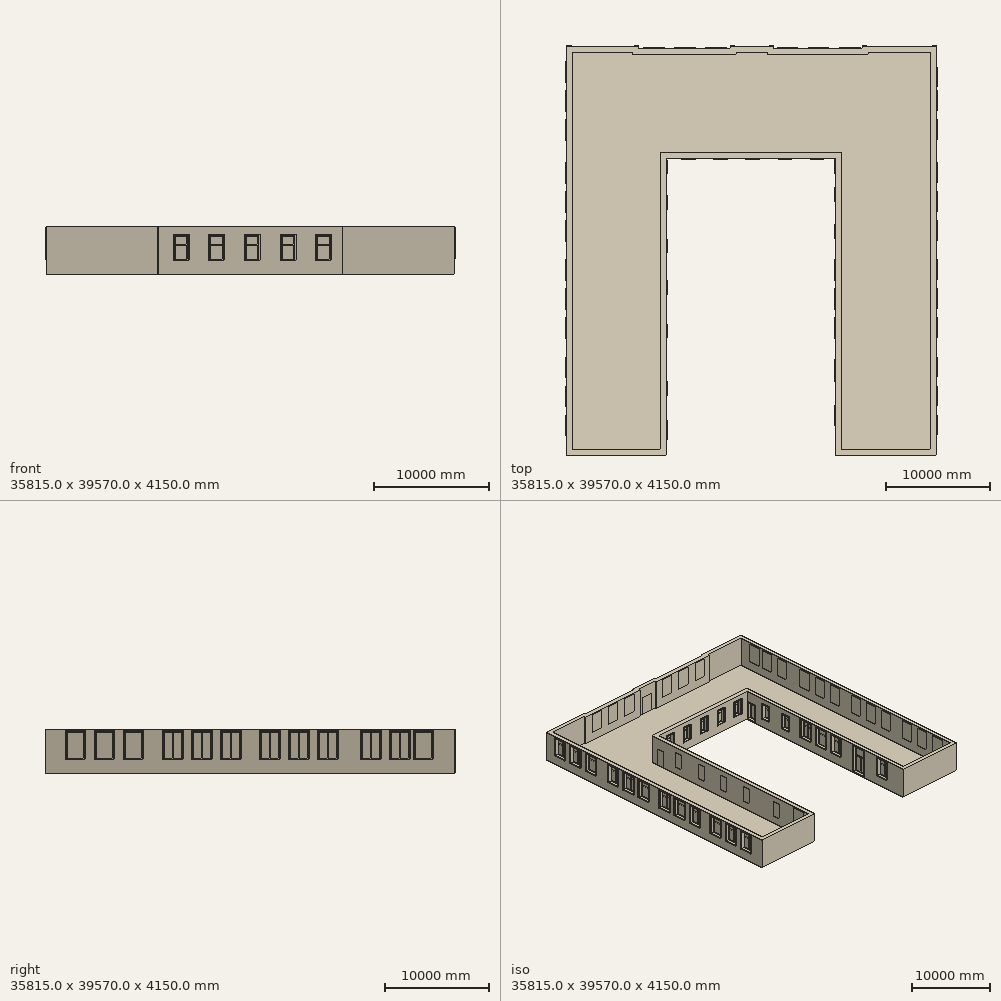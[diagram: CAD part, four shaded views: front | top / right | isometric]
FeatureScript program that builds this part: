
annotation { "Feature Type Name" : "Feature", "Feature Type Description" : "" }
export const myFeature = defineFeature(function(context is Context, id is Id, definition is map)
    precondition{}
    {
        {
            var Q0;
            Q0=qCreatedBy(makeId("Top.planeOp"),FACE);
            var sketch = newSketch(context, id + "F0", { "sketchPlane" : qUnion([Q0])});
            skLineSegment(sketch, "E0", {"start": v(0, 0) * mm, "end": v(0, 39360) * mm});
            skLineSegment(sketch, "E1", {"start": v(0, 39360) * mm, "end": v(-7000, 39360) * mm});
            skLineSegment(sketch, "E2", {"start": v(-7000, 39360) * mm, "end": v(-7000, 39160) * mm});
            skLineSegment(sketch, "E3", {"start": v(-7000, 39160) * mm, "end": v(-15730, 39160) * mm});
            skLineSegment(sketch, "E4", {"start": v(-15730, 39160) * mm, "end": v(-15730, 39360) * mm});
            skLineSegment(sketch, "E5", {"start": v(-15730, 39360) * mm, "end": v(-19730, 39360) * mm});
            skLineSegment(sketch, "E6", {"start": v(-19730, 39360) * mm, "end": v(-19730, 39160) * mm});
            skLineSegment(sketch, "E7", {"start": v(-19730, 39160) * mm, "end": v(-28730, 39160) * mm});
            skLineSegment(sketch, "E8", {"start": v(-28730, 39160) * mm, "end": v(-28730, 39360) * mm});
            skLineSegment(sketch, "E9", {"start": v(-28730, 39360) * mm, "end": v(-35480, 39360) * mm});
            skLineSegment(sketch, "E10", {"start": v(-35480, 39360) * mm, "end": v(-35480, 0) * mm});
            skLineSegment(sketch, "E11", {"start": v(-35480, 0) * mm, "end": v(-26000, 0) * mm});
            skLineSegment(sketch, "E12", {"start": v(-26000, 0) * mm, "end": v(-26000, 28660) * mm});
            skLineSegment(sketch, "E13", {"start": v(-26000, 28660) * mm, "end": v(-9600, 28660) * mm});
            skLineSegment(sketch, "E14", {"start": v(-9600, 28660) * mm, "end": v(-9600, 0) * mm});
            skLineSegment(sketch, "E15", {"start": v(-9600, 0) * mm, "end": v(0, 0) * mm});
            skLineSegment(sketch, "E16.0", {"start": v(-500, 500) * mm, "end": v(-500, 38860) * mm});
            skLineSegment(sketch, "E16.1", {"start": v(-9100, 500) * mm, "end": v(-500, 500) * mm});
            skLineSegment(sketch, "E16.2", {"start": v(-9100, 29160) * mm, "end": v(-9100, 500) * mm});
            skLineSegment(sketch, "E16.3", {"start": v(-26500, 29160) * mm, "end": v(-9100, 29160) * mm});
            skLineSegment(sketch, "E16.4", {"start": v(-26500, 500) * mm, "end": v(-26500, 29160) * mm});
            skLineSegment(sketch, "E16.5", {"start": v(-16230, 38860) * mm, "end": v(-19230, 38860) * mm});
            skLineSegment(sketch, "E16.6", {"start": v(-16230, 38660) * mm, "end": v(-16230, 38860) * mm});
            skLineSegment(sketch, "E16.7", {"start": v(-6500, 38660) * mm, "end": v(-16230, 38660) * mm});
            skLineSegment(sketch, "E16.8", {"start": v(-6500, 38860) * mm, "end": v(-6500, 38660) * mm});
            skLineSegment(sketch, "E16.9", {"start": v(-19230, 38860) * mm, "end": v(-19230, 38660) * mm});
            skLineSegment(sketch, "E16.10", {"start": v(-19230, 38660) * mm, "end": v(-29230, 38660) * mm});
            skLineSegment(sketch, "E16.11", {"start": v(-29230, 38660) * mm, "end": v(-29230, 38860) * mm});
            skLineSegment(sketch, "E16.12", {"start": v(-29230, 38860) * mm, "end": v(-34980, 38860) * mm});
            skLineSegment(sketch, "E16.13", {"start": v(-34980, 38860) * mm, "end": v(-34980, 500) * mm});
            skLineSegment(sketch, "E16.14", {"start": v(-500, 38860) * mm, "end": v(-6500, 38860) * mm});
            skLineSegment(sketch, "E16.15", {"start": v(-34980, 500) * mm, "end": v(-26500, 500) * mm});
            skLineSegment(sketch, "E17.0", {"start": v(-28640, 39250) * mm, "end": v(-28640, 39450) * mm});
            skLineSegment(sketch, "E17.1", {"start": v(-19820, 39250) * mm, "end": v(-28640, 39250) * mm});
            skLineSegment(sketch, "E17.2", {"start": v(-19820, 39450) * mm, "end": v(-19820, 39250) * mm});
            skLineSegment(sketch, "E17.3", {"start": v(-15640, 39450) * mm, "end": v(-19820, 39450) * mm});
            skLineSegment(sketch, "E17.4", {"start": v(-15640, 39250) * mm, "end": v(-15640, 39450) * mm});
            skLineSegment(sketch, "E17.5", {"start": v(-25910, 28570) * mm, "end": v(-9690, 28570) * mm});
            skLineSegment(sketch, "E17.6", {"start": v(-25910, -90) * mm, "end": v(-25910, 28570) * mm});
            skLineSegment(sketch, "E17.7", {"start": v(-35570, -90) * mm, "end": v(-25910, -90) * mm});
            skLineSegment(sketch, "E17.8", {"start": v(-35570, 39450) * mm, "end": v(-35570, -90) * mm});
            skLineSegment(sketch, "E17.9", {"start": v(-9690, 28570) * mm, "end": v(-9690, -90) * mm});
            skLineSegment(sketch, "E17.10", {"start": v(-9690, -90) * mm, "end": v(90, -90) * mm});
            skLineSegment(sketch, "E17.11", {"start": v(90, -90) * mm, "end": v(90, 39450) * mm});
            skLineSegment(sketch, "E17.12", {"start": v(90, 39450) * mm, "end": v(-7090, 39450) * mm});
            skLineSegment(sketch, "E17.13", {"start": v(-7090, 39450) * mm, "end": v(-7090, 39250) * mm});
            skLineSegment(sketch, "E17.14", {"start": v(-28640, 39450) * mm, "end": v(-35570, 39450) * mm});
            skLineSegment(sketch, "E17.15", {"start": v(-7090, 39250) * mm, "end": v(-15640, 39250) * mm});
            skSolve(sketch);
        }
        {
            var Q0;
            Q0=qSketchRegion(id+"F0",true);
            var Q1;
            Q1=makeQuery(id+"F0.imprint","IMPRINT",FACE,{"disambiguationData":[TD([[makeQuery(id+"F0.imprint","IMPRINT",EDGE,{"derivedFrom":sQuery(id+"F0.wireOp",EDGE,"E0")}),1.0]])]});
            extrude(context, id + "F1", {"entities" : qUnion([Q0, Q1]), "depth" : 4000 * mm, "offsetDistance" : 25 * mm});
        }
        {
            var Q0;
            Q0=makeQuery(id+"F1.opExtrude","CAP_FACE",FACE,{"disambiguationData":[OSD([sQuery(id+"F0.wireOp",EDGE,"E16.0"),sQuery(id+"F0.wireOp",EDGE,"E16.1"),sQuery(id+"F0.wireOp",EDGE,"E16.2"),sQuery(id+"F0.wireOp",EDGE,"E16.3"),sQuery(id+"F0.wireOp",EDGE,"E16.4"),sQuery(id+"F0.wireOp",EDGE,"E16.5"),sQuery(id+"F0.wireOp",EDGE,"E16.6"),sQuery(id+"F0.wireOp",EDGE,"E16.7"),sQuery(id+"F0.wireOp",EDGE,"E16.8"),sQuery(id+"F0.wireOp",EDGE,"E16.9"),sQuery(id+"F0.wireOp",EDGE,"E16.10"),sQuery(id+"F0.wireOp",EDGE,"E16.11"),sQuery(id+"F0.wireOp",EDGE,"E16.12"),sQuery(id+"F0.wireOp",EDGE,"E16.13"),sQuery(id+"F0.wireOp",EDGE,"E16.14"),sQuery(id+"F0.wireOp",EDGE,"E16.15"),sQuery(id+"F0.wireOp",EDGE,"E17.0"),sQuery(id+"F0.wireOp",EDGE,"E17.1"),sQuery(id+"F0.wireOp",EDGE,"E17.2"),sQuery(id+"F0.wireOp",EDGE,"E17.3"),sQuery(id+"F0.wireOp",EDGE,"E17.4"),sQuery(id+"F0.wireOp",EDGE,"E17.5"),sQuery(id+"F0.wireOp",EDGE,"E17.6"),sQuery(id+"F0.wireOp",EDGE,"E17.7"),sQuery(id+"F0.wireOp",EDGE,"E17.8"),sQuery(id+"F0.wireOp",EDGE,"E17.9"),sQuery(id+"F0.wireOp",EDGE,"E17.10"),sQuery(id+"F0.wireOp",EDGE,"E17.11"),sQuery(id+"F0.wireOp",EDGE,"E17.12"),sQuery(id+"F0.wireOp",EDGE,"E17.13"),sQuery(id+"F0.wireOp",EDGE,"E17.14"),sQuery(id+"F0.wireOp",EDGE,"E17.15")])],"isStart":false});
            var sketch = newSketch(context, id + "F2", { "sketchPlane" : qUnion([Q0])});
            skLineSegment(sketch, "E18.0.0", {"start": v(-9690, 28570) * mm, "end": v(-9690, -90) * mm});
            skLineSegment(sketch, "E18.0.1", {"start": v(-9690, -90) * mm, "end": v(90, -90) * mm});
            skLineSegment(sketch, "E18.0.2", {"start": v(90, -90) * mm, "end": v(90, 39450) * mm});
            skLineSegment(sketch, "E18.0.3", {"start": v(90, 39450) * mm, "end": v(-7090, 39450) * mm});
            skLineSegment(sketch, "E18.0.4", {"start": v(-7090, 39450) * mm, "end": v(-7090, 39250) * mm});
            skLineSegment(sketch, "E18.0.5", {"start": v(-7090, 39250) * mm, "end": v(-15640, 39250) * mm});
            skLineSegment(sketch, "E18.0.6", {"start": v(-15640, 39250) * mm, "end": v(-15640, 39450) * mm});
            skLineSegment(sketch, "E18.0.7", {"start": v(-15640, 39450) * mm, "end": v(-19820, 39450) * mm});
            skLineSegment(sketch, "E18.0.8", {"start": v(-19820, 39450) * mm, "end": v(-19820, 39250) * mm});
            skLineSegment(sketch, "E18.0.9", {"start": v(-19820, 39250) * mm, "end": v(-28640, 39250) * mm});
            skLineSegment(sketch, "E18.0.10", {"start": v(-28640, 39250) * mm, "end": v(-28640, 39450) * mm});
            skLineSegment(sketch, "E18.0.11", {"start": v(-28640, 39450) * mm, "end": v(-35570, 39450) * mm});
            skLineSegment(sketch, "E18.0.12", {"start": v(-35570, 39450) * mm, "end": v(-35570, -90) * mm});
            skLineSegment(sketch, "E18.0.13", {"start": v(-35570, -90) * mm, "end": v(-25910, -90) * mm});
            skLineSegment(sketch, "E18.0.14", {"start": v(-25910, -90) * mm, "end": v(-25910, 28570) * mm});
            skLineSegment(sketch, "E18.0.15", {"start": v(-25910, 28570) * mm, "end": v(-9690, 28570) * mm});
            skLineSegment(sketch, "E19.0", {"start": v(-19810, 39440) * mm, "end": v(-19810, 39240) * mm});
            skLineSegment(sketch, "E19.1", {"start": v(-15650, 39440) * mm, "end": v(-19810, 39440) * mm});
            skLineSegment(sketch, "E19.2", {"start": v(-15650, 39240) * mm, "end": v(-15650, 39440) * mm});
            skLineSegment(sketch, "E19.3", {"start": v(-7080, 39240) * mm, "end": v(-15650, 39240) * mm});
            skLineSegment(sketch, "E19.4", {"start": v(-7080, 39440) * mm, "end": v(-7080, 39240) * mm});
            skLineSegment(sketch, "E19.5", {"start": v(-35560, -80) * mm, "end": v(-25920, -80) * mm});
            skLineSegment(sketch, "E19.6", {"start": v(-35560, 39440) * mm, "end": v(-35560, -80) * mm});
            skLineSegment(sketch, "E19.7", {"start": v(-28650, 39440) * mm, "end": v(-35560, 39440) * mm});
            skLineSegment(sketch, "E19.8", {"start": v(-28650, 39240) * mm, "end": v(-28650, 39440) * mm});
            skLineSegment(sketch, "E19.9", {"start": v(-25920, -80) * mm, "end": v(-25920, 28580) * mm});
            skLineSegment(sketch, "E19.10", {"start": v(-25920, 28580) * mm, "end": v(-9680, 28580) * mm});
            skLineSegment(sketch, "E19.11", {"start": v(-9680, 28580) * mm, "end": v(-9680, -80) * mm});
            skLineSegment(sketch, "E19.12", {"start": v(-9680, -80) * mm, "end": v(80, -80) * mm});
            skLineSegment(sketch, "E19.13", {"start": v(80, -80) * mm, "end": v(80, 39440) * mm});
            skLineSegment(sketch, "E19.14", {"start": v(-19810, 39240) * mm, "end": v(-28650, 39240) * mm});
            skLineSegment(sketch, "E19.15", {"start": v(80, 39440) * mm, "end": v(-7080, 39440) * mm});
            skSolve(sketch);
        }
        {
            var Q0;
            Q0 = qSketchRegion(id + "F2", true);
            var Q1;
            Q1=makeQuery(id+"F1.opExtrude","CAP_VERTEX",VERTEX,{"disambiguationData":[OSD([sQuery(id+"F0.wireOp",EDGE,"E17.8"),sQuery(id+"F0.wireOp",EDGE,"E17.14")])],"isStart":true});
            extrude(context, id + "F3", {"entities" : qUnion([Q0]), "operationType" : NewBodyOperationType.REMOVE, "endBound" : BoundingType.UP_TO_VERTEX, "oppositeDirection" : true, "depth" : 25 * mm, "endBoundEntityVertex" : qUnion([Q1]), "offsetDistance" : 25 * mm});
        }
        {
            var Q0;
            Q0=makeQuery(id+"F1.opExtrude","CAP_FACE",FACE,{"disambiguationData":[OSD([sQuery(id+"F0.wireOp",EDGE,"E0"),sQuery(id+"F0.wireOp",EDGE,"E1"),sQuery(id+"F0.wireOp",EDGE,"E2"),sQuery(id+"F0.wireOp",EDGE,"E3"),sQuery(id+"F0.wireOp",EDGE,"E4"),sQuery(id+"F0.wireOp",EDGE,"E5"),sQuery(id+"F0.wireOp",EDGE,"E6"),sQuery(id+"F0.wireOp",EDGE,"E7"),sQuery(id+"F0.wireOp",EDGE,"E8"),sQuery(id+"F0.wireOp",EDGE,"E9"),sQuery(id+"F0.wireOp",EDGE,"E10"),sQuery(id+"F0.wireOp",EDGE,"E11"),sQuery(id+"F0.wireOp",EDGE,"E12"),sQuery(id+"F0.wireOp",EDGE,"E13"),sQuery(id+"F0.wireOp",EDGE,"E14"),sQuery(id+"F0.wireOp",EDGE,"E15"),sQuery(id+"F0.wireOp",EDGE,"E16.0"),sQuery(id+"F0.wireOp",EDGE,"E16.1"),sQuery(id+"F0.wireOp",EDGE,"E16.2"),sQuery(id+"F0.wireOp",EDGE,"E16.3"),sQuery(id+"F0.wireOp",EDGE,"E16.4"),sQuery(id+"F0.wireOp",EDGE,"E16.5"),sQuery(id+"F0.wireOp",EDGE,"E16.6"),sQuery(id+"F0.wireOp",EDGE,"E16.7"),sQuery(id+"F0.wireOp",EDGE,"E16.8"),sQuery(id+"F0.wireOp",EDGE,"E16.9"),sQuery(id+"F0.wireOp",EDGE,"E16.10"),sQuery(id+"F0.wireOp",EDGE,"E16.11"),sQuery(id+"F0.wireOp",EDGE,"E16.12"),sQuery(id+"F0.wireOp",EDGE,"E16.13"),sQuery(id+"F0.wireOp",EDGE,"E16.14"),sQuery(id+"F0.wireOp",EDGE,"E16.15")])],"isStart":true});
            var sketch = newSketch(context, id + "F4", { "sketchPlane" : qUnion([Q0])});
            skLineSegment(sketch, "E20", {"start": v(-35560, -39440) * mm, "end": v(-35560, 80) * mm});
            skLineSegment(sketch, "E21", {"start": v(-15650, -39440) * mm, "end": v(-19810, -39440) * mm});
            skLineSegment(sketch, "E22", {"start": v(-19810, -39440) * mm, "end": v(-19810, -39240) * mm});
            skLineSegment(sketch, "E23", {"start": v(-19810, -39240) * mm, "end": v(-28650, -39240) * mm});
            skLineSegment(sketch, "E24", {"start": v(-28650, -39240) * mm, "end": v(-28650, -39440) * mm});
            skLineSegment(sketch, "E25", {"start": v(-28650, -39440) * mm, "end": v(-35560, -39440) * mm});
            skLineSegment(sketch, "E26.0", {"start": v(-15650, -39240) * mm, "end": v(-15650, -39440) * mm});
            skLineSegment(sketch, "E27.0", {"start": v(-7080, -39240) * mm, "end": v(-15650, -39240) * mm});
            skLineSegment(sketch, "E28.0", {"start": v(-7080, -39440) * mm, "end": v(-7080, -39240) * mm});
            skLineSegment(sketch, "E29.0", {"start": v(80, -39440) * mm, "end": v(-7080, -39440) * mm});
            skLineSegment(sketch, "E30.0", {"start": v(80, 80) * mm, "end": v(80, -39440) * mm});
            skLineSegment(sketch, "E31.0", {"start": v(-9680, 80) * mm, "end": v(80, 80) * mm});
            skLineSegment(sketch, "E32.0", {"start": v(-9680, -28580) * mm, "end": v(-9680, 80) * mm});
            skLineSegment(sketch, "E33.0", {"start": v(-25920, -28580) * mm, "end": v(-9680, -28580) * mm});
            skLineSegment(sketch, "E34.0", {"start": v(-25920, 80) * mm, "end": v(-25920, -28580) * mm});
            skLineSegment(sketch, "E35.0", {"start": v(-35560, 80) * mm, "end": v(-25920, 80) * mm});
            skSolve(sketch);
        }
        {
            var Q0;
            {var subQ0=makeQuery(id+"F1.opExtrude","CAP_EDGE",EDGE,{"disambiguationData":[OSD([sQuery(id+"F0.wireOp",EDGE,"E16.10")])],"isStart":true});Q0=makeQuery(id+"F4.imprint","IMPRINT",FACE,{"disambiguationData":[TD([[makeQuery(id+"F4.imprint","IMPRINT",EDGE,{"derivedFrom":subQ0}),-1.0]])]});}
            var Q1;
            {var subQ8=sQuery(id+"F4.wireOp",EDGE,"E20");Q1=makeQuery(id+"F4.imprint","IMPRINT",FACE,{"disambiguationData":[TD([[makeQuery(id+"F4.imprint","IMPRINT",EDGE,{"derivedFrom":subQ8}),-1.0]])]});}
            var Q2;
            {var subQ5=sQuery(id+"F4.wireOp",EDGE,"WrZoUcTY-9wdJ-lOnS-oAZQ-S74aqCpjquS9");var subQ6=makeQuery(id+"F4.imprint","INTERSECT",VERTEX,{"derivedFrom":[makeQuery(id+"F1.opExtrude","CAP_EDGE",EDGE,{"disambiguationData":[OSD([sQuery(id+"F0.wireOp",EDGE,"E12")])],"isStart":true}),subQ5]});Q2=makeQuery(id+"F4.imprint","IMPRINT",FACE,{"disambiguationData":[TD([[makeQuery(id+"F4.imprint","IMPRINT",EDGE,{"disambiguationData":[TD([[subQ6,1.0]])],"derivedFrom":subQ5}),-1.0]])]});}
            extrude(context, id + "F5", {"entities" : qUnion([Q0, Q1, Q2]), "operationType" : NewBodyOperationType.ADD, "depth" : 150 * mm, "offsetDistance" : 25 * mm});
        }
        {
            var Q0;
            Q0=makeQuery(id+"F5.boolean.opBoolean","MERGE",FACE,{"derivedFrom":[makeQuery(id+"F1.opExtrude","SWEPT_FACE",FACE,{"disambiguationData":[OSD([sQuery(id+"F0.wireOp",EDGE,"E7")])]}),makeQuery(id+"F5.opExtrude","SWEPT_FACE",FACE,{"disambiguationData":[OSD([sQuery(id+"F4.wireOp",EDGE,"E23")])]})]});
            var sketch = newSketch(context, id + "F6", { "sketchPlane" : qUnion([Q0])});
            skLineSegment(sketch, "E36.bottom", {"start": v(20330, 3800) * mm, "end": v(22030, 3800) * mm});
            skLineSegment(sketch, "E36.top", {"start": v(20330, 1200) * mm, "end": v(22030, 1200) * mm});
            skLineSegment(sketch, "E36.left", {"start": v(20330, 3800) * mm, "end": v(20330, 1200) * mm});
            skLineSegment(sketch, "E36.right", {"start": v(22030, 3800) * mm, "end": v(22030, 1200) * mm});
            skLineSegment(sketch, "E37.bottom", {"start": v(23330, 3800) * mm, "end": v(25030, 3800) * mm});
            skLineSegment(sketch, "E37.top", {"start": v(23330, 1200) * mm, "end": v(25030, 1200) * mm});
            skLineSegment(sketch, "E37.left", {"start": v(23330, 3800) * mm, "end": v(23330, 1200) * mm});
            skLineSegment(sketch, "E37.right", {"start": v(25030, 3800) * mm, "end": v(25030, 1200) * mm});
            skLineSegment(sketch, "E38.bottom", {"start": v(26330, 3800) * mm, "end": v(28030, 3800) * mm});
            skLineSegment(sketch, "E38.top", {"start": v(26330, 1200) * mm, "end": v(28030, 1200) * mm});
            skLineSegment(sketch, "E38.left", {"start": v(26330, 3800) * mm, "end": v(26330, 1200) * mm});
            skLineSegment(sketch, "E38.right", {"start": v(28030, 3800) * mm, "end": v(28030, 1200) * mm});
            skLineSegment(sketch, "E39", {"start": v(17730, -150) * mm, "end": v(17730, 3306.36) * mm, "construction": true});
            skLineSegment(sketch, "E40.MirrorCS", {"start": v(15130, 3800) * mm, "end": v(15130, 1200) * mm});
            skLineSegment(sketch, "E41.MirrorCS", {"start": v(7430, 3800) * mm, "end": v(7430, 1200) * mm});
            skLineSegment(sketch, "E42.MirrorCS", {"start": v(10430, 3800) * mm, "end": v(10430, 1200) * mm});
            skLineSegment(sketch, "E43.MirrorCS", {"start": v(9130, 3800) * mm, "end": v(9130, 1200) * mm});
            skLineSegment(sketch, "E44.MirrorCS", {"start": v(9130, 3800) * mm, "end": v(7430, 3800) * mm});
            skLineSegment(sketch, "E45.MirrorCS", {"start": v(12130, 3800) * mm, "end": v(12130, 1200) * mm});
            skLineSegment(sketch, "E46.MirrorCS", {"start": v(12130, 1200) * mm, "end": v(10430, 1200) * mm});
            skLineSegment(sketch, "E47.MirrorCS", {"start": v(15130, 3800) * mm, "end": v(13430, 3800) * mm});
            skLineSegment(sketch, "E48.MirrorCS", {"start": v(15130, 1200) * mm, "end": v(13430, 1200) * mm});
            skLineSegment(sketch, "E49.MirrorCS", {"start": v(9130, 1200) * mm, "end": v(7430, 1200) * mm});
            skLineSegment(sketch, "E50.MirrorCS", {"start": v(13430, 3800) * mm, "end": v(13430, 1200) * mm});
            skLineSegment(sketch, "E51.MirrorCS", {"start": v(12130, 3800) * mm, "end": v(10430, 3800) * mm});
            skSolve(sketch);
        }
        {
            var Q0;
            Q0=qSketchRegion(id+"F6",true);
            extrude(context, id + "F7", {"entities" : qUnion([Q0]), "operationType" : NewBodyOperationType.REMOVE, "oppositeDirection" : true, "depth" : 590 * mm, "offsetDistance" : 25 * mm});
        }
        {
            var Q0;
            Q0=makeQuery(id+"F1.opExtrude","SWEPT_FACE",FACE,{"disambiguationData":[OSD([sQuery(id+"F0.wireOp",EDGE,"E16.10")])]});
            var sketch = newSketch(context, id + "F8", { "sketchPlane" : qUnion([Q0])});
            skLineSegment(sketch, "E52.0", {"start": v(-20330, 3800) * mm, "end": v(-22030, 3800) * mm});
            skLineSegment(sketch, "E53.0", {"start": v(-20330, 3800) * mm, "end": v(-20330, 1200) * mm});
            skLineSegment(sketch, "E54.0", {"start": v(-20330, 1200) * mm, "end": v(-22030, 1200) * mm});
            skLineSegment(sketch, "E55.0", {"start": v(-22030, 3800) * mm, "end": v(-22030, 1200) * mm});
            skLineSegment(sketch, "E56.0", {"start": v(-23330, 3800) * mm, "end": v(-23330, 1200) * mm});
            skLineSegment(sketch, "E57.0", {"start": v(-23330, 3800) * mm, "end": v(-25030, 3800) * mm});
            skLineSegment(sketch, "E58.0", {"start": v(-25030, 3800) * mm, "end": v(-25030, 1200) * mm});
            skLineSegment(sketch, "E59.0", {"start": v(-23330, 1200) * mm, "end": v(-25030, 1200) * mm});
            skLineSegment(sketch, "E60.0", {"start": v(-26330, 3800) * mm, "end": v(-28030, 3800) * mm});
            skLineSegment(sketch, "E61.0", {"start": v(-28030, 3800) * mm, "end": v(-28030, 1200) * mm});
            skLineSegment(sketch, "E62.0", {"start": v(-26330, 1200) * mm, "end": v(-28030, 1200) * mm});
            skLineSegment(sketch, "E63.0", {"start": v(-26330, 3800) * mm, "end": v(-26330, 1200) * mm});
            skLineSegment(sketch, "E64.0", {"start": v(-9130, 1200) * mm, "end": v(-7430, 1200) * mm});
            skLineSegment(sketch, "E65.0", {"start": v(-7430, 3800) * mm, "end": v(-7430, 1200) * mm});
            skLineSegment(sketch, "E66.0", {"start": v(-9130, 3800) * mm, "end": v(-7430, 3800) * mm});
            skLineSegment(sketch, "E67.0", {"start": v(-9130, 3800) * mm, "end": v(-9130, 1200) * mm});
            skLineSegment(sketch, "E68.0", {"start": v(-12130, 1200) * mm, "end": v(-10430, 1200) * mm});
            skLineSegment(sketch, "E69.0", {"start": v(-10430, 3800) * mm, "end": v(-10430, 1200) * mm});
            skLineSegment(sketch, "E70.0", {"start": v(-12130, 3800) * mm, "end": v(-10430, 3800) * mm});
            skLineSegment(sketch, "E71.0", {"start": v(-12130, 3800) * mm, "end": v(-12130, 1200) * mm});
            skLineSegment(sketch, "E72.0", {"start": v(-15130, 1200) * mm, "end": v(-13430, 1200) * mm});
            skLineSegment(sketch, "E73.0", {"start": v(-13430, 3800) * mm, "end": v(-13430, 1200) * mm});
            skLineSegment(sketch, "E74.0", {"start": v(-15130, 3800) * mm, "end": v(-13430, 3800) * mm});
            skLineSegment(sketch, "E75.0", {"start": v(-15130, 3800) * mm, "end": v(-15130, 1200) * mm});
            skSolve(sketch);
        }
        {
            var Q0;
            Q0=qSketchRegion(id+"F8",true);
            extrude(context, id + "F9", {"entities" : qUnion([Q0]), "oppositeDirection" : true, "depth" : 5 * mm, "offsetDistance" : 25 * mm});
        }
        {
            var Q0;
            Q0=makeQuery(id+"F9.opExtrude","CAP_FACE",FACE,{"disambiguationData":[OSD([sQuery(id+"F8.wireOp",EDGE,"E60.0"),sQuery(id+"F8.wireOp",EDGE,"E61.0"),sQuery(id+"F8.wireOp",EDGE,"E62.0"),sQuery(id+"F8.wireOp",EDGE,"E63.0")])],"isStart":false});
            var sketch = newSketch(context, id + "F10", { "sketchPlane" : qUnion([Q0])});
            skLineSegment(sketch, "E76.0.0", {"start": v(9130, 3800) * mm, "end": v(7430, 3800) * mm});
            skLineSegment(sketch, "E76.0.1", {"start": v(7430, 3800) * mm, "end": v(7430, 1200) * mm});
            skLineSegment(sketch, "E76.0.2", {"start": v(7430, 1200) * mm, "end": v(9130, 1200) * mm});
            skLineSegment(sketch, "E76.0.3", {"start": v(9130, 1200) * mm, "end": v(9130, 3800) * mm});
            skLineSegment(sketch, "E77", {"start": v(8280, 3800) * mm, "end": v(8280, 1200) * mm, "construction": true});
            skLineSegment(sketch, "E78.bottom", {"start": v(7480, 2850) * mm, "end": v(8242.5, 2850) * mm});
            skLineSegment(sketch, "E78.top", {"start": v(7480, 1250) * mm, "end": v(8242.5, 1250) * mm});
            skLineSegment(sketch, "E78.left", {"start": v(7480, 2850) * mm, "end": v(7480, 1250) * mm});
            skLineSegment(sketch, "E78.right", {"start": v(8242.5, 2850) * mm, "end": v(8242.5, 1250) * mm});
            skLineSegment(sketch, "E79.bottom", {"start": v(7480, 2900) * mm, "end": v(8242.5, 2900) * mm});
            skLineSegment(sketch, "E79.top", {"start": v(7480, 3750) * mm, "end": v(8242.5, 3750) * mm});
            skLineSegment(sketch, "E79.left", {"start": v(7480, 2900) * mm, "end": v(7480, 3750) * mm});
            skLineSegment(sketch, "E79.right", {"start": v(8242.5, 2900) * mm, "end": v(8242.5, 3750) * mm});
            skLineSegment(sketch, "E80.MirrorCS", {"start": v(9080, 3750) * mm, "end": v(8317.5, 3750) * mm});
            skLineSegment(sketch, "E81.MirrorCS", {"start": v(9080, 2900) * mm, "end": v(9080, 3750) * mm});
            skLineSegment(sketch, "E82.MirrorCS", {"start": v(8317.5, 2900) * mm, "end": v(8317.5, 3750) * mm});
            skLineSegment(sketch, "E83.MirrorCS", {"start": v(9080, 2900) * mm, "end": v(8317.5, 2900) * mm});
            skLineSegment(sketch, "E84.MirrorCS", {"start": v(9080, 2850) * mm, "end": v(8317.5, 2850) * mm});
            skLineSegment(sketch, "E85.MirrorCS", {"start": v(8317.5, 2850) * mm, "end": v(8317.5, 1250) * mm});
            skLineSegment(sketch, "E86.MirrorCS", {"start": v(9080, 2850) * mm, "end": v(9080, 1250) * mm});
            skLineSegment(sketch, "E87.MirrorCS", {"start": v(9080, 1250) * mm, "end": v(8317.5, 1250) * mm});
            skLineSegment(sketch, "E88.0.0", {"start": v(12129.64, 3800) * mm, "end": v(10429.64, 3800) * mm});
            skLineSegment(sketch, "E88.0.1", {"start": v(10429.64, 3800) * mm, "end": v(10429.64, 1200) * mm});
            skLineSegment(sketch, "E88.0.2", {"start": v(10429.64, 1200) * mm, "end": v(12129.64, 1200) * mm});
            skLineSegment(sketch, "E88.0.3", {"start": v(12129.64, 1200) * mm, "end": v(12129.64, 3800) * mm});
            skLineSegment(sketch, "E89", {"start": v(11279.64, 3800) * mm, "end": v(11279.64, 1200) * mm, "construction": true});
            skLineSegment(sketch, "E90.bottom", {"start": v(10479.64, 2850) * mm, "end": v(11242.14, 2850) * mm});
            skLineSegment(sketch, "E90.top", {"start": v(10479.64, 1250) * mm, "end": v(11242.14, 1250) * mm});
            skLineSegment(sketch, "E90.left", {"start": v(10479.64, 2850) * mm, "end": v(10479.64, 1250) * mm});
            skLineSegment(sketch, "E90.right", {"start": v(11242.14, 2850) * mm, "end": v(11242.14, 1250) * mm});
            skLineSegment(sketch, "E91.bottom", {"start": v(10479.64, 2900) * mm, "end": v(11242.14, 2900) * mm});
            skLineSegment(sketch, "E91.top", {"start": v(10479.64, 3750) * mm, "end": v(11242.14, 3750) * mm});
            skLineSegment(sketch, "E91.left", {"start": v(10479.64, 2900) * mm, "end": v(10479.64, 3750) * mm});
            skLineSegment(sketch, "E91.right", {"start": v(11242.14, 2900) * mm, "end": v(11242.14, 3750) * mm});
            skLineSegment(sketch, "E92.MirrorCS", {"start": v(12079.64, 3750) * mm, "end": v(11317.14, 3750) * mm});
            skLineSegment(sketch, "E93.MirrorCS", {"start": v(12079.64, 2900) * mm, "end": v(12079.64, 3750) * mm});
            skLineSegment(sketch, "E94.MirrorCS", {"start": v(11317.14, 2900) * mm, "end": v(11317.14, 3750) * mm});
            skLineSegment(sketch, "E95.MirrorCS", {"start": v(12079.64, 2900) * mm, "end": v(11317.14, 2900) * mm});
            skLineSegment(sketch, "E96.MirrorCS", {"start": v(12079.64, 2850) * mm, "end": v(11317.14, 2850) * mm});
            skLineSegment(sketch, "E97.MirrorCS", {"start": v(11317.14, 2850) * mm, "end": v(11317.14, 1250) * mm});
            skLineSegment(sketch, "E98.MirrorCS", {"start": v(12079.64, 2850) * mm, "end": v(12079.64, 1250) * mm});
            skLineSegment(sketch, "E99.MirrorCS", {"start": v(12079.64, 1250) * mm, "end": v(11317.14, 1250) * mm});
            skLineSegment(sketch, "E100.0.0", {"start": v(15130, 3800) * mm, "end": v(13430, 3800) * mm});
            skLineSegment(sketch, "E100.0.1", {"start": v(13430, 3800) * mm, "end": v(13430, 1200) * mm});
            skLineSegment(sketch, "E100.0.2", {"start": v(13430, 1200) * mm, "end": v(15130, 1200) * mm});
            skLineSegment(sketch, "E100.0.3", {"start": v(15130, 1200) * mm, "end": v(15130, 3800) * mm});
            skLineSegment(sketch, "E101", {"start": v(14280, 3800) * mm, "end": v(14280, 1200) * mm, "construction": true});
            skLineSegment(sketch, "E102.bottom", {"start": v(13480, 2850) * mm, "end": v(14242.5, 2850) * mm});
            skLineSegment(sketch, "E102.top", {"start": v(13480, 1250) * mm, "end": v(14242.5, 1250) * mm});
            skLineSegment(sketch, "E102.left", {"start": v(13480, 2850) * mm, "end": v(13480, 1250) * mm});
            skLineSegment(sketch, "E102.right", {"start": v(14242.5, 2850) * mm, "end": v(14242.5, 1250) * mm});
            skLineSegment(sketch, "E103.bottom", {"start": v(13480, 2900) * mm, "end": v(14242.5, 2900) * mm});
            skLineSegment(sketch, "E103.top", {"start": v(13480, 3750) * mm, "end": v(14242.5, 3750) * mm});
            skLineSegment(sketch, "E103.left", {"start": v(13480, 2900) * mm, "end": v(13480, 3750) * mm});
            skLineSegment(sketch, "E103.right", {"start": v(14242.5, 2900) * mm, "end": v(14242.5, 3750) * mm});
            skLineSegment(sketch, "E104.MirrorCS", {"start": v(15080, 3750) * mm, "end": v(14317.5, 3750) * mm});
            skLineSegment(sketch, "E105.MirrorCS", {"start": v(15080, 2900) * mm, "end": v(15080, 3750) * mm});
            skLineSegment(sketch, "E106.MirrorCS", {"start": v(14317.5, 2900) * mm, "end": v(14317.5, 3750) * mm});
            skLineSegment(sketch, "E107.MirrorCS", {"start": v(15080, 2900) * mm, "end": v(14317.5, 2900) * mm});
            skLineSegment(sketch, "E108.MirrorCS", {"start": v(15080, 2850) * mm, "end": v(14317.5, 2850) * mm});
            skLineSegment(sketch, "E109.MirrorCS", {"start": v(14317.5, 2850) * mm, "end": v(14317.5, 1250) * mm});
            skLineSegment(sketch, "E110.MirrorCS", {"start": v(15080, 2850) * mm, "end": v(15080, 1250) * mm});
            skLineSegment(sketch, "E111.MirrorCS", {"start": v(15080, 1250) * mm, "end": v(14317.5, 1250) * mm});
            skLineSegment(sketch, "E112", {"start": v(17730, -150) * mm, "end": v(17730, 2939.63) * mm, "construction": true});
            skLineSegment(sketch, "E113.MirrorCS", {"start": v(21142.5, 2900) * mm, "end": v(21142.5, 3750) * mm});
            skLineSegment(sketch, "E114.MirrorCS", {"start": v(25030.36, 1200) * mm, "end": v(23330.36, 1200) * mm});
            skLineSegment(sketch, "E115.MirrorCS", {"start": v(27217.5, 2900) * mm, "end": v(27217.5, 3750) * mm});
            skLineSegment(sketch, "E116.MirrorCS", {"start": v(24217.86, 2900) * mm, "end": v(24217.86, 3750) * mm});
            skLineSegment(sketch, "E117.MirrorCS", {"start": v(21980, 2900) * mm, "end": v(21980, 3750) * mm});
            skLineSegment(sketch, "E118.MirrorCS", {"start": v(27217.5, 2850) * mm, "end": v(27217.5, 1250) * mm});
            skLineSegment(sketch, "E119.MirrorCS", {"start": v(21980, 2850) * mm, "end": v(21980, 1250) * mm});
            skLineSegment(sketch, "E120.MirrorCS", {"start": v(21142.5, 2850) * mm, "end": v(21142.5, 1250) * mm});
            skLineSegment(sketch, "E121.MirrorCS", {"start": v(22030, 1200) * mm, "end": v(20330, 1200) * mm});
            skLineSegment(sketch, "E122.MirrorCS", {"start": v(28030, 1200) * mm, "end": v(26330, 1200) * mm});
            skLineSegment(sketch, "E123.MirrorCS", {"start": v(24217.86, 2850) * mm, "end": v(24217.86, 1250) * mm});
            skLineSegment(sketch, "E124.MirrorCS", {"start": v(23380.36, 1250) * mm, "end": v(24142.86, 1250) * mm});
            skLineSegment(sketch, "E125.MirrorCS", {"start": v(27980, 2850) * mm, "end": v(27980, 1250) * mm});
            skLineSegment(sketch, "E126.MirrorCS", {"start": v(27980, 1250) * mm, "end": v(27217.5, 1250) * mm});
            skLineSegment(sketch, "E127.MirrorCS", {"start": v(23380.36, 2850) * mm, "end": v(24142.86, 2850) * mm});
            skLineSegment(sketch, "E128.MirrorCS", {"start": v(24980.36, 3750) * mm, "end": v(24217.86, 3750) * mm});
            skLineSegment(sketch, "E129.MirrorCS", {"start": v(20380, 2900) * mm, "end": v(21142.5, 2900) * mm});
            skLineSegment(sketch, "E130.MirrorCS", {"start": v(23330.36, 3800) * mm, "end": v(25030.36, 3800) * mm});
            skLineSegment(sketch, "E131.MirrorCS", {"start": v(23380.36, 2900) * mm, "end": v(24142.86, 2900) * mm});
            skLineSegment(sketch, "E132.MirrorCS", {"start": v(27980, 3750) * mm, "end": v(27217.5, 3750) * mm});
            skLineSegment(sketch, "E133.MirrorCS", {"start": v(23330.36, 1200) * mm, "end": v(23330.36, 3800) * mm});
            skLineSegment(sketch, "E134.MirrorCS", {"start": v(27980, 2850) * mm, "end": v(27217.5, 2850) * mm});
            skLineSegment(sketch, "E135.MirrorCS", {"start": v(20330, 3800) * mm, "end": v(22030, 3800) * mm});
            skLineSegment(sketch, "E136.MirrorCS", {"start": v(21980, 3750) * mm, "end": v(21217.5, 3750) * mm});
            skLineSegment(sketch, "E137.MirrorCS", {"start": v(21217.5, 2900) * mm, "end": v(21217.5, 3750) * mm});
            skLineSegment(sketch, "E138.MirrorCS", {"start": v(21180, 3800) * mm, "end": v(21180, 1200) * mm, "construction": true});
            skLineSegment(sketch, "E139.MirrorCS", {"start": v(23380.36, 2850) * mm, "end": v(23380.36, 1250) * mm});
            skLineSegment(sketch, "E140.MirrorCS", {"start": v(20330, 1200) * mm, "end": v(20330, 3800) * mm});
            skLineSegment(sketch, "E141.MirrorCS", {"start": v(24142.86, 2900) * mm, "end": v(24142.86, 3750) * mm});
            skLineSegment(sketch, "E142.MirrorCS", {"start": v(24180.36, 3800) * mm, "end": v(24180.36, 1200) * mm, "construction": true});
            skLineSegment(sketch, "E143.MirrorCS", {"start": v(27142.5, 2850) * mm, "end": v(27142.5, 1250) * mm});
            skLineSegment(sketch, "E144.MirrorCS", {"start": v(24980.36, 1250) * mm, "end": v(24217.86, 1250) * mm});
            skLineSegment(sketch, "E145.MirrorCS", {"start": v(26380, 2850) * mm, "end": v(26380, 1250) * mm});
            skLineSegment(sketch, "E146.MirrorCS", {"start": v(27142.5, 2900) * mm, "end": v(27142.5, 3750) * mm});
            skLineSegment(sketch, "E147.MirrorCS", {"start": v(28030, 3800) * mm, "end": v(28030, 1200) * mm});
            skLineSegment(sketch, "E148.MirrorCS", {"start": v(22030, 3800) * mm, "end": v(22030, 1200) * mm});
            skLineSegment(sketch, "E149.MirrorCS", {"start": v(26380, 2900) * mm, "end": v(26380, 3750) * mm});
            skLineSegment(sketch, "E150.MirrorCS", {"start": v(26330, 1200) * mm, "end": v(26330, 3800) * mm});
            skLineSegment(sketch, "E151.MirrorCS", {"start": v(23380.36, 2900) * mm, "end": v(23380.36, 3750) * mm});
            skLineSegment(sketch, "E152.MirrorCS", {"start": v(21980, 2850) * mm, "end": v(21217.5, 2850) * mm});
            skLineSegment(sketch, "E153.MirrorCS", {"start": v(26380, 2900) * mm, "end": v(27142.5, 2900) * mm});
            skLineSegment(sketch, "E154.MirrorCS", {"start": v(20380, 1250) * mm, "end": v(21142.5, 1250) * mm});
            skLineSegment(sketch, "E155.MirrorCS", {"start": v(26380, 3750) * mm, "end": v(27142.5, 3750) * mm});
            skLineSegment(sketch, "E156.MirrorCS", {"start": v(26380, 2850) * mm, "end": v(27142.5, 2850) * mm});
            skLineSegment(sketch, "E157.MirrorCS", {"start": v(24142.86, 2850) * mm, "end": v(24142.86, 1250) * mm});
            skLineSegment(sketch, "E158.MirrorCS", {"start": v(21217.5, 2850) * mm, "end": v(21217.5, 1250) * mm});
            skLineSegment(sketch, "E159.MirrorCS", {"start": v(23380.36, 3750) * mm, "end": v(24142.86, 3750) * mm});
            skLineSegment(sketch, "E160.MirrorCS", {"start": v(24980.36, 2850) * mm, "end": v(24217.86, 2850) * mm});
            skLineSegment(sketch, "E161.MirrorCS", {"start": v(20380, 2850) * mm, "end": v(20380, 1250) * mm});
            skLineSegment(sketch, "E162.MirrorCS", {"start": v(21980, 2900) * mm, "end": v(21217.5, 2900) * mm});
            skLineSegment(sketch, "E163.MirrorCS", {"start": v(24980.36, 2850) * mm, "end": v(24980.36, 1250) * mm});
            skLineSegment(sketch, "E164.MirrorCS", {"start": v(27980, 2900) * mm, "end": v(27217.5, 2900) * mm});
            skLineSegment(sketch, "E165.MirrorCS", {"start": v(26380, 1250) * mm, "end": v(27142.5, 1250) * mm});
            skLineSegment(sketch, "E166.MirrorCS", {"start": v(26330, 3800) * mm, "end": v(28030, 3800) * mm});
            skLineSegment(sketch, "E167.MirrorCS", {"start": v(24980.36, 2900) * mm, "end": v(24217.86, 2900) * mm});
            skLineSegment(sketch, "E168.MirrorCS", {"start": v(27180, 3800) * mm, "end": v(27180, 1200) * mm, "construction": true});
            skLineSegment(sketch, "E169.MirrorCS", {"start": v(27980, 2900) * mm, "end": v(27980, 3750) * mm});
            skLineSegment(sketch, "E170.MirrorCS", {"start": v(24980.36, 2900) * mm, "end": v(24980.36, 3750) * mm});
            skLineSegment(sketch, "E171.MirrorCS", {"start": v(20380, 3750) * mm, "end": v(21142.5, 3750) * mm});
            skLineSegment(sketch, "E172.MirrorCS", {"start": v(25030.36, 3800) * mm, "end": v(25030.36, 1200) * mm});
            skLineSegment(sketch, "E173.MirrorCS", {"start": v(21980, 1250) * mm, "end": v(21217.5, 1250) * mm});
            skLineSegment(sketch, "E174.MirrorCS", {"start": v(20380, 2850) * mm, "end": v(21142.5, 2850) * mm});
            skLineSegment(sketch, "E175.MirrorCS", {"start": v(20380, 2900) * mm, "end": v(20380, 3750) * mm});
            skSolve(sketch);
        }
        {
            var Q0;
            Q0=qSketchRegion(id+"F10",true);
            extrude(context, id + "F11", {"entities" : qUnion([Q0]), "depth" : 50 * mm, "offsetDistance" : 25 * mm});
        }
        {
            var Q0;
            Q0=makeQuery(id+"F5.boolean.opBoolean","MERGE",FACE,{"derivedFrom":[makeQuery(id+"F1.opExtrude","SWEPT_FACE",FACE,{"disambiguationData":[OSD([sQuery(id+"F0.wireOp",EDGE,"E17.8")])]}),makeQuery(id+"F5.opExtrude","SWEPT_FACE",FACE,{"disambiguationData":[OSD([sQuery(id+"F4.wireOp",EDGE,"E20")])]})]});
            var sketch = newSketch(context, id + "F12", { "sketchPlane" : qUnion([Q0])});
            skLineSegment(sketch, "E176.bottom", {"start": v(-37810, 3800) * mm, "end": v(-36110, 3800) * mm});
            skLineSegment(sketch, "E176.top", {"start": v(-37810, 1200) * mm, "end": v(-36110, 1200) * mm});
            skLineSegment(sketch, "E176.left", {"start": v(-37810, 3800) * mm, "end": v(-37810, 1200) * mm});
            skLineSegment(sketch, "E176.right", {"start": v(-36110, 3800) * mm, "end": v(-36110, 1200) * mm});
            skLineSegment(sketch, "E177.bottom", {"start": v(-35010, 3800) * mm, "end": v(-33310, 3800) * mm});
            skLineSegment(sketch, "E177.top", {"start": v(-35010, 1200) * mm, "end": v(-33310, 1200) * mm});
            skLineSegment(sketch, "E177.left", {"start": v(-35010, 3800) * mm, "end": v(-35010, 1200) * mm});
            skLineSegment(sketch, "E177.right", {"start": v(-33310, 3800) * mm, "end": v(-33310, 1200) * mm});
            skLineSegment(sketch, "E178.bottom", {"start": v(-32160, 3800) * mm, "end": v(-30460, 3800) * mm});
            skLineSegment(sketch, "E178.top", {"start": v(-32160, 1200) * mm, "end": v(-30460, 1200) * mm});
            skLineSegment(sketch, "E178.left", {"start": v(-32160, 3800) * mm, "end": v(-32160, 1200) * mm});
            skLineSegment(sketch, "E178.right", {"start": v(-30460, 3800) * mm, "end": v(-30460, 1200) * mm});
            skLineSegment(sketch, "E179.bottom", {"start": v(-28060, 3800) * mm, "end": v(-26360, 3800) * mm});
            skLineSegment(sketch, "E179.top", {"start": v(-28060, 1200) * mm, "end": v(-26360, 1200) * mm});
            skLineSegment(sketch, "E179.left", {"start": v(-28060, 3800) * mm, "end": v(-28060, 1200) * mm});
            skLineSegment(sketch, "E179.right", {"start": v(-26360, 3800) * mm, "end": v(-26360, 1200) * mm});
            skLineSegment(sketch, "E180.bottom", {"start": v(-25260, 3800) * mm, "end": v(-23560, 3800) * mm});
            skLineSegment(sketch, "E180.top", {"start": v(-25260, 1200) * mm, "end": v(-23560, 1200) * mm});
            skLineSegment(sketch, "E180.left", {"start": v(-25260, 3800) * mm, "end": v(-25260, 1200) * mm});
            skLineSegment(sketch, "E180.right", {"start": v(-23560, 3800) * mm, "end": v(-23560, 1200) * mm});
            skLineSegment(sketch, "E181.bottom", {"start": v(-22460, 3800) * mm, "end": v(-20760, 3800) * mm});
            skLineSegment(sketch, "E181.top", {"start": v(-22460, 1200) * mm, "end": v(-20760, 1200) * mm});
            skLineSegment(sketch, "E181.left", {"start": v(-22460, 3800) * mm, "end": v(-22460, 1200) * mm});
            skLineSegment(sketch, "E181.right", {"start": v(-20760, 3800) * mm, "end": v(-20760, 1200) * mm});
            skLineSegment(sketch, "E182.1.0.0", {"start": v(-13060, 3800) * mm, "end": v(-11360, 3800) * mm});
            skLineSegment(sketch, "E182.1.0.1", {"start": v(-11360, 3800) * mm, "end": v(-11360, 1200) * mm});
            skLineSegment(sketch, "E182.1.0.2", {"start": v(-15860, 3800) * mm, "end": v(-15860, 1200) * mm});
            skLineSegment(sketch, "E182.1.0.3", {"start": v(-15860, 3800) * mm, "end": v(-14160, 3800) * mm});
            skLineSegment(sketch, "E182.1.0.4", {"start": v(-18660, 3800) * mm, "end": v(-16960, 3800) * mm});
            skLineSegment(sketch, "E182.1.0.5", {"start": v(-18660, 3800) * mm, "end": v(-18660, 1200) * mm});
            skLineSegment(sketch, "E182.1.0.6", {"start": v(-13060, 3800) * mm, "end": v(-13060, 1200) * mm});
            skLineSegment(sketch, "E182.1.0.7", {"start": v(-18660, 1200) * mm, "end": v(-16960, 1200) * mm});
            skLineSegment(sketch, "E182.1.0.8", {"start": v(-15860, 1200) * mm, "end": v(-14160, 1200) * mm});
            skLineSegment(sketch, "E182.1.0.9", {"start": v(-14160, 3800) * mm, "end": v(-14160, 1200) * mm});
            skLineSegment(sketch, "E182.1.0.10", {"start": v(-13060, 1200) * mm, "end": v(-11360, 1200) * mm});
            skLineSegment(sketch, "E182.1.0.11", {"start": v(-16960, 3800) * mm, "end": v(-16960, 1200) * mm});
            skLineSegment(sketch, "E182.2.0.0", {"start": v(-3660, 3800) * mm, "end": v(-1960, 3800) * mm});
            skLineSegment(sketch, "E182.2.0.1", {"start": v(-1960, 3800) * mm, "end": v(-1960, 1200) * mm});
            skLineSegment(sketch, "E182.2.0.2", {"start": v(-6460, 3800) * mm, "end": v(-6460, 1200) * mm});
            skLineSegment(sketch, "E182.2.0.3", {"start": v(-6460, 3800) * mm, "end": v(-4760, 3800) * mm});
            skLineSegment(sketch, "E182.2.0.4", {"start": v(-9260, 3800) * mm, "end": v(-7560, 3800) * mm});
            skLineSegment(sketch, "E182.2.0.5", {"start": v(-9260, 3800) * mm, "end": v(-9260, 1200) * mm});
            skLineSegment(sketch, "E182.2.0.6", {"start": v(-3660, 3800) * mm, "end": v(-3660, 1200) * mm});
            skLineSegment(sketch, "E182.2.0.7", {"start": v(-9260, 1200) * mm, "end": v(-7560, 1200) * mm});
            skLineSegment(sketch, "E182.2.0.8", {"start": v(-6460, 1200) * mm, "end": v(-4760, 1200) * mm});
            skLineSegment(sketch, "E182.2.0.9", {"start": v(-4760, 3800) * mm, "end": v(-4760, 1200) * mm});
            skLineSegment(sketch, "E182.2.0.10", {"start": v(-3660, 1200) * mm, "end": v(-1960, 1200) * mm});
            skLineSegment(sketch, "E182.2.0.11", {"start": v(-7560, 3800) * mm, "end": v(-7560, 1200) * mm});
            skLineSegment(sketch, "E182.direction1", {"start": v(-28060, 1200) * mm, "end": v(-18660, 1200) * mm, "construction": true});
            skSolve(sketch);
        }
        {
            var Q0;
            Q0=qSketchRegion(id+"F12",true);
            extrude(context, id + "F13", {"entities" : qUnion([Q0]), "operationType" : NewBodyOperationType.REMOVE, "oppositeDirection" : true, "depth" : 650 * mm, "offsetDistance" : 25 * mm});
        }
        {
            var Q0;
            Q0=makeQuery(id+"F5.boolean.opBoolean","MERGE",FACE,{"derivedFrom":[makeQuery(id+"F3.boolean.opBoolean","COPY",FACE,{"derivedFrom":makeQuery(id+"F3.opExtrude","SWEPT_FACE",FACE,{"disambiguationData":[OSD([sQuery(id+"F2.wireOp",EDGE,"E19.13")])]})}),makeQuery(id+"F5.opExtrude","SWEPT_FACE",FACE,{"disambiguationData":[OSD([sQuery(id+"F4.wireOp",EDGE,"E30.0")])]})]});
            var sketch = newSketch(context, id + "F14", { "sketchPlane" : qUnion([Q0])});
            skLineSegment(sketch, "E183.12", {"start": v(28060, 3800) * mm, "end": v(26360, 3800) * mm});
            skLineSegment(sketch, "E183.13", {"start": v(28060, 1200) * mm, "end": v(26360, 1200) * mm});
            skLineSegment(sketch, "E183.14", {"start": v(28060, 3800) * mm, "end": v(28060, 1200) * mm});
            skLineSegment(sketch, "E183.15", {"start": v(26360, 3800) * mm, "end": v(26360, 1200) * mm});
            skLineSegment(sketch, "E183.16", {"start": v(25260, 3800) * mm, "end": v(23560, 3800) * mm});
            skLineSegment(sketch, "E183.17", {"start": v(25260, 1200) * mm, "end": v(23560, 1200) * mm});
            skLineSegment(sketch, "E183.18", {"start": v(25260, 3800) * mm, "end": v(25260, 1200) * mm});
            skLineSegment(sketch, "E183.19", {"start": v(23560, 3800) * mm, "end": v(23560, 1200) * mm});
            skLineSegment(sketch, "E183.20", {"start": v(22460, 3800) * mm, "end": v(20760, 3800) * mm});
            skLineSegment(sketch, "E183.21", {"start": v(22460, 1200) * mm, "end": v(20760, 1200) * mm});
            skLineSegment(sketch, "E183.22", {"start": v(22460, 3800) * mm, "end": v(22460, 1200) * mm});
            skLineSegment(sketch, "E183.23", {"start": v(20760, 3800) * mm, "end": v(20760, 1200) * mm});
            skLineSegment(sketch, "E183.24", {"start": v(13060, 3800) * mm, "end": v(11360, 3800) * mm});
            skLineSegment(sketch, "E183.25", {"start": v(11360, 3800) * mm, "end": v(11360, 1200) * mm});
            skLineSegment(sketch, "E183.26", {"start": v(15860, 3800) * mm, "end": v(15860, 1200) * mm});
            skLineSegment(sketch, "E183.27", {"start": v(15860, 3800) * mm, "end": v(14160, 3800) * mm});
            skLineSegment(sketch, "E183.28", {"start": v(18660, 3800) * mm, "end": v(16960, 3800) * mm});
            skLineSegment(sketch, "E183.29", {"start": v(18660, 3800) * mm, "end": v(18660, 1200) * mm});
            skLineSegment(sketch, "E183.30", {"start": v(13060, 3800) * mm, "end": v(13060, 1200) * mm});
            skLineSegment(sketch, "E183.31", {"start": v(18660, 1200) * mm, "end": v(16960, 1200) * mm});
            skLineSegment(sketch, "E183.32", {"start": v(15860, 1200) * mm, "end": v(14160, 1200) * mm});
            skLineSegment(sketch, "E183.33", {"start": v(14160, 3800) * mm, "end": v(14160, 1200) * mm});
            skLineSegment(sketch, "E183.34", {"start": v(13060, 1200) * mm, "end": v(11360, 1200) * mm});
            skLineSegment(sketch, "E183.35", {"start": v(16960, 3800) * mm, "end": v(16960, 1200) * mm});
            skLineSegment(sketch, "E183.36", {"start": v(3660, 3800) * mm, "end": v(1960, 3800) * mm});
            skLineSegment(sketch, "E183.37", {"start": v(1960, 3800) * mm, "end": v(1960, 1200) * mm});
            skLineSegment(sketch, "E183.38", {"start": v(6460, 3800) * mm, "end": v(6460, 1200) * mm});
            skLineSegment(sketch, "E183.39", {"start": v(6460, 3800) * mm, "end": v(4760, 3800) * mm});
            skLineSegment(sketch, "E183.40", {"start": v(9260, 3800) * mm, "end": v(7560, 3800) * mm});
            skLineSegment(sketch, "E183.41", {"start": v(9260, 3800) * mm, "end": v(9260, 1200) * mm});
            skLineSegment(sketch, "E183.42", {"start": v(3660, 3800) * mm, "end": v(3660, 1200) * mm});
            skLineSegment(sketch, "E183.43", {"start": v(9260, 1200) * mm, "end": v(7560, 1200) * mm});
            skLineSegment(sketch, "E183.44", {"start": v(6460, 1200) * mm, "end": v(4760, 1200) * mm});
            skLineSegment(sketch, "E183.45", {"start": v(4760, 3800) * mm, "end": v(4760, 1200) * mm});
            skLineSegment(sketch, "E183.46", {"start": v(3660, 1200) * mm, "end": v(1960, 1200) * mm});
            skLineSegment(sketch, "E183.47", {"start": v(7560, 3800) * mm, "end": v(7560, 1200) * mm});
            skLineSegment(sketch, "E183.48", {"start": v(28060, 1200) * mm, "end": v(18660, 1200) * mm});
            skLineSegment(sketch, "E184.bottom", {"start": v(30460, 3800) * mm, "end": v(32160, 3800) * mm});
            skLineSegment(sketch, "E184.top", {"start": v(30460, 1200) * mm, "end": v(32160, 1200) * mm});
            skLineSegment(sketch, "E184.left", {"start": v(30460, 3800) * mm, "end": v(30460, 1200) * mm});
            skLineSegment(sketch, "E184.right", {"start": v(32160, 3800) * mm, "end": v(32160, 1200) * mm});
            skLineSegment(sketch, "E185.bottom", {"start": v(33310, 3800) * mm, "end": v(35010, 3800) * mm});
            skLineSegment(sketch, "E185.top", {"start": v(33310, 1200) * mm, "end": v(35010, 1200) * mm});
            skLineSegment(sketch, "E185.left", {"start": v(33310, 3800) * mm, "end": v(33310, 1200) * mm});
            skLineSegment(sketch, "E185.right", {"start": v(35010, 3800) * mm, "end": v(35010, 1200) * mm});
            skLineSegment(sketch, "E186.bottom", {"start": v(35560, 3800) * mm, "end": v(37260, 3800) * mm});
            skLineSegment(sketch, "E186.top", {"start": v(35560, 1200) * mm, "end": v(37260, 1200) * mm});
            skLineSegment(sketch, "E186.left", {"start": v(35560, 3800) * mm, "end": v(35560, 1200) * mm});
            skLineSegment(sketch, "E186.right", {"start": v(37260, 3800) * mm, "end": v(37260, 1200) * mm});
            skSolve(sketch);
        }
        {
            var Q0;
            Q0 = qSketchRegion(id + "F14", true);
            extrude(context, id + "F15", {"entities" : qUnion([Q0]), "operationType" : NewBodyOperationType.REMOVE, "oppositeDirection" : true, "depth" : 600 * mm, "offsetDistance" : 25 * mm});
        }
        {
            var Q0;
            {var subQ18=sQuery(id+"F0.wireOp",EDGE,"E16.13");var subQ28=sQuery(id+"F0.wireOp",EDGE,"E16.3");Q0=makeQuery(id+"FMK1u3Q9oKXTw7Y_1.boolean.opBoolean","SPLIT",FACE,{"disambiguationData":[TD([makeQuery(id+"F1.opExtrude","SWEPT_FACE",FACE,{"disambiguationData":[OSD([subQ28])]})])],"derivedFrom":makeQuery(id+"F1.opExtrude","SWEPT_FACE",FACE,{"disambiguationData":[OSD([subQ18])]})});}
            var sketch = newSketch(context, id + "F16", { "sketchPlane" : qUnion([Q0])});
            skLineSegment(sketch, "E187.0", {"start": v(37810, 3800) * mm, "end": v(36110, 3800) * mm});
            skLineSegment(sketch, "E187.1", {"start": v(37810, 1200) * mm, "end": v(36110, 1200) * mm});
            skLineSegment(sketch, "E187.2", {"start": v(37810, 3800) * mm, "end": v(37810, 1200) * mm});
            skLineSegment(sketch, "E187.3", {"start": v(36110, 3800) * mm, "end": v(36110, 1200) * mm});
            skLineSegment(sketch, "E187.4", {"start": v(35010, 3800) * mm, "end": v(33310, 3800) * mm});
            skLineSegment(sketch, "E187.5", {"start": v(35010, 1200) * mm, "end": v(33310, 1200) * mm});
            skLineSegment(sketch, "E187.6", {"start": v(35010, 3800) * mm, "end": v(35010, 1200) * mm});
            skLineSegment(sketch, "E187.7", {"start": v(33310, 3800) * mm, "end": v(33310, 1200) * mm});
            skLineSegment(sketch, "E187.8", {"start": v(32160, 3800) * mm, "end": v(30460, 3800) * mm});
            skLineSegment(sketch, "E187.9", {"start": v(32160, 1200) * mm, "end": v(30460, 1200) * mm});
            skLineSegment(sketch, "E187.10", {"start": v(32160, 3800) * mm, "end": v(32160, 1200) * mm});
            skLineSegment(sketch, "E187.11", {"start": v(30460, 3800) * mm, "end": v(30460, 1200) * mm});
            skLineSegment(sketch, "E187.12", {"start": v(28060, 3800) * mm, "end": v(26360, 3800) * mm});
            skLineSegment(sketch, "E187.13", {"start": v(28060, 1200) * mm, "end": v(26360, 1200) * mm});
            skLineSegment(sketch, "E187.14", {"start": v(28060, 3800) * mm, "end": v(28060, 1200) * mm});
            skLineSegment(sketch, "E187.15", {"start": v(26360, 3800) * mm, "end": v(26360, 1200) * mm});
            skLineSegment(sketch, "E187.16", {"start": v(25260, 3800) * mm, "end": v(23560, 3800) * mm});
            skLineSegment(sketch, "E187.17", {"start": v(25260, 1200) * mm, "end": v(23560, 1200) * mm});
            skLineSegment(sketch, "E187.18", {"start": v(25260, 3800) * mm, "end": v(25260, 1200) * mm});
            skLineSegment(sketch, "E187.19", {"start": v(23560, 3800) * mm, "end": v(23560, 1200) * mm});
            skLineSegment(sketch, "E187.20", {"start": v(22460, 3800) * mm, "end": v(20760, 3800) * mm});
            skLineSegment(sketch, "E187.21", {"start": v(22460, 1200) * mm, "end": v(20760, 1200) * mm});
            skLineSegment(sketch, "E187.22", {"start": v(22460, 3800) * mm, "end": v(22460, 1200) * mm});
            skLineSegment(sketch, "E187.23", {"start": v(20760, 3800) * mm, "end": v(20760, 1200) * mm});
            skLineSegment(sketch, "E187.24", {"start": v(13060, 3800) * mm, "end": v(11360, 3800) * mm});
            skLineSegment(sketch, "E187.25", {"start": v(11360, 3800) * mm, "end": v(11360, 1200) * mm});
            skLineSegment(sketch, "E187.26", {"start": v(15860, 3800) * mm, "end": v(15860, 1200) * mm});
            skLineSegment(sketch, "E187.27", {"start": v(15860, 3800) * mm, "end": v(14160, 3800) * mm});
            skLineSegment(sketch, "E187.28", {"start": v(18660, 3800) * mm, "end": v(16960, 3800) * mm});
            skLineSegment(sketch, "E187.29", {"start": v(18660, 3800) * mm, "end": v(18660, 1200) * mm});
            skLineSegment(sketch, "E187.30", {"start": v(13060, 3800) * mm, "end": v(13060, 1200) * mm});
            skLineSegment(sketch, "E187.31", {"start": v(18660, 1200) * mm, "end": v(16960, 1200) * mm});
            skLineSegment(sketch, "E187.32", {"start": v(15860, 1200) * mm, "end": v(14160, 1200) * mm});
            skLineSegment(sketch, "E187.33", {"start": v(14160, 3800) * mm, "end": v(14160, 1200) * mm});
            skLineSegment(sketch, "E187.34", {"start": v(13060, 1200) * mm, "end": v(11360, 1200) * mm});
            skLineSegment(sketch, "E187.35", {"start": v(16960, 3800) * mm, "end": v(16960, 1200) * mm});
            skLineSegment(sketch, "E187.36", {"start": v(3660, 3800) * mm, "end": v(1960, 3800) * mm});
            skLineSegment(sketch, "E187.37", {"start": v(1960, 3800) * mm, "end": v(1960, 1200) * mm});
            skLineSegment(sketch, "E187.38", {"start": v(6460, 3800) * mm, "end": v(6460, 1200) * mm});
            skLineSegment(sketch, "E187.39", {"start": v(6460, 3800) * mm, "end": v(4760, 3800) * mm});
            skLineSegment(sketch, "E187.40", {"start": v(9260, 3800) * mm, "end": v(7560, 3800) * mm});
            skLineSegment(sketch, "E187.41", {"start": v(9260, 3800) * mm, "end": v(9260, 1200) * mm});
            skLineSegment(sketch, "E187.42", {"start": v(3660, 3800) * mm, "end": v(3660, 1200) * mm});
            skLineSegment(sketch, "E187.43", {"start": v(9260, 1200) * mm, "end": v(7560, 1200) * mm});
            skLineSegment(sketch, "E187.44", {"start": v(6460, 1200) * mm, "end": v(4760, 1200) * mm});
            skLineSegment(sketch, "E187.45", {"start": v(4760, 3800) * mm, "end": v(4760, 1200) * mm});
            skLineSegment(sketch, "E187.46", {"start": v(3660, 1200) * mm, "end": v(1960, 1200) * mm});
            skLineSegment(sketch, "E187.47", {"start": v(7560, 3800) * mm, "end": v(7560, 1200) * mm});
            skLineSegment(sketch, "E187.48", {"start": v(28060, 1200) * mm, "end": v(18660, 1200) * mm});
            skSolve(sketch);
        }
        {
            var Q0;
            Q0=qSketchRegion(id+"F16",true);
            extrude(context, id + "F17", {"entities" : qUnion([Q0]), "oppositeDirection" : true, "depth" : 100 * mm, "offsetDistance" : 25 * mm});
        }
        {
            var Q0;
            Q0=makeQuery(id+"F1.opExtrude","SWEPT_FACE",FACE,{"disambiguationData":[OSD([sQuery(id+"F0.wireOp",EDGE,"E16.0")])]});
            var sketch = newSketch(context, id + "F18", { "sketchPlane" : qUnion([Q0])});
            skLineSegment(sketch, "E188.0", {"start": v(-28060, 3800) * mm, "end": v(-26360, 3800) * mm});
            skLineSegment(sketch, "E188.1", {"start": v(-28060, 1200) * mm, "end": v(-26360, 1200) * mm});
            skLineSegment(sketch, "E188.2", {"start": v(-28060, 3800) * mm, "end": v(-28060, 1200) * mm});
            skLineSegment(sketch, "E188.3", {"start": v(-26360, 3800) * mm, "end": v(-26360, 1200) * mm});
            skLineSegment(sketch, "E188.4", {"start": v(-25260, 3800) * mm, "end": v(-23560, 3800) * mm});
            skLineSegment(sketch, "E188.5", {"start": v(-25260, 1200) * mm, "end": v(-23560, 1200) * mm});
            skLineSegment(sketch, "E188.6", {"start": v(-25260, 3800) * mm, "end": v(-25260, 1200) * mm});
            skLineSegment(sketch, "E188.7", {"start": v(-23560, 3800) * mm, "end": v(-23560, 1200) * mm});
            skLineSegment(sketch, "E188.8", {"start": v(-22460, 3800) * mm, "end": v(-20760, 3800) * mm});
            skLineSegment(sketch, "E188.9", {"start": v(-22460, 1200) * mm, "end": v(-20760, 1200) * mm});
            skLineSegment(sketch, "E188.10", {"start": v(-22460, 3800) * mm, "end": v(-22460, 1200) * mm});
            skLineSegment(sketch, "E188.11", {"start": v(-20760, 3800) * mm, "end": v(-20760, 1200) * mm});
            skLineSegment(sketch, "E188.12", {"start": v(-13060, 3800) * mm, "end": v(-11360, 3800) * mm});
            skLineSegment(sketch, "E188.13", {"start": v(-11360, 3800) * mm, "end": v(-11360, 1200) * mm});
            skLineSegment(sketch, "E188.14", {"start": v(-15860, 3800) * mm, "end": v(-15860, 1200) * mm});
            skLineSegment(sketch, "E188.15", {"start": v(-15860, 3800) * mm, "end": v(-14160, 3800) * mm});
            skLineSegment(sketch, "E188.16", {"start": v(-18660, 3800) * mm, "end": v(-16960, 3800) * mm});
            skLineSegment(sketch, "E188.17", {"start": v(-18660, 3800) * mm, "end": v(-18660, 1200) * mm});
            skLineSegment(sketch, "E188.18", {"start": v(-13060, 3800) * mm, "end": v(-13060, 1200) * mm});
            skLineSegment(sketch, "E188.19", {"start": v(-18660, 1200) * mm, "end": v(-16960, 1200) * mm});
            skLineSegment(sketch, "E188.20", {"start": v(-15860, 1200) * mm, "end": v(-14160, 1200) * mm});
            skLineSegment(sketch, "E188.21", {"start": v(-14160, 3800) * mm, "end": v(-14160, 1200) * mm});
            skLineSegment(sketch, "E188.22", {"start": v(-13060, 1200) * mm, "end": v(-11360, 1200) * mm});
            skLineSegment(sketch, "E188.23", {"start": v(-16960, 3800) * mm, "end": v(-16960, 1200) * mm});
            skLineSegment(sketch, "E188.24", {"start": v(-3660, 3800) * mm, "end": v(-1960, 3800) * mm});
            skLineSegment(sketch, "E188.25", {"start": v(-1960, 3800) * mm, "end": v(-1960, 1200) * mm});
            skLineSegment(sketch, "E188.26", {"start": v(-6460, 3800) * mm, "end": v(-6460, 1200) * mm});
            skLineSegment(sketch, "E188.27", {"start": v(-6460, 3800) * mm, "end": v(-4760, 3800) * mm});
            skLineSegment(sketch, "E188.28", {"start": v(-9260, 3800) * mm, "end": v(-7560, 3800) * mm});
            skLineSegment(sketch, "E188.29", {"start": v(-9260, 3800) * mm, "end": v(-9260, 1200) * mm});
            skLineSegment(sketch, "E188.30", {"start": v(-3660, 3800) * mm, "end": v(-3660, 1200) * mm});
            skLineSegment(sketch, "E188.31", {"start": v(-9260, 1200) * mm, "end": v(-7560, 1200) * mm});
            skLineSegment(sketch, "E188.32", {"start": v(-6460, 1200) * mm, "end": v(-4760, 1200) * mm});
            skLineSegment(sketch, "E188.33", {"start": v(-4760, 3800) * mm, "end": v(-4760, 1200) * mm});
            skLineSegment(sketch, "E188.34", {"start": v(-3660, 1200) * mm, "end": v(-1960, 1200) * mm});
            skLineSegment(sketch, "E188.35", {"start": v(-7560, 3800) * mm, "end": v(-7560, 1200) * mm});
            skLineSegment(sketch, "E188.36", {"start": v(-28060, 1200) * mm, "end": v(-18660, 1200) * mm});
            skLineSegment(sketch, "E188.37", {"start": v(-30460, 3800) * mm, "end": v(-32160, 3800) * mm});
            skLineSegment(sketch, "E188.38", {"start": v(-30460, 1200) * mm, "end": v(-32160, 1200) * mm});
            skLineSegment(sketch, "E188.39", {"start": v(-30460, 3800) * mm, "end": v(-30460, 1200) * mm});
            skLineSegment(sketch, "E188.40", {"start": v(-32160, 3800) * mm, "end": v(-32160, 1200) * mm});
            skLineSegment(sketch, "E188.41", {"start": v(-33310, 3800) * mm, "end": v(-35010, 3800) * mm});
            skLineSegment(sketch, "E188.42", {"start": v(-33310, 1200) * mm, "end": v(-35010, 1200) * mm});
            skLineSegment(sketch, "E188.43", {"start": v(-33310, 3800) * mm, "end": v(-33310, 1200) * mm});
            skLineSegment(sketch, "E188.44", {"start": v(-35010, 3800) * mm, "end": v(-35010, 1200) * mm});
            skLineSegment(sketch, "E188.45", {"start": v(-35560, 3800) * mm, "end": v(-37260, 3800) * mm});
            skLineSegment(sketch, "E188.46", {"start": v(-35560, 1200) * mm, "end": v(-37260, 1200) * mm});
            skLineSegment(sketch, "E188.47", {"start": v(-35560, 3800) * mm, "end": v(-35560, 1200) * mm});
            skLineSegment(sketch, "E188.48", {"start": v(-37260, 3800) * mm, "end": v(-37260, 1200) * mm});
            skSolve(sketch);
        }
        {
            var Q0;
            Q0 = qSketchRegion(id + "F18", true);
            extrude(context, id + "F19", {"entities" : qUnion([Q0]), "oppositeDirection" : true, "depth" : 100 * mm, "offsetDistance" : 25 * mm});
        }
        {
            var Q0;
            Q0=makeQuery(id+"F17.opExtrude","CAP_FACE",FACE,{"disambiguationData":[OSD([sQuery(id+"F16.wireOp",EDGE,"E187.0"),sQuery(id+"F16.wireOp",EDGE,"E187.1"),sQuery(id+"F16.wireOp",EDGE,"E187.2"),sQuery(id+"F16.wireOp",EDGE,"E187.3")])],"isStart":false});
            var sketch = newSketch(context, id + "F20", { "sketchPlane" : qUnion([Q0])});
            skLineSegment(sketch, "E189.0.0", {"start": v(-37810, 1200) * mm, "end": v(-36110, 1200) * mm});
            skLineSegment(sketch, "E189.0.1", {"start": v(-36110, 1200) * mm, "end": v(-36110, 3800) * mm});
            skLineSegment(sketch, "E189.0.2", {"start": v(-36110, 3800) * mm, "end": v(-37810, 3800) * mm});
            skLineSegment(sketch, "E189.0.3", {"start": v(-37810, 3800) * mm, "end": v(-37810, 1200) * mm});
            skLineSegment(sketch, "E190", {"start": v(-36960, 1200) * mm, "end": v(-36960, 3800) * mm, "construction": true});
            skLineSegment(sketch, "E191.bottom", {"start": v(-37760, 2850) * mm, "end": v(-36997.5, 2850) * mm});
            skLineSegment(sketch, "E191.top", {"start": v(-37760, 1250) * mm, "end": v(-36997.5, 1250) * mm});
            skLineSegment(sketch, "E191.left", {"start": v(-37760, 2850) * mm, "end": v(-37760, 1250) * mm});
            skLineSegment(sketch, "E191.right", {"start": v(-36997.5, 2850) * mm, "end": v(-36997.5, 1250) * mm});
            skLineSegment(sketch, "E192.bottom", {"start": v(-37760, 2900) * mm, "end": v(-36997.5, 2900) * mm});
            skLineSegment(sketch, "E192.top", {"start": v(-37760, 3750) * mm, "end": v(-36997.5, 3750) * mm});
            skLineSegment(sketch, "E192.left", {"start": v(-37760, 2900) * mm, "end": v(-37760, 3750) * mm});
            skLineSegment(sketch, "E192.right", {"start": v(-36997.5, 2900) * mm, "end": v(-36997.5, 3750) * mm});
            skLineSegment(sketch, "E193.MirrorCS", {"start": v(-36160, 3750) * mm, "end": v(-36922.5, 3750) * mm});
            skLineSegment(sketch, "E194.MirrorCS", {"start": v(-36922.5, 2900) * mm, "end": v(-36922.5, 3750) * mm});
            skLineSegment(sketch, "E195.MirrorCS", {"start": v(-36160, 2900) * mm, "end": v(-36922.5, 2900) * mm});
            skLineSegment(sketch, "E196.MirrorCS", {"start": v(-36160, 2900) * mm, "end": v(-36160, 3750) * mm});
            skLineSegment(sketch, "E197.MirrorCS", {"start": v(-36160, 2850) * mm, "end": v(-36922.5, 2850) * mm});
            skLineSegment(sketch, "E198.MirrorCS", {"start": v(-36922.5, 2850) * mm, "end": v(-36922.5, 1250) * mm});
            skLineSegment(sketch, "E199.MirrorCS", {"start": v(-36160, 1250) * mm, "end": v(-36922.5, 1250) * mm});
            skLineSegment(sketch, "E200.MirrorCS", {"start": v(-36160, 2850) * mm, "end": v(-36160, 1250) * mm});
            skPoint(sketch, "E201", {"position": v(-35010, 1200) * mm});
            skPoint(sketch, "E202", {"position": v(-32160, 1200) * mm});
            skLineSegment(sketch, "E203.0.0", {"start": v(-35010, 1200) * mm, "end": v(-33310, 1200) * mm});
            skLineSegment(sketch, "E203.0.1", {"start": v(-33310, 1200) * mm, "end": v(-33310, 3800) * mm});
            skLineSegment(sketch, "E203.0.2", {"start": v(-33310, 3800) * mm, "end": v(-35010, 3800) * mm});
            skLineSegment(sketch, "E203.0.3", {"start": v(-35010, 3800) * mm, "end": v(-35010, 1200) * mm});
            skLineSegment(sketch, "E204", {"start": v(-34160, 1200) * mm, "end": v(-34160, 3800) * mm, "construction": true});
            skLineSegment(sketch, "E205.bottom", {"start": v(-34960, 2850) * mm, "end": v(-34197.5, 2850) * mm});
            skLineSegment(sketch, "E205.top", {"start": v(-34960, 1250) * mm, "end": v(-34197.5, 1250) * mm});
            skLineSegment(sketch, "E205.left", {"start": v(-34960, 2850) * mm, "end": v(-34960, 1250) * mm});
            skLineSegment(sketch, "E205.right", {"start": v(-34197.5, 2850) * mm, "end": v(-34197.5, 1250) * mm});
            skLineSegment(sketch, "E206.bottom", {"start": v(-34960, 2900) * mm, "end": v(-34197.5, 2900) * mm});
            skLineSegment(sketch, "E206.top", {"start": v(-34960, 3750) * mm, "end": v(-34197.5, 3750) * mm});
            skLineSegment(sketch, "E206.left", {"start": v(-34960, 2900) * mm, "end": v(-34960, 3750) * mm});
            skLineSegment(sketch, "E206.right", {"start": v(-34197.5, 2900) * mm, "end": v(-34197.5, 3750) * mm});
            skLineSegment(sketch, "E207.MirrorCS", {"start": v(-33360, 3750) * mm, "end": v(-34122.5, 3750) * mm});
            skLineSegment(sketch, "E208.MirrorCS", {"start": v(-34122.5, 2900) * mm, "end": v(-34122.5, 3750) * mm});
            skLineSegment(sketch, "E209.MirrorCS", {"start": v(-33360, 2900) * mm, "end": v(-34122.5, 2900) * mm});
            skLineSegment(sketch, "E210.MirrorCS", {"start": v(-33360, 2900) * mm, "end": v(-33360, 3750) * mm});
            skLineSegment(sketch, "E211.MirrorCS", {"start": v(-33360, 2850) * mm, "end": v(-34122.5, 2850) * mm});
            skLineSegment(sketch, "E212.MirrorCS", {"start": v(-34122.5, 2850) * mm, "end": v(-34122.5, 1250) * mm});
            skLineSegment(sketch, "E213.MirrorCS", {"start": v(-33360, 1250) * mm, "end": v(-34122.5, 1250) * mm});
            skLineSegment(sketch, "E214.MirrorCS", {"start": v(-33360, 2850) * mm, "end": v(-33360, 1250) * mm});
            skLineSegment(sketch, "E215.0.0", {"start": v(-32160, 1199) * mm, "end": v(-30460, 1199) * mm});
            skLineSegment(sketch, "E215.0.1", {"start": v(-30460, 1199) * mm, "end": v(-30460, 3799) * mm});
            skLineSegment(sketch, "E215.0.2", {"start": v(-30460, 3799) * mm, "end": v(-32160, 3799) * mm});
            skLineSegment(sketch, "E215.0.3", {"start": v(-32160, 3799) * mm, "end": v(-32160, 1199) * mm});
            skLineSegment(sketch, "E216", {"start": v(-31310, 1199) * mm, "end": v(-31310, 3799) * mm, "construction": true});
            skLineSegment(sketch, "E217.bottom", {"start": v(-32110, 2849) * mm, "end": v(-31347.5, 2849) * mm});
            skLineSegment(sketch, "E217.top", {"start": v(-32110, 1249) * mm, "end": v(-31347.5, 1249) * mm});
            skLineSegment(sketch, "E217.left", {"start": v(-32110, 2849) * mm, "end": v(-32110, 1249) * mm});
            skLineSegment(sketch, "E217.right", {"start": v(-31347.5, 2849) * mm, "end": v(-31347.5, 1249) * mm});
            skLineSegment(sketch, "E218.bottom", {"start": v(-32110, 2899) * mm, "end": v(-31347.5, 2899) * mm});
            skLineSegment(sketch, "E218.top", {"start": v(-32110, 3749) * mm, "end": v(-31347.5, 3749) * mm});
            skLineSegment(sketch, "E218.left", {"start": v(-32110, 2899) * mm, "end": v(-32110, 3749) * mm});
            skLineSegment(sketch, "E218.right", {"start": v(-31347.5, 2899) * mm, "end": v(-31347.5, 3749) * mm});
            skLineSegment(sketch, "E219.MirrorCS", {"start": v(-30510, 3749) * mm, "end": v(-31272.5, 3749) * mm});
            skLineSegment(sketch, "E220.MirrorCS", {"start": v(-31272.5, 2899) * mm, "end": v(-31272.5, 3749) * mm});
            skLineSegment(sketch, "E221.MirrorCS", {"start": v(-30510, 2899) * mm, "end": v(-31272.5, 2899) * mm});
            skLineSegment(sketch, "E222.MirrorCS", {"start": v(-30510, 2899) * mm, "end": v(-30510, 3749) * mm});
            skLineSegment(sketch, "E223.MirrorCS", {"start": v(-30510, 2849) * mm, "end": v(-31272.5, 2849) * mm});
            skLineSegment(sketch, "E224.MirrorCS", {"start": v(-31272.5, 2849) * mm, "end": v(-31272.5, 1249) * mm});
            skLineSegment(sketch, "E225.MirrorCS", {"start": v(-30510, 1249) * mm, "end": v(-31272.5, 1249) * mm});
            skLineSegment(sketch, "E226.MirrorCS", {"start": v(-30510, 2849) * mm, "end": v(-30510, 1249) * mm});
            skPoint(sketch, "E227", {"position": v(-28060, 1200) * mm});
            skPoint(sketch, "E228", {"position": v(-25260, 1200) * mm});
            skPoint(sketch, "E229", {"position": v(-22460, 1200) * mm});
            skLineSegment(sketch, "E230.0.0", {"start": v(-28060, 1200) * mm, "end": v(-26360, 1200) * mm});
            skLineSegment(sketch, "E230.0.1", {"start": v(-26360, 1200) * mm, "end": v(-26360, 3800) * mm});
            skLineSegment(sketch, "E230.0.2", {"start": v(-26360, 3800) * mm, "end": v(-28060, 3800) * mm});
            skLineSegment(sketch, "E230.0.3", {"start": v(-28060, 3800) * mm, "end": v(-28060, 1200) * mm});
            skLineSegment(sketch, "E231", {"start": v(-27210, 1200) * mm, "end": v(-27210, 3800) * mm, "construction": true});
            skLineSegment(sketch, "E232.bottom", {"start": v(-28010, 2850) * mm, "end": v(-27247.5, 2850) * mm});
            skLineSegment(sketch, "E232.top", {"start": v(-28010, 1250) * mm, "end": v(-27247.5, 1250) * mm});
            skLineSegment(sketch, "E232.left", {"start": v(-28010, 2850) * mm, "end": v(-28010, 1250) * mm});
            skLineSegment(sketch, "E232.right", {"start": v(-27247.5, 2850) * mm, "end": v(-27247.5, 1250) * mm});
            skLineSegment(sketch, "E233.bottom", {"start": v(-28010, 2900) * mm, "end": v(-27247.5, 2900) * mm});
            skLineSegment(sketch, "E233.top", {"start": v(-28010, 3750) * mm, "end": v(-27247.5, 3750) * mm});
            skLineSegment(sketch, "E233.left", {"start": v(-28010, 2900) * mm, "end": v(-28010, 3750) * mm});
            skLineSegment(sketch, "E233.right", {"start": v(-27247.5, 2900) * mm, "end": v(-27247.5, 3750) * mm});
            skLineSegment(sketch, "E234.MirrorCS", {"start": v(-26410, 3750) * mm, "end": v(-27172.5, 3750) * mm});
            skLineSegment(sketch, "E235.MirrorCS", {"start": v(-27172.5, 2900) * mm, "end": v(-27172.5, 3750) * mm});
            skLineSegment(sketch, "E236.MirrorCS", {"start": v(-26410, 2900) * mm, "end": v(-27172.5, 2900) * mm});
            skLineSegment(sketch, "E237.MirrorCS", {"start": v(-26410, 2900) * mm, "end": v(-26410, 3750) * mm});
            skLineSegment(sketch, "E238.MirrorCS", {"start": v(-26410, 2850) * mm, "end": v(-27172.5, 2850) * mm});
            skLineSegment(sketch, "E239.MirrorCS", {"start": v(-27172.5, 2850) * mm, "end": v(-27172.5, 1250) * mm});
            skLineSegment(sketch, "E240.MirrorCS", {"start": v(-26410, 1250) * mm, "end": v(-27172.5, 1250) * mm});
            skLineSegment(sketch, "E241.MirrorCS", {"start": v(-26410, 2850) * mm, "end": v(-26410, 1250) * mm});
            skLineSegment(sketch, "E242.0.0", {"start": v(-25260, 1200) * mm, "end": v(-23560, 1200) * mm});
            skLineSegment(sketch, "E242.0.1", {"start": v(-23560, 1200) * mm, "end": v(-23560, 3800) * mm});
            skLineSegment(sketch, "E242.0.2", {"start": v(-23560, 3800) * mm, "end": v(-25260, 3800) * mm});
            skLineSegment(sketch, "E242.0.3", {"start": v(-25260, 3800) * mm, "end": v(-25260, 1200) * mm});
            skLineSegment(sketch, "E243", {"start": v(-24410, 1200) * mm, "end": v(-24410, 3800) * mm, "construction": true});
            skLineSegment(sketch, "E244.bottom", {"start": v(-25210, 2850) * mm, "end": v(-24447.5, 2850) * mm});
            skLineSegment(sketch, "E244.top", {"start": v(-25210, 1250) * mm, "end": v(-24447.5, 1250) * mm});
            skLineSegment(sketch, "E244.left", {"start": v(-25210, 2850) * mm, "end": v(-25210, 1250) * mm});
            skLineSegment(sketch, "E244.right", {"start": v(-24447.5, 2850) * mm, "end": v(-24447.5, 1250) * mm});
            skLineSegment(sketch, "E245.bottom", {"start": v(-25210, 2900) * mm, "end": v(-24447.5, 2900) * mm});
            skLineSegment(sketch, "E245.top", {"start": v(-25210, 3750) * mm, "end": v(-24447.5, 3750) * mm});
            skLineSegment(sketch, "E245.left", {"start": v(-25210, 2900) * mm, "end": v(-25210, 3750) * mm});
            skLineSegment(sketch, "E245.right", {"start": v(-24447.5, 2900) * mm, "end": v(-24447.5, 3750) * mm});
            skLineSegment(sketch, "E246.MirrorCS", {"start": v(-23610, 3750) * mm, "end": v(-24372.5, 3750) * mm});
            skLineSegment(sketch, "E247.MirrorCS", {"start": v(-24372.5, 2900) * mm, "end": v(-24372.5, 3750) * mm});
            skLineSegment(sketch, "E248.MirrorCS", {"start": v(-23610, 2900) * mm, "end": v(-24372.5, 2900) * mm});
            skLineSegment(sketch, "E249.MirrorCS", {"start": v(-23610, 2900) * mm, "end": v(-23610, 3750) * mm});
            skLineSegment(sketch, "E250.MirrorCS", {"start": v(-23610, 2850) * mm, "end": v(-24372.5, 2850) * mm});
            skLineSegment(sketch, "E251.MirrorCS", {"start": v(-24372.5, 2850) * mm, "end": v(-24372.5, 1250) * mm});
            skLineSegment(sketch, "E252.MirrorCS", {"start": v(-23610, 1250) * mm, "end": v(-24372.5, 1250) * mm});
            skLineSegment(sketch, "E253.MirrorCS", {"start": v(-23610, 2850) * mm, "end": v(-23610, 1250) * mm});
            skLineSegment(sketch, "E254.0.0", {"start": v(-22460, 1200) * mm, "end": v(-20760, 1200) * mm});
            skLineSegment(sketch, "E254.0.1", {"start": v(-20760, 1200) * mm, "end": v(-20760, 3800) * mm});
            skLineSegment(sketch, "E254.0.2", {"start": v(-20760, 3800) * mm, "end": v(-22460, 3800) * mm});
            skLineSegment(sketch, "E254.0.3", {"start": v(-22460, 3800) * mm, "end": v(-22460, 1200) * mm});
            skLineSegment(sketch, "E255", {"start": v(-21610, 1200) * mm, "end": v(-21610, 3800) * mm, "construction": true});
            skLineSegment(sketch, "E256.bottom", {"start": v(-22410, 2850) * mm, "end": v(-21647.5, 2850) * mm});
            skLineSegment(sketch, "E256.top", {"start": v(-22410, 1250) * mm, "end": v(-21647.5, 1250) * mm});
            skLineSegment(sketch, "E256.left", {"start": v(-22410, 2850) * mm, "end": v(-22410, 1250) * mm});
            skLineSegment(sketch, "E256.right", {"start": v(-21647.5, 2850) * mm, "end": v(-21647.5, 1250) * mm});
            skLineSegment(sketch, "E257.bottom", {"start": v(-22410, 2900) * mm, "end": v(-21647.5, 2900) * mm});
            skLineSegment(sketch, "E257.top", {"start": v(-22410, 3750) * mm, "end": v(-21647.5, 3750) * mm});
            skLineSegment(sketch, "E257.left", {"start": v(-22410, 2900) * mm, "end": v(-22410, 3750) * mm});
            skLineSegment(sketch, "E257.right", {"start": v(-21647.5, 2900) * mm, "end": v(-21647.5, 3750) * mm});
            skLineSegment(sketch, "E258.MirrorCS", {"start": v(-20810, 3750) * mm, "end": v(-21572.5, 3750) * mm});
            skLineSegment(sketch, "E259.MirrorCS", {"start": v(-21572.5, 2900) * mm, "end": v(-21572.5, 3750) * mm});
            skLineSegment(sketch, "E260.MirrorCS", {"start": v(-20810, 2900) * mm, "end": v(-21572.5, 2900) * mm});
            skLineSegment(sketch, "E261.MirrorCS", {"start": v(-20810, 2900) * mm, "end": v(-20810, 3750) * mm});
            skLineSegment(sketch, "E262.MirrorCS", {"start": v(-20810, 2850) * mm, "end": v(-21572.5, 2850) * mm});
            skLineSegment(sketch, "E263.MirrorCS", {"start": v(-21572.5, 2850) * mm, "end": v(-21572.5, 1250) * mm});
            skLineSegment(sketch, "E264.MirrorCS", {"start": v(-20810, 1250) * mm, "end": v(-21572.5, 1250) * mm});
            skLineSegment(sketch, "E265.MirrorCS", {"start": v(-20810, 2850) * mm, "end": v(-20810, 1250) * mm});
            skLineSegment(sketch, "E266.1.0.0", {"start": v(-15810, 2900) * mm, "end": v(-15047.5, 2900) * mm});
            skLineSegment(sketch, "E266.1.0.1", {"start": v(-18610, 2900) * mm, "end": v(-18610, 3750) * mm});
            skLineSegment(sketch, "E266.1.0.2", {"start": v(-11410, 2900) * mm, "end": v(-11410, 3750) * mm});
            skLineSegment(sketch, "E266.1.0.3", {"start": v(-15810, 2850) * mm, "end": v(-15047.5, 2850) * mm});
            skLineSegment(sketch, "E266.1.0.4", {"start": v(-18610, 3750) * mm, "end": v(-17847.5, 3750) * mm});
            skLineSegment(sketch, "E266.1.0.5", {"start": v(-17010, 2850) * mm, "end": v(-17010, 1250) * mm});
            skLineSegment(sketch, "E266.1.0.6", {"start": v(-14210, 2900) * mm, "end": v(-14972.5, 2900) * mm});
            skLineSegment(sketch, "E266.1.0.7", {"start": v(-18610, 2900) * mm, "end": v(-17847.5, 2900) * mm});
            skLineSegment(sketch, "E266.1.0.8", {"start": v(-13060, 1200) * mm, "end": v(-11360, 1200) * mm});
            skPoint(sketch, "E266.1.0.9", {"position": v(-18660, 1200) * mm});
            skLineSegment(sketch, "E266.1.0.10", {"start": v(-13010, 2900) * mm, "end": v(-12247.5, 2900) * mm});
            skLineSegment(sketch, "E266.1.0.11", {"start": v(-13010, 1250) * mm, "end": v(-12247.5, 1250) * mm});
            skLineSegment(sketch, "E266.1.0.12", {"start": v(-18660, 1200) * mm, "end": v(-16960, 1200) * mm});
            skLineSegment(sketch, "E266.1.0.13", {"start": v(-17010, 2850) * mm, "end": v(-17772.5, 2850) * mm});
            skLineSegment(sketch, "E266.1.0.14", {"start": v(-13010, 2850) * mm, "end": v(-13010, 1250) * mm});
            skLineSegment(sketch, "E266.1.0.15", {"start": v(-18610, 1250) * mm, "end": v(-17847.5, 1250) * mm});
            skLineSegment(sketch, "E266.1.0.16", {"start": v(-15047.5, 2850) * mm, "end": v(-15047.5, 1250) * mm});
            skLineSegment(sketch, "E266.1.0.17", {"start": v(-16960, 1200) * mm, "end": v(-16960, 3800) * mm});
            skLineSegment(sketch, "E266.1.0.18", {"start": v(-13010, 2850) * mm, "end": v(-12247.5, 2850) * mm});
            skLineSegment(sketch, "E266.1.0.19", {"start": v(-17010, 2900) * mm, "end": v(-17772.5, 2900) * mm});
            skLineSegment(sketch, "E266.1.0.20", {"start": v(-15047.5, 2900) * mm, "end": v(-15047.5, 3750) * mm});
            skPoint(sketch, "E266.1.0.21", {"position": v(-15860, 1200) * mm});
            skLineSegment(sketch, "E266.1.0.22", {"start": v(-15810, 2900) * mm, "end": v(-15810, 3750) * mm});
            skLineSegment(sketch, "E266.1.0.23", {"start": v(-11410, 2850) * mm, "end": v(-11410, 1250) * mm});
            skLineSegment(sketch, "E266.1.0.24", {"start": v(-15810, 2850) * mm, "end": v(-15810, 1250) * mm});
            skLineSegment(sketch, "E266.1.0.25", {"start": v(-11360, 3800) * mm, "end": v(-13060, 3800) * mm});
            skLineSegment(sketch, "E266.1.0.26", {"start": v(-17010, 1250) * mm, "end": v(-17772.5, 1250) * mm});
            skLineSegment(sketch, "E266.1.0.27", {"start": v(-18610, 2850) * mm, "end": v(-17847.5, 2850) * mm});
            skLineSegment(sketch, "E266.1.0.28", {"start": v(-17010, 3750) * mm, "end": v(-17772.5, 3750) * mm});
            skLineSegment(sketch, "E266.1.0.29", {"start": v(-17810, 1200) * mm, "end": v(-17810, 3800) * mm, "construction": true});
            skLineSegment(sketch, "E266.1.0.30", {"start": v(-14160, 1200) * mm, "end": v(-14160, 3800) * mm});
            skLineSegment(sketch, "E266.1.0.31", {"start": v(-11410, 1250) * mm, "end": v(-12172.5, 1250) * mm});
            skLineSegment(sketch, "E266.1.0.32", {"start": v(-17010, 2900) * mm, "end": v(-17010, 3750) * mm});
            skPoint(sketch, "E266.1.0.33", {"position": v(-13060, 1200) * mm});
            skLineSegment(sketch, "E266.1.0.34", {"start": v(-13010, 2900) * mm, "end": v(-13010, 3750) * mm});
            skLineSegment(sketch, "E266.1.0.35", {"start": v(-18660, 3800) * mm, "end": v(-18660, 1200) * mm});
            skLineSegment(sketch, "E266.1.0.36", {"start": v(-12210, 1200) * mm, "end": v(-12210, 3800) * mm, "construction": true});
            skLineSegment(sketch, "E266.1.0.37", {"start": v(-11410, 2850) * mm, "end": v(-12172.5, 2850) * mm});
            skLineSegment(sketch, "E266.1.0.38", {"start": v(-15810, 3750) * mm, "end": v(-15047.5, 3750) * mm});
            skLineSegment(sketch, "E266.1.0.39", {"start": v(-15860, 1200) * mm, "end": v(-14160, 1200) * mm});
            skLineSegment(sketch, "E266.1.0.40", {"start": v(-13060, 3800) * mm, "end": v(-13060, 1200) * mm});
            skLineSegment(sketch, "E266.1.0.41", {"start": v(-11410, 2900) * mm, "end": v(-12172.5, 2900) * mm});
            skLineSegment(sketch, "E266.1.0.42", {"start": v(-14210, 1250) * mm, "end": v(-14972.5, 1250) * mm});
            skLineSegment(sketch, "E266.1.0.43", {"start": v(-14160, 3800) * mm, "end": v(-15860, 3800) * mm});
            skLineSegment(sketch, "E266.1.0.44", {"start": v(-14210, 2850) * mm, "end": v(-14210, 1250) * mm});
            skLineSegment(sketch, "E266.1.0.45", {"start": v(-14210, 2850) * mm, "end": v(-14972.5, 2850) * mm});
            skLineSegment(sketch, "E266.1.0.46", {"start": v(-11360, 1200) * mm, "end": v(-11360, 3800) * mm});
            skLineSegment(sketch, "E266.1.0.47", {"start": v(-18610, 2850) * mm, "end": v(-18610, 1250) * mm});
            skLineSegment(sketch, "E266.1.0.48", {"start": v(-15010, 1200) * mm, "end": v(-15010, 3800) * mm, "construction": true});
            skLineSegment(sketch, "E266.1.0.49", {"start": v(-13010, 3750) * mm, "end": v(-12247.5, 3750) * mm});
            skLineSegment(sketch, "E266.1.0.50", {"start": v(-11410, 3750) * mm, "end": v(-12172.5, 3750) * mm});
            skLineSegment(sketch, "E266.1.0.51", {"start": v(-14210, 3750) * mm, "end": v(-14972.5, 3750) * mm});
            skLineSegment(sketch, "E266.1.0.52", {"start": v(-16960, 3800) * mm, "end": v(-18660, 3800) * mm});
            skLineSegment(sketch, "E266.1.0.53", {"start": v(-14972.5, 2900) * mm, "end": v(-14972.5, 3750) * mm});
            skLineSegment(sketch, "E266.1.0.54", {"start": v(-15810, 1250) * mm, "end": v(-15047.5, 1250) * mm});
            skLineSegment(sketch, "E266.1.0.55", {"start": v(-12172.5, 2850) * mm, "end": v(-12172.5, 1250) * mm});
            skLineSegment(sketch, "E266.1.0.56", {"start": v(-14210, 2900) * mm, "end": v(-14210, 3750) * mm});
            skLineSegment(sketch, "E266.1.0.57", {"start": v(-15860, 3800) * mm, "end": v(-15860, 1200) * mm});
            skLineSegment(sketch, "E266.1.0.58", {"start": v(-17847.5, 2850) * mm, "end": v(-17847.5, 1250) * mm});
            skLineSegment(sketch, "E266.1.0.59", {"start": v(-12172.5, 2900) * mm, "end": v(-12172.5, 3750) * mm});
            skLineSegment(sketch, "E266.1.0.60", {"start": v(-14972.5, 2850) * mm, "end": v(-14972.5, 1250) * mm});
            skLineSegment(sketch, "E266.1.0.61", {"start": v(-17847.5, 2900) * mm, "end": v(-17847.5, 3750) * mm});
            skLineSegment(sketch, "E266.1.0.62", {"start": v(-17772.5, 2900) * mm, "end": v(-17772.5, 3750) * mm});
            skLineSegment(sketch, "E266.1.0.63", {"start": v(-12247.5, 2900) * mm, "end": v(-12247.5, 3750) * mm});
            skLineSegment(sketch, "E266.1.0.64", {"start": v(-17772.5, 2850) * mm, "end": v(-17772.5, 1250) * mm});
            skLineSegment(sketch, "E266.1.0.65", {"start": v(-12247.5, 2850) * mm, "end": v(-12247.5, 1250) * mm});
            skLineSegment(sketch, "E266.2.0.0", {"start": v(-6410, 2900) * mm, "end": v(-5647.5, 2900) * mm});
            skLineSegment(sketch, "E266.2.0.1", {"start": v(-9210, 2900) * mm, "end": v(-9210, 3750) * mm});
            skLineSegment(sketch, "E266.2.0.2", {"start": v(-2010, 2900) * mm, "end": v(-2010, 3750) * mm});
            skLineSegment(sketch, "E266.2.0.3", {"start": v(-6410, 2850) * mm, "end": v(-5647.5, 2850) * mm});
            skLineSegment(sketch, "E266.2.0.4", {"start": v(-9210, 3750) * mm, "end": v(-8447.5, 3750) * mm});
            skLineSegment(sketch, "E266.2.0.5", {"start": v(-7610, 2850) * mm, "end": v(-7610, 1250) * mm});
            skLineSegment(sketch, "E266.2.0.6", {"start": v(-4810, 2900) * mm, "end": v(-5572.5, 2900) * mm});
            skLineSegment(sketch, "E266.2.0.7", {"start": v(-9210, 2900) * mm, "end": v(-8447.5, 2900) * mm});
            skLineSegment(sketch, "E266.2.0.8", {"start": v(-3660, 1200) * mm, "end": v(-1960, 1200) * mm});
            skPoint(sketch, "E266.2.0.9", {"position": v(-9260, 1200) * mm});
            skLineSegment(sketch, "E266.2.0.10", {"start": v(-3610, 2900) * mm, "end": v(-2847.5, 2900) * mm});
            skLineSegment(sketch, "E266.2.0.11", {"start": v(-3610, 1250) * mm, "end": v(-2847.5, 1250) * mm});
            skLineSegment(sketch, "E266.2.0.12", {"start": v(-9260, 1200) * mm, "end": v(-7560, 1200) * mm});
            skLineSegment(sketch, "E266.2.0.13", {"start": v(-7610, 2850) * mm, "end": v(-8372.5, 2850) * mm});
            skLineSegment(sketch, "E266.2.0.14", {"start": v(-3610, 2850) * mm, "end": v(-3610, 1250) * mm});
            skLineSegment(sketch, "E266.2.0.15", {"start": v(-9210, 1250) * mm, "end": v(-8447.5, 1250) * mm});
            skLineSegment(sketch, "E266.2.0.16", {"start": v(-5647.5, 2850) * mm, "end": v(-5647.5, 1250) * mm});
            skLineSegment(sketch, "E266.2.0.17", {"start": v(-7560, 1200) * mm, "end": v(-7560, 3800) * mm});
            skLineSegment(sketch, "E266.2.0.18", {"start": v(-3610, 2850) * mm, "end": v(-2847.5, 2850) * mm});
            skLineSegment(sketch, "E266.2.0.19", {"start": v(-7610, 2900) * mm, "end": v(-8372.5, 2900) * mm});
            skLineSegment(sketch, "E266.2.0.20", {"start": v(-5647.5, 2900) * mm, "end": v(-5647.5, 3750) * mm});
            skPoint(sketch, "E266.2.0.21", {"position": v(-6460, 1200) * mm});
            skLineSegment(sketch, "E266.2.0.22", {"start": v(-6410, 2900) * mm, "end": v(-6410, 3750) * mm});
            skLineSegment(sketch, "E266.2.0.23", {"start": v(-2010, 2850) * mm, "end": v(-2010, 1250) * mm});
            skLineSegment(sketch, "E266.2.0.24", {"start": v(-6410, 2850) * mm, "end": v(-6410, 1250) * mm});
            skLineSegment(sketch, "E266.2.0.25", {"start": v(-1960, 3800) * mm, "end": v(-3660, 3800) * mm});
            skLineSegment(sketch, "E266.2.0.26", {"start": v(-7610, 1250) * mm, "end": v(-8372.5, 1250) * mm});
            skLineSegment(sketch, "E266.2.0.27", {"start": v(-9210, 2850) * mm, "end": v(-8447.5, 2850) * mm});
            skLineSegment(sketch, "E266.2.0.28", {"start": v(-7610, 3750) * mm, "end": v(-8372.5, 3750) * mm});
            skLineSegment(sketch, "E266.2.0.29", {"start": v(-8410, 1200) * mm, "end": v(-8410, 3800) * mm, "construction": true});
            skLineSegment(sketch, "E266.2.0.30", {"start": v(-4760, 1200) * mm, "end": v(-4760, 3800) * mm});
            skLineSegment(sketch, "E266.2.0.31", {"start": v(-2010, 1250) * mm, "end": v(-2772.5, 1250) * mm});
            skLineSegment(sketch, "E266.2.0.32", {"start": v(-7610, 2900) * mm, "end": v(-7610, 3750) * mm});
            skPoint(sketch, "E266.2.0.33", {"position": v(-3660, 1200) * mm});
            skLineSegment(sketch, "E266.2.0.34", {"start": v(-3610, 2900) * mm, "end": v(-3610, 3750) * mm});
            skLineSegment(sketch, "E266.2.0.35", {"start": v(-9260, 3800) * mm, "end": v(-9260, 1200) * mm});
            skLineSegment(sketch, "E266.2.0.36", {"start": v(-2810, 1200) * mm, "end": v(-2810, 3800) * mm, "construction": true});
            skLineSegment(sketch, "E266.2.0.37", {"start": v(-2010, 2850) * mm, "end": v(-2772.5, 2850) * mm});
            skLineSegment(sketch, "E266.2.0.38", {"start": v(-6410, 3750) * mm, "end": v(-5647.5, 3750) * mm});
            skLineSegment(sketch, "E266.2.0.39", {"start": v(-6460, 1200) * mm, "end": v(-4760, 1200) * mm});
            skLineSegment(sketch, "E266.2.0.40", {"start": v(-3660, 3800) * mm, "end": v(-3660, 1200) * mm});
            skLineSegment(sketch, "E266.2.0.41", {"start": v(-2010, 2900) * mm, "end": v(-2772.5, 2900) * mm});
            skLineSegment(sketch, "E266.2.0.42", {"start": v(-4810, 1250) * mm, "end": v(-5572.5, 1250) * mm});
            skLineSegment(sketch, "E266.2.0.43", {"start": v(-4760, 3800) * mm, "end": v(-6460, 3800) * mm});
            skLineSegment(sketch, "E266.2.0.44", {"start": v(-4810, 2850) * mm, "end": v(-4810, 1250) * mm});
            skLineSegment(sketch, "E266.2.0.45", {"start": v(-4810, 2850) * mm, "end": v(-5572.5, 2850) * mm});
            skLineSegment(sketch, "E266.2.0.46", {"start": v(-1960, 1200) * mm, "end": v(-1960, 3800) * mm});
            skLineSegment(sketch, "E266.2.0.47", {"start": v(-9210, 2850) * mm, "end": v(-9210, 1250) * mm});
            skLineSegment(sketch, "E266.2.0.48", {"start": v(-5610, 1200) * mm, "end": v(-5610, 3800) * mm, "construction": true});
            skLineSegment(sketch, "E266.2.0.49", {"start": v(-3610, 3750) * mm, "end": v(-2847.5, 3750) * mm});
            skLineSegment(sketch, "E266.2.0.50", {"start": v(-2010, 3750) * mm, "end": v(-2772.5, 3750) * mm});
            skLineSegment(sketch, "E266.2.0.51", {"start": v(-4810, 3750) * mm, "end": v(-5572.5, 3750) * mm});
            skLineSegment(sketch, "E266.2.0.52", {"start": v(-7560, 3800) * mm, "end": v(-9260, 3800) * mm});
            skLineSegment(sketch, "E266.2.0.53", {"start": v(-5572.5, 2900) * mm, "end": v(-5572.5, 3750) * mm});
            skLineSegment(sketch, "E266.2.0.54", {"start": v(-6410, 1250) * mm, "end": v(-5647.5, 1250) * mm});
            skLineSegment(sketch, "E266.2.0.55", {"start": v(-2772.5, 2850) * mm, "end": v(-2772.5, 1250) * mm});
            skLineSegment(sketch, "E266.2.0.56", {"start": v(-4810, 2900) * mm, "end": v(-4810, 3750) * mm});
            skLineSegment(sketch, "E266.2.0.57", {"start": v(-6460, 3800) * mm, "end": v(-6460, 1200) * mm});
            skLineSegment(sketch, "E266.2.0.58", {"start": v(-8447.5, 2850) * mm, "end": v(-8447.5, 1250) * mm});
            skLineSegment(sketch, "E266.2.0.59", {"start": v(-2772.5, 2900) * mm, "end": v(-2772.5, 3750) * mm});
            skLineSegment(sketch, "E266.2.0.60", {"start": v(-5572.5, 2850) * mm, "end": v(-5572.5, 1250) * mm});
            skLineSegment(sketch, "E266.2.0.61", {"start": v(-8447.5, 2900) * mm, "end": v(-8447.5, 3750) * mm});
            skLineSegment(sketch, "E266.2.0.62", {"start": v(-8372.5, 2900) * mm, "end": v(-8372.5, 3750) * mm});
            skLineSegment(sketch, "E266.2.0.63", {"start": v(-2847.5, 2900) * mm, "end": v(-2847.5, 3750) * mm});
            skLineSegment(sketch, "E266.2.0.64", {"start": v(-8372.5, 2850) * mm, "end": v(-8372.5, 1250) * mm});
            skLineSegment(sketch, "E266.2.0.65", {"start": v(-2847.5, 2850) * mm, "end": v(-2847.5, 1250) * mm});
            skLineSegment(sketch, "E266.direction1", {"start": v(-28060, 1200) * mm, "end": v(-18660, 1200) * mm, "construction": true});
            skSolve(sketch);
        }
        {
            var Q0;
            Q0=qSketchRegion(id+"F20",true);
            extrude(context, id + "F21", {"entities" : qUnion([Q0]), "depth" : 50 * mm, "offsetDistance" : 25 * mm});
        }
        {
            var Q0;
            Q0=makeQuery(id+"F19.opExtrude","CAP_FACE",FACE,{"disambiguationData":[OSD([sQuery(id+"F18.wireOp",EDGE,"E188.24"),sQuery(id+"F18.wireOp",EDGE,"E188.25"),sQuery(id+"F18.wireOp",EDGE,"E188.30"),sQuery(id+"F18.wireOp",EDGE,"E188.34")])],"isStart":false});
            var sketch = newSketch(context, id + "F22", { "sketchPlane" : qUnion([Q0])});
            skLineSegment(sketch, "E267.0", {"start": v(37260, 1200) * mm, "end": v(35560, 1200) * mm});
            skLineSegment(sketch, "E267.1", {"start": v(35560, 1200) * mm, "end": v(35560, 3800) * mm});
            skLineSegment(sketch, "E267.2", {"start": v(35560, 3800) * mm, "end": v(37260, 3800) * mm});
            skLineSegment(sketch, "E267.3", {"start": v(37260, 3800) * mm, "end": v(37260, 1200) * mm});
            skLineSegment(sketch, "E267.4", {"start": v(36410, 1200) * mm, "end": v(36410, 3800) * mm});
            skLineSegment(sketch, "E267.5", {"start": v(37210, 2850) * mm, "end": v(36447.5, 2850) * mm});
            skLineSegment(sketch, "E267.6", {"start": v(37210, 1250) * mm, "end": v(36447.5, 1250) * mm});
            skLineSegment(sketch, "E267.7", {"start": v(37210, 2850) * mm, "end": v(37210, 1250) * mm});
            skLineSegment(sketch, "E267.8", {"start": v(36447.5, 2850) * mm, "end": v(36447.5, 1250) * mm});
            skLineSegment(sketch, "E267.9", {"start": v(37210, 2900) * mm, "end": v(36447.5, 2900) * mm});
            skLineSegment(sketch, "E267.10", {"start": v(37210, 3750) * mm, "end": v(36447.5, 3750) * mm});
            skLineSegment(sketch, "E267.11", {"start": v(37210, 2900) * mm, "end": v(37210, 3750) * mm});
            skLineSegment(sketch, "E267.12", {"start": v(36447.5, 2900) * mm, "end": v(36447.5, 3750) * mm});
            skLineSegment(sketch, "E267.13", {"start": v(35610, 3750) * mm, "end": v(36372.5, 3750) * mm});
            skLineSegment(sketch, "E267.14", {"start": v(36372.5, 2900) * mm, "end": v(36372.5, 3750) * mm});
            skLineSegment(sketch, "E267.15", {"start": v(35610, 2900) * mm, "end": v(36372.5, 2900) * mm});
            skLineSegment(sketch, "E267.16", {"start": v(35610, 2900) * mm, "end": v(35610, 3750) * mm});
            skLineSegment(sketch, "E267.17", {"start": v(35610, 2850) * mm, "end": v(36372.5, 2850) * mm});
            skLineSegment(sketch, "E267.18", {"start": v(36372.5, 2850) * mm, "end": v(36372.5, 1250) * mm});
            skLineSegment(sketch, "E267.19", {"start": v(35610, 1250) * mm, "end": v(36372.5, 1250) * mm});
            skLineSegment(sketch, "E267.20", {"start": v(35610, 2850) * mm, "end": v(35610, 1250) * mm});
            skPoint(sketch, "E267.21", {"position": v(35010, 1200) * mm});
            skPoint(sketch, "E267.22", {"position": v(32160, 1200) * mm});
            skLineSegment(sketch, "E267.23", {"start": v(35010, 1200) * mm, "end": v(33310, 1200) * mm});
            skLineSegment(sketch, "E267.24", {"start": v(33310, 1200) * mm, "end": v(33310, 3800) * mm});
            skLineSegment(sketch, "E267.25", {"start": v(33310, 3800) * mm, "end": v(35010, 3800) * mm});
            skLineSegment(sketch, "E267.26", {"start": v(35010, 3800) * mm, "end": v(35010, 1200) * mm});
            skLineSegment(sketch, "E267.27", {"start": v(34160, 1200) * mm, "end": v(34160, 3800) * mm});
            skLineSegment(sketch, "E267.28", {"start": v(34960, 2850) * mm, "end": v(34197.5, 2850) * mm});
            skLineSegment(sketch, "E267.29", {"start": v(34960, 1250) * mm, "end": v(34197.5, 1250) * mm});
            skLineSegment(sketch, "E267.30", {"start": v(34960, 2850) * mm, "end": v(34960, 1250) * mm});
            skLineSegment(sketch, "E267.31", {"start": v(34197.5, 2850) * mm, "end": v(34197.5, 1250) * mm});
            skLineSegment(sketch, "E267.32", {"start": v(34960, 2900) * mm, "end": v(34197.5, 2900) * mm});
            skLineSegment(sketch, "E267.33", {"start": v(34960, 3750) * mm, "end": v(34197.5, 3750) * mm});
            skLineSegment(sketch, "E267.34", {"start": v(34960, 2900) * mm, "end": v(34960, 3750) * mm});
            skLineSegment(sketch, "E267.35", {"start": v(34197.5, 2900) * mm, "end": v(34197.5, 3750) * mm});
            skLineSegment(sketch, "E267.36", {"start": v(33360, 3750) * mm, "end": v(34122.5, 3750) * mm});
            skLineSegment(sketch, "E267.37", {"start": v(34122.5, 2900) * mm, "end": v(34122.5, 3750) * mm});
            skLineSegment(sketch, "E267.38", {"start": v(33360, 2900) * mm, "end": v(34122.5, 2900) * mm});
            skLineSegment(sketch, "E267.39", {"start": v(33360, 2900) * mm, "end": v(33360, 3750) * mm});
            skLineSegment(sketch, "E267.40", {"start": v(33360, 2850) * mm, "end": v(34122.5, 2850) * mm});
            skLineSegment(sketch, "E267.41", {"start": v(34122.5, 2850) * mm, "end": v(34122.5, 1250) * mm});
            skLineSegment(sketch, "E267.42", {"start": v(33360, 1250) * mm, "end": v(34122.5, 1250) * mm});
            skLineSegment(sketch, "E267.43", {"start": v(33360, 2850) * mm, "end": v(33360, 1250) * mm});
            skLineSegment(sketch, "E267.44", {"start": v(32160, 1199) * mm, "end": v(30460, 1199) * mm});
            skLineSegment(sketch, "E267.45", {"start": v(30460, 1199) * mm, "end": v(30460, 3799) * mm});
            skLineSegment(sketch, "E267.46", {"start": v(30460, 3799) * mm, "end": v(32160, 3799) * mm});
            skLineSegment(sketch, "E267.47", {"start": v(32160, 3799) * mm, "end": v(32160, 1199) * mm});
            skLineSegment(sketch, "E267.48", {"start": v(31310, 1199) * mm, "end": v(31310, 3799) * mm});
            skLineSegment(sketch, "E267.49", {"start": v(32110, 2849) * mm, "end": v(31347.5, 2849) * mm});
            skLineSegment(sketch, "E267.50", {"start": v(32110, 1249) * mm, "end": v(31347.5, 1249) * mm});
            skLineSegment(sketch, "E267.51", {"start": v(32110, 2849) * mm, "end": v(32110, 1249) * mm});
            skLineSegment(sketch, "E267.52", {"start": v(31347.5, 2849) * mm, "end": v(31347.5, 1249) * mm});
            skLineSegment(sketch, "E267.53", {"start": v(32110, 2899) * mm, "end": v(31347.5, 2899) * mm});
            skLineSegment(sketch, "E267.54", {"start": v(32110, 3749) * mm, "end": v(31347.5, 3749) * mm});
            skLineSegment(sketch, "E267.55", {"start": v(32110, 2899) * mm, "end": v(32110, 3749) * mm});
            skLineSegment(sketch, "E267.56", {"start": v(31347.5, 2899) * mm, "end": v(31347.5, 3749) * mm});
            skLineSegment(sketch, "E267.57", {"start": v(30510, 3749) * mm, "end": v(31272.5, 3749) * mm});
            skLineSegment(sketch, "E267.58", {"start": v(31272.5, 2899) * mm, "end": v(31272.5, 3749) * mm});
            skLineSegment(sketch, "E267.59", {"start": v(30510, 2899) * mm, "end": v(31272.5, 2899) * mm});
            skLineSegment(sketch, "E267.60", {"start": v(30510, 2899) * mm, "end": v(30510, 3749) * mm});
            skLineSegment(sketch, "E267.61", {"start": v(30510, 2849) * mm, "end": v(31272.5, 2849) * mm});
            skLineSegment(sketch, "E267.62", {"start": v(31272.5, 2849) * mm, "end": v(31272.5, 1249) * mm});
            skLineSegment(sketch, "E267.63", {"start": v(30510, 1249) * mm, "end": v(31272.5, 1249) * mm});
            skLineSegment(sketch, "E267.64", {"start": v(30510, 2849) * mm, "end": v(30510, 1249) * mm});
            skPoint(sketch, "E267.65", {"position": v(28060, 1200) * mm});
            skPoint(sketch, "E267.66", {"position": v(25260, 1200) * mm});
            skPoint(sketch, "E267.67", {"position": v(22460, 1200) * mm});
            skLineSegment(sketch, "E267.68", {"start": v(28060, 1200) * mm, "end": v(26360, 1200) * mm});
            skLineSegment(sketch, "E267.69", {"start": v(26360, 1200) * mm, "end": v(26360, 3800) * mm});
            skLineSegment(sketch, "E267.70", {"start": v(26360, 3800) * mm, "end": v(28060, 3800) * mm});
            skLineSegment(sketch, "E267.71", {"start": v(28060, 3800) * mm, "end": v(28060, 1200) * mm});
            skLineSegment(sketch, "E267.72", {"start": v(27210, 1200) * mm, "end": v(27210, 3800) * mm});
            skLineSegment(sketch, "E267.73", {"start": v(28010, 2850) * mm, "end": v(27247.5, 2850) * mm});
            skLineSegment(sketch, "E267.74", {"start": v(28010, 1250) * mm, "end": v(27247.5, 1250) * mm});
            skLineSegment(sketch, "E267.75", {"start": v(28010, 2850) * mm, "end": v(28010, 1250) * mm});
            skLineSegment(sketch, "E267.76", {"start": v(27247.5, 2850) * mm, "end": v(27247.5, 1250) * mm});
            skLineSegment(sketch, "E267.77", {"start": v(28010, 2900) * mm, "end": v(27247.5, 2900) * mm});
            skLineSegment(sketch, "E267.78", {"start": v(28010, 3750) * mm, "end": v(27247.5, 3750) * mm});
            skLineSegment(sketch, "E267.79", {"start": v(28010, 2900) * mm, "end": v(28010, 3750) * mm});
            skLineSegment(sketch, "E267.80", {"start": v(27247.5, 2900) * mm, "end": v(27247.5, 3750) * mm});
            skLineSegment(sketch, "E267.81", {"start": v(26410, 3750) * mm, "end": v(27172.5, 3750) * mm});
            skLineSegment(sketch, "E267.82", {"start": v(27172.5, 2900) * mm, "end": v(27172.5, 3750) * mm});
            skLineSegment(sketch, "E267.83", {"start": v(26410, 2900) * mm, "end": v(27172.5, 2900) * mm});
            skLineSegment(sketch, "E267.84", {"start": v(26410, 2900) * mm, "end": v(26410, 3750) * mm});
            skLineSegment(sketch, "E267.85", {"start": v(26410, 2850) * mm, "end": v(27172.5, 2850) * mm});
            skLineSegment(sketch, "E267.86", {"start": v(27172.5, 2850) * mm, "end": v(27172.5, 1250) * mm});
            skLineSegment(sketch, "E267.87", {"start": v(26410, 1250) * mm, "end": v(27172.5, 1250) * mm});
            skLineSegment(sketch, "E267.88", {"start": v(26410, 2850) * mm, "end": v(26410, 1250) * mm});
            skLineSegment(sketch, "E267.89", {"start": v(25260, 1200) * mm, "end": v(23560, 1200) * mm});
            skLineSegment(sketch, "E267.90", {"start": v(23560, 1200) * mm, "end": v(23560, 3800) * mm});
            skLineSegment(sketch, "E267.91", {"start": v(23560, 3800) * mm, "end": v(25260, 3800) * mm});
            skLineSegment(sketch, "E267.92", {"start": v(25260, 3800) * mm, "end": v(25260, 1200) * mm});
            skLineSegment(sketch, "E267.93", {"start": v(24410, 1200) * mm, "end": v(24410, 3800) * mm});
            skLineSegment(sketch, "E267.94", {"start": v(25210, 2850) * mm, "end": v(24447.5, 2850) * mm});
            skLineSegment(sketch, "E267.95", {"start": v(25210, 1250) * mm, "end": v(24447.5, 1250) * mm});
            skLineSegment(sketch, "E267.96", {"start": v(25210, 2850) * mm, "end": v(25210, 1250) * mm});
            skLineSegment(sketch, "E267.97", {"start": v(24447.5, 2850) * mm, "end": v(24447.5, 1250) * mm});
            skLineSegment(sketch, "E267.98", {"start": v(25210, 2900) * mm, "end": v(24447.5, 2900) * mm});
            skLineSegment(sketch, "E267.99", {"start": v(25210, 3750) * mm, "end": v(24447.5, 3750) * mm});
            skLineSegment(sketch, "E267.100", {"start": v(25210, 2900) * mm, "end": v(25210, 3750) * mm});
            skLineSegment(sketch, "E267.101", {"start": v(24447.5, 2900) * mm, "end": v(24447.5, 3750) * mm});
            skLineSegment(sketch, "E267.102", {"start": v(23610, 3750) * mm, "end": v(24372.5, 3750) * mm});
            skLineSegment(sketch, "E267.103", {"start": v(24372.5, 2900) * mm, "end": v(24372.5, 3750) * mm});
            skLineSegment(sketch, "E267.104", {"start": v(23610, 2900) * mm, "end": v(24372.5, 2900) * mm});
            skLineSegment(sketch, "E267.105", {"start": v(23610, 2900) * mm, "end": v(23610, 3750) * mm});
            skLineSegment(sketch, "E267.106", {"start": v(23610, 2850) * mm, "end": v(24372.5, 2850) * mm});
            skLineSegment(sketch, "E267.107", {"start": v(24372.5, 2850) * mm, "end": v(24372.5, 1250) * mm});
            skLineSegment(sketch, "E267.108", {"start": v(23610, 1250) * mm, "end": v(24372.5, 1250) * mm});
            skLineSegment(sketch, "E267.109", {"start": v(23610, 2850) * mm, "end": v(23610, 1250) * mm});
            skLineSegment(sketch, "E267.110", {"start": v(22460, 1200) * mm, "end": v(20760, 1200) * mm});
            skLineSegment(sketch, "E267.111", {"start": v(20760, 1200) * mm, "end": v(20760, 3800) * mm});
            skLineSegment(sketch, "E267.112", {"start": v(20760, 3800) * mm, "end": v(22460, 3800) * mm});
            skLineSegment(sketch, "E267.113", {"start": v(22460, 3800) * mm, "end": v(22460, 1200) * mm});
            skLineSegment(sketch, "E267.114", {"start": v(21610, 1200) * mm, "end": v(21610, 3800) * mm});
            skLineSegment(sketch, "E267.115", {"start": v(22410, 2850) * mm, "end": v(21647.5, 2850) * mm});
            skLineSegment(sketch, "E267.116", {"start": v(22410, 1250) * mm, "end": v(21647.5, 1250) * mm});
            skLineSegment(sketch, "E267.117", {"start": v(22410, 2850) * mm, "end": v(22410, 1250) * mm});
            skLineSegment(sketch, "E267.118", {"start": v(21647.5, 2850) * mm, "end": v(21647.5, 1250) * mm});
            skLineSegment(sketch, "E267.119", {"start": v(22410, 2900) * mm, "end": v(21647.5, 2900) * mm});
            skLineSegment(sketch, "E267.120", {"start": v(22410, 3750) * mm, "end": v(21647.5, 3750) * mm});
            skLineSegment(sketch, "E267.121", {"start": v(22410, 2900) * mm, "end": v(22410, 3750) * mm});
            skLineSegment(sketch, "E267.122", {"start": v(21647.5, 2900) * mm, "end": v(21647.5, 3750) * mm});
            skLineSegment(sketch, "E267.123", {"start": v(20810, 3750) * mm, "end": v(21572.5, 3750) * mm});
            skLineSegment(sketch, "E267.124", {"start": v(21572.5, 2900) * mm, "end": v(21572.5, 3750) * mm});
            skLineSegment(sketch, "E267.125", {"start": v(20810, 2900) * mm, "end": v(21572.5, 2900) * mm});
            skLineSegment(sketch, "E267.126", {"start": v(20810, 2900) * mm, "end": v(20810, 3750) * mm});
            skLineSegment(sketch, "E267.127", {"start": v(20810, 2850) * mm, "end": v(21572.5, 2850) * mm});
            skLineSegment(sketch, "E267.128", {"start": v(21572.5, 2850) * mm, "end": v(21572.5, 1250) * mm});
            skLineSegment(sketch, "E267.129", {"start": v(20810, 1250) * mm, "end": v(21572.5, 1250) * mm});
            skLineSegment(sketch, "E267.130", {"start": v(20810, 2850) * mm, "end": v(20810, 1250) * mm});
            skLineSegment(sketch, "E267.131", {"start": v(15810, 2900) * mm, "end": v(15047.5, 2900) * mm});
            skLineSegment(sketch, "E267.132", {"start": v(18610, 2900) * mm, "end": v(18610, 3750) * mm});
            skLineSegment(sketch, "E267.133", {"start": v(11410, 2900) * mm, "end": v(11410, 3750) * mm});
            skLineSegment(sketch, "E267.134", {"start": v(15810, 2850) * mm, "end": v(15047.5, 2850) * mm});
            skLineSegment(sketch, "E267.135", {"start": v(18610, 3750) * mm, "end": v(17847.5, 3750) * mm});
            skLineSegment(sketch, "E267.136", {"start": v(17010, 2850) * mm, "end": v(17010, 1250) * mm});
            skLineSegment(sketch, "E267.137", {"start": v(14210, 2900) * mm, "end": v(14972.5, 2900) * mm});
            skLineSegment(sketch, "E267.138", {"start": v(18610, 2900) * mm, "end": v(17847.5, 2900) * mm});
            skLineSegment(sketch, "E267.139", {"start": v(13060, 1200) * mm, "end": v(11360, 1200) * mm});
            skPoint(sketch, "E267.140", {"position": v(18660, 1200) * mm});
            skLineSegment(sketch, "E267.141", {"start": v(13010, 2900) * mm, "end": v(12247.5, 2900) * mm});
            skLineSegment(sketch, "E267.142", {"start": v(13010, 1250) * mm, "end": v(12247.5, 1250) * mm});
            skLineSegment(sketch, "E267.143", {"start": v(18660, 1200) * mm, "end": v(16960, 1200) * mm});
            skLineSegment(sketch, "E267.144", {"start": v(17010, 2850) * mm, "end": v(17772.5, 2850) * mm});
            skLineSegment(sketch, "E267.145", {"start": v(13010, 2850) * mm, "end": v(13010, 1250) * mm});
            skLineSegment(sketch, "E267.146", {"start": v(18610, 1250) * mm, "end": v(17847.5, 1250) * mm});
            skLineSegment(sketch, "E267.147", {"start": v(15047.5, 2850) * mm, "end": v(15047.5, 1250) * mm});
            skLineSegment(sketch, "E267.148", {"start": v(16960, 1200) * mm, "end": v(16960, 3800) * mm});
            skLineSegment(sketch, "E267.149", {"start": v(13010, 2850) * mm, "end": v(12247.5, 2850) * mm});
            skLineSegment(sketch, "E267.150", {"start": v(17010, 2900) * mm, "end": v(17772.5, 2900) * mm});
            skLineSegment(sketch, "E267.151", {"start": v(15047.5, 2900) * mm, "end": v(15047.5, 3750) * mm});
            skPoint(sketch, "E267.152", {"position": v(15860, 1200) * mm});
            skLineSegment(sketch, "E267.153", {"start": v(15810, 2900) * mm, "end": v(15810, 3750) * mm});
            skLineSegment(sketch, "E267.154", {"start": v(11410, 2850) * mm, "end": v(11410, 1250) * mm});
            skLineSegment(sketch, "E267.155", {"start": v(15810, 2850) * mm, "end": v(15810, 1250) * mm});
            skLineSegment(sketch, "E267.156", {"start": v(11360, 3800) * mm, "end": v(13060, 3800) * mm});
            skLineSegment(sketch, "E267.157", {"start": v(17010, 1250) * mm, "end": v(17772.5, 1250) * mm});
            skLineSegment(sketch, "E267.158", {"start": v(18610, 2850) * mm, "end": v(17847.5, 2850) * mm});
            skLineSegment(sketch, "E267.159", {"start": v(17010, 3750) * mm, "end": v(17772.5, 3750) * mm});
            skLineSegment(sketch, "E267.160", {"start": v(17810, 1200) * mm, "end": v(17810, 3800) * mm});
            skLineSegment(sketch, "E267.161", {"start": v(14160, 1200) * mm, "end": v(14160, 3800) * mm});
            skLineSegment(sketch, "E267.162", {"start": v(11410, 1250) * mm, "end": v(12172.5, 1250) * mm});
            skLineSegment(sketch, "E267.163", {"start": v(17010, 2900) * mm, "end": v(17010, 3750) * mm});
            skPoint(sketch, "E267.164", {"position": v(13060, 1200) * mm});
            skLineSegment(sketch, "E267.165", {"start": v(13010, 2900) * mm, "end": v(13010, 3750) * mm});
            skLineSegment(sketch, "E267.166", {"start": v(18660, 3800) * mm, "end": v(18660, 1200) * mm});
            skLineSegment(sketch, "E267.167", {"start": v(12210, 1200) * mm, "end": v(12210, 3800) * mm});
            skLineSegment(sketch, "E267.168", {"start": v(11410, 2850) * mm, "end": v(12172.5, 2850) * mm});
            skLineSegment(sketch, "E267.169", {"start": v(15810, 3750) * mm, "end": v(15047.5, 3750) * mm});
            skLineSegment(sketch, "E267.170", {"start": v(15860, 1200) * mm, "end": v(14160, 1200) * mm});
            skLineSegment(sketch, "E267.171", {"start": v(13060, 3800) * mm, "end": v(13060, 1200) * mm});
            skLineSegment(sketch, "E267.172", {"start": v(11410, 2900) * mm, "end": v(12172.5, 2900) * mm});
            skLineSegment(sketch, "E267.173", {"start": v(14210, 1250) * mm, "end": v(14972.5, 1250) * mm});
            skLineSegment(sketch, "E267.174", {"start": v(14160, 3800) * mm, "end": v(15860, 3800) * mm});
            skLineSegment(sketch, "E267.175", {"start": v(14210, 2850) * mm, "end": v(14210, 1250) * mm});
            skLineSegment(sketch, "E267.176", {"start": v(14210, 2850) * mm, "end": v(14972.5, 2850) * mm});
            skLineSegment(sketch, "E267.177", {"start": v(11360, 1200) * mm, "end": v(11360, 3800) * mm});
            skLineSegment(sketch, "E267.178", {"start": v(18610, 2850) * mm, "end": v(18610, 1250) * mm});
            skLineSegment(sketch, "E267.179", {"start": v(15010, 1200) * mm, "end": v(15010, 3800) * mm});
            skLineSegment(sketch, "E267.180", {"start": v(13010, 3750) * mm, "end": v(12247.5, 3750) * mm});
            skLineSegment(sketch, "E267.181", {"start": v(11410, 3750) * mm, "end": v(12172.5, 3750) * mm});
            skLineSegment(sketch, "E267.182", {"start": v(14210, 3750) * mm, "end": v(14972.5, 3750) * mm});
            skLineSegment(sketch, "E267.183", {"start": v(16960, 3800) * mm, "end": v(18660, 3800) * mm});
            skLineSegment(sketch, "E267.184", {"start": v(14972.5, 2900) * mm, "end": v(14972.5, 3750) * mm});
            skLineSegment(sketch, "E267.185", {"start": v(15810, 1250) * mm, "end": v(15047.5, 1250) * mm});
            skLineSegment(sketch, "E267.186", {"start": v(12172.5, 2850) * mm, "end": v(12172.5, 1250) * mm});
            skLineSegment(sketch, "E267.187", {"start": v(14210, 2900) * mm, "end": v(14210, 3750) * mm});
            skLineSegment(sketch, "E267.188", {"start": v(15860, 3800) * mm, "end": v(15860, 1200) * mm});
            skLineSegment(sketch, "E267.189", {"start": v(17847.5, 2850) * mm, "end": v(17847.5, 1250) * mm});
            skLineSegment(sketch, "E267.190", {"start": v(12172.5, 2900) * mm, "end": v(12172.5, 3750) * mm});
            skLineSegment(sketch, "E267.191", {"start": v(14972.5, 2850) * mm, "end": v(14972.5, 1250) * mm});
            skLineSegment(sketch, "E267.192", {"start": v(17847.5, 2900) * mm, "end": v(17847.5, 3750) * mm});
            skLineSegment(sketch, "E267.193", {"start": v(17772.5, 2900) * mm, "end": v(17772.5, 3750) * mm});
            skLineSegment(sketch, "E267.194", {"start": v(12247.5, 2900) * mm, "end": v(12247.5, 3750) * mm});
            skLineSegment(sketch, "E267.195", {"start": v(17772.5, 2850) * mm, "end": v(17772.5, 1250) * mm});
            skLineSegment(sketch, "E267.196", {"start": v(12247.5, 2850) * mm, "end": v(12247.5, 1250) * mm});
            skLineSegment(sketch, "E267.197", {"start": v(6410, 2900) * mm, "end": v(5647.5, 2900) * mm});
            skLineSegment(sketch, "E267.198", {"start": v(9210, 2900) * mm, "end": v(9210, 3750) * mm});
            skLineSegment(sketch, "E267.199", {"start": v(2010, 2900) * mm, "end": v(2010, 3750) * mm});
            skLineSegment(sketch, "E267.200", {"start": v(6410, 2850) * mm, "end": v(5647.5, 2850) * mm});
            skLineSegment(sketch, "E267.201", {"start": v(9210, 3750) * mm, "end": v(8447.5, 3750) * mm});
            skLineSegment(sketch, "E267.202", {"start": v(7610, 2850) * mm, "end": v(7610, 1250) * mm});
            skLineSegment(sketch, "E267.203", {"start": v(4810, 2900) * mm, "end": v(5572.5, 2900) * mm});
            skLineSegment(sketch, "E267.204", {"start": v(9210, 2900) * mm, "end": v(8447.5, 2900) * mm});
            skLineSegment(sketch, "E267.205", {"start": v(3660, 1200) * mm, "end": v(1960, 1200) * mm});
            skPoint(sketch, "E267.206", {"position": v(9260, 1200) * mm});
            skLineSegment(sketch, "E267.207", {"start": v(3610, 2900) * mm, "end": v(2847.5, 2900) * mm});
            skLineSegment(sketch, "E267.208", {"start": v(3610, 1250) * mm, "end": v(2847.5, 1250) * mm});
            skLineSegment(sketch, "E267.209", {"start": v(9260, 1200) * mm, "end": v(7560, 1200) * mm});
            skLineSegment(sketch, "E267.210", {"start": v(7610, 2850) * mm, "end": v(8372.5, 2850) * mm});
            skLineSegment(sketch, "E267.211", {"start": v(3610, 2850) * mm, "end": v(3610, 1250) * mm});
            skLineSegment(sketch, "E267.212", {"start": v(9210, 1250) * mm, "end": v(8447.5, 1250) * mm});
            skLineSegment(sketch, "E267.213", {"start": v(5647.5, 2850) * mm, "end": v(5647.5, 1250) * mm});
            skLineSegment(sketch, "E267.214", {"start": v(7560, 1200) * mm, "end": v(7560, 3800) * mm});
            skLineSegment(sketch, "E267.215", {"start": v(3610, 2850) * mm, "end": v(2847.5, 2850) * mm});
            skLineSegment(sketch, "E267.216", {"start": v(7610, 2900) * mm, "end": v(8372.5, 2900) * mm});
            skLineSegment(sketch, "E267.217", {"start": v(5647.5, 2900) * mm, "end": v(5647.5, 3750) * mm});
            skPoint(sketch, "E267.218", {"position": v(6460, 1200) * mm});
            skLineSegment(sketch, "E267.219", {"start": v(6410, 2900) * mm, "end": v(6410, 3750) * mm});
            skLineSegment(sketch, "E267.220", {"start": v(2010, 2850) * mm, "end": v(2010, 1250) * mm});
            skLineSegment(sketch, "E267.221", {"start": v(6410, 2850) * mm, "end": v(6410, 1250) * mm});
            skLineSegment(sketch, "E267.222", {"start": v(1960, 3800) * mm, "end": v(3660, 3800) * mm});
            skLineSegment(sketch, "E267.223", {"start": v(7610, 1250) * mm, "end": v(8372.5, 1250) * mm});
            skLineSegment(sketch, "E267.224", {"start": v(9210, 2850) * mm, "end": v(8447.5, 2850) * mm});
            skLineSegment(sketch, "E267.225", {"start": v(7610, 3750) * mm, "end": v(8372.5, 3750) * mm});
            skLineSegment(sketch, "E267.226", {"start": v(8410, 1200) * mm, "end": v(8410, 3800) * mm});
            skLineSegment(sketch, "E267.227", {"start": v(4760, 1200) * mm, "end": v(4760, 3800) * mm});
            skLineSegment(sketch, "E267.228", {"start": v(2010, 1250) * mm, "end": v(2772.5, 1250) * mm});
            skLineSegment(sketch, "E267.229", {"start": v(7610, 2900) * mm, "end": v(7610, 3750) * mm});
            skPoint(sketch, "E267.230", {"position": v(3660, 1200) * mm});
            skLineSegment(sketch, "E267.231", {"start": v(3610, 2900) * mm, "end": v(3610, 3750) * mm});
            skLineSegment(sketch, "E267.232", {"start": v(9260, 3800) * mm, "end": v(9260, 1200) * mm});
            skLineSegment(sketch, "E267.233", {"start": v(2810, 1200) * mm, "end": v(2810, 3800) * mm});
            skLineSegment(sketch, "E267.234", {"start": v(2010, 2850) * mm, "end": v(2772.5, 2850) * mm});
            skLineSegment(sketch, "E267.235", {"start": v(6410, 3750) * mm, "end": v(5647.5, 3750) * mm});
            skLineSegment(sketch, "E267.236", {"start": v(6460, 1200) * mm, "end": v(4760, 1200) * mm});
            skLineSegment(sketch, "E267.237", {"start": v(3660, 3800) * mm, "end": v(3660, 1200) * mm});
            skLineSegment(sketch, "E267.238", {"start": v(2010, 2900) * mm, "end": v(2772.5, 2900) * mm});
            skLineSegment(sketch, "E267.239", {"start": v(4810, 1250) * mm, "end": v(5572.5, 1250) * mm});
            skLineSegment(sketch, "E267.240", {"start": v(4760, 3800) * mm, "end": v(6460, 3800) * mm});
            skLineSegment(sketch, "E267.241", {"start": v(4810, 2850) * mm, "end": v(4810, 1250) * mm});
            skLineSegment(sketch, "E267.242", {"start": v(4810, 2850) * mm, "end": v(5572.5, 2850) * mm});
            skLineSegment(sketch, "E267.243", {"start": v(1960, 1200) * mm, "end": v(1960, 3800) * mm});
            skLineSegment(sketch, "E267.244", {"start": v(9210, 2850) * mm, "end": v(9210, 1250) * mm});
            skLineSegment(sketch, "E267.245", {"start": v(5610, 1200) * mm, "end": v(5610, 3800) * mm});
            skLineSegment(sketch, "E267.246", {"start": v(3610, 3750) * mm, "end": v(2847.5, 3750) * mm});
            skLineSegment(sketch, "E267.247", {"start": v(2010, 3750) * mm, "end": v(2772.5, 3750) * mm});
            skLineSegment(sketch, "E267.248", {"start": v(4810, 3750) * mm, "end": v(5572.5, 3750) * mm});
            skLineSegment(sketch, "E267.249", {"start": v(7560, 3800) * mm, "end": v(9260, 3800) * mm});
            skLineSegment(sketch, "E267.250", {"start": v(5572.5, 2900) * mm, "end": v(5572.5, 3750) * mm});
            skLineSegment(sketch, "E267.251", {"start": v(6410, 1250) * mm, "end": v(5647.5, 1250) * mm});
            skLineSegment(sketch, "E267.252", {"start": v(2772.5, 2850) * mm, "end": v(2772.5, 1250) * mm});
            skLineSegment(sketch, "E267.253", {"start": v(4810, 2900) * mm, "end": v(4810, 3750) * mm});
            skLineSegment(sketch, "E267.254", {"start": v(6460, 3800) * mm, "end": v(6460, 1200) * mm});
            skLineSegment(sketch, "E267.255", {"start": v(8447.5, 2850) * mm, "end": v(8447.5, 1250) * mm});
            skLineSegment(sketch, "E267.256", {"start": v(2772.5, 2900) * mm, "end": v(2772.5, 3750) * mm});
            skLineSegment(sketch, "E267.257", {"start": v(5572.5, 2850) * mm, "end": v(5572.5, 1250) * mm});
            skLineSegment(sketch, "E267.258", {"start": v(8447.5, 2900) * mm, "end": v(8447.5, 3750) * mm});
            skLineSegment(sketch, "E267.259", {"start": v(8372.5, 2900) * mm, "end": v(8372.5, 3750) * mm});
            skLineSegment(sketch, "E267.260", {"start": v(2847.5, 2900) * mm, "end": v(2847.5, 3750) * mm});
            skLineSegment(sketch, "E267.261", {"start": v(8372.5, 2850) * mm, "end": v(8372.5, 1250) * mm});
            skLineSegment(sketch, "E267.262", {"start": v(2847.5, 2850) * mm, "end": v(2847.5, 1250) * mm});
            skLineSegment(sketch, "E267.263", {"start": v(28060, 1200) * mm, "end": v(18660, 1200) * mm});
            skPoint(sketch, "E268", {"position": v(35560, 1200) * mm});
            skSolve(sketch);
        }
        {
            var Q0;
            Q0 = qSketchRegion(id + "F22", true);
            extrude(context, id + "F23", {"entities" : qUnion([Q0]), "depth" : 50 * mm, "offsetDistance" : 25 * mm});
        }
        {
            var Q0;
            Q0=makeQuery(id+"F5.boolean.opBoolean","MERGE",FACE,{"derivedFrom":[makeQuery(id+"F3.boolean.opBoolean","COPY",FACE,{"derivedFrom":makeQuery(id+"F3.opExtrude","SWEPT_FACE",FACE,{"disambiguationData":[OSD([sQuery(id+"F2.wireOp",EDGE,"E19.9")])]})}),makeQuery(id+"F5.opExtrude","SWEPT_FACE",FACE,{"disambiguationData":[OSD([sQuery(id+"F4.wireOp",EDGE,"E34.0")])]})]});
            var sketch = newSketch(context, id + "F24", { "sketchPlane" : qUnion([Q0])});
            skLineSegment(sketch, "E269.bottom", {"start": v(27160, 2400) * mm, "end": v(28260, 2400) * mm});
            skLineSegment(sketch, "E269.top", {"start": v(27160, 0) * mm, "end": v(28260, 0) * mm});
            skLineSegment(sketch, "E269.left", {"start": v(27160, 2400) * mm, "end": v(27160, 0) * mm});
            skLineSegment(sketch, "E269.right", {"start": v(28260, 2400) * mm, "end": v(28260, 0) * mm});
            skLineSegment(sketch, "E270.bottom", {"start": v(23730, 3200) * mm, "end": v(24830, 3200) * mm});
            skLineSegment(sketch, "E270.top", {"start": v(23730, 1100) * mm, "end": v(24830, 1100) * mm});
            skLineSegment(sketch, "E270.left", {"start": v(23730, 3200) * mm, "end": v(23730, 1100) * mm});
            skLineSegment(sketch, "E270.right", {"start": v(24830, 3200) * mm, "end": v(24830, 1100) * mm});
            skLineSegment(sketch, "E271.bottom", {"start": v(20660, 3200) * mm, "end": v(19560, 3200) * mm});
            skLineSegment(sketch, "E271.top", {"start": v(20660, 1100) * mm, "end": v(19560, 1100) * mm});
            skLineSegment(sketch, "E271.left", {"start": v(20660, 3200) * mm, "end": v(20660, 1100) * mm});
            skLineSegment(sketch, "E271.right", {"start": v(19560, 3200) * mm, "end": v(19560, 1100) * mm});
            skLineSegment(sketch, "E272.bottom", {"start": v(16660, 3200) * mm, "end": v(15560, 3200) * mm});
            skLineSegment(sketch, "E272.top", {"start": v(16660, 1100) * mm, "end": v(15560, 1100) * mm});
            skLineSegment(sketch, "E272.left", {"start": v(16660, 3200) * mm, "end": v(16660, 1100) * mm});
            skLineSegment(sketch, "E272.right", {"start": v(15560, 3200) * mm, "end": v(15560, 1100) * mm});
            skLineSegment(sketch, "E273.bottom", {"start": v(12430, 3200) * mm, "end": v(11330, 3200) * mm});
            skLineSegment(sketch, "E273.top", {"start": v(12430, 1100) * mm, "end": v(11330, 1100) * mm});
            skLineSegment(sketch, "E273.left", {"start": v(12430, 3200) * mm, "end": v(12430, 1100) * mm});
            skLineSegment(sketch, "E273.right", {"start": v(11330, 3200) * mm, "end": v(11330, 1100) * mm});
            skLineSegment(sketch, "E274.bottom", {"start": v(6900, 3200) * mm, "end": v(5800, 3200) * mm});
            skLineSegment(sketch, "E274.top", {"start": v(6900, 1100) * mm, "end": v(5800, 1100) * mm});
            skLineSegment(sketch, "E274.left", {"start": v(6900, 3200) * mm, "end": v(6900, 1100) * mm});
            skLineSegment(sketch, "E274.right", {"start": v(5800, 3200) * mm, "end": v(5800, 1100) * mm});
            skLineSegment(sketch, "E275.bottom", {"start": v(1480, 3800) * mm, "end": v(3180, 3800) * mm});
            skLineSegment(sketch, "E275.top", {"start": v(1480, 1200) * mm, "end": v(3180, 1200) * mm});
            skLineSegment(sketch, "E275.left", {"start": v(1480, 3800) * mm, "end": v(1480, 1200) * mm});
            skLineSegment(sketch, "E275.right", {"start": v(3180, 3800) * mm, "end": v(3180, 1200) * mm});
            skSolve(sketch);
        }
        {
            var Q0;
            Q0 = qSketchRegion(id + "F24", true);
            extrude(context, id + "F25", {"entities" : qUnion([Q0]), "operationType" : NewBodyOperationType.REMOVE, "oppositeDirection" : true, "depth" : 600 * mm, "offsetDistance" : 25 * mm});
        }
        {
            var Q0;
            Q0=makeQuery(id+"F1.opExtrude","SWEPT_FACE",FACE,{"disambiguationData":[OSD([sQuery(id+"F0.wireOp",EDGE,"E16.4")])]});
            var sketch = newSketch(context, id + "F26", { "sketchPlane" : qUnion([Q0])});
            skLineSegment(sketch, "E276.0", {"start": v(-27160, 2400) * mm, "end": v(-28260, 2400) * mm});
            skLineSegment(sketch, "E276.1", {"start": v(-27160, 0) * mm, "end": v(-28260, 0) * mm});
            skLineSegment(sketch, "E276.2", {"start": v(-27160, 2400) * mm, "end": v(-27160, 0) * mm});
            skLineSegment(sketch, "E276.3", {"start": v(-28260, 2400) * mm, "end": v(-28260, 0) * mm});
            skLineSegment(sketch, "E276.4", {"start": v(-23730, 3200) * mm, "end": v(-24830, 3200) * mm});
            skLineSegment(sketch, "E276.5", {"start": v(-23730, 1100) * mm, "end": v(-24830, 1100) * mm});
            skLineSegment(sketch, "E276.6", {"start": v(-23730, 3200) * mm, "end": v(-23730, 1100) * mm});
            skLineSegment(sketch, "E276.7", {"start": v(-24830, 3200) * mm, "end": v(-24830, 1100) * mm});
            skLineSegment(sketch, "E276.8", {"start": v(-20660, 3200) * mm, "end": v(-19560, 3200) * mm});
            skLineSegment(sketch, "E276.9", {"start": v(-20660, 1100) * mm, "end": v(-19560, 1100) * mm});
            skLineSegment(sketch, "E276.10", {"start": v(-20660, 3200) * mm, "end": v(-20660, 1100) * mm});
            skLineSegment(sketch, "E276.11", {"start": v(-19560, 3200) * mm, "end": v(-19560, 1100) * mm});
            skLineSegment(sketch, "E276.12", {"start": v(-16660, 3200) * mm, "end": v(-15560, 3200) * mm});
            skLineSegment(sketch, "E276.13", {"start": v(-16660, 1100) * mm, "end": v(-15560, 1100) * mm});
            skLineSegment(sketch, "E276.14", {"start": v(-16660, 3200) * mm, "end": v(-16660, 1100) * mm});
            skLineSegment(sketch, "E276.15", {"start": v(-15560, 3200) * mm, "end": v(-15560, 1100) * mm});
            skLineSegment(sketch, "E276.16", {"start": v(-12430, 3200) * mm, "end": v(-11330, 3200) * mm});
            skLineSegment(sketch, "E276.17", {"start": v(-12430, 1100) * mm, "end": v(-11330, 1100) * mm});
            skLineSegment(sketch, "E276.18", {"start": v(-12430, 3200) * mm, "end": v(-12430, 1100) * mm});
            skLineSegment(sketch, "E276.19", {"start": v(-11330, 3200) * mm, "end": v(-11330, 1100) * mm});
            skLineSegment(sketch, "E276.20", {"start": v(-6900, 3200) * mm, "end": v(-5800, 3200) * mm});
            skLineSegment(sketch, "E276.21", {"start": v(-6900, 1100) * mm, "end": v(-5800, 1100) * mm});
            skLineSegment(sketch, "E276.22", {"start": v(-6900, 3200) * mm, "end": v(-6900, 1100) * mm});
            skLineSegment(sketch, "E276.23", {"start": v(-5800, 3200) * mm, "end": v(-5800, 1100) * mm});
            skLineSegment(sketch, "E276.24", {"start": v(-1480, 3800) * mm, "end": v(-3180, 3800) * mm});
            skLineSegment(sketch, "E276.25", {"start": v(-1480, 1200) * mm, "end": v(-3180, 1200) * mm});
            skLineSegment(sketch, "E276.26", {"start": v(-1480, 3800) * mm, "end": v(-1480, 1200) * mm});
            skLineSegment(sketch, "E276.27", {"start": v(-3180, 3800) * mm, "end": v(-3180, 1200) * mm});
            skSolve(sketch);
        }
        {
            var Q0;
            Q0 = qSketchRegion(id + "F26", true);
            extrude(context, id + "F27", {"entities" : qUnion([Q0]), "oppositeDirection" : true, "depth" : 100 * mm, "offsetDistance" : 25 * mm});
        }
        {
            var Q0;
            Q0=makeQuery(id+"F27.opExtrude","CAP_FACE",FACE,{"disambiguationData":[OSD([sQuery(id+"F26.wireOp",EDGE,"E276.0"),sQuery(id+"F26.wireOp",EDGE,"E276.1"),sQuery(id+"F26.wireOp",EDGE,"E276.2"),sQuery(id+"F26.wireOp",EDGE,"E276.3")])],"isStart":false});
            var sketch = newSketch(context, id + "F28", { "sketchPlane" : qUnion([Q0])});
            skLineSegment(sketch, "E277.0.0", {"start": v(27160, 0) * mm, "end": v(28260, 0) * mm});
            skLineSegment(sketch, "E277.0.1", {"start": v(28260, 0) * mm, "end": v(28260, 2400) * mm});
            skLineSegment(sketch, "E277.0.2", {"start": v(28260, 2400) * mm, "end": v(27160, 2400) * mm});
            skLineSegment(sketch, "E277.0.3", {"start": v(27160, 2400) * mm, "end": v(27160, 0) * mm});
            skLineSegment(sketch, "E278.0.0", {"start": v(1480, 1200) * mm, "end": v(3180, 1200) * mm});
            skLineSegment(sketch, "E278.0.1", {"start": v(3180, 1200) * mm, "end": v(3180, 3800) * mm});
            skLineSegment(sketch, "E278.0.2", {"start": v(3180, 3800) * mm, "end": v(1480, 3800) * mm});
            skLineSegment(sketch, "E278.0.3", {"start": v(1480, 3800) * mm, "end": v(1480, 1200) * mm});
            skLineSegment(sketch, "E279.0.0", {"start": v(5800, 1100) * mm, "end": v(6900, 1100) * mm});
            skLineSegment(sketch, "E279.0.1", {"start": v(6900, 1100) * mm, "end": v(6900, 3200) * mm});
            skLineSegment(sketch, "E279.0.2", {"start": v(6900, 3200) * mm, "end": v(5800, 3200) * mm});
            skLineSegment(sketch, "E279.0.3", {"start": v(5800, 3200) * mm, "end": v(5800, 1100) * mm});
            skLineSegment(sketch, "E280", {"start": v(2330, 3800) * mm, "end": v(2330, 1200) * mm, "construction": true});
            skLineSegment(sketch, "E281.bottom", {"start": v(1530, 2850) * mm, "end": v(2292.5, 2850) * mm});
            skLineSegment(sketch, "E281.top", {"start": v(1530, 1250) * mm, "end": v(2292.5, 1250) * mm});
            skLineSegment(sketch, "E281.left", {"start": v(1530, 2850) * mm, "end": v(1530, 1250) * mm});
            skLineSegment(sketch, "E281.right", {"start": v(2292.5, 2850) * mm, "end": v(2292.5, 1250) * mm});
            skLineSegment(sketch, "E282.bottom", {"start": v(1530, 2900) * mm, "end": v(2292.5, 2900) * mm});
            skLineSegment(sketch, "E282.top", {"start": v(1530, 3750) * mm, "end": v(2292.5, 3750) * mm});
            skLineSegment(sketch, "E282.left", {"start": v(1530, 2900) * mm, "end": v(1530, 3750) * mm});
            skLineSegment(sketch, "E282.right", {"start": v(2292.5, 2900) * mm, "end": v(2292.5, 3750) * mm});
            skLineSegment(sketch, "E283.MirrorCS", {"start": v(3130, 2850) * mm, "end": v(2367.5, 2850) * mm});
            skLineSegment(sketch, "E284.MirrorCS", {"start": v(2367.5, 2850) * mm, "end": v(2367.5, 1250) * mm});
            skLineSegment(sketch, "E285.MirrorCS", {"start": v(3130, 2850) * mm, "end": v(3130, 1250) * mm});
            skLineSegment(sketch, "E286.MirrorCS", {"start": v(3130, 1250) * mm, "end": v(2367.5, 1250) * mm});
            skLineSegment(sketch, "E287.MirrorCS", {"start": v(3130, 2900) * mm, "end": v(2367.5, 2900) * mm});
            skLineSegment(sketch, "E288.MirrorCS", {"start": v(2367.5, 2900) * mm, "end": v(2367.5, 3750) * mm});
            skLineSegment(sketch, "E289.MirrorCS", {"start": v(3130, 2900) * mm, "end": v(3130, 3750) * mm});
            skLineSegment(sketch, "E290.MirrorCS", {"start": v(3130, 3750) * mm, "end": v(2367.5, 3750) * mm});
            skLineSegment(sketch, "E291.0", {"start": v(27210, 2350) * mm, "end": v(27210, 50) * mm});
            skLineSegment(sketch, "E291.1", {"start": v(28210, 2350) * mm, "end": v(27210, 2350) * mm});
            skLineSegment(sketch, "E291.2", {"start": v(28210, 50) * mm, "end": v(28210, 2350) * mm});
            skLineSegment(sketch, "E291.3", {"start": v(27210, 50) * mm, "end": v(28210, 50) * mm});
            skLineSegment(sketch, "E292.bottom", {"start": v(5850, 2400) * mm, "end": v(6850, 2400) * mm});
            skLineSegment(sketch, "E292.top", {"start": v(5850, 1150) * mm, "end": v(6850, 1150) * mm});
            skLineSegment(sketch, "E292.left", {"start": v(5850, 2400) * mm, "end": v(5850, 1150) * mm});
            skLineSegment(sketch, "E292.right", {"start": v(6850, 2400) * mm, "end": v(6850, 1150) * mm});
            skLineSegment(sketch, "E293.bottom", {"start": v(5850, 2450) * mm, "end": v(6850, 2450) * mm});
            skLineSegment(sketch, "E293.top", {"start": v(5850, 3150) * mm, "end": v(6850, 3150) * mm});
            skLineSegment(sketch, "E293.left", {"start": v(5850, 2450) * mm, "end": v(5850, 3150) * mm});
            skLineSegment(sketch, "E293.right", {"start": v(6850, 2450) * mm, "end": v(6850, 3150) * mm});
            skPoint(sketch, "E294", {"position": v(11330, 1100) * mm});
            skPoint(sketch, "E295", {"position": v(15560, 1100) * mm});
            skPoint(sketch, "E296", {"position": v(19560, 1100) * mm});
            skPoint(sketch, "E297", {"position": v(23730, 1100) * mm});
            skLineSegment(sketch, "E298.0.0", {"start": v(11330, 1100) * mm, "end": v(12430, 1100) * mm});
            skLineSegment(sketch, "E298.0.1", {"start": v(12430, 1100) * mm, "end": v(12430, 3200) * mm});
            skLineSegment(sketch, "E298.0.2", {"start": v(12430, 3200) * mm, "end": v(11330, 3200) * mm});
            skLineSegment(sketch, "E298.0.3", {"start": v(11330, 3200) * mm, "end": v(11330, 1100) * mm});
            skLineSegment(sketch, "E299.bottom", {"start": v(11380, 2400) * mm, "end": v(12380, 2400) * mm});
            skLineSegment(sketch, "E299.top", {"start": v(11380, 1150) * mm, "end": v(12380, 1150) * mm});
            skLineSegment(sketch, "E299.left", {"start": v(11380, 2400) * mm, "end": v(11380, 1150) * mm});
            skLineSegment(sketch, "E299.right", {"start": v(12380, 2400) * mm, "end": v(12380, 1150) * mm});
            skLineSegment(sketch, "E300.bottom", {"start": v(11380, 2450) * mm, "end": v(12380, 2450) * mm});
            skLineSegment(sketch, "E300.top", {"start": v(11380, 3150) * mm, "end": v(12380, 3150) * mm});
            skLineSegment(sketch, "E300.left", {"start": v(11380, 2450) * mm, "end": v(11380, 3150) * mm});
            skLineSegment(sketch, "E300.right", {"start": v(12380, 2450) * mm, "end": v(12380, 3150) * mm});
            skLineSegment(sketch, "E301.0.0", {"start": v(15560, 1100) * mm, "end": v(16660, 1100) * mm});
            skLineSegment(sketch, "E301.0.1", {"start": v(16660, 1100) * mm, "end": v(16660, 3200) * mm});
            skLineSegment(sketch, "E301.0.2", {"start": v(16660, 3200) * mm, "end": v(15560, 3200) * mm});
            skLineSegment(sketch, "E301.0.3", {"start": v(15560, 3200) * mm, "end": v(15560, 1100) * mm});
            skLineSegment(sketch, "E302.bottom", {"start": v(15610, 2400) * mm, "end": v(16610, 2400) * mm});
            skLineSegment(sketch, "E302.top", {"start": v(15610, 1150) * mm, "end": v(16610, 1150) * mm});
            skLineSegment(sketch, "E302.left", {"start": v(15610, 2400) * mm, "end": v(15610, 1150) * mm});
            skLineSegment(sketch, "E302.right", {"start": v(16610, 2400) * mm, "end": v(16610, 1150) * mm});
            skLineSegment(sketch, "E303.bottom", {"start": v(15610, 2450) * mm, "end": v(16610, 2450) * mm});
            skLineSegment(sketch, "E303.top", {"start": v(15610, 3150) * mm, "end": v(16610, 3150) * mm});
            skLineSegment(sketch, "E303.left", {"start": v(15610, 2450) * mm, "end": v(15610, 3150) * mm});
            skLineSegment(sketch, "E303.right", {"start": v(16610, 2450) * mm, "end": v(16610, 3150) * mm});
            skLineSegment(sketch, "E304.0.0", {"start": v(19560, 1100) * mm, "end": v(20660, 1100) * mm});
            skLineSegment(sketch, "E304.0.1", {"start": v(20660, 1100) * mm, "end": v(20660, 3200) * mm});
            skLineSegment(sketch, "E304.0.2", {"start": v(20660, 3200) * mm, "end": v(19560, 3200) * mm});
            skLineSegment(sketch, "E304.0.3", {"start": v(19560, 3200) * mm, "end": v(19560, 1100) * mm});
            skLineSegment(sketch, "E305.bottom", {"start": v(19610, 2400) * mm, "end": v(20610, 2400) * mm});
            skLineSegment(sketch, "E305.top", {"start": v(19610, 1150) * mm, "end": v(20610, 1150) * mm});
            skLineSegment(sketch, "E305.left", {"start": v(19610, 2400) * mm, "end": v(19610, 1150) * mm});
            skLineSegment(sketch, "E305.right", {"start": v(20610, 2400) * mm, "end": v(20610, 1150) * mm});
            skLineSegment(sketch, "E306.bottom", {"start": v(19610, 2450) * mm, "end": v(20610, 2450) * mm});
            skLineSegment(sketch, "E306.top", {"start": v(19610, 3150) * mm, "end": v(20610, 3150) * mm});
            skLineSegment(sketch, "E306.left", {"start": v(19610, 2450) * mm, "end": v(19610, 3150) * mm});
            skLineSegment(sketch, "E306.right", {"start": v(20610, 2450) * mm, "end": v(20610, 3150) * mm});
            skLineSegment(sketch, "E307.0.0", {"start": v(23730, 1100) * mm, "end": v(24830, 1100) * mm});
            skLineSegment(sketch, "E307.0.1", {"start": v(24830, 1100) * mm, "end": v(24830, 3200) * mm});
            skLineSegment(sketch, "E307.0.2", {"start": v(24830, 3200) * mm, "end": v(23730, 3200) * mm});
            skLineSegment(sketch, "E307.0.3", {"start": v(23730, 3200) * mm, "end": v(23730, 1100) * mm});
            skLineSegment(sketch, "E308.bottom", {"start": v(23780, 2400) * mm, "end": v(24780, 2400) * mm});
            skLineSegment(sketch, "E308.top", {"start": v(23780, 1150) * mm, "end": v(24780, 1150) * mm});
            skLineSegment(sketch, "E308.left", {"start": v(23780, 2400) * mm, "end": v(23780, 1150) * mm});
            skLineSegment(sketch, "E308.right", {"start": v(24780, 2400) * mm, "end": v(24780, 1150) * mm});
            skLineSegment(sketch, "E309.bottom", {"start": v(23780, 2450) * mm, "end": v(24780, 2450) * mm});
            skLineSegment(sketch, "E309.top", {"start": v(23780, 3150) * mm, "end": v(24780, 3150) * mm});
            skLineSegment(sketch, "E309.left", {"start": v(23780, 2450) * mm, "end": v(23780, 3150) * mm});
            skLineSegment(sketch, "E309.right", {"start": v(24780, 2450) * mm, "end": v(24780, 3150) * mm});
            skSolve(sketch);
        }
        {
            var Q0;
            Q0 = qSketchRegion(id + "F28", true);
            extrude(context, id + "F29", {"entities" : qUnion([Q0]), "depth" : 50 * mm, "offsetDistance" : 25 * mm});
        }
        {
            var Q0;
            Q0=makeQuery(id+"F5.boolean.opBoolean","MERGE",FACE,{"derivedFrom":[makeQuery(id+"F3.boolean.opBoolean","COPY",FACE,{"derivedFrom":makeQuery(id+"F3.opExtrude","SWEPT_FACE",FACE,{"disambiguationData":[OSD([sQuery(id+"F2.wireOp",EDGE,"E19.10")])]})}),makeQuery(id+"F5.opExtrude","SWEPT_FACE",FACE,{"disambiguationData":[OSD([sQuery(id+"F4.wireOp",EDGE,"E33.0")])]})]});
            var sketch = newSketch(context, id + "F30", { "sketchPlane" : qUnion([Q0])});
            skLineSegment(sketch, "E310.bottom", {"start": v(-24350, 3200) * mm, "end": v(-23250, 3200) * mm});
            skLineSegment(sketch, "E310.top", {"start": v(-24350, 1100) * mm, "end": v(-23250, 1100) * mm});
            skLineSegment(sketch, "E310.left", {"start": v(-24350, 3200) * mm, "end": v(-24350, 1100) * mm});
            skLineSegment(sketch, "E310.right", {"start": v(-23250, 3200) * mm, "end": v(-23250, 1100) * mm});
            skLineSegment(sketch, "E311.bottom", {"start": v(-21270, 3200) * mm, "end": v(-20170, 3200) * mm});
            skLineSegment(sketch, "E311.top", {"start": v(-21270, 1100) * mm, "end": v(-20170, 1100) * mm});
            skLineSegment(sketch, "E311.left", {"start": v(-21270, 3200) * mm, "end": v(-21270, 1100) * mm});
            skLineSegment(sketch, "E311.right", {"start": v(-20170, 3200) * mm, "end": v(-20170, 1100) * mm});
            skLineSegment(sketch, "E312.bottom", {"start": v(-18160, 3200) * mm, "end": v(-17060, 3200) * mm});
            skLineSegment(sketch, "E312.top", {"start": v(-18160, 1100) * mm, "end": v(-17060, 1100) * mm});
            skLineSegment(sketch, "E312.left", {"start": v(-18160, 3200) * mm, "end": v(-18160, 1100) * mm});
            skLineSegment(sketch, "E312.right", {"start": v(-17060, 3200) * mm, "end": v(-17060, 1100) * mm});
            skLineSegment(sketch, "E313.bottom", {"start": v(-15020, 3200) * mm, "end": v(-13920, 3200) * mm});
            skLineSegment(sketch, "E313.top", {"start": v(-15020, 1100) * mm, "end": v(-13920, 1100) * mm});
            skLineSegment(sketch, "E313.left", {"start": v(-15020, 3200) * mm, "end": v(-15020, 1100) * mm});
            skLineSegment(sketch, "E313.right", {"start": v(-13920, 3200) * mm, "end": v(-13920, 1100) * mm});
            skLineSegment(sketch, "E314.bottom", {"start": v(-11930, 3200) * mm, "end": v(-10830, 3200) * mm});
            skLineSegment(sketch, "E314.top", {"start": v(-11930, 1100) * mm, "end": v(-10830, 1100) * mm});
            skLineSegment(sketch, "E314.left", {"start": v(-11930, 3200) * mm, "end": v(-11930, 1100) * mm});
            skLineSegment(sketch, "E314.right", {"start": v(-10830, 3200) * mm, "end": v(-10830, 1100) * mm});
            skSolve(sketch);
        }
        {
            var Q0;
            Q0 = qSketchRegion(id + "F30", true);
            extrude(context, id + "F31", {"entities" : qUnion([Q0]), "operationType" : NewBodyOperationType.REMOVE, "oppositeDirection" : true, "depth" : 600 * mm, "offsetDistance" : 25 * mm});
        }
        {
            var Q0;
            Q0=makeQuery(id+"F1.opExtrude","SWEPT_FACE",FACE,{"disambiguationData":[OSD([sQuery(id+"F0.wireOp",EDGE,"E16.3")])]});
            var sketch = newSketch(context, id + "F32", { "sketchPlane" : qUnion([Q0])});
            skLineSegment(sketch, "E315.0", {"start": v(24350, 3200) * mm, "end": v(23250, 3200) * mm});
            skLineSegment(sketch, "E315.1", {"start": v(24350, 1100) * mm, "end": v(23250, 1100) * mm});
            skLineSegment(sketch, "E315.2", {"start": v(24350, 3200) * mm, "end": v(24350, 1100) * mm});
            skLineSegment(sketch, "E315.3", {"start": v(23250, 3200) * mm, "end": v(23250, 1100) * mm});
            skLineSegment(sketch, "E315.4", {"start": v(21270, 3200) * mm, "end": v(20170, 3200) * mm});
            skLineSegment(sketch, "E315.5", {"start": v(21270, 1100) * mm, "end": v(20170, 1100) * mm});
            skLineSegment(sketch, "E315.6", {"start": v(21270, 3200) * mm, "end": v(21270, 1100) * mm});
            skLineSegment(sketch, "E315.7", {"start": v(20170, 3200) * mm, "end": v(20170, 1100) * mm});
            skLineSegment(sketch, "E315.8", {"start": v(18160, 3200) * mm, "end": v(17060, 3200) * mm});
            skLineSegment(sketch, "E315.9", {"start": v(18160, 1100) * mm, "end": v(17060, 1100) * mm});
            skLineSegment(sketch, "E315.10", {"start": v(18160, 3200) * mm, "end": v(18160, 1100) * mm});
            skLineSegment(sketch, "E315.11", {"start": v(17060, 3200) * mm, "end": v(17060, 1100) * mm});
            skLineSegment(sketch, "E315.12", {"start": v(15020, 3200) * mm, "end": v(13920, 3200) * mm});
            skLineSegment(sketch, "E315.13", {"start": v(15020, 1100) * mm, "end": v(13920, 1100) * mm});
            skLineSegment(sketch, "E315.14", {"start": v(15020, 3200) * mm, "end": v(15020, 1100) * mm});
            skLineSegment(sketch, "E315.15", {"start": v(13920, 3200) * mm, "end": v(13920, 1100) * mm});
            skLineSegment(sketch, "E315.16", {"start": v(11930, 3200) * mm, "end": v(10830, 3200) * mm});
            skLineSegment(sketch, "E315.17", {"start": v(11930, 1100) * mm, "end": v(10830, 1100) * mm});
            skLineSegment(sketch, "E315.18", {"start": v(11930, 3200) * mm, "end": v(11930, 1100) * mm});
            skLineSegment(sketch, "E315.19", {"start": v(10830, 3200) * mm, "end": v(10830, 1100) * mm});
            skSolve(sketch);
        }
        {
            var Q0;
            Q0 = qSketchRegion(id + "F32", true);
            extrude(context, id + "F33", {"entities" : qUnion([Q0]), "oppositeDirection" : true, "depth" : 100 * mm, "offsetDistance" : 25 * mm});
        }
        {
            var Q0;
            Q0=makeQuery(id+"F33.opExtrude","CAP_FACE",FACE,{"disambiguationData":[OSD([sQuery(id+"F32.wireOp",EDGE,"E315.0"),sQuery(id+"F32.wireOp",EDGE,"E315.1"),sQuery(id+"F32.wireOp",EDGE,"E315.2"),sQuery(id+"F32.wireOp",EDGE,"E315.3")])],"isStart":false});
            var sketch = newSketch(context, id + "F34", { "sketchPlane" : qUnion([Q0])});
            skLineSegment(sketch, "E316.0.0", {"start": v(-24350, 1100) * mm, "end": v(-23250, 1100) * mm});
            skLineSegment(sketch, "E316.0.1", {"start": v(-23250, 1100) * mm, "end": v(-23250, 3200) * mm});
            skLineSegment(sketch, "E316.0.2", {"start": v(-23250, 3200) * mm, "end": v(-24350, 3200) * mm});
            skLineSegment(sketch, "E316.0.3", {"start": v(-24350, 3200) * mm, "end": v(-24350, 1100) * mm});
            skLineSegment(sketch, "E317.bottom", {"start": v(-24300, 2400) * mm, "end": v(-23300, 2400) * mm});
            skLineSegment(sketch, "E317.top", {"start": v(-24300, 1150) * mm, "end": v(-23300, 1150) * mm});
            skLineSegment(sketch, "E317.left", {"start": v(-24300, 2400) * mm, "end": v(-24300, 1150) * mm});
            skLineSegment(sketch, "E317.right", {"start": v(-23300, 2400) * mm, "end": v(-23300, 1150) * mm});
            skLineSegment(sketch, "E318.bottom", {"start": v(-24300, 2450) * mm, "end": v(-23300, 2450) * mm});
            skLineSegment(sketch, "E318.top", {"start": v(-24300, 3150) * mm, "end": v(-23300, 3150) * mm});
            skLineSegment(sketch, "E318.left", {"start": v(-24300, 2450) * mm, "end": v(-24300, 3150) * mm});
            skLineSegment(sketch, "E318.right", {"start": v(-23300, 2450) * mm, "end": v(-23300, 3150) * mm});
            skPoint(sketch, "E319", {"position": v(-24350, 1191.67) * mm});
            skPoint(sketch, "E320", {"position": v(-21270, 1100) * mm});
            skPoint(sketch, "E321", {"position": v(-18160, 1100) * mm});
            skPoint(sketch, "E322", {"position": v(-15020, 1100) * mm});
            skPoint(sketch, "E323", {"position": v(-11930, 1100) * mm});
            skLineSegment(sketch, "E324.0.0", {"start": v(-21270, 1100) * mm, "end": v(-20170, 1100) * mm});
            skLineSegment(sketch, "E324.0.1", {"start": v(-20170, 1100) * mm, "end": v(-20170, 3200) * mm});
            skLineSegment(sketch, "E324.0.2", {"start": v(-20170, 3200) * mm, "end": v(-21270, 3200) * mm});
            skLineSegment(sketch, "E324.0.3", {"start": v(-21270, 3200) * mm, "end": v(-21270, 1100) * mm});
            skLineSegment(sketch, "E325.bottom", {"start": v(-21220, 2400) * mm, "end": v(-20220, 2400) * mm});
            skLineSegment(sketch, "E325.top", {"start": v(-21220, 1150) * mm, "end": v(-20220, 1150) * mm});
            skLineSegment(sketch, "E325.left", {"start": v(-21220, 2400) * mm, "end": v(-21220, 1150) * mm});
            skLineSegment(sketch, "E325.right", {"start": v(-20220, 2400) * mm, "end": v(-20220, 1150) * mm});
            skLineSegment(sketch, "E326.bottom", {"start": v(-21220, 2450) * mm, "end": v(-20220, 2450) * mm});
            skLineSegment(sketch, "E326.top", {"start": v(-21220, 3150) * mm, "end": v(-20220, 3150) * mm});
            skLineSegment(sketch, "E326.left", {"start": v(-21220, 2450) * mm, "end": v(-21220, 3150) * mm});
            skLineSegment(sketch, "E326.right", {"start": v(-20220, 2450) * mm, "end": v(-20220, 3150) * mm});
            skLineSegment(sketch, "E327.0.0", {"start": v(-18160, 1100) * mm, "end": v(-17060, 1100) * mm});
            skLineSegment(sketch, "E327.0.1", {"start": v(-17060, 1100) * mm, "end": v(-17060, 3200) * mm});
            skLineSegment(sketch, "E327.0.2", {"start": v(-17060, 3200) * mm, "end": v(-18160, 3200) * mm});
            skLineSegment(sketch, "E327.0.3", {"start": v(-18160, 3200) * mm, "end": v(-18160, 1100) * mm});
            skLineSegment(sketch, "E328.bottom", {"start": v(-18110, 2400) * mm, "end": v(-17110, 2400) * mm});
            skLineSegment(sketch, "E328.top", {"start": v(-18110, 1150) * mm, "end": v(-17110, 1150) * mm});
            skLineSegment(sketch, "E328.left", {"start": v(-18110, 2400) * mm, "end": v(-18110, 1150) * mm});
            skLineSegment(sketch, "E328.right", {"start": v(-17110, 2400) * mm, "end": v(-17110, 1150) * mm});
            skLineSegment(sketch, "E329.bottom", {"start": v(-18110, 2450) * mm, "end": v(-17110, 2450) * mm});
            skLineSegment(sketch, "E329.top", {"start": v(-18110, 3150) * mm, "end": v(-17110, 3150) * mm});
            skLineSegment(sketch, "E329.left", {"start": v(-18110, 2450) * mm, "end": v(-18110, 3150) * mm});
            skLineSegment(sketch, "E329.right", {"start": v(-17110, 2450) * mm, "end": v(-17110, 3150) * mm});
            skLineSegment(sketch, "E330.0.0", {"start": v(-15020, 1100) * mm, "end": v(-13920, 1100) * mm});
            skLineSegment(sketch, "E330.0.1", {"start": v(-13920, 1100) * mm, "end": v(-13920, 3200) * mm});
            skLineSegment(sketch, "E330.0.2", {"start": v(-13920, 3200) * mm, "end": v(-15020, 3200) * mm});
            skLineSegment(sketch, "E330.0.3", {"start": v(-15020, 3200) * mm, "end": v(-15020, 1100) * mm});
            skLineSegment(sketch, "E331.bottom", {"start": v(-14970, 2400) * mm, "end": v(-13970, 2400) * mm});
            skLineSegment(sketch, "E331.top", {"start": v(-14970, 1150) * mm, "end": v(-13970, 1150) * mm});
            skLineSegment(sketch, "E331.left", {"start": v(-14970, 2400) * mm, "end": v(-14970, 1150) * mm});
            skLineSegment(sketch, "E331.right", {"start": v(-13970, 2400) * mm, "end": v(-13970, 1150) * mm});
            skLineSegment(sketch, "E332.bottom", {"start": v(-14970, 2450) * mm, "end": v(-13970, 2450) * mm});
            skLineSegment(sketch, "E332.top", {"start": v(-14970, 3150) * mm, "end": v(-13970, 3150) * mm});
            skLineSegment(sketch, "E332.left", {"start": v(-14970, 2450) * mm, "end": v(-14970, 3150) * mm});
            skLineSegment(sketch, "E332.right", {"start": v(-13970, 2450) * mm, "end": v(-13970, 3150) * mm});
            skLineSegment(sketch, "E333.0.0", {"start": v(-11930, 1100) * mm, "end": v(-10830, 1100) * mm});
            skLineSegment(sketch, "E333.0.1", {"start": v(-10830, 1100) * mm, "end": v(-10830, 3200) * mm});
            skLineSegment(sketch, "E333.0.2", {"start": v(-10830, 3200) * mm, "end": v(-11930, 3200) * mm});
            skLineSegment(sketch, "E333.0.3", {"start": v(-11930, 3200) * mm, "end": v(-11930, 1100) * mm});
            skLineSegment(sketch, "E334.bottom", {"start": v(-11880, 2400) * mm, "end": v(-10880, 2400) * mm});
            skLineSegment(sketch, "E334.top", {"start": v(-11880, 1150) * mm, "end": v(-10880, 1150) * mm});
            skLineSegment(sketch, "E334.left", {"start": v(-11880, 2400) * mm, "end": v(-11880, 1150) * mm});
            skLineSegment(sketch, "E334.right", {"start": v(-10880, 2400) * mm, "end": v(-10880, 1150) * mm});
            skLineSegment(sketch, "E335.bottom", {"start": v(-11880, 2450) * mm, "end": v(-10880, 2450) * mm});
            skLineSegment(sketch, "E335.top", {"start": v(-11880, 3150) * mm, "end": v(-10880, 3150) * mm});
            skLineSegment(sketch, "E335.left", {"start": v(-11880, 2450) * mm, "end": v(-11880, 3150) * mm});
            skLineSegment(sketch, "E335.right", {"start": v(-10880, 2450) * mm, "end": v(-10880, 3150) * mm});
            skSolve(sketch);
        }
        {
            var Q0;
            Q0 = qSketchRegion(id + "F34", true);
            extrude(context, id + "F35", {"entities" : qUnion([Q0]), "depth" : 50 * mm, "offsetDistance" : 25 * mm});
        }
        {
            var Q0;
            Q0=makeQuery(id+"F5.boolean.opBoolean","MERGE",FACE,{"derivedFrom":[makeQuery(id+"F3.boolean.opBoolean","COPY",FACE,{"derivedFrom":makeQuery(id+"F3.opExtrude","SWEPT_FACE",FACE,{"disambiguationData":[OSD([sQuery(id+"F2.wireOp",EDGE,"E19.11")])]})}),makeQuery(id+"F5.opExtrude","SWEPT_FACE",FACE,{"disambiguationData":[OSD([sQuery(id+"F4.wireOp",EDGE,"E32.0")])]})]});
            var sketch = newSketch(context, id + "F36", { "sketchPlane" : qUnion([Q0])});
            skLineSegment(sketch, "E336.bottom", {"start": v(-28360, 2400) * mm, "end": v(-27260, 2400) * mm});
            skLineSegment(sketch, "E336.top", {"start": v(-28360, 0) * mm, "end": v(-27260, 0) * mm});
            skLineSegment(sketch, "E336.left", {"start": v(-28360, 2400) * mm, "end": v(-28360, 0) * mm});
            skLineSegment(sketch, "E336.right", {"start": v(-27260, 2400) * mm, "end": v(-27260, 0) * mm});
            skLineSegment(sketch, "E337.bottom", {"start": v(-25660, 3200) * mm, "end": v(-24560, 3200) * mm});
            skLineSegment(sketch, "E337.top", {"start": v(-25660, 1100) * mm, "end": v(-24560, 1100) * mm});
            skLineSegment(sketch, "E337.left", {"start": v(-25660, 3200) * mm, "end": v(-25660, 1100) * mm});
            skLineSegment(sketch, "E337.right", {"start": v(-24560, 3200) * mm, "end": v(-24560, 1100) * mm});
            skLineSegment(sketch, "E338.bottom", {"start": v(-22100, 3200) * mm, "end": v(-21000, 3200) * mm});
            skLineSegment(sketch, "E338.top", {"start": v(-22100, 1100) * mm, "end": v(-21000, 1100) * mm});
            skLineSegment(sketch, "E338.left", {"start": v(-22100, 3200) * mm, "end": v(-22100, 1100) * mm});
            skLineSegment(sketch, "E338.right", {"start": v(-21000, 3200) * mm, "end": v(-21000, 1100) * mm});
            skLineSegment(sketch, "E339.0", {"start": v(-16960, 3800) * mm, "end": v(-18660, 3800) * mm});
            skLineSegment(sketch, "E340.0", {"start": v(-16960, 1200) * mm, "end": v(-16960, 3800) * mm});
            skLineSegment(sketch, "E341.0", {"start": v(-16960, 1200) * mm, "end": v(-18660, 1200) * mm});
            skLineSegment(sketch, "E342.0", {"start": v(-18660, 1200) * mm, "end": v(-18660, 3800) * mm});
            skLineSegment(sketch, "E343.0", {"start": v(-14160, 3800) * mm, "end": v(-15860, 3800) * mm});
            skLineSegment(sketch, "E344.0", {"start": v(-14160, 1200) * mm, "end": v(-14160, 3800) * mm});
            skLineSegment(sketch, "E345.0", {"start": v(-14160, 1200) * mm, "end": v(-15860, 1200) * mm});
            skLineSegment(sketch, "E346.0", {"start": v(-15860, 1200) * mm, "end": v(-15860, 3800) * mm});
            skLineSegment(sketch, "E347.0", {"start": v(-11360, 3800) * mm, "end": v(-13060, 3800) * mm});
            skLineSegment(sketch, "E348.0", {"start": v(-11360, 1200) * mm, "end": v(-11360, 3800) * mm});
            skLineSegment(sketch, "E349.0", {"start": v(-11360, 1200) * mm, "end": v(-13060, 1200) * mm});
            skLineSegment(sketch, "E350.0", {"start": v(-13060, 1200) * mm, "end": v(-13060, 3800) * mm});
            skLineSegment(sketch, "E351.bottom", {"start": v(-9030, 0) * mm, "end": v(-7230, 0) * mm});
            skLineSegment(sketch, "E351.top", {"start": v(-9030, 3800) * mm, "end": v(-7230, 3800) * mm});
            skLineSegment(sketch, "E351.left", {"start": v(-9030, 0) * mm, "end": v(-9030, 3800) * mm});
            skLineSegment(sketch, "E351.right", {"start": v(-7230, 0) * mm, "end": v(-7230, 3800) * mm});
            skLineSegment(sketch, "E352.bottom", {"start": v(-4620, 3800) * mm, "end": v(-2920, 3800) * mm});
            skLineSegment(sketch, "E352.top", {"start": v(-4620, 1200) * mm, "end": v(-2920, 1200) * mm});
            skLineSegment(sketch, "E352.left", {"start": v(-4620, 3800) * mm, "end": v(-4620, 1200) * mm});
            skLineSegment(sketch, "E352.right", {"start": v(-2920, 3800) * mm, "end": v(-2920, 1200) * mm});
            skSolve(sketch);
        }
        {
            var Q0;
            Q0 = qSketchRegion(id + "F36", true);
            extrude(context, id + "F37", {"entities" : qUnion([Q0]), "operationType" : NewBodyOperationType.REMOVE, "oppositeDirection" : true, "depth" : 600 * mm, "offsetDistance" : 25 * mm});
        }
        {
            var Q0;
            Q0=makeQuery(id+"F1.opExtrude","SWEPT_FACE",FACE,{"disambiguationData":[OSD([sQuery(id+"F0.wireOp",EDGE,"E16.2")])]});
            var sketch = newSketch(context, id + "F38", { "sketchPlane" : qUnion([Q0])});
            skLineSegment(sketch, "E353.0", {"start": v(28360, 2400) * mm, "end": v(27260, 2400) * mm});
            skLineSegment(sketch, "E353.1", {"start": v(28360, 0) * mm, "end": v(27260, 0) * mm});
            skLineSegment(sketch, "E353.2", {"start": v(28360, 2400) * mm, "end": v(28360, 0) * mm});
            skLineSegment(sketch, "E353.3", {"start": v(27260, 2400) * mm, "end": v(27260, 0) * mm});
            skLineSegment(sketch, "E353.4", {"start": v(25660, 3200) * mm, "end": v(24560, 3200) * mm});
            skLineSegment(sketch, "E353.5", {"start": v(25660, 1100) * mm, "end": v(24560, 1100) * mm});
            skLineSegment(sketch, "E353.6", {"start": v(25660, 3200) * mm, "end": v(25660, 1100) * mm});
            skLineSegment(sketch, "E353.7", {"start": v(24560, 3200) * mm, "end": v(24560, 1100) * mm});
            skLineSegment(sketch, "E353.8", {"start": v(22100, 3200) * mm, "end": v(21000, 3200) * mm});
            skLineSegment(sketch, "E353.9", {"start": v(22100, 1100) * mm, "end": v(21000, 1100) * mm});
            skLineSegment(sketch, "E353.10", {"start": v(22100, 3200) * mm, "end": v(22100, 1100) * mm});
            skLineSegment(sketch, "E353.11", {"start": v(21000, 3200) * mm, "end": v(21000, 1100) * mm});
            skLineSegment(sketch, "E353.12", {"start": v(16960, 3800) * mm, "end": v(18660, 3800) * mm});
            skLineSegment(sketch, "E353.13", {"start": v(16960, 1200) * mm, "end": v(16960, 3800) * mm});
            skLineSegment(sketch, "E353.14", {"start": v(16960, 1200) * mm, "end": v(18660, 1200) * mm});
            skLineSegment(sketch, "E353.15", {"start": v(18660, 1200) * mm, "end": v(18660, 3800) * mm});
            skLineSegment(sketch, "E353.16", {"start": v(14160, 3800) * mm, "end": v(15860, 3800) * mm});
            skLineSegment(sketch, "E353.17", {"start": v(14160, 1200) * mm, "end": v(14160, 3800) * mm});
            skLineSegment(sketch, "E353.18", {"start": v(14160, 1200) * mm, "end": v(15860, 1200) * mm});
            skLineSegment(sketch, "E353.19", {"start": v(15860, 1200) * mm, "end": v(15860, 3800) * mm});
            skLineSegment(sketch, "E353.20", {"start": v(11360, 3800) * mm, "end": v(13060, 3800) * mm});
            skLineSegment(sketch, "E353.21", {"start": v(11360, 1200) * mm, "end": v(11360, 3800) * mm});
            skLineSegment(sketch, "E353.22", {"start": v(11360, 1200) * mm, "end": v(13060, 1200) * mm});
            skLineSegment(sketch, "E353.23", {"start": v(13060, 1200) * mm, "end": v(13060, 3800) * mm});
            skLineSegment(sketch, "E353.24", {"start": v(9030, 0) * mm, "end": v(7230, 0) * mm});
            skLineSegment(sketch, "E353.25", {"start": v(9030, 3800) * mm, "end": v(7230, 3800) * mm});
            skLineSegment(sketch, "E353.26", {"start": v(9030, 0) * mm, "end": v(9030, 3800) * mm});
            skLineSegment(sketch, "E353.27", {"start": v(7230, 0) * mm, "end": v(7230, 3800) * mm});
            skLineSegment(sketch, "E353.28", {"start": v(4620, 3800) * mm, "end": v(2920, 3800) * mm});
            skLineSegment(sketch, "E353.29", {"start": v(4620, 1200) * mm, "end": v(2920, 1200) * mm});
            skLineSegment(sketch, "E353.30", {"start": v(4620, 3800) * mm, "end": v(4620, 1200) * mm});
            skLineSegment(sketch, "E353.31", {"start": v(2920, 3800) * mm, "end": v(2920, 1200) * mm});
            skSolve(sketch);
        }
        {
            var Q0;
            Q0 = qSketchRegion(id + "F38", true);
            extrude(context, id + "F39", {"entities" : qUnion([Q0]), "oppositeDirection" : true, "depth" : 100 * mm, "offsetDistance" : 25 * mm});
        }
        {
            var Q0;
            Q0=makeQuery(id+"F39.opExtrude","CAP_FACE",FACE,{"disambiguationData":[OSD([sQuery(id+"F38.wireOp",EDGE,"E353.4"),sQuery(id+"F38.wireOp",EDGE,"E353.5"),sQuery(id+"F38.wireOp",EDGE,"E353.6"),sQuery(id+"F38.wireOp",EDGE,"E353.7")])],"isStart":false});
            var sketch = newSketch(context, id + "F40", { "sketchPlane" : qUnion([Q0])});
            skLineSegment(sketch, "E354.0.0", {"start": v(-25660, 1100) * mm, "end": v(-24560, 1100) * mm});
            skLineSegment(sketch, "E354.0.1", {"start": v(-24560, 1100) * mm, "end": v(-24560, 3200) * mm});
            skLineSegment(sketch, "E354.0.2", {"start": v(-24560, 3200) * mm, "end": v(-25660, 3200) * mm});
            skLineSegment(sketch, "E354.0.3", {"start": v(-25660, 3200) * mm, "end": v(-25660, 1100) * mm});
            skLineSegment(sketch, "E355.bottom", {"start": v(-25610, 2400) * mm, "end": v(-24610, 2400) * mm});
            skLineSegment(sketch, "E355.top", {"start": v(-25610, 1150) * mm, "end": v(-24610, 1150) * mm});
            skLineSegment(sketch, "E355.left", {"start": v(-25610, 2400) * mm, "end": v(-25610, 1150) * mm});
            skLineSegment(sketch, "E355.right", {"start": v(-24610, 2400) * mm, "end": v(-24610, 1150) * mm});
            skLineSegment(sketch, "E356.bottom", {"start": v(-25610, 2450) * mm, "end": v(-24610, 2450) * mm});
            skLineSegment(sketch, "E356.top", {"start": v(-25610, 3150) * mm, "end": v(-24610, 3150) * mm});
            skLineSegment(sketch, "E356.left", {"start": v(-25610, 2450) * mm, "end": v(-25610, 3150) * mm});
            skLineSegment(sketch, "E356.right", {"start": v(-24610, 2450) * mm, "end": v(-24610, 3150) * mm});
            skLineSegment(sketch, "E357.0.0", {"start": v(-22100, 1100) * mm, "end": v(-21000, 1100) * mm});
            skLineSegment(sketch, "E357.0.1", {"start": v(-21000, 1100) * mm, "end": v(-21000, 3200) * mm});
            skLineSegment(sketch, "E357.0.2", {"start": v(-21000, 3200) * mm, "end": v(-22100, 3200) * mm});
            skLineSegment(sketch, "E357.0.3", {"start": v(-22100, 3200) * mm, "end": v(-22100, 1100) * mm});
            skLineSegment(sketch, "E358.bottom", {"start": v(-22050, 2400) * mm, "end": v(-21050, 2400) * mm});
            skLineSegment(sketch, "E358.top", {"start": v(-22050, 1150) * mm, "end": v(-21050, 1150) * mm});
            skLineSegment(sketch, "E358.left", {"start": v(-22050, 2400) * mm, "end": v(-22050, 1150) * mm});
            skLineSegment(sketch, "E358.right", {"start": v(-21050, 2400) * mm, "end": v(-21050, 1150) * mm});
            skLineSegment(sketch, "E359.bottom", {"start": v(-22050, 2450) * mm, "end": v(-21050, 2450) * mm});
            skLineSegment(sketch, "E359.top", {"start": v(-22050, 3150) * mm, "end": v(-21050, 3150) * mm});
            skLineSegment(sketch, "E359.left", {"start": v(-22050, 2450) * mm, "end": v(-22050, 3150) * mm});
            skLineSegment(sketch, "E359.right", {"start": v(-21050, 2450) * mm, "end": v(-21050, 3150) * mm});
            skPoint(sketch, "E360", {"position": v(-22100, 1100) * mm});
            skLineSegment(sketch, "E361.0.0", {"start": v(-28360, 0) * mm, "end": v(-27260, 0) * mm});
            skLineSegment(sketch, "E361.0.1", {"start": v(-27260, 0) * mm, "end": v(-27260, 2400) * mm});
            skLineSegment(sketch, "E361.0.2", {"start": v(-27260, 2400) * mm, "end": v(-28360, 2400) * mm});
            skLineSegment(sketch, "E361.0.3", {"start": v(-28360, 2400) * mm, "end": v(-28360, 0) * mm});
            skLineSegment(sketch, "E362.0", {"start": v(-28310, 50) * mm, "end": v(-27310, 50) * mm});
            skLineSegment(sketch, "E362.1", {"start": v(-28310, 2350) * mm, "end": v(-28310, 50) * mm});
            skLineSegment(sketch, "E362.2", {"start": v(-27310, 2350) * mm, "end": v(-28310, 2350) * mm});
            skLineSegment(sketch, "E362.3", {"start": v(-27310, 50) * mm, "end": v(-27310, 2350) * mm});
            skPoint(sketch, "E363", {"position": v(-18660, 1200) * mm});
            skPoint(sketch, "E364", {"position": v(-15860, 1200) * mm});
            skPoint(sketch, "E365", {"position": v(-13060, 1200) * mm});
            skLineSegment(sketch, "E366.2.0.2", {"start": v(-17010, 2900) * mm, "end": v(-17010, 3750) * mm});
            skLineSegment(sketch, "E366.2.0.8", {"start": v(-18660, 1200) * mm, "end": v(-16960, 1200) * mm});
            skLineSegment(sketch, "E366.2.0.10", {"start": v(-18610, 2900) * mm, "end": v(-17847.5, 2900) * mm});
            skLineSegment(sketch, "E366.2.0.11", {"start": v(-18610, 1250) * mm, "end": v(-17847.5, 1250) * mm});
            skLineSegment(sketch, "E366.2.0.14", {"start": v(-18610, 2850) * mm, "end": v(-18610, 1250) * mm});
            skLineSegment(sketch, "E366.2.0.18", {"start": v(-18610, 2850) * mm, "end": v(-17847.5, 2850) * mm});
            skLineSegment(sketch, "E366.2.0.23", {"start": v(-17010, 2850) * mm, "end": v(-17010, 1250) * mm});
            skLineSegment(sketch, "E366.2.0.25", {"start": v(-16960, 3800) * mm, "end": v(-18660, 3800) * mm});
            skLineSegment(sketch, "E366.2.0.31", {"start": v(-17010, 1250) * mm, "end": v(-17772.5, 1250) * mm});
            skLineSegment(sketch, "E366.2.0.34", {"start": v(-18610, 2900) * mm, "end": v(-18610, 3750) * mm});
            skLineSegment(sketch, "E366.2.0.36", {"start": v(-17810, 1200) * mm, "end": v(-17810, 3800) * mm, "construction": true});
            skLineSegment(sketch, "E366.2.0.37", {"start": v(-17010, 2850) * mm, "end": v(-17772.5, 2850) * mm});
            skLineSegment(sketch, "E366.2.0.40", {"start": v(-18660, 3800) * mm, "end": v(-18660, 1200) * mm});
            skLineSegment(sketch, "E366.2.0.41", {"start": v(-17010, 2900) * mm, "end": v(-17772.5, 2900) * mm});
            skLineSegment(sketch, "E366.2.0.46", {"start": v(-16960, 1200) * mm, "end": v(-16960, 3800) * mm});
            skLineSegment(sketch, "E366.2.0.49", {"start": v(-18610, 3750) * mm, "end": v(-17847.5, 3750) * mm});
            skLineSegment(sketch, "E366.2.0.50", {"start": v(-17010, 3750) * mm, "end": v(-17772.5, 3750) * mm});
            skLineSegment(sketch, "E366.2.0.55", {"start": v(-17772.5, 2850) * mm, "end": v(-17772.5, 1250) * mm});
            skLineSegment(sketch, "E366.2.0.59", {"start": v(-17772.5, 2900) * mm, "end": v(-17772.5, 3750) * mm});
            skLineSegment(sketch, "E366.2.0.63", {"start": v(-17847.5, 2900) * mm, "end": v(-17847.5, 3750) * mm});
            skLineSegment(sketch, "E366.2.0.65", {"start": v(-17847.5, 2850) * mm, "end": v(-17847.5, 1250) * mm});
            skLineSegment(sketch, "E367.2.0.2", {"start": v(-14210, 2850) * mm, "end": v(-14210, 3700) * mm});
            skLineSegment(sketch, "E367.2.0.8", {"start": v(-15860, 1150) * mm, "end": v(-14160, 1150) * mm});
            skLineSegment(sketch, "E367.2.0.10", {"start": v(-15810, 2850) * mm, "end": v(-15047.5, 2850) * mm});
            skLineSegment(sketch, "E367.2.0.11", {"start": v(-15810, 1200) * mm, "end": v(-15047.5, 1200) * mm});
            skLineSegment(sketch, "E367.2.0.14", {"start": v(-15810, 2800) * mm, "end": v(-15810, 1200) * mm});
            skLineSegment(sketch, "E367.2.0.18", {"start": v(-15810, 2800) * mm, "end": v(-15047.5, 2800) * mm});
            skLineSegment(sketch, "E367.2.0.23", {"start": v(-14210, 2800) * mm, "end": v(-14210, 1200) * mm});
            skLineSegment(sketch, "E367.2.0.25", {"start": v(-14160, 3750) * mm, "end": v(-15860, 3750) * mm});
            skLineSegment(sketch, "E367.2.0.31", {"start": v(-14210, 1200) * mm, "end": v(-14972.5, 1200) * mm});
            skPoint(sketch, "E367.2.0.33", {"position": v(-15860, 1150) * mm});
            skLineSegment(sketch, "E367.2.0.34", {"start": v(-15810, 2850) * mm, "end": v(-15810, 3700) * mm});
            skLineSegment(sketch, "E367.2.0.36", {"start": v(-15010, 1150) * mm, "end": v(-15010, 3750) * mm, "construction": true});
            skLineSegment(sketch, "E367.2.0.37", {"start": v(-14210, 2800) * mm, "end": v(-14972.5, 2800) * mm});
            skLineSegment(sketch, "E367.2.0.40", {"start": v(-15860, 3750) * mm, "end": v(-15860, 1150) * mm});
            skLineSegment(sketch, "E367.2.0.41", {"start": v(-14210, 2850) * mm, "end": v(-14972.5, 2850) * mm});
            skLineSegment(sketch, "E367.2.0.46", {"start": v(-14160, 1150) * mm, "end": v(-14160, 3750) * mm});
            skLineSegment(sketch, "E367.2.0.49", {"start": v(-15810, 3700) * mm, "end": v(-15047.5, 3700) * mm});
            skLineSegment(sketch, "E367.2.0.50", {"start": v(-14210, 3700) * mm, "end": v(-14972.5, 3700) * mm});
            skLineSegment(sketch, "E367.2.0.55", {"start": v(-14972.5, 2800) * mm, "end": v(-14972.5, 1200) * mm});
            skLineSegment(sketch, "E367.2.0.59", {"start": v(-14972.5, 2850) * mm, "end": v(-14972.5, 3700) * mm});
            skLineSegment(sketch, "E367.2.0.63", {"start": v(-15047.5, 2850) * mm, "end": v(-15047.5, 3700) * mm});
            skLineSegment(sketch, "E367.2.0.65", {"start": v(-15047.5, 2800) * mm, "end": v(-15047.5, 1200) * mm});
            skLineSegment(sketch, "E368.2.0.2", {"start": v(-11410, 2900) * mm, "end": v(-11410, 3750) * mm});
            skLineSegment(sketch, "E368.2.0.8", {"start": v(-13060, 1200) * mm, "end": v(-11360, 1200) * mm});
            skLineSegment(sketch, "E368.2.0.10", {"start": v(-13010, 2900) * mm, "end": v(-12247.5, 2900) * mm});
            skLineSegment(sketch, "E368.2.0.11", {"start": v(-13010, 1250) * mm, "end": v(-12247.5, 1250) * mm});
            skLineSegment(sketch, "E368.2.0.14", {"start": v(-13010, 2850) * mm, "end": v(-13010, 1250) * mm});
            skLineSegment(sketch, "E368.2.0.18", {"start": v(-13010, 2850) * mm, "end": v(-12247.5, 2850) * mm});
            skLineSegment(sketch, "E368.2.0.23", {"start": v(-11410, 2850) * mm, "end": v(-11410, 1250) * mm});
            skLineSegment(sketch, "E368.2.0.25", {"start": v(-11360, 3800) * mm, "end": v(-13060, 3800) * mm});
            skLineSegment(sketch, "E368.2.0.31", {"start": v(-11410, 1250) * mm, "end": v(-12172.5, 1250) * mm});
            skLineSegment(sketch, "E368.2.0.34", {"start": v(-13010, 2900) * mm, "end": v(-13010, 3750) * mm});
            skLineSegment(sketch, "E368.2.0.36", {"start": v(-12210, 1200) * mm, "end": v(-12210, 3800) * mm, "construction": true});
            skLineSegment(sketch, "E368.2.0.37", {"start": v(-11410, 2850) * mm, "end": v(-12172.5, 2850) * mm});
            skLineSegment(sketch, "E368.2.0.40", {"start": v(-13060, 3800) * mm, "end": v(-13060, 1200) * mm});
            skLineSegment(sketch, "E368.2.0.41", {"start": v(-11410, 2900) * mm, "end": v(-12172.5, 2900) * mm});
            skLineSegment(sketch, "E368.2.0.46", {"start": v(-11360, 1200) * mm, "end": v(-11360, 3800) * mm});
            skLineSegment(sketch, "E368.2.0.49", {"start": v(-13010, 3750) * mm, "end": v(-12247.5, 3750) * mm});
            skLineSegment(sketch, "E368.2.0.50", {"start": v(-11410, 3750) * mm, "end": v(-12172.5, 3750) * mm});
            skLineSegment(sketch, "E368.2.0.55", {"start": v(-12172.5, 2850) * mm, "end": v(-12172.5, 1250) * mm});
            skLineSegment(sketch, "E368.2.0.59", {"start": v(-12172.5, 2900) * mm, "end": v(-12172.5, 3750) * mm});
            skLineSegment(sketch, "E368.2.0.63", {"start": v(-12247.5, 2900) * mm, "end": v(-12247.5, 3750) * mm});
            skLineSegment(sketch, "E368.2.0.65", {"start": v(-12247.5, 2850) * mm, "end": v(-12247.5, 1250) * mm});
            skPoint(sketch, "E369", {"position": v(-4620, 1200) * mm});
            skLineSegment(sketch, "E370.2.0.2", {"start": v(-2970, 2900) * mm, "end": v(-2970, 3750) * mm});
            skLineSegment(sketch, "E370.2.0.8", {"start": v(-4620, 1200) * mm, "end": v(-2920, 1200) * mm});
            skLineSegment(sketch, "E370.2.0.10", {"start": v(-4570, 2900) * mm, "end": v(-3807.5, 2900) * mm});
            skLineSegment(sketch, "E370.2.0.11", {"start": v(-4570, 1250) * mm, "end": v(-3807.5, 1250) * mm});
            skLineSegment(sketch, "E370.2.0.14", {"start": v(-4570, 2850) * mm, "end": v(-4570, 1250) * mm});
            skLineSegment(sketch, "E370.2.0.18", {"start": v(-4570, 2850) * mm, "end": v(-3807.5, 2850) * mm});
            skLineSegment(sketch, "E370.2.0.23", {"start": v(-2970, 2850) * mm, "end": v(-2970, 1250) * mm});
            skLineSegment(sketch, "E370.2.0.25", {"start": v(-2920, 3800) * mm, "end": v(-4620, 3800) * mm});
            skLineSegment(sketch, "E370.2.0.31", {"start": v(-2970, 1250) * mm, "end": v(-3732.5, 1250) * mm});
            skLineSegment(sketch, "E370.2.0.34", {"start": v(-4570, 2900) * mm, "end": v(-4570, 3750) * mm});
            skLineSegment(sketch, "E370.2.0.36", {"start": v(-3770, 1200) * mm, "end": v(-3770, 3800) * mm, "construction": true});
            skLineSegment(sketch, "E370.2.0.37", {"start": v(-2970, 2850) * mm, "end": v(-3732.5, 2850) * mm});
            skLineSegment(sketch, "E370.2.0.40", {"start": v(-4620, 3800) * mm, "end": v(-4620, 1200) * mm});
            skLineSegment(sketch, "E370.2.0.41", {"start": v(-2970, 2900) * mm, "end": v(-3732.5, 2900) * mm});
            skLineSegment(sketch, "E370.2.0.46", {"start": v(-2920, 1200) * mm, "end": v(-2920, 3800) * mm});
            skLineSegment(sketch, "E370.2.0.49", {"start": v(-4570, 3750) * mm, "end": v(-3807.5, 3750) * mm});
            skLineSegment(sketch, "E370.2.0.50", {"start": v(-2970, 3750) * mm, "end": v(-3732.5, 3750) * mm});
            skLineSegment(sketch, "E370.2.0.55", {"start": v(-3732.5, 2850) * mm, "end": v(-3732.5, 1250) * mm});
            skLineSegment(sketch, "E370.2.0.59", {"start": v(-3732.5, 2900) * mm, "end": v(-3732.5, 3750) * mm});
            skLineSegment(sketch, "E370.2.0.63", {"start": v(-3807.5, 2900) * mm, "end": v(-3807.5, 3750) * mm});
            skLineSegment(sketch, "E370.2.0.65", {"start": v(-3807.5, 2850) * mm, "end": v(-3807.5, 1250) * mm});
            skLineSegment(sketch, "E371", {"start": v(-8130, 0) * mm, "end": v(-8130, 3800) * mm, "construction": true});
            skLineSegment(sketch, "E372.bottom", {"start": v(-8980, 2250) * mm, "end": v(-8167.5, 2250) * mm});
            skLineSegment(sketch, "E372.top", {"start": v(-8980, 50) * mm, "end": v(-8167.5, 50) * mm});
            skLineSegment(sketch, "E372.left", {"start": v(-8980, 2250) * mm, "end": v(-8980, 50) * mm});
            skLineSegment(sketch, "E372.right", {"start": v(-8167.5, 2250) * mm, "end": v(-8167.5, 50) * mm});
            skLineSegment(sketch, "E373.0.0", {"start": v(-9030, 0) * mm, "end": v(-7230, 0) * mm});
            skLineSegment(sketch, "E373.0.1", {"start": v(-7230, 0) * mm, "end": v(-7230, 3800) * mm});
            skLineSegment(sketch, "E373.0.2", {"start": v(-7230, 3800) * mm, "end": v(-9030, 3800) * mm});
            skLineSegment(sketch, "E373.0.3", {"start": v(-9030, 3800) * mm, "end": v(-9030, 0) * mm});
            skLineSegment(sketch, "E374.bottom", {"start": v(-8980, 2350) * mm, "end": v(-8092.5, 2350) * mm});
            skLineSegment(sketch, "E374.top", {"start": v(-8167.5, 3750) * mm, "end": v(-8092.5, 3750) * mm});
            skLineSegment(sketch, "E374.left", {"start": v(-8980, 2350) * mm, "end": v(-8980, 3750) * mm});
            skLineSegment(sketch, "E375.MirrorCS", {"start": v(-7280, 3750) * mm, "end": v(-8092.5, 3750) * mm});
            skLineSegment(sketch, "E376.MirrorCS", {"start": v(-7280, 2350) * mm, "end": v(-7280, 3750) * mm});
            skLineSegment(sketch, "E377.MirrorCS", {"start": v(-7280, 2350) * mm, "end": v(-8092.5, 2350) * mm});
            skLineSegment(sketch, "E378.MirrorCS", {"start": v(-7280, 2250) * mm, "end": v(-8092.5, 2250) * mm});
            skLineSegment(sketch, "E379.MirrorCS", {"start": v(-8092.5, 2250) * mm, "end": v(-8092.5, 50) * mm});
            skLineSegment(sketch, "E380.MirrorCS", {"start": v(-7280, 2250) * mm, "end": v(-7280, 50) * mm});
            skLineSegment(sketch, "E381.MirrorCS", {"start": v(-7280, 50) * mm, "end": v(-8092.5, 50) * mm});
            skPoint(sketch, "E382.orphan", {"position": v(-8167.5, 2350) * mm});
            skLineSegment(sketch, "E383", {"start": v(-8980, 3750) * mm, "end": v(-8167.5, 3750) * mm});
            skSolve(sketch);
        }
        {
            var Q0;
            Q0 = qSketchRegion(id + "F40", true);
            extrude(context, id + "F41", {"entities" : qUnion([Q0]), "depth" : 50 * mm, "offsetDistance" : 25 * mm});
        }
        {
            var Q0;
            Q0=makeQuery(id+"F5.boolean.opBoolean","MERGE",FACE,{"derivedFrom":[makeQuery(id+"F3.boolean.opBoolean","COPY",FACE,{"derivedFrom":makeQuery(id+"F3.opExtrude","SWEPT_FACE",FACE,{"disambiguationData":[OSD([sQuery(id+"F2.wireOp",EDGE,"E19.1")])]})}),makeQuery(id+"F5.opExtrude","SWEPT_FACE",FACE,{"disambiguationData":[OSD([sQuery(id+"F4.wireOp",EDGE,"E21")])]})]});
            var sketch = newSketch(context, id + "F42", { "sketchPlane" : qUnion([Q0])});
            skLineSegment(sketch, "E384.bottom", {"start": v(16930, -150) * mm, "end": v(18530, -150) * mm});
            skLineSegment(sketch, "E384.top", {"start": v(16930, 2440) * mm, "end": v(18530, 2440) * mm});
            skLineSegment(sketch, "E384.left", {"start": v(16930, -150) * mm, "end": v(16930, 2440) * mm});
            skLineSegment(sketch, "E384.right", {"start": v(18530, -150) * mm, "end": v(18530, 2440) * mm});
            skSolve(sketch);
        }
        {
            var Q0;
            Q0 = qSketchRegion(id + "F42", true);
            extrude(context, id + "F43", {"entities" : qUnion([Q0]), "operationType" : NewBodyOperationType.REMOVE, "oppositeDirection" : true, "depth" : 600 * mm, "offsetDistance" : 25 * mm});
        }
        {
            var Q0;
            {var subQ26=sQuery(id+"F0.wireOp",EDGE,"E16.5");Q0=makeQuery(id+"F2hi8GqezRywkeN_40.boolean.opBoolean","SPLIT",FACE,{"disambiguationData":[TD([makeQuery(id+"F2x6o0qxNZTSrfC_40.boolean.opBoolean","COPY",FACE,{"derivedFrom":makeQuery(id+"F2x6o0qxNZTSrfC_40.opExtrude","SWEPT_FACE",FACE,{"disambiguationData":[OSD([sQuery(id+"F7vcSyRpF9JMD3K_40.wireOp",EDGE,"hXnOyaqm-xlU2-VTCc-7dql-qga7E96rzK4p.right")])]})})])],"derivedFrom":makeQuery(id+"F1.opExtrude","SWEPT_FACE",FACE,{"disambiguationData":[OSD([subQ26])]})});}
            var sketch = newSketch(context, id + "F44", { "sketchPlane" : qUnion([Q0])});
            skLineSegment(sketch, "E385.0", {"start": v(-16930, -150) * mm, "end": v(-16930, 2440) * mm});
            skLineSegment(sketch, "E386.0", {"start": v(-16930, 2440) * mm, "end": v(-18530, 2440) * mm});
            skLineSegment(sketch, "E387.0", {"start": v(-18530, -150) * mm, "end": v(-18530, 2440) * mm});
            skLineSegment(sketch, "E388.0", {"start": v(-16930, -150) * mm, "end": v(-18530, -150) * mm});
            skSolve(sketch);
        }
        {
            var Q0;
            Q0=qSketchRegion(id+"F44",true);
            extrude(context, id + "F45", {"entities" : qUnion([Q0]), "oppositeDirection" : true, "depth" : 100 * mm, "offsetDistance" : 25 * mm});
        }
        {
            var Q0;
            Q0=makeQuery(id+"F45.opExtrude","CAP_FACE",FACE,{"disambiguationData":[OSD([sQuery(id+"F44.wireOp",EDGE,"E385.0"),sQuery(id+"F44.wireOp",EDGE,"E386.0"),sQuery(id+"F44.wireOp",EDGE,"E387.0"),sQuery(id+"F44.wireOp",EDGE,"E388.0")])],"isStart":false});
            var sketch = newSketch(context, id + "F46", { "sketchPlane" : qUnion([Q0])});
            skLineSegment(sketch, "E389", {"start": v(17730, 2440) * mm, "end": v(17730, -150) * mm, "construction": true});
            skLineSegment(sketch, "E390.0.0", {"start": v(18530, 2440) * mm, "end": v(18530, -150) * mm});
            skLineSegment(sketch, "E390.0.6", {"start": v(16930, -150) * mm, "end": v(16930, 2440) * mm});
            skLineSegment(sketch, "E390.0.7", {"start": v(16930, 2440) * mm, "end": v(18530, 2440) * mm});
            skLineSegment(sketch, "E391", {"start": v(16980, -150) * mm, "end": v(16980, 1050) * mm});
            skLineSegment(sketch, "E392", {"start": v(16980, 1050) * mm, "end": v(17680, 1050) * mm});
            skLineSegment(sketch, "E393", {"start": v(17680, 1050) * mm, "end": v(17680, -150) * mm});
            skLineSegment(sketch, "E394", {"start": v(17680, -150) * mm, "end": v(17730, -150) * mm});
            skLineSegment(sketch, "E395", {"start": v(16980, -150) * mm, "end": v(16930, -150) * mm});
            skLineSegment(sketch, "E396", {"start": v(17730, 2390) * mm, "end": v(16980, 2390) * mm});
            skLineSegment(sketch, "E397", {"start": v(16980, 2390) * mm, "end": v(16980, 1100) * mm});
            skLineSegment(sketch, "E398", {"start": v(16980, 1100) * mm, "end": v(17730, 1100) * mm});
            skLineSegment(sketch, "E399.MirrorCS", {"start": v(17730, 2390) * mm, "end": v(18480, 2390) * mm});
            skLineSegment(sketch, "E400.MirrorCS", {"start": v(18480, 2390) * mm, "end": v(18480, 1100) * mm});
            skLineSegment(sketch, "E401.MirrorCS", {"start": v(18480, 1100) * mm, "end": v(17730, 1100) * mm});
            skLineSegment(sketch, "E402.MirrorCS", {"start": v(18480, 1050) * mm, "end": v(17780, 1050) * mm});
            skLineSegment(sketch, "E403.MirrorCS", {"start": v(17780, 1050) * mm, "end": v(17780, -150) * mm});
            skLineSegment(sketch, "E404.MirrorCS", {"start": v(18480, -150) * mm, "end": v(18480, 1050) * mm});
            skLineSegment(sketch, "E405.MirrorCS", {"start": v(18480, -150) * mm, "end": v(18530, -150) * mm});
            skLineSegment(sketch, "E406.MirrorCS", {"start": v(17780, -150) * mm, "end": v(17730, -150) * mm});
            skSolve(sketch);
        }
        {
            var Q0;
            Q0=qSketchRegion(id+"F46",true);
            extrude(context, id + "F47", {"entities" : qUnion([Q0]), "depth" : 50 * mm, "offsetDistance" : 25 * mm});
        }
        {
            var Q0;
            Q0=makeQuery(id+"F5.boolean.opBoolean","MERGE",FACE,{"derivedFrom":[makeQuery(id+"F3.boolean.opBoolean","COPY",FACE,{"derivedFrom":makeQuery(id+"F3.opExtrude","SWEPT_FACE",FACE,{"disambiguationData":[OSD([sQuery(id+"F2.wireOp",EDGE,"E19.1")])]})}),makeQuery(id+"F5.opExtrude","SWEPT_FACE",FACE,{"disambiguationData":[OSD([sQuery(id+"F4.wireOp",EDGE,"E21")])]})]});
            var sketch = newSketch(context, id + "F48", { "sketchPlane" : qUnion([Q0])});
            skLineSegment(sketch, "E407.bottom", {"start": v(15650, 4000) * mm, "end": v(16050, 4000) * mm});
            skLineSegment(sketch, "E407.top", {"start": v(15650, -150) * mm, "end": v(16050, -150) * mm});
            skLineSegment(sketch, "E407.left", {"start": v(15650, 4000) * mm, "end": v(15650, -150) * mm});
            skLineSegment(sketch, "E407.right", {"start": v(16050, 4000) * mm, "end": v(16050, -150) * mm});
            skLineSegment(sketch, "E408.bottom", {"start": v(6680, 4000) * mm, "end": v(7080, 4000) * mm});
            skLineSegment(sketch, "E408.top", {"start": v(6680, -150) * mm, "end": v(7080, -150) * mm});
            skLineSegment(sketch, "E408.left", {"start": v(6680, 4000) * mm, "end": v(6680, -150) * mm});
            skLineSegment(sketch, "E408.right", {"start": v(7080, 4000) * mm, "end": v(7080, -150) * mm});
            skLineSegment(sketch, "E409.bottom", {"start": v(-80, 4000) * mm, "end": v(320, 4000) * mm});
            skLineSegment(sketch, "E409.top", {"start": v(-80, -150) * mm, "end": v(320, -150) * mm});
            skLineSegment(sketch, "E409.left", {"start": v(-80, 4000) * mm, "end": v(-80, -150) * mm});
            skLineSegment(sketch, "E409.right", {"start": v(320, 4000) * mm, "end": v(320, -150) * mm});
            skLineSegment(sketch, "E410.bottom", {"start": v(19810, 4000) * mm, "end": v(19410, 4000) * mm});
            skLineSegment(sketch, "E410.top", {"start": v(19810, -150) * mm, "end": v(19410, -150) * mm});
            skLineSegment(sketch, "E410.left", {"start": v(19810, 4000) * mm, "end": v(19810, -150) * mm});
            skLineSegment(sketch, "E410.right", {"start": v(19410, 4000) * mm, "end": v(19410, -150) * mm});
            skLineSegment(sketch, "E411.bottom", {"start": v(28650, 4000) * mm, "end": v(29050, 4000) * mm});
            skLineSegment(sketch, "E411.top", {"start": v(28650, -150) * mm, "end": v(29050, -150) * mm});
            skLineSegment(sketch, "E411.left", {"start": v(28650, 4000) * mm, "end": v(28650, -150) * mm});
            skLineSegment(sketch, "E411.right", {"start": v(29050, 4000) * mm, "end": v(29050, -150) * mm});
            skLineSegment(sketch, "E412.bottom", {"start": v(35160, 4000) * mm, "end": v(35560, 4000) * mm});
            skLineSegment(sketch, "E412.top", {"start": v(35160, -150) * mm, "end": v(35560, -150) * mm});
            skLineSegment(sketch, "E412.left", {"start": v(35160, 4000) * mm, "end": v(35160, -150) * mm});
            skLineSegment(sketch, "E412.right", {"start": v(35560, 4000) * mm, "end": v(35560, -150) * mm});
            skSolve(sketch);
        }
        {
            var Q0;
            Q0 = qSketchRegion(id + "F48", true);
            extrude(context, id + "F49", {"entities" : qUnion([Q0]), "depth" : 50 * mm, "offsetDistance" : 25 * mm});
        }
        {
            var Q0;
            Q0=makeQuery(id+"F5.boolean.opBoolean","MERGE",FACE,{"derivedFrom":[makeQuery(id+"F3.boolean.opBoolean","COPY",FACE,{"derivedFrom":makeQuery(id+"F3.opExtrude","SWEPT_FACE",FACE,{"disambiguationData":[OSD([sQuery(id+"F2.wireOp",EDGE,"E19.3")])]})}),makeQuery(id+"F5.opExtrude","SWEPT_FACE",FACE,{"disambiguationData":[OSD([sQuery(id+"F4.wireOp",EDGE,"E27.0")])]})]});
            var sketch = newSketch(context, id + "F50", { "sketchPlane" : qUnion([Q0])});
            skLineSegment(sketch, "E413.0", {"start": v(9130, 3800) * mm, "end": v(7430, 3800) * mm});
            skLineSegment(sketch, "E414.0", {"start": v(9130, 3800) * mm, "end": v(9130, 1200) * mm});
            skLineSegment(sketch, "E415.0", {"start": v(7430, 3800) * mm, "end": v(7430, 1200) * mm});
            skLineSegment(sketch, "E416.0", {"start": v(9130, 1200) * mm, "end": v(7430, 1200) * mm});
            skLineSegment(sketch, "E417.bottom", {"start": v(7280, 3950) * mm, "end": v(9280, 3950) * mm});
            skLineSegment(sketch, "E417.top", {"start": v(7280, 1150) * mm, "end": v(9280, 1150) * mm});
            skLineSegment(sketch, "E417.left", {"start": v(7280, 3950) * mm, "end": v(7280, 1150) * mm});
            skLineSegment(sketch, "E417.right", {"start": v(9280, 3950) * mm, "end": v(9280, 1150) * mm});
            skLineSegment(sketch, "E418.0", {"start": v(12130, 3800) * mm, "end": v(10430, 3800) * mm});
            skLineSegment(sketch, "E419.0", {"start": v(12130, 3800) * mm, "end": v(12130, 1200) * mm});
            skLineSegment(sketch, "E420.0", {"start": v(10430, 3800) * mm, "end": v(10430, 1200) * mm});
            skLineSegment(sketch, "E421.0", {"start": v(12130, 1200) * mm, "end": v(10430, 1200) * mm});
            skLineSegment(sketch, "E422.bottom", {"start": v(10280, 3950) * mm, "end": v(12280, 3950) * mm});
            skLineSegment(sketch, "E422.top", {"start": v(10280, 1150) * mm, "end": v(12280, 1150) * mm});
            skLineSegment(sketch, "E422.left", {"start": v(10280, 3950) * mm, "end": v(10280, 1150) * mm});
            skLineSegment(sketch, "E422.right", {"start": v(12280, 3950) * mm, "end": v(12280, 1150) * mm});
            skLineSegment(sketch, "E423.0", {"start": v(15130, 3800) * mm, "end": v(13430, 3800) * mm});
            skLineSegment(sketch, "E424.0", {"start": v(15130, 3800) * mm, "end": v(15130, 1200) * mm});
            skLineSegment(sketch, "E425.0", {"start": v(13430, 3800) * mm, "end": v(13430, 1200) * mm});
            skLineSegment(sketch, "E426.0", {"start": v(15130, 1200) * mm, "end": v(13430, 1200) * mm});
            skLineSegment(sketch, "E427.bottom", {"start": v(13280, 3950) * mm, "end": v(15280, 3950) * mm});
            skLineSegment(sketch, "E427.top", {"start": v(13280, 1150) * mm, "end": v(15280, 1150) * mm});
            skLineSegment(sketch, "E427.left", {"start": v(13280, 3950) * mm, "end": v(13280, 1150) * mm});
            skLineSegment(sketch, "E427.right", {"start": v(15280, 3950) * mm, "end": v(15280, 1150) * mm});
            skLineSegment(sketch, "E428", {"start": v(17730, 4000) * mm, "end": v(17730, 2909.1) * mm, "construction": true});
            skLineSegment(sketch, "E429.MirrorCS", {"start": v(25180, 1150) * mm, "end": v(23180, 1150) * mm});
            skLineSegment(sketch, "E430.MirrorCS", {"start": v(26330, 1200) * mm, "end": v(28030, 1200) * mm});
            skLineSegment(sketch, "E431.MirrorCS", {"start": v(20330, 1200) * mm, "end": v(22030, 1200) * mm});
            skLineSegment(sketch, "E432.MirrorCS", {"start": v(28180, 1150) * mm, "end": v(26180, 1150) * mm});
            skLineSegment(sketch, "E433.MirrorCS", {"start": v(28180, 3950) * mm, "end": v(26180, 3950) * mm});
            skLineSegment(sketch, "E434.MirrorCS", {"start": v(23330, 3800) * mm, "end": v(25030, 3800) * mm});
            skLineSegment(sketch, "E435.MirrorCS", {"start": v(26180, 3950) * mm, "end": v(26180, 1150) * mm});
            skLineSegment(sketch, "E436.MirrorCS", {"start": v(22030, 3800) * mm, "end": v(22030, 1200) * mm});
            skLineSegment(sketch, "E437.MirrorCS", {"start": v(25030, 3800) * mm, "end": v(25030, 1200) * mm});
            skLineSegment(sketch, "E438.MirrorCS", {"start": v(22180, 3950) * mm, "end": v(20180, 3950) * mm});
            skLineSegment(sketch, "E439.MirrorCS", {"start": v(23180, 3950) * mm, "end": v(23180, 1150) * mm});
            skLineSegment(sketch, "E440.MirrorCS", {"start": v(25180, 3950) * mm, "end": v(25180, 1150) * mm});
            skLineSegment(sketch, "E441.MirrorCS", {"start": v(20180, 3950) * mm, "end": v(20180, 1150) * mm});
            skLineSegment(sketch, "E442.MirrorCS", {"start": v(26330, 3800) * mm, "end": v(26330, 1200) * mm});
            skLineSegment(sketch, "E443.MirrorCS", {"start": v(26330, 3800) * mm, "end": v(28030, 3800) * mm});
            skLineSegment(sketch, "E444.MirrorCS", {"start": v(22180, 1150) * mm, "end": v(20180, 1150) * mm});
            skLineSegment(sketch, "E445.MirrorCS", {"start": v(28030, 3800) * mm, "end": v(28030, 1200) * mm});
            skLineSegment(sketch, "E446.MirrorCS", {"start": v(25180, 3950) * mm, "end": v(23180, 3950) * mm});
            skLineSegment(sketch, "E447.MirrorCS", {"start": v(20330, 3800) * mm, "end": v(20330, 1200) * mm});
            skLineSegment(sketch, "E448.MirrorCS", {"start": v(23330, 1200) * mm, "end": v(25030, 1200) * mm});
            skLineSegment(sketch, "E449.MirrorCS", {"start": v(22180, 3950) * mm, "end": v(22180, 1150) * mm});
            skLineSegment(sketch, "E450.MirrorCS", {"start": v(20330, 3800) * mm, "end": v(22030, 3800) * mm});
            skLineSegment(sketch, "E451.MirrorCS", {"start": v(23330, 3800) * mm, "end": v(23330, 1200) * mm});
            skLineSegment(sketch, "E452.MirrorCS", {"start": v(28180, 3950) * mm, "end": v(28180, 1150) * mm});
            skSolve(sketch);
        }
        {
            var Q0;
            Q0 = qSketchRegion(id + "F50", true);
            extrude(context, id + "F51", {"entities" : qUnion([Q0]), "depth" : 50 * mm, "offsetDistance" : 25 * mm});
        }
        {
            var Q0;
            Q0=makeQuery(id+"F51.opExtrude","CAP_FACE",FACE,{"disambiguationData":[OSD([sQuery(id+"F50.wireOp",EDGE,"E413.0"),sQuery(id+"F50.wireOp",EDGE,"E414.0"),sQuery(id+"F50.wireOp",EDGE,"E415.0"),sQuery(id+"F50.wireOp",EDGE,"E416.0"),sQuery(id+"F50.wireOp",EDGE,"E417.bottom"),sQuery(id+"F50.wireOp",EDGE,"E417.top"),sQuery(id+"F50.wireOp",EDGE,"E417.left"),sQuery(id+"F50.wireOp",EDGE,"E417.right")])],"isStart":false});
            var sketch = newSketch(context, id + "F52", { "sketchPlane" : qUnion([Q0])});
            skLineSegment(sketch, "E453.0.0", {"start": v(7280, 3950) * mm, "end": v(7280, 1150) * mm});
            skLineSegment(sketch, "E453.0.2", {"start": v(9280, 1150) * mm, "end": v(9280, 3950) * mm});
            skLineSegment(sketch, "E453.0.3", {"start": v(9280, 3950) * mm, "end": v(7280, 3950) * mm});
            skLineSegment(sketch, "E454.0", {"start": v(7380, 3850) * mm, "end": v(7380, 1150) * mm});
            skLineSegment(sketch, "E454.1", {"start": v(9180, 3850) * mm, "end": v(7380, 3850) * mm});
            skLineSegment(sketch, "E454.2", {"start": v(9180, 1150) * mm, "end": v(9180, 3850) * mm});
            skLineSegment(sketch, "E455", {"start": v(7280, 1150) * mm, "end": v(7380, 1150) * mm});
            skLineSegment(sketch, "E456", {"start": v(9180, 1150) * mm, "end": v(9280, 1150) * mm});
            skLineSegment(sketch, "E457.0.0", {"start": v(10280, 3950) * mm, "end": v(10280, 1150) * mm});
            skLineSegment(sketch, "E457.0.2", {"start": v(12280, 1150) * mm, "end": v(12280, 3950) * mm});
            skLineSegment(sketch, "E457.0.3", {"start": v(12280, 3950) * mm, "end": v(10280, 3950) * mm});
            skLineSegment(sketch, "E458.0", {"start": v(10380, 3850) * mm, "end": v(10380, 1150) * mm});
            skLineSegment(sketch, "E458.1", {"start": v(12180, 3850) * mm, "end": v(10380, 3850) * mm});
            skLineSegment(sketch, "E458.2", {"start": v(12180, 1150) * mm, "end": v(12180, 3850) * mm});
            skLineSegment(sketch, "E459", {"start": v(10280, 1150) * mm, "end": v(10380, 1150) * mm});
            skLineSegment(sketch, "E460", {"start": v(12180, 1150) * mm, "end": v(12280, 1150) * mm});
            skPoint(sketch, "E461", {"position": v(10280, 1150) * mm});
            skPoint(sketch, "E462", {"position": v(13280, 1100) * mm});
            skLineSegment(sketch, "E463.0.0", {"start": v(13280, 3950) * mm, "end": v(13280, 1150) * mm});
            skLineSegment(sketch, "E463.0.2", {"start": v(15280, 1150) * mm, "end": v(15280, 3950) * mm});
            skLineSegment(sketch, "E463.0.3", {"start": v(15280, 3950) * mm, "end": v(13280, 3950) * mm});
            skLineSegment(sketch, "E464.0", {"start": v(13380, 3850) * mm, "end": v(13380, 1150) * mm});
            skLineSegment(sketch, "E464.1", {"start": v(15180, 3850) * mm, "end": v(13380, 3850) * mm});
            skLineSegment(sketch, "E464.2", {"start": v(15180, 1150) * mm, "end": v(15180, 3850) * mm});
            skLineSegment(sketch, "E465", {"start": v(13280, 1150) * mm, "end": v(13380, 1150) * mm});
            skLineSegment(sketch, "E466", {"start": v(15180, 1150) * mm, "end": v(15280, 1150) * mm});
            skLineSegment(sketch, "E467", {"start": v(17730, 4000) * mm, "end": v(17730, 2765.07) * mm, "construction": true});
            skLineSegment(sketch, "E468.MirrorCS", {"start": v(25180, 1150) * mm, "end": v(25080, 1150) * mm});
            skLineSegment(sketch, "E469.MirrorCS", {"start": v(22180, 1150) * mm, "end": v(22080, 1150) * mm});
            skLineSegment(sketch, "E470.MirrorCS", {"start": v(20280, 1150) * mm, "end": v(20180, 1150) * mm});
            skLineSegment(sketch, "E471.MirrorCS", {"start": v(28180, 1150) * mm, "end": v(28080, 1150) * mm});
            skLineSegment(sketch, "E472.MirrorCS", {"start": v(26280, 1150) * mm, "end": v(26180, 1150) * mm});
            skLineSegment(sketch, "E473.MirrorCS", {"start": v(23280, 1150) * mm, "end": v(23180, 1150) * mm});
            skLineSegment(sketch, "E474.MirrorCS", {"start": v(25080, 3850) * mm, "end": v(25080, 1150) * mm});
            skLineSegment(sketch, "E475.MirrorCS", {"start": v(23180, 3950) * mm, "end": v(25180, 3950) * mm});
            skLineSegment(sketch, "E476.MirrorCS", {"start": v(23280, 3850) * mm, "end": v(25080, 3850) * mm});
            skPoint(sketch, "E477.MirrorP", {"position": v(22180, 1100) * mm});
            skLineSegment(sketch, "E478.MirrorCS", {"start": v(20280, 1150) * mm, "end": v(20280, 3850) * mm});
            skLineSegment(sketch, "E479.MirrorCS", {"start": v(20280, 3850) * mm, "end": v(22080, 3850) * mm});
            skLineSegment(sketch, "E480.MirrorCS", {"start": v(20180, 3950) * mm, "end": v(22180, 3950) * mm});
            skLineSegment(sketch, "E481.MirrorCS", {"start": v(22180, 3950) * mm, "end": v(22180, 1150) * mm});
            skLineSegment(sketch, "E482.MirrorCS", {"start": v(26280, 1150) * mm, "end": v(26280, 3850) * mm});
            skLineSegment(sketch, "E483.MirrorCS", {"start": v(26280, 3850) * mm, "end": v(28080, 3850) * mm});
            skLineSegment(sketch, "E484.MirrorCS", {"start": v(20180, 1150) * mm, "end": v(20180, 3950) * mm});
            skLineSegment(sketch, "E485.MirrorCS", {"start": v(23180, 1150) * mm, "end": v(23180, 3950) * mm});
            skLineSegment(sketch, "E486.MirrorCS", {"start": v(25180, 3950) * mm, "end": v(25180, 1150) * mm});
            skLineSegment(sketch, "E487.MirrorCS", {"start": v(22080, 3850) * mm, "end": v(22080, 1150) * mm});
            skLineSegment(sketch, "E488.MirrorCS", {"start": v(23280, 1150) * mm, "end": v(23280, 3850) * mm});
            skLineSegment(sketch, "E489.MirrorCS", {"start": v(28180, 3950) * mm, "end": v(28180, 1150) * mm});
            skLineSegment(sketch, "E490.MirrorCS", {"start": v(26180, 1150) * mm, "end": v(26180, 3950) * mm});
            skLineSegment(sketch, "E491.MirrorCS", {"start": v(28080, 3850) * mm, "end": v(28080, 1150) * mm});
            skLineSegment(sketch, "E492.MirrorCS", {"start": v(26180, 3950) * mm, "end": v(28180, 3950) * mm});
            skPoint(sketch, "E493.MirrorP", {"position": v(25180, 1150) * mm});
            skSolve(sketch);
        }
        {
            var Q0;
            Q0 = qSketchRegion(id + "F52", true);
            extrude(context, id + "F53", {"entities" : qUnion([Q0]), "operationType" : NewBodyOperationType.ADD, "depth" : 50 * mm, "offsetDistance" : 25 * mm});
        }
        {
            var Q0;
            Q0=makeQuery(id+"F5.boolean.opBoolean","MERGE",FACE,{"derivedFrom":[makeQuery(id+"F3.boolean.opBoolean","COPY",FACE,{"derivedFrom":makeQuery(id+"F3.opExtrude","SWEPT_FACE",FACE,{"disambiguationData":[OSD([sQuery(id+"F2.wireOp",EDGE,"E19.6")])]})}),makeQuery(id+"F5.opExtrude","SWEPT_FACE",FACE,{"disambiguationData":[OSD([sQuery(id+"F4.wireOp",EDGE,"E20")])]})]});
            var sketch = newSketch(context, id + "F54", { "sketchPlane" : qUnion([Q0])});
            skLineSegment(sketch, "E494.0.0", {"start": v(-37960, 3950) * mm, "end": v(-37960, 1150) * mm});
            skLineSegment(sketch, "E494.0.2", {"start": v(-35960, 1150) * mm, "end": v(-35960, 3950) * mm});
            skLineSegment(sketch, "E494.0.3", {"start": v(-35960, 3950) * mm, "end": v(-37960, 3950) * mm});
            skLineSegment(sketch, "E495.0", {"start": v(-37860, 3850) * mm, "end": v(-37860, 1150) * mm});
            skLineSegment(sketch, "E495.1", {"start": v(-36060, 3850) * mm, "end": v(-37860, 3850) * mm});
            skLineSegment(sketch, "E495.2", {"start": v(-36060, 1150) * mm, "end": v(-36060, 3850) * mm});
            skLineSegment(sketch, "E496", {"start": v(-37960, 1150) * mm, "end": v(-37860, 1150) * mm});
            skLineSegment(sketch, "E497", {"start": v(-36060, 1150) * mm, "end": v(-35960, 1150) * mm});
            skLineSegment(sketch, "E498.MirrorCS", {"start": v(-35960, 1150) * mm, "end": v(-37960, 1150) * mm});
            skLineSegment(sketch, "E499.MirrorCS", {"start": v(-37810, 3800) * mm, "end": v(-36110, 3800) * mm});
            skLineSegment(sketch, "E500.MirrorCS", {"start": v(-36110, 3800) * mm, "end": v(-36110, 1200) * mm});
            skLineSegment(sketch, "E501.MirrorCS", {"start": v(-35960, 3950) * mm, "end": v(-35960, 1150) * mm});
            skLineSegment(sketch, "E502.MirrorCS", {"start": v(-37810, 1200) * mm, "end": v(-36110, 1200) * mm});
            skLineSegment(sketch, "E503.MirrorCS", {"start": v(-37810, 3800) * mm, "end": v(-37810, 1200) * mm});
            skPoint(sketch, "E504", {"position": v(-35010, 1200) * mm});
            skPoint(sketch, "E505", {"position": v(-32160, 1200) * mm});
            skPoint(sketch, "E506", {"position": v(-28060, 1200) * mm});
            skPoint(sketch, "E507", {"position": v(-25260, 1200) * mm});
            skPoint(sketch, "E508", {"position": v(-22460, 1200) * mm});
            skLineSegment(sketch, "E509.0.0", {"start": v(-35160, 3950) * mm, "end": v(-35160, 1150) * mm});
            skLineSegment(sketch, "E509.0.2", {"start": v(-33160, 1150) * mm, "end": v(-33160, 3950) * mm});
            skLineSegment(sketch, "E509.0.3", {"start": v(-33160, 3950) * mm, "end": v(-35160, 3950) * mm});
            skLineSegment(sketch, "E510.0", {"start": v(-35060, 3850) * mm, "end": v(-35060, 1150) * mm});
            skLineSegment(sketch, "E510.1", {"start": v(-33260, 3850) * mm, "end": v(-35060, 3850) * mm});
            skLineSegment(sketch, "E510.2", {"start": v(-33260, 1150) * mm, "end": v(-33260, 3850) * mm});
            skLineSegment(sketch, "E511", {"start": v(-35160, 1150) * mm, "end": v(-35060, 1150) * mm});
            skLineSegment(sketch, "E512", {"start": v(-33260, 1150) * mm, "end": v(-33160, 1150) * mm});
            skLineSegment(sketch, "E513.MirrorCS", {"start": v(-33160, 1150) * mm, "end": v(-35160, 1150) * mm});
            skLineSegment(sketch, "E514.MirrorCS", {"start": v(-35010, 3800) * mm, "end": v(-33310, 3800) * mm});
            skLineSegment(sketch, "E515.MirrorCS", {"start": v(-33310, 3800) * mm, "end": v(-33310, 1200) * mm});
            skLineSegment(sketch, "E516.MirrorCS", {"start": v(-33160, 3950) * mm, "end": v(-33160, 1150) * mm});
            skLineSegment(sketch, "E517.MirrorCS", {"start": v(-35010, 1200) * mm, "end": v(-33310, 1200) * mm});
            skLineSegment(sketch, "E518.MirrorCS", {"start": v(-35010, 3800) * mm, "end": v(-35010, 1200) * mm});
            skLineSegment(sketch, "E519.0.0", {"start": v(-32310, 3950) * mm, "end": v(-32310, 1150) * mm});
            skLineSegment(sketch, "E519.0.2", {"start": v(-30310, 1150) * mm, "end": v(-30310, 3950) * mm});
            skLineSegment(sketch, "E519.0.3", {"start": v(-30310, 3950) * mm, "end": v(-32310, 3950) * mm});
            skLineSegment(sketch, "E520.0", {"start": v(-32210, 3850) * mm, "end": v(-32210, 1150) * mm});
            skLineSegment(sketch, "E520.1", {"start": v(-30410, 3850) * mm, "end": v(-32210, 3850) * mm});
            skLineSegment(sketch, "E520.2", {"start": v(-30410, 1150) * mm, "end": v(-30410, 3850) * mm});
            skLineSegment(sketch, "E521", {"start": v(-32310, 1150) * mm, "end": v(-32210, 1150) * mm});
            skLineSegment(sketch, "E522", {"start": v(-30410, 1150) * mm, "end": v(-30310, 1150) * mm});
            skLineSegment(sketch, "E523.MirrorCS", {"start": v(-30310, 1150) * mm, "end": v(-32310, 1150) * mm});
            skLineSegment(sketch, "E524.MirrorCS", {"start": v(-32160, 3800) * mm, "end": v(-30460, 3800) * mm});
            skLineSegment(sketch, "E525.MirrorCS", {"start": v(-30460, 3800) * mm, "end": v(-30460, 1200) * mm});
            skLineSegment(sketch, "E526.MirrorCS", {"start": v(-30310, 3950) * mm, "end": v(-30310, 1150) * mm});
            skLineSegment(sketch, "E527.MirrorCS", {"start": v(-32160, 1200) * mm, "end": v(-30460, 1200) * mm});
            skLineSegment(sketch, "E528.MirrorCS", {"start": v(-32160, 3800) * mm, "end": v(-32160, 1200) * mm});
            skLineSegment(sketch, "E529.0.0", {"start": v(-28210, 3950) * mm, "end": v(-28210, 1150) * mm});
            skLineSegment(sketch, "E529.0.2", {"start": v(-26210, 1150) * mm, "end": v(-26210, 3950) * mm});
            skLineSegment(sketch, "E529.0.3", {"start": v(-26210, 3950) * mm, "end": v(-28210, 3950) * mm});
            skLineSegment(sketch, "E530.0", {"start": v(-28110, 3850) * mm, "end": v(-28110, 1150) * mm});
            skLineSegment(sketch, "E530.1", {"start": v(-26310, 3850) * mm, "end": v(-28110, 3850) * mm});
            skLineSegment(sketch, "E530.2", {"start": v(-26310, 1150) * mm, "end": v(-26310, 3850) * mm});
            skLineSegment(sketch, "E531", {"start": v(-28210, 1150) * mm, "end": v(-28110, 1150) * mm});
            skLineSegment(sketch, "E532", {"start": v(-26310, 1150) * mm, "end": v(-26210, 1150) * mm});
            skLineSegment(sketch, "E533.MirrorCS", {"start": v(-26210, 1150) * mm, "end": v(-28210, 1150) * mm});
            skLineSegment(sketch, "E534.MirrorCS", {"start": v(-28060, 3800) * mm, "end": v(-26360, 3800) * mm});
            skLineSegment(sketch, "E535.MirrorCS", {"start": v(-26360, 3800) * mm, "end": v(-26360, 1200) * mm});
            skLineSegment(sketch, "E536.MirrorCS", {"start": v(-26210, 3950) * mm, "end": v(-26210, 1150) * mm});
            skLineSegment(sketch, "E537.MirrorCS", {"start": v(-28060, 1200) * mm, "end": v(-26360, 1200) * mm});
            skLineSegment(sketch, "E538.MirrorCS", {"start": v(-28060, 3800) * mm, "end": v(-28060, 1200) * mm});
            skLineSegment(sketch, "E539.0.0", {"start": v(-25410, 3950) * mm, "end": v(-25410, 1150) * mm});
            skLineSegment(sketch, "E539.0.2", {"start": v(-23410, 1150) * mm, "end": v(-23410, 3950) * mm});
            skLineSegment(sketch, "E539.0.3", {"start": v(-23410, 3950) * mm, "end": v(-25410, 3950) * mm});
            skLineSegment(sketch, "E540.0", {"start": v(-25310, 3850) * mm, "end": v(-25310, 1150) * mm});
            skLineSegment(sketch, "E540.1", {"start": v(-23510, 3850) * mm, "end": v(-25310, 3850) * mm});
            skLineSegment(sketch, "E540.2", {"start": v(-23510, 1150) * mm, "end": v(-23510, 3850) * mm});
            skLineSegment(sketch, "E541", {"start": v(-25410, 1150) * mm, "end": v(-25310, 1150) * mm});
            skLineSegment(sketch, "E542", {"start": v(-23510, 1150) * mm, "end": v(-23410, 1150) * mm});
            skLineSegment(sketch, "E543.MirrorCS", {"start": v(-23410, 1150) * mm, "end": v(-25410, 1150) * mm});
            skLineSegment(sketch, "E544.MirrorCS", {"start": v(-25260, 3800) * mm, "end": v(-23560, 3800) * mm});
            skLineSegment(sketch, "E545.MirrorCS", {"start": v(-23560, 3800) * mm, "end": v(-23560, 1200) * mm});
            skLineSegment(sketch, "E546.MirrorCS", {"start": v(-23410, 3950) * mm, "end": v(-23410, 1150) * mm});
            skLineSegment(sketch, "E547.MirrorCS", {"start": v(-25260, 1200) * mm, "end": v(-23560, 1200) * mm});
            skLineSegment(sketch, "E548.MirrorCS", {"start": v(-25260, 3800) * mm, "end": v(-25260, 1200) * mm});
            skLineSegment(sketch, "E549.0.0", {"start": v(-22610, 3950) * mm, "end": v(-22610, 1150) * mm});
            skLineSegment(sketch, "E549.0.2", {"start": v(-20610, 1150) * mm, "end": v(-20610, 3950) * mm});
            skLineSegment(sketch, "E549.0.3", {"start": v(-20610, 3950) * mm, "end": v(-22610, 3950) * mm});
            skLineSegment(sketch, "E550.0", {"start": v(-22510, 3850) * mm, "end": v(-22510, 1150) * mm});
            skLineSegment(sketch, "E550.1", {"start": v(-20710, 3850) * mm, "end": v(-22510, 3850) * mm});
            skLineSegment(sketch, "E550.2", {"start": v(-20710, 1150) * mm, "end": v(-20710, 3850) * mm});
            skLineSegment(sketch, "E551", {"start": v(-22610, 1150) * mm, "end": v(-22510, 1150) * mm});
            skLineSegment(sketch, "E552", {"start": v(-20710, 1150) * mm, "end": v(-20610, 1150) * mm});
            skLineSegment(sketch, "E553.MirrorCS", {"start": v(-20610, 1150) * mm, "end": v(-22610, 1150) * mm});
            skLineSegment(sketch, "E554.MirrorCS", {"start": v(-22460, 3800) * mm, "end": v(-20760, 3800) * mm});
            skLineSegment(sketch, "E555.MirrorCS", {"start": v(-20760, 3800) * mm, "end": v(-20760, 1200) * mm});
            skLineSegment(sketch, "E556.MirrorCS", {"start": v(-20610, 3950) * mm, "end": v(-20610, 1150) * mm});
            skLineSegment(sketch, "E557.MirrorCS", {"start": v(-22460, 1200) * mm, "end": v(-20760, 1200) * mm});
            skLineSegment(sketch, "E558.MirrorCS", {"start": v(-22460, 3800) * mm, "end": v(-22460, 1200) * mm});
            skLineSegment(sketch, "E559.1.0.0", {"start": v(-11360, 3800) * mm, "end": v(-11360, 1200) * mm});
            skLineSegment(sketch, "E559.1.0.1", {"start": v(-14160, 3800) * mm, "end": v(-14160, 1200) * mm});
            skLineSegment(sketch, "E559.1.0.2", {"start": v(-16810, 1150) * mm, "end": v(-16810, 3950) * mm});
            skLineSegment(sketch, "E559.1.0.3", {"start": v(-18660, 3800) * mm, "end": v(-16960, 3800) * mm});
            skLineSegment(sketch, "E559.1.0.4", {"start": v(-18810, 3950) * mm, "end": v(-18810, 1150) * mm});
            skLineSegment(sketch, "E559.1.0.5", {"start": v(-16010, 3950) * mm, "end": v(-16010, 1150) * mm});
            skLineSegment(sketch, "E559.1.0.6", {"start": v(-16960, 3800) * mm, "end": v(-16960, 1200) * mm});
            skLineSegment(sketch, "E559.1.0.7", {"start": v(-14110, 3850) * mm, "end": v(-15910, 3850) * mm});
            skPoint(sketch, "E559.1.0.8", {"position": v(-15860, 1200) * mm});
            skLineSegment(sketch, "E559.1.0.9", {"start": v(-16910, 3850) * mm, "end": v(-18710, 3850) * mm});
            skLineSegment(sketch, "E559.1.0.10", {"start": v(-13060, 3800) * mm, "end": v(-11360, 3800) * mm});
            skLineSegment(sketch, "E559.1.0.11", {"start": v(-15860, 3800) * mm, "end": v(-14160, 3800) * mm});
            skPoint(sketch, "E559.1.0.12", {"position": v(-18660, 1200) * mm});
            skLineSegment(sketch, "E559.1.0.13", {"start": v(-13060, 3800) * mm, "end": v(-13060, 1200) * mm});
            skLineSegment(sketch, "E559.1.0.14", {"start": v(-15860, 3800) * mm, "end": v(-15860, 1200) * mm});
            skPoint(sketch, "E559.1.0.15", {"position": v(-13060, 1200) * mm});
            skLineSegment(sketch, "E559.1.0.16", {"start": v(-13110, 3850) * mm, "end": v(-13110, 1150) * mm});
            skLineSegment(sketch, "E559.1.0.17", {"start": v(-14010, 1150) * mm, "end": v(-14010, 3950) * mm});
            skLineSegment(sketch, "E559.1.0.18", {"start": v(-18710, 3850) * mm, "end": v(-18710, 1150) * mm});
            skLineSegment(sketch, "E559.1.0.19", {"start": v(-15910, 3850) * mm, "end": v(-15910, 1150) * mm});
            skLineSegment(sketch, "E559.1.0.20", {"start": v(-11310, 3850) * mm, "end": v(-13110, 3850) * mm});
            skLineSegment(sketch, "E559.1.0.21", {"start": v(-11210, 1150) * mm, "end": v(-11210, 3950) * mm});
            skLineSegment(sketch, "E559.1.0.22", {"start": v(-14010, 1150) * mm, "end": v(-16010, 1150) * mm});
            skLineSegment(sketch, "E559.1.0.23", {"start": v(-16810, 1150) * mm, "end": v(-18810, 1150) * mm});
            skLineSegment(sketch, "E559.1.0.24", {"start": v(-11210, 1150) * mm, "end": v(-13210, 1150) * mm});
            skLineSegment(sketch, "E559.1.0.25", {"start": v(-11210, 3950) * mm, "end": v(-13210, 3950) * mm});
            skLineSegment(sketch, "E559.1.0.26", {"start": v(-14010, 3950) * mm, "end": v(-16010, 3950) * mm});
            skLineSegment(sketch, "E559.1.0.27", {"start": v(-16810, 3950) * mm, "end": v(-18810, 3950) * mm});
            skLineSegment(sketch, "E559.1.0.28", {"start": v(-13210, 3950) * mm, "end": v(-13210, 1150) * mm});
            skLineSegment(sketch, "E559.1.0.29", {"start": v(-13060, 1200) * mm, "end": v(-11360, 1200) * mm});
            skLineSegment(sketch, "E559.1.0.30", {"start": v(-15860, 1200) * mm, "end": v(-14160, 1200) * mm});
            skLineSegment(sketch, "E559.1.0.31", {"start": v(-18660, 1200) * mm, "end": v(-16960, 1200) * mm});
            skLineSegment(sketch, "E559.1.0.32", {"start": v(-11310, 1150) * mm, "end": v(-11310, 3850) * mm});
            skLineSegment(sketch, "E559.1.0.33", {"start": v(-16910, 1150) * mm, "end": v(-16910, 3850) * mm});
            skLineSegment(sketch, "E559.1.0.34", {"start": v(-14010, 3950) * mm, "end": v(-14010, 1150) * mm});
            skLineSegment(sketch, "E559.1.0.35", {"start": v(-16810, 3950) * mm, "end": v(-16810, 1150) * mm});
            skLineSegment(sketch, "E559.1.0.36", {"start": v(-11210, 3950) * mm, "end": v(-11210, 1150) * mm});
            skLineSegment(sketch, "E559.1.0.37", {"start": v(-18660, 3800) * mm, "end": v(-18660, 1200) * mm});
            skLineSegment(sketch, "E559.1.0.38", {"start": v(-16810, 3950) * mm, "end": v(-18810, 3950) * mm});
            skLineSegment(sketch, "E559.1.0.39", {"start": v(-16010, 3950) * mm, "end": v(-16010, 1150) * mm});
            skLineSegment(sketch, "E559.1.0.40", {"start": v(-18810, 3950) * mm, "end": v(-18810, 1150) * mm});
            skLineSegment(sketch, "E559.1.0.41", {"start": v(-13210, 3950) * mm, "end": v(-13210, 1150) * mm});
            skLineSegment(sketch, "E559.1.0.42", {"start": v(-11210, 3950) * mm, "end": v(-13210, 3950) * mm});
            skLineSegment(sketch, "E559.1.0.43", {"start": v(-14010, 3950) * mm, "end": v(-16010, 3950) * mm});
            skLineSegment(sketch, "E559.1.0.44", {"start": v(-14110, 1150) * mm, "end": v(-14110, 3850) * mm});
            skLineSegment(sketch, "E559.1.0.45", {"start": v(-14110, 1150) * mm, "end": v(-14010, 1150) * mm});
            skLineSegment(sketch, "E559.1.0.46", {"start": v(-16910, 1150) * mm, "end": v(-16810, 1150) * mm});
            skLineSegment(sketch, "E559.1.0.47", {"start": v(-11310, 1150) * mm, "end": v(-11210, 1150) * mm});
            skLineSegment(sketch, "E559.1.0.48", {"start": v(-13210, 1150) * mm, "end": v(-13110, 1150) * mm});
            skLineSegment(sketch, "E559.1.0.49", {"start": v(-16010, 1150) * mm, "end": v(-15910, 1150) * mm});
            skLineSegment(sketch, "E559.1.0.50", {"start": v(-18810, 1150) * mm, "end": v(-18710, 1150) * mm});
            skLineSegment(sketch, "E559.2.0.0", {"start": v(-1960, 3800) * mm, "end": v(-1960, 1200) * mm});
            skLineSegment(sketch, "E559.2.0.1", {"start": v(-4760, 3800) * mm, "end": v(-4760, 1200) * mm});
            skLineSegment(sketch, "E559.2.0.2", {"start": v(-7410, 1150) * mm, "end": v(-7410, 3950) * mm});
            skLineSegment(sketch, "E559.2.0.3", {"start": v(-9260, 3800) * mm, "end": v(-7560, 3800) * mm});
            skLineSegment(sketch, "E559.2.0.4", {"start": v(-9410, 3950) * mm, "end": v(-9410, 1150) * mm});
            skLineSegment(sketch, "E559.2.0.5", {"start": v(-6610, 3950) * mm, "end": v(-6610, 1150) * mm});
            skLineSegment(sketch, "E559.2.0.6", {"start": v(-7560, 3800) * mm, "end": v(-7560, 1200) * mm});
            skLineSegment(sketch, "E559.2.0.7", {"start": v(-4710, 3850) * mm, "end": v(-6510, 3850) * mm});
            skPoint(sketch, "E559.2.0.8", {"position": v(-6460, 1200) * mm});
            skLineSegment(sketch, "E559.2.0.9", {"start": v(-7510, 3850) * mm, "end": v(-9310, 3850) * mm});
            skLineSegment(sketch, "E559.2.0.10", {"start": v(-3660, 3800) * mm, "end": v(-1960, 3800) * mm});
            skLineSegment(sketch, "E559.2.0.11", {"start": v(-6460, 3800) * mm, "end": v(-4760, 3800) * mm});
            skPoint(sketch, "E559.2.0.12", {"position": v(-9260, 1200) * mm});
            skLineSegment(sketch, "E559.2.0.13", {"start": v(-3660, 3800) * mm, "end": v(-3660, 1200) * mm});
            skLineSegment(sketch, "E559.2.0.14", {"start": v(-6460, 3800) * mm, "end": v(-6460, 1200) * mm});
            skPoint(sketch, "E559.2.0.15", {"position": v(-3660, 1200) * mm});
            skLineSegment(sketch, "E559.2.0.16", {"start": v(-3710, 3850) * mm, "end": v(-3710, 1150) * mm});
            skLineSegment(sketch, "E559.2.0.17", {"start": v(-4610, 1150) * mm, "end": v(-4610, 3950) * mm});
            skLineSegment(sketch, "E559.2.0.18", {"start": v(-9310, 3850) * mm, "end": v(-9310, 1150) * mm});
            skLineSegment(sketch, "E559.2.0.19", {"start": v(-6510, 3850) * mm, "end": v(-6510, 1150) * mm});
            skLineSegment(sketch, "E559.2.0.20", {"start": v(-1910, 3850) * mm, "end": v(-3710, 3850) * mm});
            skLineSegment(sketch, "E559.2.0.21", {"start": v(-1810, 1150) * mm, "end": v(-1810, 3950) * mm});
            skLineSegment(sketch, "E559.2.0.22", {"start": v(-4610, 1150) * mm, "end": v(-6610, 1150) * mm});
            skLineSegment(sketch, "E559.2.0.23", {"start": v(-7410, 1150) * mm, "end": v(-9410, 1150) * mm});
            skLineSegment(sketch, "E559.2.0.24", {"start": v(-1810, 1150) * mm, "end": v(-3810, 1150) * mm});
            skLineSegment(sketch, "E559.2.0.25", {"start": v(-1810, 3950) * mm, "end": v(-3810, 3950) * mm});
            skLineSegment(sketch, "E559.2.0.26", {"start": v(-4610, 3950) * mm, "end": v(-6610, 3950) * mm});
            skLineSegment(sketch, "E559.2.0.27", {"start": v(-7410, 3950) * mm, "end": v(-9410, 3950) * mm});
            skLineSegment(sketch, "E559.2.0.28", {"start": v(-3810, 3950) * mm, "end": v(-3810, 1150) * mm});
            skLineSegment(sketch, "E559.2.0.29", {"start": v(-3660, 1200) * mm, "end": v(-1960, 1200) * mm});
            skLineSegment(sketch, "E559.2.0.30", {"start": v(-6460, 1200) * mm, "end": v(-4760, 1200) * mm});
            skLineSegment(sketch, "E559.2.0.31", {"start": v(-9260, 1200) * mm, "end": v(-7560, 1200) * mm});
            skLineSegment(sketch, "E559.2.0.32", {"start": v(-1910, 1150) * mm, "end": v(-1910, 3850) * mm});
            skLineSegment(sketch, "E559.2.0.33", {"start": v(-7510, 1150) * mm, "end": v(-7510, 3850) * mm});
            skLineSegment(sketch, "E559.2.0.34", {"start": v(-4610, 3950) * mm, "end": v(-4610, 1150) * mm});
            skLineSegment(sketch, "E559.2.0.35", {"start": v(-7410, 3950) * mm, "end": v(-7410, 1150) * mm});
            skLineSegment(sketch, "E559.2.0.36", {"start": v(-1810, 3950) * mm, "end": v(-1810, 1150) * mm});
            skLineSegment(sketch, "E559.2.0.37", {"start": v(-9260, 3800) * mm, "end": v(-9260, 1200) * mm});
            skLineSegment(sketch, "E559.2.0.38", {"start": v(-7410, 3950) * mm, "end": v(-9410, 3950) * mm});
            skLineSegment(sketch, "E559.2.0.39", {"start": v(-6610, 3950) * mm, "end": v(-6610, 1150) * mm});
            skLineSegment(sketch, "E559.2.0.40", {"start": v(-9410, 3950) * mm, "end": v(-9410, 1150) * mm});
            skLineSegment(sketch, "E559.2.0.41", {"start": v(-3810, 3950) * mm, "end": v(-3810, 1150) * mm});
            skLineSegment(sketch, "E559.2.0.42", {"start": v(-1810, 3950) * mm, "end": v(-3810, 3950) * mm});
            skLineSegment(sketch, "E559.2.0.43", {"start": v(-4610, 3950) * mm, "end": v(-6610, 3950) * mm});
            skLineSegment(sketch, "E559.2.0.44", {"start": v(-4710, 1150) * mm, "end": v(-4710, 3850) * mm});
            skLineSegment(sketch, "E559.2.0.45", {"start": v(-4710, 1150) * mm, "end": v(-4610, 1150) * mm});
            skLineSegment(sketch, "E559.2.0.46", {"start": v(-7510, 1150) * mm, "end": v(-7410, 1150) * mm});
            skLineSegment(sketch, "E559.2.0.47", {"start": v(-1910, 1150) * mm, "end": v(-1810, 1150) * mm});
            skLineSegment(sketch, "E559.2.0.48", {"start": v(-3810, 1150) * mm, "end": v(-3710, 1150) * mm});
            skLineSegment(sketch, "E559.2.0.49", {"start": v(-6610, 1150) * mm, "end": v(-6510, 1150) * mm});
            skLineSegment(sketch, "E559.2.0.50", {"start": v(-9410, 1150) * mm, "end": v(-9310, 1150) * mm});
            skLineSegment(sketch, "E559.direction1", {"start": v(-28210, 1150) * mm, "end": v(-18810, 1150) * mm, "construction": true});
            skSolve(sketch);
        }
        {
            var Q0;
            Q0 = qSketchRegion(id + "F54", true);
            extrude(context, id + "F55", {"entities" : qUnion([Q0]), "depth" : 50 * mm, "offsetDistance" : 25 * mm});
        }
        {
            var Q0;
            Q0=makeQuery(id+"F55.opExtrude","CAP_FACE",FACE,{"disambiguationData":[OSD([sQuery(id+"F54.wireOp",EDGE,"E494.0.0"),sQuery(id+"F54.wireOp",EDGE,"E494.0.3"),sQuery(id+"F54.wireOp",EDGE,"E496"),sQuery(id+"F54.wireOp",EDGE,"E498.MirrorCS"),sQuery(id+"F54.wireOp",EDGE,"E499.MirrorCS"),sQuery(id+"F54.wireOp",EDGE,"E500.MirrorCS"),sQuery(id+"F54.wireOp",EDGE,"E501.MirrorCS"),sQuery(id+"F54.wireOp",EDGE,"E494.0.3"),sQuery(id+"F54.wireOp",EDGE,"E502.MirrorCS"),sQuery(id+"F54.wireOp",EDGE,"E503.MirrorCS")])],"isStart":false});
            var sketch = newSketch(context, id + "F56", { "sketchPlane" : qUnion([Q0])});
            skLineSegment(sketch, "E560.0", {"start": v(-37960, 3950) * mm, "end": v(-37960, 1150) * mm});
            skLineSegment(sketch, "E560.1", {"start": v(-35960, 1150) * mm, "end": v(-35960, 3950) * mm});
            skLineSegment(sketch, "E560.2", {"start": v(-35960, 3950) * mm, "end": v(-37960, 3950) * mm});
            skLineSegment(sketch, "E560.3", {"start": v(-37860, 3850) * mm, "end": v(-37860, 1150) * mm});
            skLineSegment(sketch, "E560.4", {"start": v(-36060, 3850) * mm, "end": v(-37860, 3850) * mm});
            skLineSegment(sketch, "E560.5", {"start": v(-36060, 1150) * mm, "end": v(-36060, 3850) * mm});
            skLineSegment(sketch, "E560.6", {"start": v(-37960, 1150) * mm, "end": v(-37860, 1150) * mm});
            skLineSegment(sketch, "E560.7", {"start": v(-36060, 1150) * mm, "end": v(-35960, 1150) * mm});
            skLineSegment(sketch, "E560.8", {"start": v(-35960, 1150) * mm, "end": v(-37960, 1150) * mm});
            skLineSegment(sketch, "E560.9", {"start": v(-37810, 3800) * mm, "end": v(-36110, 3800) * mm});
            skLineSegment(sketch, "E560.10", {"start": v(-36110, 3800) * mm, "end": v(-36110, 1200) * mm});
            skLineSegment(sketch, "E560.11", {"start": v(-37960, 3950) * mm, "end": v(-37960, 1150) * mm});
            skLineSegment(sketch, "E560.12", {"start": v(-35960, 3950) * mm, "end": v(-35960, 1150) * mm});
            skLineSegment(sketch, "E560.13", {"start": v(-35960, 3950) * mm, "end": v(-37960, 3950) * mm});
            skLineSegment(sketch, "E560.14", {"start": v(-37810, 1200) * mm, "end": v(-36110, 1200) * mm});
            skLineSegment(sketch, "E560.15", {"start": v(-37810, 3800) * mm, "end": v(-37810, 1200) * mm});
            skPoint(sketch, "E560.16", {"position": v(-35010, 1200) * mm});
            skPoint(sketch, "E560.17", {"position": v(-32160, 1200) * mm});
            skPoint(sketch, "E560.18", {"position": v(-28060, 1200) * mm});
            skPoint(sketch, "E560.19", {"position": v(-25260, 1200) * mm});
            skPoint(sketch, "E560.20", {"position": v(-22460, 1200) * mm});
            skLineSegment(sketch, "E560.21", {"start": v(-35160, 3950) * mm, "end": v(-35160, 1150) * mm});
            skLineSegment(sketch, "E560.22", {"start": v(-33160, 1150) * mm, "end": v(-33160, 3950) * mm});
            skLineSegment(sketch, "E560.23", {"start": v(-33160, 3950) * mm, "end": v(-35160, 3950) * mm});
            skLineSegment(sketch, "E560.24", {"start": v(-35060, 3850) * mm, "end": v(-35060, 1150) * mm});
            skLineSegment(sketch, "E560.25", {"start": v(-33260, 3850) * mm, "end": v(-35060, 3850) * mm});
            skLineSegment(sketch, "E560.26", {"start": v(-33260, 1150) * mm, "end": v(-33260, 3850) * mm});
            skLineSegment(sketch, "E560.27", {"start": v(-35160, 1150) * mm, "end": v(-35060, 1150) * mm});
            skLineSegment(sketch, "E560.28", {"start": v(-33260, 1150) * mm, "end": v(-33160, 1150) * mm});
            skLineSegment(sketch, "E560.29", {"start": v(-33160, 1150) * mm, "end": v(-35160, 1150) * mm});
            skLineSegment(sketch, "E560.30", {"start": v(-35010, 3800) * mm, "end": v(-33310, 3800) * mm});
            skLineSegment(sketch, "E560.31", {"start": v(-33310, 3800) * mm, "end": v(-33310, 1200) * mm});
            skLineSegment(sketch, "E560.32", {"start": v(-35160, 3950) * mm, "end": v(-35160, 1150) * mm});
            skLineSegment(sketch, "E560.33", {"start": v(-33160, 3950) * mm, "end": v(-33160, 1150) * mm});
            skLineSegment(sketch, "E560.34", {"start": v(-33160, 3950) * mm, "end": v(-35160, 3950) * mm});
            skLineSegment(sketch, "E560.35", {"start": v(-35010, 1200) * mm, "end": v(-33310, 1200) * mm});
            skLineSegment(sketch, "E560.36", {"start": v(-35010, 3800) * mm, "end": v(-35010, 1200) * mm});
            skLineSegment(sketch, "E560.37", {"start": v(-32310, 3950) * mm, "end": v(-32310, 1150) * mm});
            skLineSegment(sketch, "E560.38", {"start": v(-30310, 1150) * mm, "end": v(-30310, 3950) * mm});
            skLineSegment(sketch, "E560.39", {"start": v(-30310, 3950) * mm, "end": v(-32310, 3950) * mm});
            skLineSegment(sketch, "E560.40", {"start": v(-32210, 3850) * mm, "end": v(-32210, 1150) * mm});
            skLineSegment(sketch, "E560.41", {"start": v(-30410, 3850) * mm, "end": v(-32210, 3850) * mm});
            skLineSegment(sketch, "E560.42", {"start": v(-30410, 1150) * mm, "end": v(-30410, 3850) * mm});
            skLineSegment(sketch, "E560.43", {"start": v(-32310, 1150) * mm, "end": v(-32210, 1150) * mm});
            skLineSegment(sketch, "E560.44", {"start": v(-30410, 1150) * mm, "end": v(-30310, 1150) * mm});
            skLineSegment(sketch, "E560.45", {"start": v(-30310, 1150) * mm, "end": v(-32310, 1150) * mm});
            skLineSegment(sketch, "E560.46", {"start": v(-32160, 3800) * mm, "end": v(-30460, 3800) * mm});
            skLineSegment(sketch, "E560.47", {"start": v(-30460, 3800) * mm, "end": v(-30460, 1200) * mm});
            skLineSegment(sketch, "E560.48", {"start": v(-32310, 3950) * mm, "end": v(-32310, 1150) * mm});
            skLineSegment(sketch, "E560.49", {"start": v(-30310, 3950) * mm, "end": v(-30310, 1150) * mm});
            skLineSegment(sketch, "E560.50", {"start": v(-30310, 3950) * mm, "end": v(-32310, 3950) * mm});
            skLineSegment(sketch, "E560.51", {"start": v(-32160, 1200) * mm, "end": v(-30460, 1200) * mm});
            skLineSegment(sketch, "E560.52", {"start": v(-32160, 3800) * mm, "end": v(-32160, 1200) * mm});
            skLineSegment(sketch, "E560.53", {"start": v(-28210, 3950) * mm, "end": v(-28210, 1150) * mm});
            skLineSegment(sketch, "E560.54", {"start": v(-26210, 1150) * mm, "end": v(-26210, 3950) * mm});
            skLineSegment(sketch, "E560.55", {"start": v(-26210, 3950) * mm, "end": v(-28210, 3950) * mm});
            skLineSegment(sketch, "E560.56", {"start": v(-28110, 3850) * mm, "end": v(-28110, 1150) * mm});
            skLineSegment(sketch, "E560.57", {"start": v(-26310, 3850) * mm, "end": v(-28110, 3850) * mm});
            skLineSegment(sketch, "E560.58", {"start": v(-26310, 1150) * mm, "end": v(-26310, 3850) * mm});
            skLineSegment(sketch, "E560.59", {"start": v(-28210, 1150) * mm, "end": v(-28110, 1150) * mm});
            skLineSegment(sketch, "E560.60", {"start": v(-26310, 1150) * mm, "end": v(-26210, 1150) * mm});
            skLineSegment(sketch, "E560.61", {"start": v(-26210, 1150) * mm, "end": v(-28210, 1150) * mm});
            skLineSegment(sketch, "E560.62", {"start": v(-28060, 3800) * mm, "end": v(-26360, 3800) * mm});
            skLineSegment(sketch, "E560.63", {"start": v(-26360, 3800) * mm, "end": v(-26360, 1200) * mm});
            skLineSegment(sketch, "E560.64", {"start": v(-28210, 3950) * mm, "end": v(-28210, 1150) * mm});
            skLineSegment(sketch, "E560.65", {"start": v(-26210, 3950) * mm, "end": v(-26210, 1150) * mm});
            skLineSegment(sketch, "E560.66", {"start": v(-26210, 3950) * mm, "end": v(-28210, 3950) * mm});
            skLineSegment(sketch, "E560.67", {"start": v(-28060, 1200) * mm, "end": v(-26360, 1200) * mm});
            skLineSegment(sketch, "E560.68", {"start": v(-28060, 3800) * mm, "end": v(-28060, 1200) * mm});
            skLineSegment(sketch, "E560.69", {"start": v(-25410, 3950) * mm, "end": v(-25410, 1150) * mm});
            skLineSegment(sketch, "E560.70", {"start": v(-23410, 1150) * mm, "end": v(-23410, 3950) * mm});
            skLineSegment(sketch, "E560.71", {"start": v(-23410, 3950) * mm, "end": v(-25410, 3950) * mm});
            skLineSegment(sketch, "E560.72", {"start": v(-25310, 3850) * mm, "end": v(-25310, 1150) * mm});
            skLineSegment(sketch, "E560.73", {"start": v(-23510, 3850) * mm, "end": v(-25310, 3850) * mm});
            skLineSegment(sketch, "E560.74", {"start": v(-23510, 1150) * mm, "end": v(-23510, 3850) * mm});
            skLineSegment(sketch, "E560.75", {"start": v(-25410, 1150) * mm, "end": v(-25310, 1150) * mm});
            skLineSegment(sketch, "E560.76", {"start": v(-23510, 1150) * mm, "end": v(-23410, 1150) * mm});
            skLineSegment(sketch, "E560.77", {"start": v(-23410, 1150) * mm, "end": v(-25410, 1150) * mm});
            skLineSegment(sketch, "E560.78", {"start": v(-25260, 3800) * mm, "end": v(-23560, 3800) * mm});
            skLineSegment(sketch, "E560.79", {"start": v(-23560, 3800) * mm, "end": v(-23560, 1200) * mm});
            skLineSegment(sketch, "E560.80", {"start": v(-25410, 3950) * mm, "end": v(-25410, 1150) * mm});
            skLineSegment(sketch, "E560.81", {"start": v(-23410, 3950) * mm, "end": v(-23410, 1150) * mm});
            skLineSegment(sketch, "E560.82", {"start": v(-23410, 3950) * mm, "end": v(-25410, 3950) * mm});
            skLineSegment(sketch, "E560.83", {"start": v(-25260, 1200) * mm, "end": v(-23560, 1200) * mm});
            skLineSegment(sketch, "E560.84", {"start": v(-25260, 3800) * mm, "end": v(-25260, 1200) * mm});
            skLineSegment(sketch, "E560.85", {"start": v(-22610, 3950) * mm, "end": v(-22610, 1150) * mm});
            skLineSegment(sketch, "E560.86", {"start": v(-20610, 1150) * mm, "end": v(-20610, 3950) * mm});
            skLineSegment(sketch, "E560.87", {"start": v(-20610, 3950) * mm, "end": v(-22610, 3950) * mm});
            skLineSegment(sketch, "E560.88", {"start": v(-22510, 3850) * mm, "end": v(-22510, 1150) * mm});
            skLineSegment(sketch, "E560.89", {"start": v(-20710, 3850) * mm, "end": v(-22510, 3850) * mm});
            skLineSegment(sketch, "E560.90", {"start": v(-20710, 1150) * mm, "end": v(-20710, 3850) * mm});
            skLineSegment(sketch, "E560.91", {"start": v(-22610, 1150) * mm, "end": v(-22510, 1150) * mm});
            skLineSegment(sketch, "E560.92", {"start": v(-20710, 1150) * mm, "end": v(-20610, 1150) * mm});
            skLineSegment(sketch, "E560.93", {"start": v(-20610, 1150) * mm, "end": v(-22610, 1150) * mm});
            skLineSegment(sketch, "E560.94", {"start": v(-22460, 3800) * mm, "end": v(-20760, 3800) * mm});
            skLineSegment(sketch, "E560.95", {"start": v(-20760, 3800) * mm, "end": v(-20760, 1200) * mm});
            skLineSegment(sketch, "E560.96", {"start": v(-22610, 3950) * mm, "end": v(-22610, 1150) * mm});
            skLineSegment(sketch, "E560.97", {"start": v(-20610, 3950) * mm, "end": v(-20610, 1150) * mm});
            skLineSegment(sketch, "E560.98", {"start": v(-20610, 3950) * mm, "end": v(-22610, 3950) * mm});
            skLineSegment(sketch, "E560.99", {"start": v(-22460, 1200) * mm, "end": v(-20760, 1200) * mm});
            skLineSegment(sketch, "E560.100", {"start": v(-22460, 3800) * mm, "end": v(-22460, 1200) * mm});
            skLineSegment(sketch, "E560.101", {"start": v(-11360, 3800) * mm, "end": v(-11360, 1200) * mm});
            skLineSegment(sketch, "E560.102", {"start": v(-14160, 3800) * mm, "end": v(-14160, 1200) * mm});
            skLineSegment(sketch, "E560.103", {"start": v(-16810, 1150) * mm, "end": v(-16810, 3950) * mm});
            skLineSegment(sketch, "E560.104", {"start": v(-18660, 3800) * mm, "end": v(-16960, 3800) * mm});
            skLineSegment(sketch, "E560.105", {"start": v(-18810, 3950) * mm, "end": v(-18810, 1150) * mm});
            skLineSegment(sketch, "E560.106", {"start": v(-16010, 3950) * mm, "end": v(-16010, 1150) * mm});
            skLineSegment(sketch, "E560.107", {"start": v(-16960, 3800) * mm, "end": v(-16960, 1200) * mm});
            skLineSegment(sketch, "E560.108", {"start": v(-14110, 3850) * mm, "end": v(-15910, 3850) * mm});
            skPoint(sketch, "E560.109", {"position": v(-15860, 1200) * mm});
            skLineSegment(sketch, "E560.110", {"start": v(-16910, 3850) * mm, "end": v(-18710, 3850) * mm});
            skLineSegment(sketch, "E560.111", {"start": v(-13060, 3800) * mm, "end": v(-11360, 3800) * mm});
            skLineSegment(sketch, "E560.112", {"start": v(-15860, 3800) * mm, "end": v(-14160, 3800) * mm});
            skPoint(sketch, "E560.113", {"position": v(-18660, 1200) * mm});
            skLineSegment(sketch, "E560.114", {"start": v(-13060, 3800) * mm, "end": v(-13060, 1200) * mm});
            skLineSegment(sketch, "E560.115", {"start": v(-15860, 3800) * mm, "end": v(-15860, 1200) * mm});
            skPoint(sketch, "E560.116", {"position": v(-13060, 1200) * mm});
            skLineSegment(sketch, "E560.117", {"start": v(-13110, 3850) * mm, "end": v(-13110, 1150) * mm});
            skLineSegment(sketch, "E560.118", {"start": v(-14010, 1150) * mm, "end": v(-14010, 3950) * mm});
            skLineSegment(sketch, "E560.119", {"start": v(-18710, 3850) * mm, "end": v(-18710, 1150) * mm});
            skLineSegment(sketch, "E560.120", {"start": v(-15910, 3850) * mm, "end": v(-15910, 1150) * mm});
            skLineSegment(sketch, "E560.121", {"start": v(-11310, 3850) * mm, "end": v(-13110, 3850) * mm});
            skLineSegment(sketch, "E560.122", {"start": v(-11210, 1150) * mm, "end": v(-11210, 3950) * mm});
            skLineSegment(sketch, "E560.123", {"start": v(-14010, 1150) * mm, "end": v(-16010, 1150) * mm});
            skLineSegment(sketch, "E560.124", {"start": v(-16810, 1150) * mm, "end": v(-18810, 1150) * mm});
            skLineSegment(sketch, "E560.125", {"start": v(-11210, 1150) * mm, "end": v(-13210, 1150) * mm});
            skLineSegment(sketch, "E560.126", {"start": v(-11210, 3950) * mm, "end": v(-13210, 3950) * mm});
            skLineSegment(sketch, "E560.127", {"start": v(-14010, 3950) * mm, "end": v(-16010, 3950) * mm});
            skLineSegment(sketch, "E560.128", {"start": v(-16810, 3950) * mm, "end": v(-18810, 3950) * mm});
            skLineSegment(sketch, "E560.129", {"start": v(-13210, 3950) * mm, "end": v(-13210, 1150) * mm});
            skLineSegment(sketch, "E560.130", {"start": v(-13060, 1200) * mm, "end": v(-11360, 1200) * mm});
            skLineSegment(sketch, "E560.131", {"start": v(-15860, 1200) * mm, "end": v(-14160, 1200) * mm});
            skLineSegment(sketch, "E560.132", {"start": v(-18660, 1200) * mm, "end": v(-16960, 1200) * mm});
            skLineSegment(sketch, "E560.133", {"start": v(-11310, 1150) * mm, "end": v(-11310, 3850) * mm});
            skLineSegment(sketch, "E560.134", {"start": v(-16910, 1150) * mm, "end": v(-16910, 3850) * mm});
            skLineSegment(sketch, "E560.135", {"start": v(-14010, 3950) * mm, "end": v(-14010, 1150) * mm});
            skLineSegment(sketch, "E560.136", {"start": v(-16810, 3950) * mm, "end": v(-16810, 1150) * mm});
            skLineSegment(sketch, "E560.137", {"start": v(-11210, 3950) * mm, "end": v(-11210, 1150) * mm});
            skLineSegment(sketch, "E560.138", {"start": v(-18660, 3800) * mm, "end": v(-18660, 1200) * mm});
            skLineSegment(sketch, "E560.139", {"start": v(-16810, 3950) * mm, "end": v(-18810, 3950) * mm});
            skLineSegment(sketch, "E560.140", {"start": v(-16010, 3950) * mm, "end": v(-16010, 1150) * mm});
            skLineSegment(sketch, "E560.141", {"start": v(-18810, 3950) * mm, "end": v(-18810, 1150) * mm});
            skLineSegment(sketch, "E560.142", {"start": v(-13210, 3950) * mm, "end": v(-13210, 1150) * mm});
            skLineSegment(sketch, "E560.143", {"start": v(-11210, 3950) * mm, "end": v(-13210, 3950) * mm});
            skLineSegment(sketch, "E560.144", {"start": v(-14010, 3950) * mm, "end": v(-16010, 3950) * mm});
            skLineSegment(sketch, "E560.145", {"start": v(-14110, 1150) * mm, "end": v(-14110, 3850) * mm});
            skLineSegment(sketch, "E560.146", {"start": v(-14110, 1150) * mm, "end": v(-14010, 1150) * mm});
            skLineSegment(sketch, "E560.147", {"start": v(-16910, 1150) * mm, "end": v(-16810, 1150) * mm});
            skLineSegment(sketch, "E560.148", {"start": v(-11310, 1150) * mm, "end": v(-11210, 1150) * mm});
            skLineSegment(sketch, "E560.149", {"start": v(-13210, 1150) * mm, "end": v(-13110, 1150) * mm});
            skLineSegment(sketch, "E560.150", {"start": v(-16010, 1150) * mm, "end": v(-15910, 1150) * mm});
            skLineSegment(sketch, "E560.151", {"start": v(-18810, 1150) * mm, "end": v(-18710, 1150) * mm});
            skLineSegment(sketch, "E560.152", {"start": v(-1960, 3800) * mm, "end": v(-1960, 1200) * mm});
            skLineSegment(sketch, "E560.153", {"start": v(-4760, 3800) * mm, "end": v(-4760, 1200) * mm});
            skLineSegment(sketch, "E560.154", {"start": v(-7410, 1150) * mm, "end": v(-7410, 3950) * mm});
            skLineSegment(sketch, "E560.155", {"start": v(-9260, 3800) * mm, "end": v(-7560, 3800) * mm});
            skLineSegment(sketch, "E560.156", {"start": v(-9410, 3950) * mm, "end": v(-9410, 1150) * mm});
            skLineSegment(sketch, "E560.157", {"start": v(-6610, 3950) * mm, "end": v(-6610, 1150) * mm});
            skLineSegment(sketch, "E560.158", {"start": v(-7560, 3800) * mm, "end": v(-7560, 1200) * mm});
            skLineSegment(sketch, "E560.159", {"start": v(-4710, 3850) * mm, "end": v(-6510, 3850) * mm});
            skPoint(sketch, "E560.160", {"position": v(-6460, 1200) * mm});
            skLineSegment(sketch, "E560.161", {"start": v(-7510, 3850) * mm, "end": v(-9310, 3850) * mm});
            skLineSegment(sketch, "E560.162", {"start": v(-3660, 3800) * mm, "end": v(-1960, 3800) * mm});
            skLineSegment(sketch, "E560.163", {"start": v(-6460, 3800) * mm, "end": v(-4760, 3800) * mm});
            skPoint(sketch, "E560.164", {"position": v(-9260, 1200) * mm});
            skLineSegment(sketch, "E560.165", {"start": v(-3660, 3800) * mm, "end": v(-3660, 1200) * mm});
            skLineSegment(sketch, "E560.166", {"start": v(-6460, 3800) * mm, "end": v(-6460, 1200) * mm});
            skPoint(sketch, "E560.167", {"position": v(-3660, 1200) * mm});
            skLineSegment(sketch, "E560.168", {"start": v(-3710, 3850) * mm, "end": v(-3710, 1150) * mm});
            skLineSegment(sketch, "E560.169", {"start": v(-4610, 1150) * mm, "end": v(-4610, 3950) * mm});
            skLineSegment(sketch, "E560.170", {"start": v(-9310, 3850) * mm, "end": v(-9310, 1150) * mm});
            skLineSegment(sketch, "E560.171", {"start": v(-6510, 3850) * mm, "end": v(-6510, 1150) * mm});
            skLineSegment(sketch, "E560.172", {"start": v(-1910, 3850) * mm, "end": v(-3710, 3850) * mm});
            skLineSegment(sketch, "E560.173", {"start": v(-1810, 1150) * mm, "end": v(-1810, 3950) * mm});
            skLineSegment(sketch, "E560.174", {"start": v(-4610, 1150) * mm, "end": v(-6610, 1150) * mm});
            skLineSegment(sketch, "E560.175", {"start": v(-7410, 1150) * mm, "end": v(-9410, 1150) * mm});
            skLineSegment(sketch, "E560.176", {"start": v(-1810, 1150) * mm, "end": v(-3810, 1150) * mm});
            skLineSegment(sketch, "E560.177", {"start": v(-1810, 3950) * mm, "end": v(-3810, 3950) * mm});
            skLineSegment(sketch, "E560.178", {"start": v(-4610, 3950) * mm, "end": v(-6610, 3950) * mm});
            skLineSegment(sketch, "E560.179", {"start": v(-7410, 3950) * mm, "end": v(-9410, 3950) * mm});
            skLineSegment(sketch, "E560.180", {"start": v(-3810, 3950) * mm, "end": v(-3810, 1150) * mm});
            skLineSegment(sketch, "E560.181", {"start": v(-3660, 1200) * mm, "end": v(-1960, 1200) * mm});
            skLineSegment(sketch, "E560.182", {"start": v(-6460, 1200) * mm, "end": v(-4760, 1200) * mm});
            skLineSegment(sketch, "E560.183", {"start": v(-9260, 1200) * mm, "end": v(-7560, 1200) * mm});
            skLineSegment(sketch, "E560.184", {"start": v(-1910, 1150) * mm, "end": v(-1910, 3850) * mm});
            skLineSegment(sketch, "E560.185", {"start": v(-7510, 1150) * mm, "end": v(-7510, 3850) * mm});
            skLineSegment(sketch, "E560.186", {"start": v(-4610, 3950) * mm, "end": v(-4610, 1150) * mm});
            skLineSegment(sketch, "E560.187", {"start": v(-7410, 3950) * mm, "end": v(-7410, 1150) * mm});
            skLineSegment(sketch, "E560.188", {"start": v(-1810, 3950) * mm, "end": v(-1810, 1150) * mm});
            skLineSegment(sketch, "E560.189", {"start": v(-9260, 3800) * mm, "end": v(-9260, 1200) * mm});
            skLineSegment(sketch, "E560.190", {"start": v(-7410, 3950) * mm, "end": v(-9410, 3950) * mm});
            skLineSegment(sketch, "E560.191", {"start": v(-6610, 3950) * mm, "end": v(-6610, 1150) * mm});
            skLineSegment(sketch, "E560.192", {"start": v(-9410, 3950) * mm, "end": v(-9410, 1150) * mm});
            skLineSegment(sketch, "E560.193", {"start": v(-3810, 3950) * mm, "end": v(-3810, 1150) * mm});
            skLineSegment(sketch, "E560.194", {"start": v(-1810, 3950) * mm, "end": v(-3810, 3950) * mm});
            skLineSegment(sketch, "E560.195", {"start": v(-4610, 3950) * mm, "end": v(-6610, 3950) * mm});
            skLineSegment(sketch, "E560.196", {"start": v(-4710, 1150) * mm, "end": v(-4710, 3850) * mm});
            skLineSegment(sketch, "E560.197", {"start": v(-4710, 1150) * mm, "end": v(-4610, 1150) * mm});
            skLineSegment(sketch, "E560.198", {"start": v(-7510, 1150) * mm, "end": v(-7410, 1150) * mm});
            skLineSegment(sketch, "E560.199", {"start": v(-1910, 1150) * mm, "end": v(-1810, 1150) * mm});
            skLineSegment(sketch, "E560.200", {"start": v(-3810, 1150) * mm, "end": v(-3710, 1150) * mm});
            skLineSegment(sketch, "E560.201", {"start": v(-6610, 1150) * mm, "end": v(-6510, 1150) * mm});
            skLineSegment(sketch, "E560.202", {"start": v(-9410, 1150) * mm, "end": v(-9310, 1150) * mm});
            skLineSegment(sketch, "E560.203", {"start": v(-28210, 1150) * mm, "end": v(-18810, 1150) * mm});
            skSolve(sketch);
        }
        {
            var Q0;
            {var subQ2=sQuery(id+"F56.wireOp",EDGE,"E560.1");Q0=makeQuery(id+"F56.imprint","IMPRINT",FACE,{"disambiguationData":[TD([[makeQuery(id+"F56.imprint","IMPRINT",EDGE,{"derivedFrom":subQ2}),1.0]])]});}
            var Q1;
            {var subQ2=sQuery(id+"F56.wireOp",EDGE,"E560.22");Q1=makeQuery(id+"F56.imprint","IMPRINT",FACE,{"disambiguationData":[TD([[makeQuery(id+"F56.imprint","IMPRINT",EDGE,{"derivedFrom":subQ2}),1.0]])]});}
            var Q2;
            {var subQ2=sQuery(id+"F56.wireOp",EDGE,"E560.38");Q2=makeQuery(id+"F56.imprint","IMPRINT",FACE,{"disambiguationData":[TD([[makeQuery(id+"F56.imprint","IMPRINT",EDGE,{"derivedFrom":subQ2}),1.0]])]});}
            var Q3;
            {var subQ2=sQuery(id+"F56.wireOp",EDGE,"E560.54");Q3=makeQuery(id+"F56.imprint","IMPRINT",FACE,{"disambiguationData":[TD([[makeQuery(id+"F56.imprint","IMPRINT",EDGE,{"derivedFrom":subQ2}),1.0]])]});}
            var Q4;
            {var subQ4=sQuery(id+"F56.wireOp",EDGE,"E560.70");Q4=makeQuery(id+"F56.imprint","IMPRINT",FACE,{"disambiguationData":[TD([[makeQuery(id+"F56.imprint","IMPRINT",EDGE,{"derivedFrom":subQ4}),1.0]])]});}
            var Q5;
            {var subQ2=sQuery(id+"F56.wireOp",EDGE,"E560.86");Q5=makeQuery(id+"F56.imprint","IMPRINT",FACE,{"disambiguationData":[TD([[makeQuery(id+"F56.imprint","IMPRINT",EDGE,{"derivedFrom":subQ2}),1.0]])]});}
            var Q6;
            {var subQ2=sQuery(id+"F56.wireOp",EDGE,"E560.103");Q6=makeQuery(id+"F56.imprint","IMPRINT",FACE,{"disambiguationData":[TD([[makeQuery(id+"F56.imprint","IMPRINT",EDGE,{"derivedFrom":subQ2}),1.0]])]});}
            var Q7;
            Q7=makeQuery(id+"F56.imprint","IMPRINT",FACE,{"disambiguationData":[TD([[makeQuery(id+"F56.imprint","IMPRINT",EDGE,{"derivedFrom":sQuery(id+"F56.wireOp",EDGE,"E560.108")}),-1.0]])]});
            var Q8;
            {var subQ1=sQuery(id+"F56.wireOp",EDGE,"E560.117");Q8=makeQuery(id+"F56.imprint","IMPRINT",FACE,{"disambiguationData":[TD([[makeQuery(id+"F56.imprint","IMPRINT",EDGE,{"derivedFrom":subQ1}),-1.0]])]});}
            var Q9;
            {var subQ2=sQuery(id+"F56.wireOp",EDGE,"E560.154");Q9=makeQuery(id+"F56.imprint","IMPRINT",FACE,{"disambiguationData":[TD([[makeQuery(id+"F56.imprint","IMPRINT",EDGE,{"derivedFrom":subQ2}),1.0]])]});}
            var Q10;
            Q10=makeQuery(id+"F56.imprint","IMPRINT",FACE,{"disambiguationData":[TD([[makeQuery(id+"F56.imprint","IMPRINT",EDGE,{"derivedFrom":sQuery(id+"F56.wireOp",EDGE,"E560.159")}),-1.0]])]});
            var Q11;
            {var subQ1=sQuery(id+"F56.wireOp",EDGE,"E560.168");Q11=makeQuery(id+"F56.imprint","IMPRINT",FACE,{"disambiguationData":[TD([[makeQuery(id+"F56.imprint","IMPRINT",EDGE,{"derivedFrom":subQ1}),-1.0]])]});}
            extrude(context, id + "F57", {"entities" : qUnion([Q0, Q1, Q2, Q3, Q4, Q5, Q6, Q7, Q8, Q9, Q10, Q11]), "operationType" : NewBodyOperationType.ADD, "depth" : 50 * mm, "offsetDistance" : 25 * mm});
        }
        {
            var Q0;
            Q0=makeQuery(id+"F5.boolean.opBoolean","MERGE",FACE,{"derivedFrom":[makeQuery(id+"F3.boolean.opBoolean","COPY",FACE,{"derivedFrom":makeQuery(id+"F3.opExtrude","SWEPT_FACE",FACE,{"disambiguationData":[OSD([sQuery(id+"F2.wireOp",EDGE,"E19.13")])]})}),makeQuery(id+"F5.opExtrude","SWEPT_FACE",FACE,{"disambiguationData":[OSD([sQuery(id+"F4.wireOp",EDGE,"E30.0")])]})]});
            var sketch = newSketch(context, id + "F58", { "sketchPlane" : qUnion([Q0])});
            skLineSegment(sketch, "E561.0", {"start": v(37410, 3950) * mm, "end": v(37410, 1150) * mm});
            skLineSegment(sketch, "E561.1", {"start": v(35410, 1150) * mm, "end": v(35410, 3950) * mm});
            skLineSegment(sketch, "E561.2", {"start": v(35410, 3950) * mm, "end": v(37410, 3950) * mm});
            skLineSegment(sketch, "E561.3", {"start": v(37310, 3850) * mm, "end": v(37310, 1150) * mm});
            skLineSegment(sketch, "E561.4", {"start": v(35510, 3850) * mm, "end": v(37310, 3850) * mm});
            skLineSegment(sketch, "E561.5", {"start": v(35510, 1150) * mm, "end": v(35510, 3850) * mm});
            skLineSegment(sketch, "E561.6", {"start": v(37410, 1150) * mm, "end": v(37310, 1150) * mm});
            skLineSegment(sketch, "E561.7", {"start": v(35510, 1150) * mm, "end": v(35410, 1150) * mm});
            skLineSegment(sketch, "E561.8", {"start": v(35410, 1150) * mm, "end": v(37410, 1150) * mm});
            skLineSegment(sketch, "E561.9", {"start": v(37260, 3800) * mm, "end": v(35560, 3800) * mm});
            skLineSegment(sketch, "E561.10", {"start": v(35560, 3800) * mm, "end": v(35560, 1200) * mm});
            skLineSegment(sketch, "E561.11", {"start": v(37410, 3950) * mm, "end": v(37410, 1150) * mm});
            skLineSegment(sketch, "E561.12", {"start": v(35410, 3950) * mm, "end": v(35410, 1150) * mm});
            skLineSegment(sketch, "E561.13", {"start": v(35410, 3950) * mm, "end": v(37410, 3950) * mm});
            skLineSegment(sketch, "E561.14", {"start": v(37260, 1200) * mm, "end": v(35560, 1200) * mm});
            skLineSegment(sketch, "E561.15", {"start": v(37260, 3800) * mm, "end": v(37260, 1200) * mm});
            skPoint(sketch, "E561.16", {"position": v(35010, 1200) * mm});
            skPoint(sketch, "E561.17", {"position": v(32160, 1200) * mm});
            skPoint(sketch, "E561.18", {"position": v(28060, 1200) * mm});
            skPoint(sketch, "E561.19", {"position": v(25260, 1200) * mm});
            skPoint(sketch, "E561.20", {"position": v(22460, 1200) * mm});
            skLineSegment(sketch, "E561.21", {"start": v(35160, 3950) * mm, "end": v(35160, 1150) * mm});
            skLineSegment(sketch, "E561.22", {"start": v(33160, 1150) * mm, "end": v(33160, 3950) * mm});
            skLineSegment(sketch, "E561.23", {"start": v(33160, 3950) * mm, "end": v(35160, 3950) * mm});
            skLineSegment(sketch, "E561.24", {"start": v(35060, 3850) * mm, "end": v(35060, 1150) * mm});
            skLineSegment(sketch, "E561.25", {"start": v(33260, 3850) * mm, "end": v(35060, 3850) * mm});
            skLineSegment(sketch, "E561.26", {"start": v(33260, 1150) * mm, "end": v(33260, 3850) * mm});
            skLineSegment(sketch, "E561.27", {"start": v(35160, 1150) * mm, "end": v(35060, 1150) * mm});
            skLineSegment(sketch, "E561.28", {"start": v(33260, 1150) * mm, "end": v(33160, 1150) * mm});
            skLineSegment(sketch, "E561.29", {"start": v(33160, 1150) * mm, "end": v(35160, 1150) * mm});
            skLineSegment(sketch, "E561.30", {"start": v(35010, 3800) * mm, "end": v(33310, 3800) * mm});
            skLineSegment(sketch, "E561.31", {"start": v(33310, 3800) * mm, "end": v(33310, 1200) * mm});
            skLineSegment(sketch, "E561.32", {"start": v(35160, 3950) * mm, "end": v(35160, 1150) * mm});
            skLineSegment(sketch, "E561.33", {"start": v(33160, 3950) * mm, "end": v(33160, 1150) * mm});
            skLineSegment(sketch, "E561.34", {"start": v(33160, 3950) * mm, "end": v(35160, 3950) * mm});
            skLineSegment(sketch, "E561.35", {"start": v(35010, 1200) * mm, "end": v(33310, 1200) * mm});
            skLineSegment(sketch, "E561.36", {"start": v(35010, 3800) * mm, "end": v(35010, 1200) * mm});
            skLineSegment(sketch, "E561.37", {"start": v(32310, 3950) * mm, "end": v(32310, 1150) * mm});
            skLineSegment(sketch, "E561.38", {"start": v(30310, 1150) * mm, "end": v(30310, 3950) * mm});
            skLineSegment(sketch, "E561.39", {"start": v(30310, 3950) * mm, "end": v(32310, 3950) * mm});
            skLineSegment(sketch, "E561.40", {"start": v(32210, 3850) * mm, "end": v(32210, 1150) * mm});
            skLineSegment(sketch, "E561.41", {"start": v(30410, 3850) * mm, "end": v(32210, 3850) * mm});
            skLineSegment(sketch, "E561.42", {"start": v(30410, 1150) * mm, "end": v(30410, 3850) * mm});
            skLineSegment(sketch, "E561.43", {"start": v(32310, 1150) * mm, "end": v(32210, 1150) * mm});
            skLineSegment(sketch, "E561.44", {"start": v(30410, 1150) * mm, "end": v(30310, 1150) * mm});
            skLineSegment(sketch, "E561.45", {"start": v(30310, 1150) * mm, "end": v(32310, 1150) * mm});
            skLineSegment(sketch, "E561.46", {"start": v(32160, 3800) * mm, "end": v(30460, 3800) * mm});
            skLineSegment(sketch, "E561.47", {"start": v(30460, 3800) * mm, "end": v(30460, 1200) * mm});
            skLineSegment(sketch, "E561.48", {"start": v(32310, 3950) * mm, "end": v(32310, 1150) * mm});
            skLineSegment(sketch, "E561.49", {"start": v(30310, 3950) * mm, "end": v(30310, 1150) * mm});
            skLineSegment(sketch, "E561.50", {"start": v(30310, 3950) * mm, "end": v(32310, 3950) * mm});
            skLineSegment(sketch, "E561.51", {"start": v(32160, 1200) * mm, "end": v(30460, 1200) * mm});
            skLineSegment(sketch, "E561.52", {"start": v(32160, 3800) * mm, "end": v(32160, 1200) * mm});
            skLineSegment(sketch, "E561.53", {"start": v(28210, 3950) * mm, "end": v(28210, 1150) * mm});
            skLineSegment(sketch, "E561.54", {"start": v(26210, 1150) * mm, "end": v(26210, 3950) * mm});
            skLineSegment(sketch, "E561.55", {"start": v(26210, 3950) * mm, "end": v(28210, 3950) * mm});
            skLineSegment(sketch, "E561.56", {"start": v(28110, 3850) * mm, "end": v(28110, 1150) * mm});
            skLineSegment(sketch, "E561.57", {"start": v(26310, 3850) * mm, "end": v(28110, 3850) * mm});
            skLineSegment(sketch, "E561.58", {"start": v(26310, 1150) * mm, "end": v(26310, 3850) * mm});
            skLineSegment(sketch, "E561.59", {"start": v(28210, 1150) * mm, "end": v(28110, 1150) * mm});
            skLineSegment(sketch, "E561.60", {"start": v(26310, 1150) * mm, "end": v(26210, 1150) * mm});
            skLineSegment(sketch, "E561.61", {"start": v(26210, 1150) * mm, "end": v(28210, 1150) * mm});
            skLineSegment(sketch, "E561.62", {"start": v(28060, 3800) * mm, "end": v(26360, 3800) * mm});
            skLineSegment(sketch, "E561.63", {"start": v(26360, 3800) * mm, "end": v(26360, 1200) * mm});
            skLineSegment(sketch, "E561.64", {"start": v(28210, 3950) * mm, "end": v(28210, 1150) * mm});
            skLineSegment(sketch, "E561.65", {"start": v(26210, 3950) * mm, "end": v(26210, 1150) * mm});
            skLineSegment(sketch, "E561.66", {"start": v(26210, 3950) * mm, "end": v(28210, 3950) * mm});
            skLineSegment(sketch, "E561.67", {"start": v(28060, 1200) * mm, "end": v(26360, 1200) * mm});
            skLineSegment(sketch, "E561.68", {"start": v(28060, 3800) * mm, "end": v(28060, 1200) * mm});
            skLineSegment(sketch, "E561.69", {"start": v(25410, 3950) * mm, "end": v(25410, 1150) * mm});
            skLineSegment(sketch, "E561.70", {"start": v(23410, 1150) * mm, "end": v(23410, 3950) * mm});
            skLineSegment(sketch, "E561.71", {"start": v(23410, 3950) * mm, "end": v(25410, 3950) * mm});
            skLineSegment(sketch, "E561.72", {"start": v(25310, 3850) * mm, "end": v(25310, 1150) * mm});
            skLineSegment(sketch, "E561.73", {"start": v(23510, 3850) * mm, "end": v(25310, 3850) * mm});
            skLineSegment(sketch, "E561.74", {"start": v(23510, 1150) * mm, "end": v(23510, 3850) * mm});
            skLineSegment(sketch, "E561.75", {"start": v(25410, 1150) * mm, "end": v(25310, 1150) * mm});
            skLineSegment(sketch, "E561.76", {"start": v(23510, 1150) * mm, "end": v(23410, 1150) * mm});
            skLineSegment(sketch, "E561.77", {"start": v(23410, 1150) * mm, "end": v(25410, 1150) * mm});
            skLineSegment(sketch, "E561.78", {"start": v(25260, 3800) * mm, "end": v(23560, 3800) * mm});
            skLineSegment(sketch, "E561.79", {"start": v(23560, 3800) * mm, "end": v(23560, 1200) * mm});
            skLineSegment(sketch, "E561.80", {"start": v(25410, 3950) * mm, "end": v(25410, 1150) * mm});
            skLineSegment(sketch, "E561.81", {"start": v(23410, 3950) * mm, "end": v(23410, 1150) * mm});
            skLineSegment(sketch, "E561.82", {"start": v(23410, 3950) * mm, "end": v(25410, 3950) * mm});
            skLineSegment(sketch, "E561.83", {"start": v(25260, 1200) * mm, "end": v(23560, 1200) * mm});
            skLineSegment(sketch, "E561.84", {"start": v(25260, 3800) * mm, "end": v(25260, 1200) * mm});
            skLineSegment(sketch, "E561.85", {"start": v(22610, 3950) * mm, "end": v(22610, 1150) * mm});
            skLineSegment(sketch, "E561.86", {"start": v(20610, 1150) * mm, "end": v(20610, 3950) * mm});
            skLineSegment(sketch, "E561.87", {"start": v(20610, 3950) * mm, "end": v(22610, 3950) * mm});
            skLineSegment(sketch, "E561.88", {"start": v(22510, 3850) * mm, "end": v(22510, 1150) * mm});
            skLineSegment(sketch, "E561.89", {"start": v(20710, 3850) * mm, "end": v(22510, 3850) * mm});
            skLineSegment(sketch, "E561.90", {"start": v(20710, 1150) * mm, "end": v(20710, 3850) * mm});
            skLineSegment(sketch, "E561.91", {"start": v(22610, 1150) * mm, "end": v(22510, 1150) * mm});
            skLineSegment(sketch, "E561.92", {"start": v(20710, 1150) * mm, "end": v(20610, 1150) * mm});
            skLineSegment(sketch, "E561.93", {"start": v(20610, 1150) * mm, "end": v(22610, 1150) * mm});
            skLineSegment(sketch, "E561.94", {"start": v(22460, 3800) * mm, "end": v(20760, 3800) * mm});
            skLineSegment(sketch, "E561.95", {"start": v(20760, 3800) * mm, "end": v(20760, 1200) * mm});
            skLineSegment(sketch, "E561.96", {"start": v(22610, 3950) * mm, "end": v(22610, 1150) * mm});
            skLineSegment(sketch, "E561.97", {"start": v(20610, 3950) * mm, "end": v(20610, 1150) * mm});
            skLineSegment(sketch, "E561.98", {"start": v(20610, 3950) * mm, "end": v(22610, 3950) * mm});
            skLineSegment(sketch, "E561.99", {"start": v(22460, 1200) * mm, "end": v(20760, 1200) * mm});
            skLineSegment(sketch, "E561.100", {"start": v(22460, 3800) * mm, "end": v(22460, 1200) * mm});
            skLineSegment(sketch, "E561.101", {"start": v(11360, 3800) * mm, "end": v(11360, 1200) * mm});
            skLineSegment(sketch, "E561.102", {"start": v(14160, 3800) * mm, "end": v(14160, 1200) * mm});
            skLineSegment(sketch, "E561.103", {"start": v(16810, 1150) * mm, "end": v(16810, 3950) * mm});
            skLineSegment(sketch, "E561.104", {"start": v(18660, 3800) * mm, "end": v(16960, 3800) * mm});
            skLineSegment(sketch, "E561.105", {"start": v(18810, 3950) * mm, "end": v(18810, 1150) * mm});
            skLineSegment(sketch, "E561.106", {"start": v(16010, 3950) * mm, "end": v(16010, 1150) * mm});
            skLineSegment(sketch, "E561.107", {"start": v(16960, 3800) * mm, "end": v(16960, 1200) * mm});
            skLineSegment(sketch, "E561.108", {"start": v(14110, 3850) * mm, "end": v(15910, 3850) * mm});
            skPoint(sketch, "E561.109", {"position": v(15860, 1200) * mm});
            skLineSegment(sketch, "E561.110", {"start": v(16910, 3850) * mm, "end": v(18710, 3850) * mm});
            skLineSegment(sketch, "E561.111", {"start": v(13060, 3800) * mm, "end": v(11360, 3800) * mm});
            skLineSegment(sketch, "E561.112", {"start": v(15860, 3800) * mm, "end": v(14160, 3800) * mm});
            skPoint(sketch, "E561.113", {"position": v(18660, 1200) * mm});
            skLineSegment(sketch, "E561.114", {"start": v(13060, 3800) * mm, "end": v(13060, 1200) * mm});
            skLineSegment(sketch, "E561.115", {"start": v(15860, 3800) * mm, "end": v(15860, 1200) * mm});
            skPoint(sketch, "E561.116", {"position": v(13060, 1200) * mm});
            skLineSegment(sketch, "E561.117", {"start": v(13110, 3850) * mm, "end": v(13110, 1150) * mm});
            skLineSegment(sketch, "E561.118", {"start": v(14010, 1150) * mm, "end": v(14010, 3950) * mm});
            skLineSegment(sketch, "E561.119", {"start": v(18710, 3850) * mm, "end": v(18710, 1150) * mm});
            skLineSegment(sketch, "E561.120", {"start": v(15910, 3850) * mm, "end": v(15910, 1150) * mm});
            skLineSegment(sketch, "E561.121", {"start": v(11310, 3850) * mm, "end": v(13110, 3850) * mm});
            skLineSegment(sketch, "E561.122", {"start": v(11210, 1150) * mm, "end": v(11210, 3950) * mm});
            skLineSegment(sketch, "E561.123", {"start": v(14010, 1150) * mm, "end": v(16010, 1150) * mm});
            skLineSegment(sketch, "E561.124", {"start": v(16810, 1150) * mm, "end": v(18810, 1150) * mm});
            skLineSegment(sketch, "E561.125", {"start": v(11210, 1150) * mm, "end": v(13210, 1150) * mm});
            skLineSegment(sketch, "E561.126", {"start": v(11210, 3950) * mm, "end": v(13210, 3950) * mm});
            skLineSegment(sketch, "E561.127", {"start": v(14010, 3950) * mm, "end": v(16010, 3950) * mm});
            skLineSegment(sketch, "E561.128", {"start": v(16810, 3950) * mm, "end": v(18810, 3950) * mm});
            skLineSegment(sketch, "E561.129", {"start": v(13210, 3950) * mm, "end": v(13210, 1150) * mm});
            skLineSegment(sketch, "E561.130", {"start": v(13060, 1200) * mm, "end": v(11360, 1200) * mm});
            skLineSegment(sketch, "E561.131", {"start": v(15860, 1200) * mm, "end": v(14160, 1200) * mm});
            skLineSegment(sketch, "E561.132", {"start": v(18660, 1200) * mm, "end": v(16960, 1200) * mm});
            skLineSegment(sketch, "E561.133", {"start": v(11310, 1150) * mm, "end": v(11310, 3850) * mm});
            skLineSegment(sketch, "E561.134", {"start": v(16910, 1150) * mm, "end": v(16910, 3850) * mm});
            skLineSegment(sketch, "E561.135", {"start": v(14010, 3950) * mm, "end": v(14010, 1150) * mm});
            skLineSegment(sketch, "E561.136", {"start": v(16810, 3950) * mm, "end": v(16810, 1150) * mm});
            skLineSegment(sketch, "E561.137", {"start": v(11210, 3950) * mm, "end": v(11210, 1150) * mm});
            skLineSegment(sketch, "E561.138", {"start": v(18660, 3800) * mm, "end": v(18660, 1200) * mm});
            skLineSegment(sketch, "E561.139", {"start": v(16810, 3950) * mm, "end": v(18810, 3950) * mm});
            skLineSegment(sketch, "E561.140", {"start": v(16010, 3950) * mm, "end": v(16010, 1150) * mm});
            skLineSegment(sketch, "E561.141", {"start": v(18810, 3950) * mm, "end": v(18810, 1150) * mm});
            skLineSegment(sketch, "E561.142", {"start": v(13210, 3950) * mm, "end": v(13210, 1150) * mm});
            skLineSegment(sketch, "E561.143", {"start": v(11210, 3950) * mm, "end": v(13210, 3950) * mm});
            skLineSegment(sketch, "E561.144", {"start": v(14010, 3950) * mm, "end": v(16010, 3950) * mm});
            skLineSegment(sketch, "E561.145", {"start": v(14110, 1150) * mm, "end": v(14110, 3850) * mm});
            skLineSegment(sketch, "E561.146", {"start": v(14110, 1150) * mm, "end": v(14010, 1150) * mm});
            skLineSegment(sketch, "E561.147", {"start": v(16910, 1150) * mm, "end": v(16810, 1150) * mm});
            skLineSegment(sketch, "E561.148", {"start": v(11310, 1150) * mm, "end": v(11210, 1150) * mm});
            skLineSegment(sketch, "E561.149", {"start": v(13210, 1150) * mm, "end": v(13110, 1150) * mm});
            skLineSegment(sketch, "E561.150", {"start": v(16010, 1150) * mm, "end": v(15910, 1150) * mm});
            skLineSegment(sketch, "E561.151", {"start": v(18810, 1150) * mm, "end": v(18710, 1150) * mm});
            skLineSegment(sketch, "E561.152", {"start": v(1960, 3800) * mm, "end": v(1960, 1200) * mm});
            skLineSegment(sketch, "E561.153", {"start": v(4760, 3800) * mm, "end": v(4760, 1200) * mm});
            skLineSegment(sketch, "E561.154", {"start": v(7410, 1150) * mm, "end": v(7410, 3950) * mm});
            skLineSegment(sketch, "E561.155", {"start": v(9260, 3800) * mm, "end": v(7560, 3800) * mm});
            skLineSegment(sketch, "E561.156", {"start": v(9410, 3950) * mm, "end": v(9410, 1150) * mm});
            skLineSegment(sketch, "E561.157", {"start": v(6610, 3950) * mm, "end": v(6610, 1150) * mm});
            skLineSegment(sketch, "E561.158", {"start": v(7560, 3800) * mm, "end": v(7560, 1200) * mm});
            skLineSegment(sketch, "E561.159", {"start": v(4710, 3850) * mm, "end": v(6510, 3850) * mm});
            skPoint(sketch, "E561.160", {"position": v(6460, 1200) * mm});
            skLineSegment(sketch, "E561.161", {"start": v(7510, 3850) * mm, "end": v(9310, 3850) * mm});
            skLineSegment(sketch, "E561.162", {"start": v(3660, 3800) * mm, "end": v(1960, 3800) * mm});
            skLineSegment(sketch, "E561.163", {"start": v(6460, 3800) * mm, "end": v(4760, 3800) * mm});
            skPoint(sketch, "E561.164", {"position": v(9260, 1200) * mm});
            skLineSegment(sketch, "E561.165", {"start": v(3660, 3800) * mm, "end": v(3660, 1200) * mm});
            skLineSegment(sketch, "E561.166", {"start": v(6460, 3800) * mm, "end": v(6460, 1200) * mm});
            skPoint(sketch, "E561.167", {"position": v(3660, 1200) * mm});
            skLineSegment(sketch, "E561.168", {"start": v(3710, 3850) * mm, "end": v(3710, 1150) * mm});
            skLineSegment(sketch, "E561.169", {"start": v(4610, 1150) * mm, "end": v(4610, 3950) * mm});
            skLineSegment(sketch, "E561.170", {"start": v(9310, 3850) * mm, "end": v(9310, 1150) * mm});
            skLineSegment(sketch, "E561.171", {"start": v(6510, 3850) * mm, "end": v(6510, 1150) * mm});
            skLineSegment(sketch, "E561.172", {"start": v(1910, 3850) * mm, "end": v(3710, 3850) * mm});
            skLineSegment(sketch, "E561.173", {"start": v(1810, 1150) * mm, "end": v(1810, 3950) * mm});
            skLineSegment(sketch, "E561.174", {"start": v(4610, 1150) * mm, "end": v(6610, 1150) * mm});
            skLineSegment(sketch, "E561.175", {"start": v(7410, 1150) * mm, "end": v(9410, 1150) * mm});
            skLineSegment(sketch, "E561.176", {"start": v(1810, 1150) * mm, "end": v(3810, 1150) * mm});
            skLineSegment(sketch, "E561.177", {"start": v(1810, 3950) * mm, "end": v(3810, 3950) * mm});
            skLineSegment(sketch, "E561.178", {"start": v(4610, 3950) * mm, "end": v(6610, 3950) * mm});
            skLineSegment(sketch, "E561.179", {"start": v(7410, 3950) * mm, "end": v(9410, 3950) * mm});
            skLineSegment(sketch, "E561.180", {"start": v(3810, 3950) * mm, "end": v(3810, 1150) * mm});
            skLineSegment(sketch, "E561.181", {"start": v(3660, 1200) * mm, "end": v(1960, 1200) * mm});
            skLineSegment(sketch, "E561.182", {"start": v(6460, 1200) * mm, "end": v(4760, 1200) * mm});
            skLineSegment(sketch, "E561.183", {"start": v(9260, 1200) * mm, "end": v(7560, 1200) * mm});
            skLineSegment(sketch, "E561.184", {"start": v(1910, 1150) * mm, "end": v(1910, 3850) * mm});
            skLineSegment(sketch, "E561.185", {"start": v(7510, 1150) * mm, "end": v(7510, 3850) * mm});
            skLineSegment(sketch, "E561.186", {"start": v(4610, 3950) * mm, "end": v(4610, 1150) * mm});
            skLineSegment(sketch, "E561.187", {"start": v(7410, 3950) * mm, "end": v(7410, 1150) * mm});
            skLineSegment(sketch, "E561.188", {"start": v(1810, 3950) * mm, "end": v(1810, 1150) * mm});
            skLineSegment(sketch, "E561.189", {"start": v(9260, 3800) * mm, "end": v(9260, 1200) * mm});
            skLineSegment(sketch, "E561.190", {"start": v(7410, 3950) * mm, "end": v(9410, 3950) * mm});
            skLineSegment(sketch, "E561.191", {"start": v(6610, 3950) * mm, "end": v(6610, 1150) * mm});
            skLineSegment(sketch, "E561.192", {"start": v(9410, 3950) * mm, "end": v(9410, 1150) * mm});
            skLineSegment(sketch, "E561.193", {"start": v(3810, 3950) * mm, "end": v(3810, 1150) * mm});
            skLineSegment(sketch, "E561.194", {"start": v(1810, 3950) * mm, "end": v(3810, 3950) * mm});
            skLineSegment(sketch, "E561.195", {"start": v(4610, 3950) * mm, "end": v(6610, 3950) * mm});
            skLineSegment(sketch, "E561.196", {"start": v(4710, 1150) * mm, "end": v(4710, 3850) * mm});
            skLineSegment(sketch, "E561.197", {"start": v(4710, 1150) * mm, "end": v(4610, 1150) * mm});
            skLineSegment(sketch, "E561.198", {"start": v(7510, 1150) * mm, "end": v(7410, 1150) * mm});
            skLineSegment(sketch, "E561.199", {"start": v(1910, 1150) * mm, "end": v(1810, 1150) * mm});
            skLineSegment(sketch, "E561.200", {"start": v(3810, 1150) * mm, "end": v(3710, 1150) * mm});
            skLineSegment(sketch, "E561.201", {"start": v(6610, 1150) * mm, "end": v(6510, 1150) * mm});
            skLineSegment(sketch, "E561.202", {"start": v(9410, 1150) * mm, "end": v(9310, 1150) * mm});
            skLineSegment(sketch, "E561.203", {"start": v(28210, 1150) * mm, "end": v(18810, 1150) * mm});
            skSolve(sketch);
        }
        {
            var Q0;
            Q0 = qSketchRegion(id + "F58", true);
            extrude(context, id + "F59", {"entities" : qUnion([Q0]), "depth" : 50 * mm, "offsetDistance" : 25 * mm});
        }
        {
            var Q0;
            Q0=makeQuery(id+"F59.opExtrude","CAP_FACE",FACE,{"disambiguationData":[OSD([sQuery(id+"F58.wireOp",EDGE,"E561.152"),sQuery(id+"F58.wireOp",EDGE,"E561.162"),sQuery(id+"F58.wireOp",EDGE,"E561.165"),sQuery(id+"F58.wireOp",EDGE,"E561.176"),sQuery(id+"F58.wireOp",EDGE,"E561.177"),sQuery(id+"F58.wireOp",EDGE,"E561.180"),sQuery(id+"F58.wireOp",EDGE,"E561.181"),sQuery(id+"F58.wireOp",EDGE,"E561.188"),sQuery(id+"F58.wireOp",EDGE,"E561.194"),sQuery(id+"F58.wireOp",EDGE,"E561.199"),sQuery(id+"F58.wireOp",EDGE,"E561.200")])],"isStart":false});
            var sketch = newSketch(context, id + "F60", { "sketchPlane" : qUnion([Q0])});
            skLineSegment(sketch, "E562.0", {"start": v(37410, 3950) * mm, "end": v(37410, 1150) * mm});
            skLineSegment(sketch, "E562.1", {"start": v(35410, 1150) * mm, "end": v(35410, 3950) * mm});
            skLineSegment(sketch, "E562.2", {"start": v(35410, 3950) * mm, "end": v(37410, 3950) * mm});
            skLineSegment(sketch, "E562.3", {"start": v(37310, 3850) * mm, "end": v(37310, 1150) * mm});
            skLineSegment(sketch, "E562.4", {"start": v(35510, 3850) * mm, "end": v(37310, 3850) * mm});
            skLineSegment(sketch, "E562.5", {"start": v(35510, 1150) * mm, "end": v(35510, 3850) * mm});
            skLineSegment(sketch, "E562.6", {"start": v(37410, 1150) * mm, "end": v(37310, 1150) * mm});
            skLineSegment(sketch, "E562.7", {"start": v(35510, 1150) * mm, "end": v(35410, 1150) * mm});
            skLineSegment(sketch, "E562.8", {"start": v(35410, 1150) * mm, "end": v(37410, 1150) * mm});
            skLineSegment(sketch, "E562.9", {"start": v(37260, 3800) * mm, "end": v(35560, 3800) * mm});
            skLineSegment(sketch, "E562.10", {"start": v(35560, 3800) * mm, "end": v(35560, 1200) * mm});
            skLineSegment(sketch, "E562.11", {"start": v(37410, 3950) * mm, "end": v(37410, 1150) * mm});
            skLineSegment(sketch, "E562.12", {"start": v(35410, 3950) * mm, "end": v(35410, 1150) * mm});
            skLineSegment(sketch, "E562.13", {"start": v(35410, 3950) * mm, "end": v(37410, 3950) * mm});
            skLineSegment(sketch, "E562.14", {"start": v(37260, 1200) * mm, "end": v(35560, 1200) * mm});
            skLineSegment(sketch, "E562.15", {"start": v(37260, 3800) * mm, "end": v(37260, 1200) * mm});
            skPoint(sketch, "E562.16", {"position": v(35010, 1200) * mm});
            skPoint(sketch, "E562.17", {"position": v(32160, 1200) * mm});
            skPoint(sketch, "E562.18", {"position": v(28060, 1200) * mm});
            skPoint(sketch, "E562.19", {"position": v(25260, 1200) * mm});
            skPoint(sketch, "E562.20", {"position": v(22460, 1200) * mm});
            skLineSegment(sketch, "E562.21", {"start": v(35160, 3950) * mm, "end": v(35160, 1150) * mm});
            skLineSegment(sketch, "E562.22", {"start": v(33160, 1150) * mm, "end": v(33160, 3950) * mm});
            skLineSegment(sketch, "E562.23", {"start": v(33160, 3950) * mm, "end": v(35160, 3950) * mm});
            skLineSegment(sketch, "E562.24", {"start": v(35060, 3850) * mm, "end": v(35060, 1150) * mm});
            skLineSegment(sketch, "E562.25", {"start": v(33260, 3850) * mm, "end": v(35060, 3850) * mm});
            skLineSegment(sketch, "E562.26", {"start": v(33260, 1150) * mm, "end": v(33260, 3850) * mm});
            skLineSegment(sketch, "E562.27", {"start": v(35160, 1150) * mm, "end": v(35060, 1150) * mm});
            skLineSegment(sketch, "E562.28", {"start": v(33260, 1150) * mm, "end": v(33160, 1150) * mm});
            skLineSegment(sketch, "E562.29", {"start": v(33160, 1150) * mm, "end": v(35160, 1150) * mm});
            skLineSegment(sketch, "E562.30", {"start": v(35010, 3800) * mm, "end": v(33310, 3800) * mm});
            skLineSegment(sketch, "E562.31", {"start": v(33310, 3800) * mm, "end": v(33310, 1200) * mm});
            skLineSegment(sketch, "E562.32", {"start": v(35160, 3950) * mm, "end": v(35160, 1150) * mm});
            skLineSegment(sketch, "E562.33", {"start": v(33160, 3950) * mm, "end": v(33160, 1150) * mm});
            skLineSegment(sketch, "E562.34", {"start": v(33160, 3950) * mm, "end": v(35160, 3950) * mm});
            skLineSegment(sketch, "E562.35", {"start": v(35010, 1200) * mm, "end": v(33310, 1200) * mm});
            skLineSegment(sketch, "E562.36", {"start": v(35010, 3800) * mm, "end": v(35010, 1200) * mm});
            skLineSegment(sketch, "E562.37", {"start": v(32310, 3950) * mm, "end": v(32310, 1150) * mm});
            skLineSegment(sketch, "E562.38", {"start": v(30310, 1150) * mm, "end": v(30310, 3950) * mm});
            skLineSegment(sketch, "E562.39", {"start": v(30310, 3950) * mm, "end": v(32310, 3950) * mm});
            skLineSegment(sketch, "E562.40", {"start": v(32210, 3850) * mm, "end": v(32210, 1150) * mm});
            skLineSegment(sketch, "E562.41", {"start": v(30410, 3850) * mm, "end": v(32210, 3850) * mm});
            skLineSegment(sketch, "E562.42", {"start": v(30410, 1150) * mm, "end": v(30410, 3850) * mm});
            skLineSegment(sketch, "E562.43", {"start": v(32310, 1150) * mm, "end": v(32210, 1150) * mm});
            skLineSegment(sketch, "E562.44", {"start": v(30410, 1150) * mm, "end": v(30310, 1150) * mm});
            skLineSegment(sketch, "E562.45", {"start": v(30310, 1150) * mm, "end": v(32310, 1150) * mm});
            skLineSegment(sketch, "E562.46", {"start": v(32160, 3800) * mm, "end": v(30460, 3800) * mm});
            skLineSegment(sketch, "E562.47", {"start": v(30460, 3800) * mm, "end": v(30460, 1200) * mm});
            skLineSegment(sketch, "E562.48", {"start": v(32310, 3950) * mm, "end": v(32310, 1150) * mm});
            skLineSegment(sketch, "E562.49", {"start": v(30310, 3950) * mm, "end": v(30310, 1150) * mm});
            skLineSegment(sketch, "E562.50", {"start": v(30310, 3950) * mm, "end": v(32310, 3950) * mm});
            skLineSegment(sketch, "E562.51", {"start": v(32160, 1200) * mm, "end": v(30460, 1200) * mm});
            skLineSegment(sketch, "E562.52", {"start": v(32160, 3800) * mm, "end": v(32160, 1200) * mm});
            skLineSegment(sketch, "E562.53", {"start": v(28210, 3950) * mm, "end": v(28210, 1150) * mm});
            skLineSegment(sketch, "E562.54", {"start": v(26210, 1150) * mm, "end": v(26210, 3950) * mm});
            skLineSegment(sketch, "E562.55", {"start": v(26210, 3950) * mm, "end": v(28210, 3950) * mm});
            skLineSegment(sketch, "E562.56", {"start": v(28110, 3850) * mm, "end": v(28110, 1150) * mm});
            skLineSegment(sketch, "E562.57", {"start": v(26310, 3850) * mm, "end": v(28110, 3850) * mm});
            skLineSegment(sketch, "E562.58", {"start": v(26310, 1150) * mm, "end": v(26310, 3850) * mm});
            skLineSegment(sketch, "E562.59", {"start": v(28210, 1150) * mm, "end": v(28110, 1150) * mm});
            skLineSegment(sketch, "E562.60", {"start": v(26310, 1150) * mm, "end": v(26210, 1150) * mm});
            skLineSegment(sketch, "E562.61", {"start": v(26210, 1150) * mm, "end": v(28210, 1150) * mm});
            skLineSegment(sketch, "E562.62", {"start": v(28060, 3800) * mm, "end": v(26360, 3800) * mm});
            skLineSegment(sketch, "E562.63", {"start": v(26360, 3800) * mm, "end": v(26360, 1200) * mm});
            skLineSegment(sketch, "E562.64", {"start": v(28210, 3950) * mm, "end": v(28210, 1150) * mm});
            skLineSegment(sketch, "E562.65", {"start": v(26210, 3950) * mm, "end": v(26210, 1150) * mm});
            skLineSegment(sketch, "E562.66", {"start": v(26210, 3950) * mm, "end": v(28210, 3950) * mm});
            skLineSegment(sketch, "E562.67", {"start": v(28060, 1200) * mm, "end": v(26360, 1200) * mm});
            skLineSegment(sketch, "E562.68", {"start": v(28060, 3800) * mm, "end": v(28060, 1200) * mm});
            skLineSegment(sketch, "E562.69", {"start": v(25410, 3950) * mm, "end": v(25410, 1150) * mm});
            skLineSegment(sketch, "E562.70", {"start": v(23410, 1150) * mm, "end": v(23410, 3950) * mm});
            skLineSegment(sketch, "E562.71", {"start": v(23410, 3950) * mm, "end": v(25410, 3950) * mm});
            skLineSegment(sketch, "E562.72", {"start": v(25310, 3850) * mm, "end": v(25310, 1150) * mm});
            skLineSegment(sketch, "E562.73", {"start": v(23510, 3850) * mm, "end": v(25310, 3850) * mm});
            skLineSegment(sketch, "E562.74", {"start": v(23510, 1150) * mm, "end": v(23510, 3850) * mm});
            skLineSegment(sketch, "E562.75", {"start": v(25410, 1150) * mm, "end": v(25310, 1150) * mm});
            skLineSegment(sketch, "E562.76", {"start": v(23510, 1150) * mm, "end": v(23410, 1150) * mm});
            skLineSegment(sketch, "E562.77", {"start": v(23410, 1150) * mm, "end": v(25410, 1150) * mm});
            skLineSegment(sketch, "E562.78", {"start": v(25260, 3800) * mm, "end": v(23560, 3800) * mm});
            skLineSegment(sketch, "E562.79", {"start": v(23560, 3800) * mm, "end": v(23560, 1200) * mm});
            skLineSegment(sketch, "E562.80", {"start": v(25410, 3950) * mm, "end": v(25410, 1150) * mm});
            skLineSegment(sketch, "E562.81", {"start": v(23410, 3950) * mm, "end": v(23410, 1150) * mm});
            skLineSegment(sketch, "E562.82", {"start": v(23410, 3950) * mm, "end": v(25410, 3950) * mm});
            skLineSegment(sketch, "E562.83", {"start": v(25260, 1200) * mm, "end": v(23560, 1200) * mm});
            skLineSegment(sketch, "E562.84", {"start": v(25260, 3800) * mm, "end": v(25260, 1200) * mm});
            skLineSegment(sketch, "E562.85", {"start": v(22610, 3950) * mm, "end": v(22610, 1150) * mm});
            skLineSegment(sketch, "E562.86", {"start": v(20610, 1150) * mm, "end": v(20610, 3950) * mm});
            skLineSegment(sketch, "E562.87", {"start": v(20610, 3950) * mm, "end": v(22610, 3950) * mm});
            skLineSegment(sketch, "E562.88", {"start": v(22510, 3850) * mm, "end": v(22510, 1150) * mm});
            skLineSegment(sketch, "E562.89", {"start": v(20710, 3850) * mm, "end": v(22510, 3850) * mm});
            skLineSegment(sketch, "E562.90", {"start": v(20710, 1150) * mm, "end": v(20710, 3850) * mm});
            skLineSegment(sketch, "E562.91", {"start": v(22610, 1150) * mm, "end": v(22510, 1150) * mm});
            skLineSegment(sketch, "E562.92", {"start": v(20710, 1150) * mm, "end": v(20610, 1150) * mm});
            skLineSegment(sketch, "E562.93", {"start": v(20610, 1150) * mm, "end": v(22610, 1150) * mm});
            skLineSegment(sketch, "E562.94", {"start": v(22460, 3800) * mm, "end": v(20760, 3800) * mm});
            skLineSegment(sketch, "E562.95", {"start": v(20760, 3800) * mm, "end": v(20760, 1200) * mm});
            skLineSegment(sketch, "E562.96", {"start": v(22610, 3950) * mm, "end": v(22610, 1150) * mm});
            skLineSegment(sketch, "E562.97", {"start": v(20610, 3950) * mm, "end": v(20610, 1150) * mm});
            skLineSegment(sketch, "E562.98", {"start": v(20610, 3950) * mm, "end": v(22610, 3950) * mm});
            skLineSegment(sketch, "E562.99", {"start": v(22460, 1200) * mm, "end": v(20760, 1200) * mm});
            skLineSegment(sketch, "E562.100", {"start": v(22460, 3800) * mm, "end": v(22460, 1200) * mm});
            skLineSegment(sketch, "E562.101", {"start": v(11360, 3800) * mm, "end": v(11360, 1200) * mm});
            skLineSegment(sketch, "E562.102", {"start": v(14160, 3800) * mm, "end": v(14160, 1200) * mm});
            skLineSegment(sketch, "E562.103", {"start": v(16810, 1150) * mm, "end": v(16810, 3950) * mm});
            skLineSegment(sketch, "E562.104", {"start": v(18660, 3800) * mm, "end": v(16960, 3800) * mm});
            skLineSegment(sketch, "E562.105", {"start": v(18810, 3950) * mm, "end": v(18810, 1150) * mm});
            skLineSegment(sketch, "E562.106", {"start": v(16010, 3950) * mm, "end": v(16010, 1150) * mm});
            skLineSegment(sketch, "E562.107", {"start": v(16960, 3800) * mm, "end": v(16960, 1200) * mm});
            skLineSegment(sketch, "E562.108", {"start": v(14110, 3850) * mm, "end": v(15910, 3850) * mm});
            skPoint(sketch, "E562.109", {"position": v(15860, 1200) * mm});
            skLineSegment(sketch, "E562.110", {"start": v(16910, 3850) * mm, "end": v(18710, 3850) * mm});
            skLineSegment(sketch, "E562.111", {"start": v(13060, 3800) * mm, "end": v(11360, 3800) * mm});
            skLineSegment(sketch, "E562.112", {"start": v(15860, 3800) * mm, "end": v(14160, 3800) * mm});
            skPoint(sketch, "E562.113", {"position": v(18660, 1200) * mm});
            skLineSegment(sketch, "E562.114", {"start": v(13060, 3800) * mm, "end": v(13060, 1200) * mm});
            skLineSegment(sketch, "E562.115", {"start": v(15860, 3800) * mm, "end": v(15860, 1200) * mm});
            skPoint(sketch, "E562.116", {"position": v(13060, 1200) * mm});
            skLineSegment(sketch, "E562.117", {"start": v(13110, 3850) * mm, "end": v(13110, 1150) * mm});
            skLineSegment(sketch, "E562.118", {"start": v(14010, 1150) * mm, "end": v(14010, 3950) * mm});
            skLineSegment(sketch, "E562.119", {"start": v(18710, 3850) * mm, "end": v(18710, 1150) * mm});
            skLineSegment(sketch, "E562.120", {"start": v(15910, 3850) * mm, "end": v(15910, 1150) * mm});
            skLineSegment(sketch, "E562.121", {"start": v(11310, 3850) * mm, "end": v(13110, 3850) * mm});
            skLineSegment(sketch, "E562.122", {"start": v(11210, 1150) * mm, "end": v(11210, 3950) * mm});
            skLineSegment(sketch, "E562.123", {"start": v(14010, 1150) * mm, "end": v(16010, 1150) * mm});
            skLineSegment(sketch, "E562.124", {"start": v(16810, 1150) * mm, "end": v(18810, 1150) * mm});
            skLineSegment(sketch, "E562.125", {"start": v(11210, 1150) * mm, "end": v(13210, 1150) * mm});
            skLineSegment(sketch, "E562.126", {"start": v(11210, 3950) * mm, "end": v(13210, 3950) * mm});
            skLineSegment(sketch, "E562.127", {"start": v(14010, 3950) * mm, "end": v(16010, 3950) * mm});
            skLineSegment(sketch, "E562.128", {"start": v(16810, 3950) * mm, "end": v(18810, 3950) * mm});
            skLineSegment(sketch, "E562.129", {"start": v(13210, 3950) * mm, "end": v(13210, 1150) * mm});
            skLineSegment(sketch, "E562.130", {"start": v(13060, 1200) * mm, "end": v(11360, 1200) * mm});
            skLineSegment(sketch, "E562.131", {"start": v(15860, 1200) * mm, "end": v(14160, 1200) * mm});
            skLineSegment(sketch, "E562.132", {"start": v(18660, 1200) * mm, "end": v(16960, 1200) * mm});
            skLineSegment(sketch, "E562.133", {"start": v(11310, 1150) * mm, "end": v(11310, 3850) * mm});
            skLineSegment(sketch, "E562.134", {"start": v(16910, 1150) * mm, "end": v(16910, 3850) * mm});
            skLineSegment(sketch, "E562.135", {"start": v(14010, 3950) * mm, "end": v(14010, 1150) * mm});
            skLineSegment(sketch, "E562.136", {"start": v(16810, 3950) * mm, "end": v(16810, 1150) * mm});
            skLineSegment(sketch, "E562.137", {"start": v(11210, 3950) * mm, "end": v(11210, 1150) * mm});
            skLineSegment(sketch, "E562.138", {"start": v(18660, 3800) * mm, "end": v(18660, 1200) * mm});
            skLineSegment(sketch, "E562.139", {"start": v(16810, 3950) * mm, "end": v(18810, 3950) * mm});
            skLineSegment(sketch, "E562.140", {"start": v(16010, 3950) * mm, "end": v(16010, 1150) * mm});
            skLineSegment(sketch, "E562.141", {"start": v(18810, 3950) * mm, "end": v(18810, 1150) * mm});
            skLineSegment(sketch, "E562.142", {"start": v(13210, 3950) * mm, "end": v(13210, 1150) * mm});
            skLineSegment(sketch, "E562.143", {"start": v(11210, 3950) * mm, "end": v(13210, 3950) * mm});
            skLineSegment(sketch, "E562.144", {"start": v(14010, 3950) * mm, "end": v(16010, 3950) * mm});
            skLineSegment(sketch, "E562.145", {"start": v(14110, 1150) * mm, "end": v(14110, 3850) * mm});
            skLineSegment(sketch, "E562.146", {"start": v(14110, 1150) * mm, "end": v(14010, 1150) * mm});
            skLineSegment(sketch, "E562.147", {"start": v(16910, 1150) * mm, "end": v(16810, 1150) * mm});
            skLineSegment(sketch, "E562.148", {"start": v(11310, 1150) * mm, "end": v(11210, 1150) * mm});
            skLineSegment(sketch, "E562.149", {"start": v(13210, 1150) * mm, "end": v(13110, 1150) * mm});
            skLineSegment(sketch, "E562.150", {"start": v(16010, 1150) * mm, "end": v(15910, 1150) * mm});
            skLineSegment(sketch, "E562.151", {"start": v(18810, 1150) * mm, "end": v(18710, 1150) * mm});
            skLineSegment(sketch, "E562.152", {"start": v(1960, 3800) * mm, "end": v(1960, 1200) * mm});
            skLineSegment(sketch, "E562.153", {"start": v(4760, 3800) * mm, "end": v(4760, 1200) * mm});
            skLineSegment(sketch, "E562.154", {"start": v(7410, 1150) * mm, "end": v(7410, 3950) * mm});
            skLineSegment(sketch, "E562.155", {"start": v(9260, 3800) * mm, "end": v(7560, 3800) * mm});
            skLineSegment(sketch, "E562.156", {"start": v(9410, 3950) * mm, "end": v(9410, 1150) * mm});
            skLineSegment(sketch, "E562.157", {"start": v(6610, 3950) * mm, "end": v(6610, 1150) * mm});
            skLineSegment(sketch, "E562.158", {"start": v(7560, 3800) * mm, "end": v(7560, 1200) * mm});
            skLineSegment(sketch, "E562.159", {"start": v(4710, 3850) * mm, "end": v(6510, 3850) * mm});
            skPoint(sketch, "E562.160", {"position": v(6460, 1200) * mm});
            skLineSegment(sketch, "E562.161", {"start": v(7510, 3850) * mm, "end": v(9310, 3850) * mm});
            skLineSegment(sketch, "E562.162", {"start": v(3660, 3800) * mm, "end": v(1960, 3800) * mm});
            skLineSegment(sketch, "E562.163", {"start": v(6460, 3800) * mm, "end": v(4760, 3800) * mm});
            skPoint(sketch, "E562.164", {"position": v(9260, 1200) * mm});
            skLineSegment(sketch, "E562.165", {"start": v(3660, 3800) * mm, "end": v(3660, 1200) * mm});
            skLineSegment(sketch, "E562.166", {"start": v(6460, 3800) * mm, "end": v(6460, 1200) * mm});
            skPoint(sketch, "E562.167", {"position": v(3660, 1200) * mm});
            skLineSegment(sketch, "E562.168", {"start": v(3710, 3850) * mm, "end": v(3710, 1150) * mm});
            skLineSegment(sketch, "E562.169", {"start": v(4610, 1150) * mm, "end": v(4610, 3950) * mm});
            skLineSegment(sketch, "E562.170", {"start": v(9310, 3850) * mm, "end": v(9310, 1150) * mm});
            skLineSegment(sketch, "E562.171", {"start": v(6510, 3850) * mm, "end": v(6510, 1150) * mm});
            skLineSegment(sketch, "E562.172", {"start": v(1910, 3850) * mm, "end": v(3710, 3850) * mm});
            skLineSegment(sketch, "E562.173", {"start": v(1810, 1150) * mm, "end": v(1810, 3950) * mm});
            skLineSegment(sketch, "E562.174", {"start": v(4610, 1150) * mm, "end": v(6610, 1150) * mm});
            skLineSegment(sketch, "E562.175", {"start": v(7410, 1150) * mm, "end": v(9410, 1150) * mm});
            skLineSegment(sketch, "E562.176", {"start": v(1810, 1150) * mm, "end": v(3810, 1150) * mm});
            skLineSegment(sketch, "E562.177", {"start": v(1810, 3950) * mm, "end": v(3810, 3950) * mm});
            skLineSegment(sketch, "E562.178", {"start": v(4610, 3950) * mm, "end": v(6610, 3950) * mm});
            skLineSegment(sketch, "E562.179", {"start": v(7410, 3950) * mm, "end": v(9410, 3950) * mm});
            skLineSegment(sketch, "E562.180", {"start": v(3810, 3950) * mm, "end": v(3810, 1150) * mm});
            skLineSegment(sketch, "E562.181", {"start": v(3660, 1200) * mm, "end": v(1960, 1200) * mm});
            skLineSegment(sketch, "E562.182", {"start": v(6460, 1200) * mm, "end": v(4760, 1200) * mm});
            skLineSegment(sketch, "E562.183", {"start": v(9260, 1200) * mm, "end": v(7560, 1200) * mm});
            skLineSegment(sketch, "E562.184", {"start": v(1910, 1150) * mm, "end": v(1910, 3850) * mm});
            skLineSegment(sketch, "E562.185", {"start": v(7510, 1150) * mm, "end": v(7510, 3850) * mm});
            skLineSegment(sketch, "E562.186", {"start": v(4610, 3950) * mm, "end": v(4610, 1150) * mm});
            skLineSegment(sketch, "E562.187", {"start": v(7410, 3950) * mm, "end": v(7410, 1150) * mm});
            skLineSegment(sketch, "E562.188", {"start": v(1810, 3950) * mm, "end": v(1810, 1150) * mm});
            skLineSegment(sketch, "E562.189", {"start": v(9260, 3800) * mm, "end": v(9260, 1200) * mm});
            skLineSegment(sketch, "E562.190", {"start": v(7410, 3950) * mm, "end": v(9410, 3950) * mm});
            skLineSegment(sketch, "E562.191", {"start": v(6610, 3950) * mm, "end": v(6610, 1150) * mm});
            skLineSegment(sketch, "E562.192", {"start": v(9410, 3950) * mm, "end": v(9410, 1150) * mm});
            skLineSegment(sketch, "E562.193", {"start": v(3810, 3950) * mm, "end": v(3810, 1150) * mm});
            skLineSegment(sketch, "E562.194", {"start": v(1810, 3950) * mm, "end": v(3810, 3950) * mm});
            skLineSegment(sketch, "E562.195", {"start": v(4610, 3950) * mm, "end": v(6610, 3950) * mm});
            skLineSegment(sketch, "E562.196", {"start": v(4710, 1150) * mm, "end": v(4710, 3850) * mm});
            skLineSegment(sketch, "E562.197", {"start": v(4710, 1150) * mm, "end": v(4610, 1150) * mm});
            skLineSegment(sketch, "E562.198", {"start": v(7510, 1150) * mm, "end": v(7410, 1150) * mm});
            skLineSegment(sketch, "E562.199", {"start": v(1910, 1150) * mm, "end": v(1810, 1150) * mm});
            skLineSegment(sketch, "E562.200", {"start": v(3810, 1150) * mm, "end": v(3710, 1150) * mm});
            skLineSegment(sketch, "E562.201", {"start": v(6610, 1150) * mm, "end": v(6510, 1150) * mm});
            skLineSegment(sketch, "E562.202", {"start": v(9410, 1150) * mm, "end": v(9310, 1150) * mm});
            skLineSegment(sketch, "E562.203", {"start": v(28210, 1150) * mm, "end": v(18810, 1150) * mm});
            skSolve(sketch);
        }
        {
            var Q0;
            {var subQ2=sQuery(id+"F60.wireOp",EDGE,"E562.168");Q0=makeQuery(id+"F60.imprint","IMPRINT",FACE,{"disambiguationData":[TD([[makeQuery(id+"F60.imprint","IMPRINT",EDGE,{"derivedFrom":subQ2}),1.0]])]});}
            var Q1;
            Q1=makeQuery(id+"F60.imprint","IMPRINT",FACE,{"disambiguationData":[TD([[makeQuery(id+"F60.imprint","IMPRINT",EDGE,{"derivedFrom":sQuery(id+"F60.wireOp",EDGE,"E562.159")}),1.0]])]});
            var Q2;
            {var subQ2=sQuery(id+"F60.wireOp",EDGE,"E562.154");Q2=makeQuery(id+"F60.imprint","IMPRINT",FACE,{"disambiguationData":[TD([[makeQuery(id+"F60.imprint","IMPRINT",EDGE,{"derivedFrom":subQ2}),-1.0]])]});}
            var Q3;
            {var subQ1=sQuery(id+"F60.wireOp",EDGE,"E562.117");Q3=makeQuery(id+"F60.imprint","IMPRINT",FACE,{"disambiguationData":[TD([[makeQuery(id+"F60.imprint","IMPRINT",EDGE,{"derivedFrom":subQ1}),1.0]])]});}
            var Q4;
            Q4=makeQuery(id+"F60.imprint","IMPRINT",FACE,{"disambiguationData":[TD([[makeQuery(id+"F60.imprint","IMPRINT",EDGE,{"derivedFrom":sQuery(id+"F60.wireOp",EDGE,"E562.108")}),1.0]])]});
            var Q5;
            {var subQ2=sQuery(id+"F60.wireOp",EDGE,"E562.103");Q5=makeQuery(id+"F60.imprint","IMPRINT",FACE,{"disambiguationData":[TD([[makeQuery(id+"F60.imprint","IMPRINT",EDGE,{"derivedFrom":subQ2}),-1.0]])]});}
            var Q6;
            {var subQ2=sQuery(id+"F60.wireOp",EDGE,"E562.86");Q6=makeQuery(id+"F60.imprint","IMPRINT",FACE,{"disambiguationData":[TD([[makeQuery(id+"F60.imprint","IMPRINT",EDGE,{"derivedFrom":subQ2}),-1.0]])]});}
            var Q7;
            {var subQ4=sQuery(id+"F60.wireOp",EDGE,"E562.70");Q7=makeQuery(id+"F60.imprint","IMPRINT",FACE,{"disambiguationData":[TD([[makeQuery(id+"F60.imprint","IMPRINT",EDGE,{"derivedFrom":subQ4}),-1.0]])]});}
            var Q8;
            {var subQ2=sQuery(id+"F60.wireOp",EDGE,"E562.54");Q8=makeQuery(id+"F60.imprint","IMPRINT",FACE,{"disambiguationData":[TD([[makeQuery(id+"F60.imprint","IMPRINT",EDGE,{"derivedFrom":subQ2}),-1.0]])]});}
            var Q9;
            {var subQ2=sQuery(id+"F60.wireOp",EDGE,"E562.38");Q9=makeQuery(id+"F60.imprint","IMPRINT",FACE,{"disambiguationData":[TD([[makeQuery(id+"F60.imprint","IMPRINT",EDGE,{"derivedFrom":subQ2}),-1.0]])]});}
            var Q10;
            {var subQ2=sQuery(id+"F60.wireOp",EDGE,"E562.22");Q10=makeQuery(id+"F60.imprint","IMPRINT",FACE,{"disambiguationData":[TD([[makeQuery(id+"F60.imprint","IMPRINT",EDGE,{"derivedFrom":subQ2}),-1.0]])]});}
            var Q11;
            {var subQ2=sQuery(id+"F60.wireOp",EDGE,"E562.1");Q11=makeQuery(id+"F60.imprint","IMPRINT",FACE,{"disambiguationData":[TD([[makeQuery(id+"F60.imprint","IMPRINT",EDGE,{"derivedFrom":subQ2}),-1.0]])]});}
            extrude(context, id + "F61", {"entities" : qUnion([Q0, Q1, Q2, Q3, Q4, Q5, Q6, Q7, Q8, Q9, Q10, Q11]), "operationType" : NewBodyOperationType.ADD, "depth" : 25 * mm, "offsetDistance" : 25 * mm});
        }
        {
            var Q0;
            Q0=makeQuery(id+"F5.boolean.opBoolean","MERGE",FACE,{"derivedFrom":[makeQuery(id+"F3.boolean.opBoolean","COPY",FACE,{"derivedFrom":makeQuery(id+"F3.opExtrude","SWEPT_FACE",FACE,{"disambiguationData":[OSD([sQuery(id+"F2.wireOp",EDGE,"E19.9")])]})}),makeQuery(id+"F5.opExtrude","SWEPT_FACE",FACE,{"disambiguationData":[OSD([sQuery(id+"F4.wireOp",EDGE,"E34.0")])]})]});
            var sketch = newSketch(context, id + "F62", { "sketchPlane" : qUnion([Q0])});
            skLineSegment(sketch, "E563.152", {"start": v(1480, 3800) * mm, "end": v(1480, 1200) * mm});
            skLineSegment(sketch, "E563.162", {"start": v(3180, 3800) * mm, "end": v(1480, 3800) * mm});
            skLineSegment(sketch, "E563.165", {"start": v(3180, 3800) * mm, "end": v(3180, 1200) * mm});
            skPoint(sketch, "E563.167", {"position": v(3180, 1200) * mm});
            skLineSegment(sketch, "E563.168", {"start": v(3230, 3850) * mm, "end": v(3230, 1150) * mm});
            skLineSegment(sketch, "E563.172", {"start": v(1430, 3850) * mm, "end": v(3230, 3850) * mm});
            skLineSegment(sketch, "E563.173", {"start": v(1330, 1150) * mm, "end": v(1330, 3950) * mm});
            skLineSegment(sketch, "E563.176", {"start": v(1330, 1150) * mm, "end": v(3330, 1150) * mm});
            skLineSegment(sketch, "E563.177", {"start": v(1330, 3950) * mm, "end": v(3330, 3950) * mm});
            skLineSegment(sketch, "E563.180", {"start": v(3330, 3950) * mm, "end": v(3330, 1150) * mm});
            skLineSegment(sketch, "E563.181", {"start": v(3180, 1200) * mm, "end": v(1480, 1200) * mm});
            skLineSegment(sketch, "E563.184", {"start": v(1430, 1150) * mm, "end": v(1430, 3850) * mm});
            skLineSegment(sketch, "E563.188", {"start": v(1330, 3950) * mm, "end": v(1330, 1150) * mm});
            skLineSegment(sketch, "E563.193", {"start": v(3330, 3950) * mm, "end": v(3330, 1150) * mm});
            skLineSegment(sketch, "E563.194", {"start": v(1330, 3950) * mm, "end": v(3330, 3950) * mm});
            skLineSegment(sketch, "E563.199", {"start": v(1430, 1150) * mm, "end": v(1330, 1150) * mm});
            skLineSegment(sketch, "E563.200", {"start": v(3330, 1150) * mm, "end": v(3230, 1150) * mm});
            skPoint(sketch, "E564", {"position": v(1480, 1200) * mm});
            skLineSegment(sketch, "E565.bottom", {"start": v(5650, 3350) * mm, "end": v(7050, 3350) * mm});
            skLineSegment(sketch, "E565.top", {"start": v(5650, 1050) * mm, "end": v(7050, 1050) * mm});
            skLineSegment(sketch, "E565.left", {"start": v(5650, 3350) * mm, "end": v(5650, 1050) * mm});
            skLineSegment(sketch, "E565.right", {"start": v(7050, 3350) * mm, "end": v(7050, 1050) * mm});
            skLineSegment(sketch, "E566", {"start": v(5750, 1050) * mm, "end": v(5750, 3250) * mm});
            skLineSegment(sketch, "E567", {"start": v(5750, 3250) * mm, "end": v(6950, 3250) * mm});
            skLineSegment(sketch, "E568", {"start": v(6950, 3250) * mm, "end": v(6950, 1050) * mm});
            skPoint(sketch, "E569", {"position": v(11330, 1100) * mm});
            skPoint(sketch, "E570", {"position": v(15560, 1100) * mm});
            skPoint(sketch, "E571", {"position": v(19560, 1100) * mm});
            skPoint(sketch, "E572", {"position": v(23730, 1100) * mm});
            skLineSegment(sketch, "E573.0", {"start": v(6900, 3200) * mm, "end": v(6900, 1100) * mm});
            skLineSegment(sketch, "E574.0", {"start": v(6900, 3200) * mm, "end": v(5800, 3200) * mm});
            skLineSegment(sketch, "E575.0", {"start": v(5800, 3200) * mm, "end": v(5800, 1100) * mm});
            skLineSegment(sketch, "E576.0", {"start": v(6900, 1100) * mm, "end": v(5800, 1100) * mm});
            skLineSegment(sketch, "E577.bottom", {"start": v(11180, 3350) * mm, "end": v(12580, 3350) * mm});
            skLineSegment(sketch, "E577.top", {"start": v(11180, 1050) * mm, "end": v(12580, 1050) * mm});
            skLineSegment(sketch, "E577.left", {"start": v(11180, 3350) * mm, "end": v(11180, 1050) * mm});
            skLineSegment(sketch, "E577.right", {"start": v(12580, 3350) * mm, "end": v(12580, 1050) * mm});
            skLineSegment(sketch, "E578", {"start": v(11280, 1050) * mm, "end": v(11280, 3250) * mm});
            skLineSegment(sketch, "E579", {"start": v(11280, 3250) * mm, "end": v(12480, 3250) * mm});
            skLineSegment(sketch, "E580", {"start": v(12480, 3250) * mm, "end": v(12480, 1050) * mm});
            skLineSegment(sketch, "E581.0", {"start": v(12430, 3200) * mm, "end": v(12430, 1100) * mm});
            skLineSegment(sketch, "E582.0", {"start": v(12430, 3200) * mm, "end": v(11330, 3200) * mm});
            skLineSegment(sketch, "E583.0", {"start": v(11330, 3200) * mm, "end": v(11330, 1100) * mm});
            skLineSegment(sketch, "E584.0", {"start": v(12430, 1100) * mm, "end": v(11330, 1100) * mm});
            skLineSegment(sketch, "E585.bottom", {"start": v(15410, 3350) * mm, "end": v(16810, 3350) * mm});
            skLineSegment(sketch, "E585.top", {"start": v(15410, 1050) * mm, "end": v(16810, 1050) * mm});
            skLineSegment(sketch, "E585.left", {"start": v(15410, 3350) * mm, "end": v(15410, 1050) * mm});
            skLineSegment(sketch, "E585.right", {"start": v(16810, 3350) * mm, "end": v(16810, 1050) * mm});
            skLineSegment(sketch, "E586", {"start": v(15510, 1050) * mm, "end": v(15510, 3250) * mm});
            skLineSegment(sketch, "E587", {"start": v(15510, 3250) * mm, "end": v(16710, 3250) * mm});
            skLineSegment(sketch, "E588", {"start": v(16710, 3250) * mm, "end": v(16710, 1050) * mm});
            skLineSegment(sketch, "E589.0", {"start": v(16660, 3200) * mm, "end": v(16660, 1100) * mm});
            skLineSegment(sketch, "E590.0", {"start": v(16660, 3200) * mm, "end": v(15560, 3200) * mm});
            skLineSegment(sketch, "E591.0", {"start": v(15560, 3200) * mm, "end": v(15560, 1100) * mm});
            skLineSegment(sketch, "E592.0", {"start": v(16660, 1100) * mm, "end": v(15560, 1100) * mm});
            skLineSegment(sketch, "E593.bottom", {"start": v(19410, 3350) * mm, "end": v(20810, 3350) * mm});
            skLineSegment(sketch, "E593.top", {"start": v(19410, 1050) * mm, "end": v(20810, 1050) * mm});
            skLineSegment(sketch, "E593.left", {"start": v(19410, 3350) * mm, "end": v(19410, 1050) * mm});
            skLineSegment(sketch, "E593.right", {"start": v(20810, 3350) * mm, "end": v(20810, 1050) * mm});
            skLineSegment(sketch, "E594", {"start": v(19510, 1050) * mm, "end": v(19510, 3250) * mm});
            skLineSegment(sketch, "E595", {"start": v(19510, 3250) * mm, "end": v(20710, 3250) * mm});
            skLineSegment(sketch, "E596", {"start": v(20710, 3250) * mm, "end": v(20710, 1050) * mm});
            skLineSegment(sketch, "E597.0", {"start": v(20660, 3200) * mm, "end": v(20660, 1100) * mm});
            skLineSegment(sketch, "E598.0", {"start": v(20660, 3200) * mm, "end": v(19560, 3200) * mm});
            skLineSegment(sketch, "E599.0", {"start": v(19560, 3200) * mm, "end": v(19560, 1100) * mm});
            skLineSegment(sketch, "E600.0", {"start": v(20660, 1100) * mm, "end": v(19560, 1100) * mm});
            skLineSegment(sketch, "E601.bottom", {"start": v(23580, 3350) * mm, "end": v(24980, 3350) * mm});
            skLineSegment(sketch, "E601.top", {"start": v(23580, 1050) * mm, "end": v(24980, 1050) * mm});
            skLineSegment(sketch, "E601.left", {"start": v(23580, 3350) * mm, "end": v(23580, 1050) * mm});
            skLineSegment(sketch, "E601.right", {"start": v(24980, 3350) * mm, "end": v(24980, 1050) * mm});
            skLineSegment(sketch, "E602", {"start": v(23680, 1050) * mm, "end": v(23680, 3250) * mm});
            skLineSegment(sketch, "E603", {"start": v(23680, 3250) * mm, "end": v(24880, 3250) * mm});
            skLineSegment(sketch, "E604", {"start": v(24880, 3250) * mm, "end": v(24880, 1050) * mm});
            skLineSegment(sketch, "E605.0", {"start": v(24830, 3200) * mm, "end": v(24830, 1100) * mm});
            skLineSegment(sketch, "E606.0", {"start": v(24830, 3200) * mm, "end": v(23730, 3200) * mm});
            skLineSegment(sketch, "E607.0", {"start": v(23730, 3200) * mm, "end": v(23730, 1100) * mm});
            skLineSegment(sketch, "E608.0", {"start": v(24830, 1100) * mm, "end": v(23730, 1100) * mm});
            skLineSegment(sketch, "E609.0.0", {"start": v(27160, 0) * mm, "end": v(28260, 0) * mm});
            skLineSegment(sketch, "E609.0.1", {"start": v(28260, 0) * mm, "end": v(28260, 2400) * mm});
            skLineSegment(sketch, "E609.0.2", {"start": v(28260, 2400) * mm, "end": v(27160, 2400) * mm});
            skLineSegment(sketch, "E609.0.3", {"start": v(27160, 2400) * mm, "end": v(27160, 0) * mm});
            skLineSegment(sketch, "E610.bottom", {"start": v(27010, 2550) * mm, "end": v(28410, 2550) * mm});
            skLineSegment(sketch, "E610.left", {"start": v(27010, 2550) * mm, "end": v(27010, -150) * mm});
            skLineSegment(sketch, "E610.right", {"start": v(28410, 2550) * mm, "end": v(28410, -150) * mm});
            skLineSegment(sketch, "E611", {"start": v(27110, -150) * mm, "end": v(27110, 2450) * mm});
            skLineSegment(sketch, "E612", {"start": v(27110, 2450) * mm, "end": v(28310, 2450) * mm});
            skLineSegment(sketch, "E613", {"start": v(28310, 2450) * mm, "end": v(28310, -150) * mm});
            skLineSegment(sketch, "E614", {"start": v(27010, -150) * mm, "end": v(28410, -150) * mm});
            skSolve(sketch);
        }
        {
            var Q0;
            Q0 = qSketchRegion(id + "F62", true);
            extrude(context, id + "F63", {"entities" : qUnion([Q0]), "depth" : 50 * mm, "offsetDistance" : 25 * mm});
        }
        {
            var Q0;
            Q0=makeQuery(id+"F63.opExtrude","CAP_FACE",FACE,{"disambiguationData":[OSD([sQuery(id+"F62.wireOp",EDGE,"E563.152"),sQuery(id+"F62.wireOp",EDGE,"E563.162"),sQuery(id+"F62.wireOp",EDGE,"E563.165"),sQuery(id+"F62.wireOp",EDGE,"E563.176"),sQuery(id+"F62.wireOp",EDGE,"E563.177"),sQuery(id+"F62.wireOp",EDGE,"E563.180"),sQuery(id+"F62.wireOp",EDGE,"E563.181"),sQuery(id+"F62.wireOp",EDGE,"E563.188"),sQuery(id+"F62.wireOp",EDGE,"E563.194"),sQuery(id+"F62.wireOp",EDGE,"E563.199"),sQuery(id+"F62.wireOp",EDGE,"E563.200")])],"isStart":false});
            var sketch = newSketch(context, id + "F64", { "sketchPlane" : qUnion([Q0])});
            skLineSegment(sketch, "E615.0", {"start": v(1480, 3800) * mm, "end": v(1480, 1200) * mm});
            skLineSegment(sketch, "E615.1", {"start": v(3180, 3800) * mm, "end": v(1480, 3800) * mm});
            skLineSegment(sketch, "E615.2", {"start": v(3180, 3800) * mm, "end": v(3180, 1200) * mm});
            skPoint(sketch, "E615.3", {"position": v(3180, 1200) * mm});
            skLineSegment(sketch, "E615.4", {"start": v(3230, 3850) * mm, "end": v(3230, 1150) * mm});
            skLineSegment(sketch, "E615.5", {"start": v(1430, 3850) * mm, "end": v(3230, 3850) * mm});
            skLineSegment(sketch, "E615.6", {"start": v(1330, 1150) * mm, "end": v(1330, 3950) * mm});
            skLineSegment(sketch, "E615.7", {"start": v(1330, 1150) * mm, "end": v(3330, 1150) * mm});
            skLineSegment(sketch, "E615.8", {"start": v(1330, 3950) * mm, "end": v(3330, 3950) * mm});
            skLineSegment(sketch, "E615.9", {"start": v(3330, 3950) * mm, "end": v(3330, 1150) * mm});
            skLineSegment(sketch, "E615.10", {"start": v(3180, 1200) * mm, "end": v(1480, 1200) * mm});
            skLineSegment(sketch, "E615.11", {"start": v(1430, 1150) * mm, "end": v(1430, 3850) * mm});
            skLineSegment(sketch, "E615.12", {"start": v(1330, 3950) * mm, "end": v(1330, 1150) * mm});
            skLineSegment(sketch, "E615.13", {"start": v(3330, 3950) * mm, "end": v(3330, 1150) * mm});
            skLineSegment(sketch, "E615.14", {"start": v(1330, 3950) * mm, "end": v(3330, 3950) * mm});
            skLineSegment(sketch, "E615.15", {"start": v(1430, 1150) * mm, "end": v(1330, 1150) * mm});
            skLineSegment(sketch, "E615.16", {"start": v(3330, 1150) * mm, "end": v(3230, 1150) * mm});
            skPoint(sketch, "E615.17", {"position": v(1480, 1200) * mm});
            skLineSegment(sketch, "E615.18", {"start": v(5650, 3350) * mm, "end": v(7050, 3350) * mm});
            skLineSegment(sketch, "E615.19", {"start": v(5650, 1050) * mm, "end": v(7050, 1050) * mm});
            skLineSegment(sketch, "E615.20", {"start": v(5650, 3350) * mm, "end": v(5650, 1050) * mm});
            skLineSegment(sketch, "E615.21", {"start": v(7050, 3350) * mm, "end": v(7050, 1050) * mm});
            skLineSegment(sketch, "E615.22", {"start": v(5750, 1050) * mm, "end": v(5750, 3250) * mm});
            skLineSegment(sketch, "E615.23", {"start": v(5750, 3250) * mm, "end": v(6950, 3250) * mm});
            skLineSegment(sketch, "E615.24", {"start": v(6950, 3250) * mm, "end": v(6950, 1050) * mm});
            skPoint(sketch, "E615.25", {"position": v(11330, 1100) * mm});
            skPoint(sketch, "E615.26", {"position": v(15560, 1100) * mm});
            skPoint(sketch, "E615.27", {"position": v(19560, 1100) * mm});
            skPoint(sketch, "E615.28", {"position": v(23730, 1100) * mm});
            skLineSegment(sketch, "E615.29", {"start": v(6900, 3200) * mm, "end": v(6900, 1100) * mm});
            skLineSegment(sketch, "E615.30", {"start": v(6900, 3200) * mm, "end": v(5800, 3200) * mm});
            skLineSegment(sketch, "E615.31", {"start": v(5800, 3200) * mm, "end": v(5800, 1100) * mm});
            skLineSegment(sketch, "E615.32", {"start": v(6900, 1100) * mm, "end": v(5800, 1100) * mm});
            skLineSegment(sketch, "E615.33", {"start": v(11180, 3350) * mm, "end": v(12580, 3350) * mm});
            skLineSegment(sketch, "E615.34", {"start": v(11180, 1050) * mm, "end": v(12580, 1050) * mm});
            skLineSegment(sketch, "E615.35", {"start": v(11180, 3350) * mm, "end": v(11180, 1050) * mm});
            skLineSegment(sketch, "E615.36", {"start": v(12580, 3350) * mm, "end": v(12580, 1050) * mm});
            skLineSegment(sketch, "E615.37", {"start": v(11280, 1050) * mm, "end": v(11280, 3250) * mm});
            skLineSegment(sketch, "E615.38", {"start": v(11280, 3250) * mm, "end": v(12480, 3250) * mm});
            skLineSegment(sketch, "E615.39", {"start": v(12480, 3250) * mm, "end": v(12480, 1050) * mm});
            skLineSegment(sketch, "E615.40", {"start": v(12430, 3200) * mm, "end": v(12430, 1100) * mm});
            skLineSegment(sketch, "E615.41", {"start": v(12430, 3200) * mm, "end": v(11330, 3200) * mm});
            skLineSegment(sketch, "E615.42", {"start": v(11330, 3200) * mm, "end": v(11330, 1100) * mm});
            skLineSegment(sketch, "E615.43", {"start": v(12430, 1100) * mm, "end": v(11330, 1100) * mm});
            skLineSegment(sketch, "E615.44", {"start": v(15410, 3350) * mm, "end": v(16810, 3350) * mm});
            skLineSegment(sketch, "E615.45", {"start": v(15410, 1050) * mm, "end": v(16810, 1050) * mm});
            skLineSegment(sketch, "E615.46", {"start": v(15410, 3350) * mm, "end": v(15410, 1050) * mm});
            skLineSegment(sketch, "E615.47", {"start": v(16810, 3350) * mm, "end": v(16810, 1050) * mm});
            skLineSegment(sketch, "E615.48", {"start": v(15510, 1050) * mm, "end": v(15510, 3250) * mm});
            skLineSegment(sketch, "E615.49", {"start": v(15510, 3250) * mm, "end": v(16710, 3250) * mm});
            skLineSegment(sketch, "E615.50", {"start": v(16710, 3250) * mm, "end": v(16710, 1050) * mm});
            skLineSegment(sketch, "E615.51", {"start": v(16660, 3200) * mm, "end": v(16660, 1100) * mm});
            skLineSegment(sketch, "E615.52", {"start": v(16660, 3200) * mm, "end": v(15560, 3200) * mm});
            skLineSegment(sketch, "E615.53", {"start": v(15560, 3200) * mm, "end": v(15560, 1100) * mm});
            skLineSegment(sketch, "E615.54", {"start": v(16660, 1100) * mm, "end": v(15560, 1100) * mm});
            skLineSegment(sketch, "E615.55", {"start": v(19410, 3350) * mm, "end": v(20810, 3350) * mm});
            skLineSegment(sketch, "E615.56", {"start": v(19410, 1050) * mm, "end": v(20810, 1050) * mm});
            skLineSegment(sketch, "E615.57", {"start": v(19410, 3350) * mm, "end": v(19410, 1050) * mm});
            skLineSegment(sketch, "E615.58", {"start": v(20810, 3350) * mm, "end": v(20810, 1050) * mm});
            skLineSegment(sketch, "E615.59", {"start": v(19510, 1050) * mm, "end": v(19510, 3250) * mm});
            skLineSegment(sketch, "E615.60", {"start": v(19510, 3250) * mm, "end": v(20710, 3250) * mm});
            skLineSegment(sketch, "E615.61", {"start": v(20710, 3250) * mm, "end": v(20710, 1050) * mm});
            skLineSegment(sketch, "E615.62", {"start": v(20660, 3200) * mm, "end": v(20660, 1100) * mm});
            skLineSegment(sketch, "E615.63", {"start": v(20660, 3200) * mm, "end": v(19560, 3200) * mm});
            skLineSegment(sketch, "E615.64", {"start": v(19560, 3200) * mm, "end": v(19560, 1100) * mm});
            skLineSegment(sketch, "E615.65", {"start": v(20660, 1100) * mm, "end": v(19560, 1100) * mm});
            skLineSegment(sketch, "E615.66", {"start": v(23580, 3350) * mm, "end": v(24980, 3350) * mm});
            skLineSegment(sketch, "E615.67", {"start": v(23580, 1050) * mm, "end": v(24980, 1050) * mm});
            skLineSegment(sketch, "E615.68", {"start": v(23580, 3350) * mm, "end": v(23580, 1050) * mm});
            skLineSegment(sketch, "E615.69", {"start": v(24980, 3350) * mm, "end": v(24980, 1050) * mm});
            skLineSegment(sketch, "E615.70", {"start": v(23680, 1050) * mm, "end": v(23680, 3250) * mm});
            skLineSegment(sketch, "E615.71", {"start": v(23680, 3250) * mm, "end": v(24880, 3250) * mm});
            skLineSegment(sketch, "E615.72", {"start": v(24880, 3250) * mm, "end": v(24880, 1050) * mm});
            skLineSegment(sketch, "E615.73", {"start": v(24830, 3200) * mm, "end": v(24830, 1100) * mm});
            skLineSegment(sketch, "E615.74", {"start": v(24830, 3200) * mm, "end": v(23730, 3200) * mm});
            skLineSegment(sketch, "E615.75", {"start": v(23730, 3200) * mm, "end": v(23730, 1100) * mm});
            skLineSegment(sketch, "E615.76", {"start": v(24830, 1100) * mm, "end": v(23730, 1100) * mm});
            skLineSegment(sketch, "E615.77", {"start": v(27160, 0) * mm, "end": v(28260, 0) * mm});
            skLineSegment(sketch, "E615.78", {"start": v(28260, 0) * mm, "end": v(28260, 2400) * mm});
            skLineSegment(sketch, "E615.79", {"start": v(28260, 2400) * mm, "end": v(27160, 2400) * mm});
            skLineSegment(sketch, "E615.80", {"start": v(27160, 2400) * mm, "end": v(27160, 0) * mm});
            skLineSegment(sketch, "E615.81", {"start": v(27010, 2550) * mm, "end": v(28410, 2550) * mm});
            skLineSegment(sketch, "E615.82", {"start": v(27010, 2550) * mm, "end": v(27010, -150) * mm});
            skLineSegment(sketch, "E615.83", {"start": v(28410, 2550) * mm, "end": v(28410, -150) * mm});
            skLineSegment(sketch, "E615.84", {"start": v(27110, -150) * mm, "end": v(27110, 2450) * mm});
            skLineSegment(sketch, "E615.85", {"start": v(27110, 2450) * mm, "end": v(28310, 2450) * mm});
            skLineSegment(sketch, "E615.86", {"start": v(28310, 2450) * mm, "end": v(28310, -150) * mm});
            skLineSegment(sketch, "E615.87", {"start": v(27010, -150) * mm, "end": v(28410, -150) * mm});
            skSolve(sketch);
        }
        {
            var Q0;
            {var subQ3=sQuery(id+"F64.wireOp",EDGE,"E615.4");Q0=makeQuery(id+"F64.imprint","IMPRINT",FACE,{"disambiguationData":[TD([[makeQuery(id+"F64.imprint","IMPRINT",EDGE,{"derivedFrom":subQ3}),1.0]])]});}
            var Q1;
            Q1=makeQuery(id+"F64.imprint","IMPRINT",FACE,{"disambiguationData":[TD([[makeQuery(id+"F64.imprint","IMPRINT",EDGE,{"derivedFrom":sQuery(id+"F64.wireOp",EDGE,"E615.18")}),-1.0]])]});
            var Q2;
            Q2=makeQuery(id+"F64.imprint","IMPRINT",FACE,{"disambiguationData":[TD([[makeQuery(id+"F64.imprint","IMPRINT",EDGE,{"derivedFrom":sQuery(id+"F64.wireOp",EDGE,"E615.33")}),-1.0]])]});
            var Q3;
            Q3=makeQuery(id+"F64.imprint","IMPRINT",FACE,{"disambiguationData":[TD([[makeQuery(id+"F64.imprint","IMPRINT",EDGE,{"derivedFrom":sQuery(id+"F64.wireOp",EDGE,"E615.44")}),-1.0]])]});
            var Q4;
            Q4=makeQuery(id+"F64.imprint","IMPRINT",FACE,{"disambiguationData":[TD([[makeQuery(id+"F64.imprint","IMPRINT",EDGE,{"derivedFrom":sQuery(id+"F64.wireOp",EDGE,"E615.55")}),-1.0]])]});
            var Q5;
            Q5=makeQuery(id+"F64.imprint","IMPRINT",FACE,{"disambiguationData":[TD([[makeQuery(id+"F64.imprint","IMPRINT",EDGE,{"derivedFrom":sQuery(id+"F64.wireOp",EDGE,"E615.66")}),-1.0]])]});
            var Q6;
            Q6=makeQuery(id+"F64.imprint","IMPRINT",FACE,{"disambiguationData":[TD([[makeQuery(id+"F64.imprint","IMPRINT",EDGE,{"derivedFrom":sQuery(id+"F64.wireOp",EDGE,"E615.81")}),-1.0]])]});
            extrude(context, id + "F65", {"entities" : qUnion([Q0, Q1, Q2, Q3, Q4, Q5, Q6]), "operationType" : NewBodyOperationType.ADD, "depth" : 50 * mm, "offsetDistance" : 25 * mm});
        }
        {
            var Q0;
            Q0=makeQuery(id+"F5.boolean.opBoolean","MERGE",FACE,{"derivedFrom":[makeQuery(id+"F3.boolean.opBoolean","COPY",FACE,{"derivedFrom":makeQuery(id+"F3.opExtrude","SWEPT_FACE",FACE,{"disambiguationData":[OSD([sQuery(id+"F2.wireOp",EDGE,"E19.10")])]})}),makeQuery(id+"F5.opExtrude","SWEPT_FACE",FACE,{"disambiguationData":[OSD([sQuery(id+"F4.wireOp",EDGE,"E33.0")])]})]});
            var sketch = newSketch(context, id + "F66", { "sketchPlane" : qUnion([Q0])});
            skPoint(sketch, "E616.26", {"position": v(-24350, 1100) * mm});
            skLineSegment(sketch, "E616.44", {"start": v(-24500, 3350) * mm, "end": v(-23100, 3350) * mm});
            skLineSegment(sketch, "E616.45", {"start": v(-24500, 1050) * mm, "end": v(-23100, 1050) * mm});
            skLineSegment(sketch, "E616.46", {"start": v(-24500, 3350) * mm, "end": v(-24500, 1050) * mm});
            skLineSegment(sketch, "E616.47", {"start": v(-23100, 3350) * mm, "end": v(-23100, 1050) * mm});
            skLineSegment(sketch, "E616.48", {"start": v(-24400, 1050) * mm, "end": v(-24400, 3250) * mm});
            skLineSegment(sketch, "E616.49", {"start": v(-24400, 3250) * mm, "end": v(-23200, 3250) * mm});
            skLineSegment(sketch, "E616.50", {"start": v(-23200, 3250) * mm, "end": v(-23200, 1050) * mm});
            skLineSegment(sketch, "E616.51", {"start": v(-23250, 3200) * mm, "end": v(-23250, 1100) * mm});
            skLineSegment(sketch, "E616.52", {"start": v(-23250, 3200) * mm, "end": v(-24350, 3200) * mm});
            skLineSegment(sketch, "E616.53", {"start": v(-24350, 3200) * mm, "end": v(-24350, 1100) * mm});
            skLineSegment(sketch, "E616.54", {"start": v(-23250, 1100) * mm, "end": v(-24350, 1100) * mm});
            skPoint(sketch, "E617", {"position": v(-21270, 1100) * mm});
            skPoint(sketch, "E618", {"position": v(-18160, 1100) * mm});
            skPoint(sketch, "E619", {"position": v(-15020, 1100) * mm});
            skPoint(sketch, "E620", {"position": v(-11930, 1100) * mm});
            skLineSegment(sketch, "E621.44", {"start": v(-21420, 3350) * mm, "end": v(-20020, 3350) * mm});
            skLineSegment(sketch, "E621.45", {"start": v(-21420, 1050) * mm, "end": v(-20020, 1050) * mm});
            skLineSegment(sketch, "E621.46", {"start": v(-21420, 3350) * mm, "end": v(-21420, 1050) * mm});
            skLineSegment(sketch, "E621.47", {"start": v(-20020, 3350) * mm, "end": v(-20020, 1050) * mm});
            skLineSegment(sketch, "E621.48", {"start": v(-21320, 1050) * mm, "end": v(-21320, 3250) * mm});
            skLineSegment(sketch, "E621.49", {"start": v(-21320, 3250) * mm, "end": v(-20120, 3250) * mm});
            skLineSegment(sketch, "E621.50", {"start": v(-20120, 3250) * mm, "end": v(-20120, 1050) * mm});
            skLineSegment(sketch, "E621.51", {"start": v(-20170, 3200) * mm, "end": v(-20170, 1100) * mm});
            skLineSegment(sketch, "E621.52", {"start": v(-20170, 3200) * mm, "end": v(-21270, 3200) * mm});
            skLineSegment(sketch, "E621.53", {"start": v(-21270, 3200) * mm, "end": v(-21270, 1100) * mm});
            skLineSegment(sketch, "E621.54", {"start": v(-20170, 1100) * mm, "end": v(-21270, 1100) * mm});
            skLineSegment(sketch, "E622.44", {"start": v(-18310, 3350) * mm, "end": v(-16910, 3350) * mm});
            skLineSegment(sketch, "E622.45", {"start": v(-18310, 1050) * mm, "end": v(-16910, 1050) * mm});
            skLineSegment(sketch, "E622.46", {"start": v(-18310, 3350) * mm, "end": v(-18310, 1050) * mm});
            skLineSegment(sketch, "E622.47", {"start": v(-16910, 3350) * mm, "end": v(-16910, 1050) * mm});
            skLineSegment(sketch, "E622.48", {"start": v(-18210, 1050) * mm, "end": v(-18210, 3250) * mm});
            skLineSegment(sketch, "E622.49", {"start": v(-18210, 3250) * mm, "end": v(-17010, 3250) * mm});
            skLineSegment(sketch, "E622.50", {"start": v(-17010, 3250) * mm, "end": v(-17010, 1050) * mm});
            skLineSegment(sketch, "E622.51", {"start": v(-17060, 3200) * mm, "end": v(-17060, 1100) * mm});
            skLineSegment(sketch, "E622.52", {"start": v(-17060, 3200) * mm, "end": v(-18160, 3200) * mm});
            skLineSegment(sketch, "E622.53", {"start": v(-18160, 3200) * mm, "end": v(-18160, 1100) * mm});
            skLineSegment(sketch, "E622.54", {"start": v(-17060, 1100) * mm, "end": v(-18160, 1100) * mm});
            skLineSegment(sketch, "E623.44", {"start": v(-15170, 3350) * mm, "end": v(-13770, 3350) * mm});
            skLineSegment(sketch, "E623.45", {"start": v(-15170, 1050) * mm, "end": v(-13770, 1050) * mm});
            skLineSegment(sketch, "E623.46", {"start": v(-15170, 3350) * mm, "end": v(-15170, 1050) * mm});
            skLineSegment(sketch, "E623.47", {"start": v(-13770, 3350) * mm, "end": v(-13770, 1050) * mm});
            skLineSegment(sketch, "E623.48", {"start": v(-15070, 1050) * mm, "end": v(-15070, 3250) * mm});
            skLineSegment(sketch, "E623.49", {"start": v(-15070, 3250) * mm, "end": v(-13870, 3250) * mm});
            skLineSegment(sketch, "E623.50", {"start": v(-13870, 3250) * mm, "end": v(-13870, 1050) * mm});
            skLineSegment(sketch, "E623.51", {"start": v(-13920, 3200) * mm, "end": v(-13920, 1100) * mm});
            skLineSegment(sketch, "E623.52", {"start": v(-13920, 3200) * mm, "end": v(-15020, 3200) * mm});
            skLineSegment(sketch, "E623.53", {"start": v(-15020, 3200) * mm, "end": v(-15020, 1100) * mm});
            skLineSegment(sketch, "E623.54", {"start": v(-13920, 1100) * mm, "end": v(-15020, 1100) * mm});
            skLineSegment(sketch, "E624.44", {"start": v(-12080, 3350) * mm, "end": v(-10680, 3350) * mm});
            skLineSegment(sketch, "E624.45", {"start": v(-12080, 1050) * mm, "end": v(-10680, 1050) * mm});
            skLineSegment(sketch, "E624.46", {"start": v(-12080, 3350) * mm, "end": v(-12080, 1050) * mm});
            skLineSegment(sketch, "E624.47", {"start": v(-10680, 3350) * mm, "end": v(-10680, 1050) * mm});
            skLineSegment(sketch, "E624.48", {"start": v(-11980, 1050) * mm, "end": v(-11980, 3250) * mm});
            skLineSegment(sketch, "E624.49", {"start": v(-11980, 3250) * mm, "end": v(-10780, 3250) * mm});
            skLineSegment(sketch, "E624.50", {"start": v(-10780, 3250) * mm, "end": v(-10780, 1050) * mm});
            skLineSegment(sketch, "E624.51", {"start": v(-10830, 3200) * mm, "end": v(-10830, 1100) * mm});
            skLineSegment(sketch, "E624.52", {"start": v(-10830, 3200) * mm, "end": v(-11930, 3200) * mm});
            skLineSegment(sketch, "E624.53", {"start": v(-11930, 3200) * mm, "end": v(-11930, 1100) * mm});
            skLineSegment(sketch, "E624.54", {"start": v(-10830, 1100) * mm, "end": v(-11930, 1100) * mm});
            skSolve(sketch);
        }
        {
            var Q0;
            Q0 = qSketchRegion(id + "F66", true);
            extrude(context, id + "F67", {"entities" : qUnion([Q0]), "depth" : 50 * mm, "offsetDistance" : 25 * mm});
        }
        {
            var Q0;
            Q0=makeQuery(id+"F67.opExtrude","CAP_FACE",FACE,{"disambiguationData":[OSD([sQuery(id+"F66.wireOp",EDGE,"E616.44"),sQuery(id+"F66.wireOp",EDGE,"E616.45"),sQuery(id+"F66.wireOp",EDGE,"E616.46"),sQuery(id+"F66.wireOp",EDGE,"E616.47"),sQuery(id+"F66.wireOp",EDGE,"E616.51"),sQuery(id+"F66.wireOp",EDGE,"E616.52"),sQuery(id+"F66.wireOp",EDGE,"E616.53"),sQuery(id+"F66.wireOp",EDGE,"E616.54")])],"isStart":false});
            var sketch = newSketch(context, id + "F68", { "sketchPlane" : qUnion([Q0])});
            skPoint(sketch, "E625.0", {"position": v(-24350, 1100) * mm});
            skLineSegment(sketch, "E625.1", {"start": v(-24500, 3350) * mm, "end": v(-23100, 3350) * mm});
            skLineSegment(sketch, "E625.2", {"start": v(-24500, 1050) * mm, "end": v(-23100, 1050) * mm});
            skLineSegment(sketch, "E625.3", {"start": v(-24500, 3350) * mm, "end": v(-24500, 1050) * mm});
            skLineSegment(sketch, "E625.4", {"start": v(-23100, 3350) * mm, "end": v(-23100, 1050) * mm});
            skLineSegment(sketch, "E625.5", {"start": v(-24400, 1050) * mm, "end": v(-24400, 3250) * mm});
            skLineSegment(sketch, "E625.6", {"start": v(-24400, 3250) * mm, "end": v(-23200, 3250) * mm});
            skLineSegment(sketch, "E625.7", {"start": v(-23200, 3250) * mm, "end": v(-23200, 1050) * mm});
            skLineSegment(sketch, "E625.8", {"start": v(-23250, 3200) * mm, "end": v(-23250, 1100) * mm});
            skLineSegment(sketch, "E625.9", {"start": v(-23250, 3200) * mm, "end": v(-24350, 3200) * mm});
            skLineSegment(sketch, "E625.10", {"start": v(-24350, 3200) * mm, "end": v(-24350, 1100) * mm});
            skLineSegment(sketch, "E625.11", {"start": v(-23250, 1100) * mm, "end": v(-24350, 1100) * mm});
            skPoint(sketch, "E625.12", {"position": v(-21270, 1100) * mm});
            skPoint(sketch, "E625.13", {"position": v(-18160, 1100) * mm});
            skPoint(sketch, "E625.14", {"position": v(-15020, 1100) * mm});
            skPoint(sketch, "E625.15", {"position": v(-11930, 1100) * mm});
            skPoint(sketch, "E625.16", {"position": v(-21270, 1100) * mm});
            skLineSegment(sketch, "E625.17", {"start": v(-21420, 3350) * mm, "end": v(-20020, 3350) * mm});
            skLineSegment(sketch, "E625.18", {"start": v(-21420, 1050) * mm, "end": v(-20020, 1050) * mm});
            skLineSegment(sketch, "E625.19", {"start": v(-21420, 3350) * mm, "end": v(-21420, 1050) * mm});
            skLineSegment(sketch, "E625.20", {"start": v(-20020, 3350) * mm, "end": v(-20020, 1050) * mm});
            skLineSegment(sketch, "E625.21", {"start": v(-21320, 1050) * mm, "end": v(-21320, 3250) * mm});
            skLineSegment(sketch, "E625.22", {"start": v(-21320, 3250) * mm, "end": v(-20120, 3250) * mm});
            skLineSegment(sketch, "E625.23", {"start": v(-20120, 3250) * mm, "end": v(-20120, 1050) * mm});
            skLineSegment(sketch, "E625.24", {"start": v(-20170, 3200) * mm, "end": v(-20170, 1100) * mm});
            skLineSegment(sketch, "E625.25", {"start": v(-20170, 3200) * mm, "end": v(-21270, 3200) * mm});
            skLineSegment(sketch, "E625.26", {"start": v(-21270, 3200) * mm, "end": v(-21270, 1100) * mm});
            skLineSegment(sketch, "E625.27", {"start": v(-20170, 1100) * mm, "end": v(-21270, 1100) * mm});
            skPoint(sketch, "E625.28", {"position": v(-18160, 1100) * mm});
            skLineSegment(sketch, "E625.29", {"start": v(-18310, 3350) * mm, "end": v(-16910, 3350) * mm});
            skLineSegment(sketch, "E625.30", {"start": v(-18310, 1050) * mm, "end": v(-16910, 1050) * mm});
            skLineSegment(sketch, "E625.31", {"start": v(-18310, 3350) * mm, "end": v(-18310, 1050) * mm});
            skLineSegment(sketch, "E625.32", {"start": v(-16910, 3350) * mm, "end": v(-16910, 1050) * mm});
            skLineSegment(sketch, "E625.33", {"start": v(-18210, 1050) * mm, "end": v(-18210, 3250) * mm});
            skLineSegment(sketch, "E625.34", {"start": v(-18210, 3250) * mm, "end": v(-17010, 3250) * mm});
            skLineSegment(sketch, "E625.35", {"start": v(-17010, 3250) * mm, "end": v(-17010, 1050) * mm});
            skLineSegment(sketch, "E625.36", {"start": v(-17060, 3200) * mm, "end": v(-17060, 1100) * mm});
            skLineSegment(sketch, "E625.37", {"start": v(-17060, 3200) * mm, "end": v(-18160, 3200) * mm});
            skLineSegment(sketch, "E625.38", {"start": v(-18160, 3200) * mm, "end": v(-18160, 1100) * mm});
            skLineSegment(sketch, "E625.39", {"start": v(-17060, 1100) * mm, "end": v(-18160, 1100) * mm});
            skPoint(sketch, "E625.40", {"position": v(-15020, 1100) * mm});
            skLineSegment(sketch, "E625.41", {"start": v(-15170, 3350) * mm, "end": v(-13770, 3350) * mm});
            skLineSegment(sketch, "E625.42", {"start": v(-15170, 1050) * mm, "end": v(-13770, 1050) * mm});
            skLineSegment(sketch, "E625.43", {"start": v(-15170, 3350) * mm, "end": v(-15170, 1050) * mm});
            skLineSegment(sketch, "E625.44", {"start": v(-13770, 3350) * mm, "end": v(-13770, 1050) * mm});
            skLineSegment(sketch, "E625.45", {"start": v(-15070, 1050) * mm, "end": v(-15070, 3250) * mm});
            skLineSegment(sketch, "E625.46", {"start": v(-15070, 3250) * mm, "end": v(-13870, 3250) * mm});
            skLineSegment(sketch, "E625.47", {"start": v(-13870, 3250) * mm, "end": v(-13870, 1050) * mm});
            skLineSegment(sketch, "E625.48", {"start": v(-13920, 3200) * mm, "end": v(-13920, 1100) * mm});
            skLineSegment(sketch, "E625.49", {"start": v(-13920, 3200) * mm, "end": v(-15020, 3200) * mm});
            skLineSegment(sketch, "E625.50", {"start": v(-15020, 3200) * mm, "end": v(-15020, 1100) * mm});
            skLineSegment(sketch, "E625.51", {"start": v(-13920, 1100) * mm, "end": v(-15020, 1100) * mm});
            skPoint(sketch, "E625.52", {"position": v(-11930, 1100) * mm});
            skLineSegment(sketch, "E625.53", {"start": v(-12080, 3350) * mm, "end": v(-10680, 3350) * mm});
            skLineSegment(sketch, "E625.54", {"start": v(-12080, 1050) * mm, "end": v(-10680, 1050) * mm});
            skLineSegment(sketch, "E625.55", {"start": v(-12080, 3350) * mm, "end": v(-12080, 1050) * mm});
            skLineSegment(sketch, "E625.56", {"start": v(-10680, 3350) * mm, "end": v(-10680, 1050) * mm});
            skLineSegment(sketch, "E625.57", {"start": v(-11980, 1050) * mm, "end": v(-11980, 3250) * mm});
            skLineSegment(sketch, "E625.58", {"start": v(-11980, 3250) * mm, "end": v(-10780, 3250) * mm});
            skLineSegment(sketch, "E625.59", {"start": v(-10780, 3250) * mm, "end": v(-10780, 1050) * mm});
            skLineSegment(sketch, "E625.60", {"start": v(-10830, 3200) * mm, "end": v(-10830, 1100) * mm});
            skLineSegment(sketch, "E625.61", {"start": v(-10830, 3200) * mm, "end": v(-11930, 3200) * mm});
            skLineSegment(sketch, "E625.62", {"start": v(-11930, 3200) * mm, "end": v(-11930, 1100) * mm});
            skLineSegment(sketch, "E625.63", {"start": v(-10830, 1100) * mm, "end": v(-11930, 1100) * mm});
            skSolve(sketch);
        }
        {
            var Q0;
            Q0=makeQuery(id+"F68.imprint","IMPRINT",FACE,{"disambiguationData":[TD([[makeQuery(id+"F68.imprint","IMPRINT",EDGE,{"derivedFrom":sQuery(id+"F68.wireOp",EDGE,"E625.1")}),-1.0]])]});
            var Q1;
            Q1=makeQuery(id+"F68.imprint","IMPRINT",FACE,{"disambiguationData":[TD([[makeQuery(id+"F68.imprint","IMPRINT",EDGE,{"derivedFrom":sQuery(id+"F68.wireOp",EDGE,"E625.17")}),-1.0]])]});
            var Q2;
            Q2=makeQuery(id+"F68.imprint","IMPRINT",FACE,{"disambiguationData":[TD([[makeQuery(id+"F68.imprint","IMPRINT",EDGE,{"derivedFrom":sQuery(id+"F68.wireOp",EDGE,"E625.29")}),-1.0]])]});
            var Q3;
            Q3=makeQuery(id+"F68.imprint","IMPRINT",FACE,{"disambiguationData":[TD([[makeQuery(id+"F68.imprint","IMPRINT",EDGE,{"derivedFrom":sQuery(id+"F68.wireOp",EDGE,"E625.41")}),-1.0]])]});
            var Q4;
            Q4=makeQuery(id+"F68.imprint","IMPRINT",FACE,{"disambiguationData":[TD([[makeQuery(id+"F68.imprint","IMPRINT",EDGE,{"derivedFrom":sQuery(id+"F68.wireOp",EDGE,"E625.53")}),-1.0]])]});
            extrude(context, id + "F69", {"entities" : qUnion([Q0, Q1, Q2, Q3, Q4]), "operationType" : NewBodyOperationType.ADD, "depth" : 25 * mm, "offsetDistance" : 25 * mm});
        }
        {
            var Q0;
            Q0=makeQuery(id+"F5.boolean.opBoolean","MERGE",FACE,{"derivedFrom":[makeQuery(id+"F3.boolean.opBoolean","COPY",FACE,{"derivedFrom":makeQuery(id+"F3.opExtrude","SWEPT_FACE",FACE,{"disambiguationData":[OSD([sQuery(id+"F2.wireOp",EDGE,"E19.11")])]})}),makeQuery(id+"F5.opExtrude","SWEPT_FACE",FACE,{"disambiguationData":[OSD([sQuery(id+"F4.wireOp",EDGE,"E32.0")])]})]});
            var sketch = newSketch(context, id + "F70", { "sketchPlane" : qUnion([Q0])});
            skPoint(sketch, "E626", {"position": v(-25660, 1100) * mm});
            skPoint(sketch, "E627", {"position": v(-22100, 1100) * mm});
            skPoint(sketch, "E628", {"position": v(-18660, 1200) * mm});
            skPoint(sketch, "E629", {"position": v(-4620, 1200) * mm});
            skLineSegment(sketch, "E630.0", {"start": v(-2920, 3800) * mm, "end": v(-2920, 1200) * mm});
            skLineSegment(sketch, "E630.1", {"start": v(-4620, 3800) * mm, "end": v(-2920, 3800) * mm});
            skLineSegment(sketch, "E630.2", {"start": v(-4620, 3800) * mm, "end": v(-4620, 1200) * mm});
            skLineSegment(sketch, "E630.4", {"start": v(-4670, 3850) * mm, "end": v(-4670, 1150) * mm});
            skLineSegment(sketch, "E630.5", {"start": v(-2870, 3850) * mm, "end": v(-4670, 3850) * mm});
            skLineSegment(sketch, "E630.6", {"start": v(-2770, 1150) * mm, "end": v(-2770, 3950) * mm});
            skLineSegment(sketch, "E630.7", {"start": v(-2770, 1150) * mm, "end": v(-4770, 1150) * mm});
            skLineSegment(sketch, "E630.8", {"start": v(-2770, 3950) * mm, "end": v(-4770, 3950) * mm});
            skLineSegment(sketch, "E630.9", {"start": v(-4770, 3950) * mm, "end": v(-4770, 1150) * mm});
            skLineSegment(sketch, "E630.10", {"start": v(-4620, 1200) * mm, "end": v(-2920, 1200) * mm});
            skLineSegment(sketch, "E630.11", {"start": v(-2870, 1150) * mm, "end": v(-2870, 3850) * mm});
            skLineSegment(sketch, "E630.12", {"start": v(-2770, 3950) * mm, "end": v(-2770, 1150) * mm});
            skLineSegment(sketch, "E630.13", {"start": v(-4770, 3950) * mm, "end": v(-4770, 1150) * mm});
            skLineSegment(sketch, "E630.14", {"start": v(-2770, 3950) * mm, "end": v(-4770, 3950) * mm});
            skLineSegment(sketch, "E630.15", {"start": v(-2870, 1150) * mm, "end": v(-2770, 1150) * mm});
            skLineSegment(sketch, "E630.16", {"start": v(-4770, 1150) * mm, "end": v(-4670, 1150) * mm});
            skLineSegment(sketch, "E630.55", {"start": v(-20850, 3350) * mm, "end": v(-22250, 3350) * mm});
            skLineSegment(sketch, "E630.56", {"start": v(-20850, 1050) * mm, "end": v(-22250, 1050) * mm});
            skLineSegment(sketch, "E630.57", {"start": v(-20850, 3350) * mm, "end": v(-20850, 1050) * mm});
            skLineSegment(sketch, "E630.58", {"start": v(-22250, 3350) * mm, "end": v(-22250, 1050) * mm});
            skLineSegment(sketch, "E630.59", {"start": v(-20950, 1050) * mm, "end": v(-20950, 3250) * mm});
            skLineSegment(sketch, "E630.60", {"start": v(-20950, 3250) * mm, "end": v(-22150, 3250) * mm});
            skLineSegment(sketch, "E630.61", {"start": v(-22150, 3250) * mm, "end": v(-22150, 1050) * mm});
            skLineSegment(sketch, "E630.62", {"start": v(-22100, 3200) * mm, "end": v(-22100, 1100) * mm});
            skLineSegment(sketch, "E630.63", {"start": v(-22100, 3200) * mm, "end": v(-21000, 3200) * mm});
            skLineSegment(sketch, "E630.64", {"start": v(-21000, 3200) * mm, "end": v(-21000, 1100) * mm});
            skLineSegment(sketch, "E630.65", {"start": v(-22100, 1100) * mm, "end": v(-21000, 1100) * mm});
            skLineSegment(sketch, "E630.66", {"start": v(-24410, 3350) * mm, "end": v(-25810, 3350) * mm});
            skLineSegment(sketch, "E630.67", {"start": v(-24410, 1050) * mm, "end": v(-25810, 1050) * mm});
            skLineSegment(sketch, "E630.68", {"start": v(-24410, 3350) * mm, "end": v(-24410, 1050) * mm});
            skLineSegment(sketch, "E630.69", {"start": v(-25810, 3350) * mm, "end": v(-25810, 1050) * mm});
            skLineSegment(sketch, "E630.70", {"start": v(-24510, 1050) * mm, "end": v(-24510, 3250) * mm});
            skLineSegment(sketch, "E630.71", {"start": v(-24510, 3250) * mm, "end": v(-25710, 3250) * mm});
            skLineSegment(sketch, "E630.72", {"start": v(-25710, 3250) * mm, "end": v(-25710, 1050) * mm});
            skLineSegment(sketch, "E630.73", {"start": v(-25660, 3200) * mm, "end": v(-25660, 1100) * mm});
            skLineSegment(sketch, "E630.74", {"start": v(-25660, 3200) * mm, "end": v(-24560, 3200) * mm});
            skLineSegment(sketch, "E630.75", {"start": v(-24560, 3200) * mm, "end": v(-24560, 1100) * mm});
            skLineSegment(sketch, "E630.76", {"start": v(-25660, 1100) * mm, "end": v(-24560, 1100) * mm});
            skLineSegment(sketch, "E630.77", {"start": v(-27260, 0) * mm, "end": v(-28360, 0) * mm});
            skLineSegment(sketch, "E630.78", {"start": v(-28360, 0) * mm, "end": v(-28360, 2400) * mm});
            skLineSegment(sketch, "E630.79", {"start": v(-28360, 2400) * mm, "end": v(-27260, 2400) * mm});
            skLineSegment(sketch, "E630.80", {"start": v(-27260, 2400) * mm, "end": v(-27260, 0) * mm});
            skLineSegment(sketch, "E630.81", {"start": v(-27110, 2550) * mm, "end": v(-28510, 2550) * mm});
            skLineSegment(sketch, "E630.82", {"start": v(-27110, 2550) * mm, "end": v(-27110, -150) * mm});
            skLineSegment(sketch, "E630.83", {"start": v(-28510, 2550) * mm, "end": v(-28510, -150) * mm});
            skLineSegment(sketch, "E630.84", {"start": v(-27210, -150) * mm, "end": v(-27210, 2450) * mm});
            skLineSegment(sketch, "E630.85", {"start": v(-27210, 2450) * mm, "end": v(-28410, 2450) * mm});
            skLineSegment(sketch, "E630.86", {"start": v(-28410, 2450) * mm, "end": v(-28410, -150) * mm});
            skLineSegment(sketch, "E630.87", {"start": v(-27110, -150) * mm, "end": v(-28510, -150) * mm});
            skPoint(sketch, "E631", {"position": v(-28360, 0) * mm});
            skPoint(sketch, "E632", {"position": v(-15860, 1200) * mm});
            skPoint(sketch, "E633", {"position": v(-13060, 1200) * mm});
            skLineSegment(sketch, "E634.0", {"start": v(-16960, 3800) * mm, "end": v(-16960, 1200) * mm});
            skLineSegment(sketch, "E634.1", {"start": v(-18660, 3800) * mm, "end": v(-16960, 3800) * mm});
            skLineSegment(sketch, "E634.2", {"start": v(-18660, 3800) * mm, "end": v(-18660, 1200) * mm});
            skLineSegment(sketch, "E634.4", {"start": v(-18710, 3850) * mm, "end": v(-18710, 1150) * mm});
            skLineSegment(sketch, "E634.5", {"start": v(-16910, 3850) * mm, "end": v(-18710, 3850) * mm});
            skLineSegment(sketch, "E634.6", {"start": v(-16810, 1150) * mm, "end": v(-16810, 3950) * mm});
            skLineSegment(sketch, "E634.7", {"start": v(-16810, 1150) * mm, "end": v(-18810, 1150) * mm});
            skLineSegment(sketch, "E634.8", {"start": v(-16810, 3950) * mm, "end": v(-18810, 3950) * mm});
            skLineSegment(sketch, "E634.9", {"start": v(-18810, 3950) * mm, "end": v(-18810, 1150) * mm});
            skLineSegment(sketch, "E634.10", {"start": v(-18660, 1200) * mm, "end": v(-16960, 1200) * mm});
            skLineSegment(sketch, "E634.11", {"start": v(-16910, 1150) * mm, "end": v(-16910, 3850) * mm});
            skLineSegment(sketch, "E634.12", {"start": v(-16810, 3950) * mm, "end": v(-16810, 1150) * mm});
            skLineSegment(sketch, "E634.13", {"start": v(-18810, 3950) * mm, "end": v(-18810, 1150) * mm});
            skLineSegment(sketch, "E634.14", {"start": v(-16810, 3950) * mm, "end": v(-18810, 3950) * mm});
            skLineSegment(sketch, "E634.15", {"start": v(-16910, 1150) * mm, "end": v(-16810, 1150) * mm});
            skLineSegment(sketch, "E634.16", {"start": v(-18810, 1150) * mm, "end": v(-18710, 1150) * mm});
            skLineSegment(sketch, "E635.0", {"start": v(-14160, 3800) * mm, "end": v(-14160, 1200) * mm});
            skLineSegment(sketch, "E635.1", {"start": v(-15860, 3800) * mm, "end": v(-14160, 3800) * mm});
            skLineSegment(sketch, "E635.2", {"start": v(-15860, 3800) * mm, "end": v(-15860, 1200) * mm});
            skLineSegment(sketch, "E635.4", {"start": v(-15910, 3850) * mm, "end": v(-15910, 1150) * mm});
            skLineSegment(sketch, "E635.5", {"start": v(-14110, 3850) * mm, "end": v(-15910, 3850) * mm});
            skLineSegment(sketch, "E635.6", {"start": v(-14010, 1150) * mm, "end": v(-14010, 3950) * mm});
            skLineSegment(sketch, "E635.7", {"start": v(-14010, 1150) * mm, "end": v(-16010, 1150) * mm});
            skLineSegment(sketch, "E635.8", {"start": v(-14010, 3950) * mm, "end": v(-16010, 3950) * mm});
            skLineSegment(sketch, "E635.9", {"start": v(-16010, 3950) * mm, "end": v(-16010, 1150) * mm});
            skLineSegment(sketch, "E635.10", {"start": v(-15860, 1200) * mm, "end": v(-14160, 1200) * mm});
            skLineSegment(sketch, "E635.11", {"start": v(-14110, 1150) * mm, "end": v(-14110, 3850) * mm});
            skLineSegment(sketch, "E635.12", {"start": v(-14010, 3950) * mm, "end": v(-14010, 1150) * mm});
            skLineSegment(sketch, "E635.13", {"start": v(-16010, 3950) * mm, "end": v(-16010, 1150) * mm});
            skLineSegment(sketch, "E635.14", {"start": v(-14010, 3950) * mm, "end": v(-16010, 3950) * mm});
            skLineSegment(sketch, "E635.15", {"start": v(-14110, 1150) * mm, "end": v(-14010, 1150) * mm});
            skLineSegment(sketch, "E635.16", {"start": v(-16010, 1150) * mm, "end": v(-15910, 1150) * mm});
            skLineSegment(sketch, "E636.0", {"start": v(-11360, 3800) * mm, "end": v(-11360, 1200) * mm});
            skLineSegment(sketch, "E636.1", {"start": v(-13060, 3800) * mm, "end": v(-11360, 3800) * mm});
            skLineSegment(sketch, "E636.2", {"start": v(-13060, 3800) * mm, "end": v(-13060, 1200) * mm});
            skLineSegment(sketch, "E636.4", {"start": v(-13110, 3850) * mm, "end": v(-13110, 1150) * mm});
            skLineSegment(sketch, "E636.5", {"start": v(-11310, 3850) * mm, "end": v(-13110, 3850) * mm});
            skLineSegment(sketch, "E636.6", {"start": v(-11210, 1150) * mm, "end": v(-11210, 3950) * mm});
            skLineSegment(sketch, "E636.7", {"start": v(-11210, 1150) * mm, "end": v(-13210, 1150) * mm});
            skLineSegment(sketch, "E636.8", {"start": v(-11210, 3950) * mm, "end": v(-13210, 3950) * mm});
            skLineSegment(sketch, "E636.9", {"start": v(-13210, 3950) * mm, "end": v(-13210, 1150) * mm});
            skLineSegment(sketch, "E636.10", {"start": v(-13060, 1200) * mm, "end": v(-11360, 1200) * mm});
            skLineSegment(sketch, "E636.11", {"start": v(-11310, 1150) * mm, "end": v(-11310, 3850) * mm});
            skLineSegment(sketch, "E636.12", {"start": v(-11210, 3950) * mm, "end": v(-11210, 1150) * mm});
            skLineSegment(sketch, "E636.13", {"start": v(-13210, 3950) * mm, "end": v(-13210, 1150) * mm});
            skLineSegment(sketch, "E636.14", {"start": v(-11210, 3950) * mm, "end": v(-13210, 3950) * mm});
            skLineSegment(sketch, "E636.15", {"start": v(-11310, 1150) * mm, "end": v(-11210, 1150) * mm});
            skLineSegment(sketch, "E636.16", {"start": v(-13210, 1150) * mm, "end": v(-13110, 1150) * mm});
            skLineSegment(sketch, "E637.bottom", {"start": v(-9180, 3950) * mm, "end": v(-7080, 3950) * mm});
            skLineSegment(sketch, "E637.top", {"start": v(-9180, -150) * mm, "end": v(-7080, -150) * mm});
            skLineSegment(sketch, "E637.left", {"start": v(-9180, 3950) * mm, "end": v(-9180, -150) * mm});
            skLineSegment(sketch, "E637.right", {"start": v(-7080, 3950) * mm, "end": v(-7080, -150) * mm});
            skLineSegment(sketch, "E638", {"start": v(-9080, -150) * mm, "end": v(-9080, 3850) * mm});
            skLineSegment(sketch, "E639", {"start": v(-9080, 3850) * mm, "end": v(-7180, 3850) * mm});
            skLineSegment(sketch, "E640", {"start": v(-7180, 3850) * mm, "end": v(-7180, -150) * mm});
            skLineSegment(sketch, "E641.0.0", {"start": v(-9030, 0) * mm, "end": v(-7230, 0) * mm});
            skLineSegment(sketch, "E641.0.1", {"start": v(-7230, 0) * mm, "end": v(-7230, 3800) * mm});
            skLineSegment(sketch, "E641.0.2", {"start": v(-7230, 3800) * mm, "end": v(-9030, 3800) * mm});
            skLineSegment(sketch, "E641.0.3", {"start": v(-9030, 3800) * mm, "end": v(-9030, 0) * mm});
            skSolve(sketch);
        }
        {
            var Q0;
            Q0 = qSketchRegion(id + "F70", true);
            extrude(context, id + "F71", {"entities" : qUnion([Q0]), "depth" : 25 * mm, "offsetDistance" : 25 * mm});
        }
        {
            var Q0;
            Q0=makeQuery(id+"F71.opExtrude","CAP_FACE",FACE,{"disambiguationData":[OSD([sQuery(id+"F70.wireOp",EDGE,"E630.77"),sQuery(id+"F70.wireOp",EDGE,"E630.78"),sQuery(id+"F70.wireOp",EDGE,"E630.79"),sQuery(id+"F70.wireOp",EDGE,"E630.80"),sQuery(id+"F70.wireOp",EDGE,"E630.81"),sQuery(id+"F70.wireOp",EDGE,"E630.82"),sQuery(id+"F70.wireOp",EDGE,"E630.83"),sQuery(id+"F70.wireOp",EDGE,"E630.87")])],"isStart":false});
            var sketch = newSketch(context, id + "F72", { "sketchPlane" : qUnion([Q0])});
            skPoint(sketch, "E642.0", {"position": v(-25660, 1100) * mm});
            skPoint(sketch, "E642.1", {"position": v(-22100, 1100) * mm});
            skPoint(sketch, "E642.2", {"position": v(-18660, 1200) * mm});
            skPoint(sketch, "E642.3", {"position": v(-4620, 1200) * mm});
            skLineSegment(sketch, "E642.4", {"start": v(-2920, 3800) * mm, "end": v(-2920, 1200) * mm});
            skLineSegment(sketch, "E642.5", {"start": v(-4620, 3800) * mm, "end": v(-2920, 3800) * mm});
            skLineSegment(sketch, "E642.6", {"start": v(-4620, 3800) * mm, "end": v(-4620, 1200) * mm});
            skLineSegment(sketch, "E642.7", {"start": v(-4670, 3850) * mm, "end": v(-4670, 1150) * mm});
            skLineSegment(sketch, "E642.8", {"start": v(-2870, 3850) * mm, "end": v(-4670, 3850) * mm});
            skLineSegment(sketch, "E642.9", {"start": v(-2770, 1150) * mm, "end": v(-2770, 3950) * mm});
            skLineSegment(sketch, "E642.10", {"start": v(-2770, 1150) * mm, "end": v(-4770, 1150) * mm});
            skLineSegment(sketch, "E642.11", {"start": v(-2770, 3950) * mm, "end": v(-4770, 3950) * mm});
            skLineSegment(sketch, "E642.12", {"start": v(-4770, 3950) * mm, "end": v(-4770, 1150) * mm});
            skLineSegment(sketch, "E642.13", {"start": v(-4620, 1200) * mm, "end": v(-2920, 1200) * mm});
            skLineSegment(sketch, "E642.14", {"start": v(-2870, 1150) * mm, "end": v(-2870, 3850) * mm});
            skLineSegment(sketch, "E642.15", {"start": v(-2770, 3950) * mm, "end": v(-2770, 1150) * mm});
            skLineSegment(sketch, "E642.16", {"start": v(-4770, 3950) * mm, "end": v(-4770, 1150) * mm});
            skLineSegment(sketch, "E642.17", {"start": v(-2770, 3950) * mm, "end": v(-4770, 3950) * mm});
            skLineSegment(sketch, "E642.18", {"start": v(-2870, 1150) * mm, "end": v(-2770, 1150) * mm});
            skLineSegment(sketch, "E642.19", {"start": v(-4770, 1150) * mm, "end": v(-4670, 1150) * mm});
            skLineSegment(sketch, "E642.20", {"start": v(-20850, 3350) * mm, "end": v(-22250, 3350) * mm});
            skLineSegment(sketch, "E642.21", {"start": v(-20850, 1050) * mm, "end": v(-22250, 1050) * mm});
            skLineSegment(sketch, "E642.22", {"start": v(-20850, 3350) * mm, "end": v(-20850, 1050) * mm});
            skLineSegment(sketch, "E642.23", {"start": v(-22250, 3350) * mm, "end": v(-22250, 1050) * mm});
            skLineSegment(sketch, "E642.24", {"start": v(-20950, 1050) * mm, "end": v(-20950, 3250) * mm});
            skLineSegment(sketch, "E642.25", {"start": v(-20950, 3250) * mm, "end": v(-22150, 3250) * mm});
            skLineSegment(sketch, "E642.26", {"start": v(-22150, 3250) * mm, "end": v(-22150, 1050) * mm});
            skLineSegment(sketch, "E642.27", {"start": v(-22100, 3200) * mm, "end": v(-22100, 1100) * mm});
            skLineSegment(sketch, "E642.28", {"start": v(-22100, 3200) * mm, "end": v(-21000, 3200) * mm});
            skLineSegment(sketch, "E642.29", {"start": v(-21000, 3200) * mm, "end": v(-21000, 1100) * mm});
            skLineSegment(sketch, "E642.30", {"start": v(-22100, 1100) * mm, "end": v(-21000, 1100) * mm});
            skLineSegment(sketch, "E642.31", {"start": v(-24410, 3350) * mm, "end": v(-25810, 3350) * mm});
            skLineSegment(sketch, "E642.32", {"start": v(-24410, 1050) * mm, "end": v(-25810, 1050) * mm});
            skLineSegment(sketch, "E642.33", {"start": v(-24410, 3350) * mm, "end": v(-24410, 1050) * mm});
            skLineSegment(sketch, "E642.34", {"start": v(-25810, 3350) * mm, "end": v(-25810, 1050) * mm});
            skLineSegment(sketch, "E642.35", {"start": v(-24510, 1050) * mm, "end": v(-24510, 3250) * mm});
            skLineSegment(sketch, "E642.36", {"start": v(-24510, 3250) * mm, "end": v(-25710, 3250) * mm});
            skLineSegment(sketch, "E642.37", {"start": v(-25710, 3250) * mm, "end": v(-25710, 1050) * mm});
            skLineSegment(sketch, "E642.38", {"start": v(-25660, 3200) * mm, "end": v(-25660, 1100) * mm});
            skLineSegment(sketch, "E642.39", {"start": v(-25660, 3200) * mm, "end": v(-24560, 3200) * mm});
            skLineSegment(sketch, "E642.40", {"start": v(-24560, 3200) * mm, "end": v(-24560, 1100) * mm});
            skLineSegment(sketch, "E642.41", {"start": v(-25660, 1100) * mm, "end": v(-24560, 1100) * mm});
            skLineSegment(sketch, "E642.42", {"start": v(-27260, 0) * mm, "end": v(-28360, 0) * mm});
            skLineSegment(sketch, "E642.43", {"start": v(-28360, 0) * mm, "end": v(-28360, 2400) * mm});
            skLineSegment(sketch, "E642.44", {"start": v(-28360, 2400) * mm, "end": v(-27260, 2400) * mm});
            skLineSegment(sketch, "E642.45", {"start": v(-27260, 2400) * mm, "end": v(-27260, 0) * mm});
            skLineSegment(sketch, "E642.46", {"start": v(-27110, 2550) * mm, "end": v(-28510, 2550) * mm});
            skLineSegment(sketch, "E642.47", {"start": v(-27110, 2550) * mm, "end": v(-27110, -150) * mm});
            skLineSegment(sketch, "E642.48", {"start": v(-28510, 2550) * mm, "end": v(-28510, -150) * mm});
            skLineSegment(sketch, "E642.49", {"start": v(-27210, -150) * mm, "end": v(-27210, 2450) * mm});
            skLineSegment(sketch, "E642.50", {"start": v(-27210, 2450) * mm, "end": v(-28410, 2450) * mm});
            skLineSegment(sketch, "E642.51", {"start": v(-28410, 2450) * mm, "end": v(-28410, -150) * mm});
            skLineSegment(sketch, "E642.52", {"start": v(-27110, -150) * mm, "end": v(-28510, -150) * mm});
            skPoint(sketch, "E642.53", {"position": v(-28360, 0) * mm});
            skPoint(sketch, "E642.54", {"position": v(-15860, 1200) * mm});
            skPoint(sketch, "E642.55", {"position": v(-13060, 1200) * mm});
            skLineSegment(sketch, "E642.56", {"start": v(-16960, 3800) * mm, "end": v(-16960, 1200) * mm});
            skLineSegment(sketch, "E642.57", {"start": v(-18660, 3800) * mm, "end": v(-16960, 3800) * mm});
            skLineSegment(sketch, "E642.58", {"start": v(-18660, 3800) * mm, "end": v(-18660, 1200) * mm});
            skLineSegment(sketch, "E642.59", {"start": v(-18710, 3850) * mm, "end": v(-18710, 1150) * mm});
            skLineSegment(sketch, "E642.60", {"start": v(-16910, 3850) * mm, "end": v(-18710, 3850) * mm});
            skLineSegment(sketch, "E642.61", {"start": v(-16810, 1150) * mm, "end": v(-16810, 3950) * mm});
            skLineSegment(sketch, "E642.62", {"start": v(-16810, 1150) * mm, "end": v(-18810, 1150) * mm});
            skLineSegment(sketch, "E642.63", {"start": v(-16810, 3950) * mm, "end": v(-18810, 3950) * mm});
            skLineSegment(sketch, "E642.64", {"start": v(-18810, 3950) * mm, "end": v(-18810, 1150) * mm});
            skLineSegment(sketch, "E642.65", {"start": v(-18660, 1200) * mm, "end": v(-16960, 1200) * mm});
            skLineSegment(sketch, "E642.66", {"start": v(-16910, 1150) * mm, "end": v(-16910, 3850) * mm});
            skLineSegment(sketch, "E642.67", {"start": v(-16810, 3950) * mm, "end": v(-16810, 1150) * mm});
            skLineSegment(sketch, "E642.68", {"start": v(-18810, 3950) * mm, "end": v(-18810, 1150) * mm});
            skLineSegment(sketch, "E642.69", {"start": v(-16810, 3950) * mm, "end": v(-18810, 3950) * mm});
            skLineSegment(sketch, "E642.70", {"start": v(-16910, 1150) * mm, "end": v(-16810, 1150) * mm});
            skLineSegment(sketch, "E642.71", {"start": v(-18810, 1150) * mm, "end": v(-18710, 1150) * mm});
            skLineSegment(sketch, "E642.72", {"start": v(-14160, 3800) * mm, "end": v(-14160, 1200) * mm});
            skLineSegment(sketch, "E642.73", {"start": v(-15860, 3800) * mm, "end": v(-14160, 3800) * mm});
            skLineSegment(sketch, "E642.74", {"start": v(-15860, 3800) * mm, "end": v(-15860, 1200) * mm});
            skLineSegment(sketch, "E642.75", {"start": v(-15910, 3850) * mm, "end": v(-15910, 1150) * mm});
            skLineSegment(sketch, "E642.76", {"start": v(-14110, 3850) * mm, "end": v(-15910, 3850) * mm});
            skLineSegment(sketch, "E642.77", {"start": v(-14010, 1150) * mm, "end": v(-14010, 3950) * mm});
            skLineSegment(sketch, "E642.78", {"start": v(-14010, 1150) * mm, "end": v(-16010, 1150) * mm});
            skLineSegment(sketch, "E642.79", {"start": v(-14010, 3950) * mm, "end": v(-16010, 3950) * mm});
            skLineSegment(sketch, "E642.80", {"start": v(-16010, 3950) * mm, "end": v(-16010, 1150) * mm});
            skLineSegment(sketch, "E642.81", {"start": v(-15860, 1200) * mm, "end": v(-14160, 1200) * mm});
            skLineSegment(sketch, "E642.82", {"start": v(-14110, 1150) * mm, "end": v(-14110, 3850) * mm});
            skLineSegment(sketch, "E642.83", {"start": v(-14010, 3950) * mm, "end": v(-14010, 1150) * mm});
            skLineSegment(sketch, "E642.84", {"start": v(-16010, 3950) * mm, "end": v(-16010, 1150) * mm});
            skLineSegment(sketch, "E642.85", {"start": v(-14010, 3950) * mm, "end": v(-16010, 3950) * mm});
            skLineSegment(sketch, "E642.86", {"start": v(-14110, 1150) * mm, "end": v(-14010, 1150) * mm});
            skLineSegment(sketch, "E642.87", {"start": v(-16010, 1150) * mm, "end": v(-15910, 1150) * mm});
            skLineSegment(sketch, "E642.88", {"start": v(-11360, 3800) * mm, "end": v(-11360, 1200) * mm});
            skLineSegment(sketch, "E642.89", {"start": v(-13060, 3800) * mm, "end": v(-11360, 3800) * mm});
            skLineSegment(sketch, "E642.90", {"start": v(-13060, 3800) * mm, "end": v(-13060, 1200) * mm});
            skLineSegment(sketch, "E642.91", {"start": v(-13110, 3850) * mm, "end": v(-13110, 1150) * mm});
            skLineSegment(sketch, "E642.92", {"start": v(-11310, 3850) * mm, "end": v(-13110, 3850) * mm});
            skLineSegment(sketch, "E642.93", {"start": v(-11210, 1150) * mm, "end": v(-11210, 3950) * mm});
            skLineSegment(sketch, "E642.94", {"start": v(-11210, 1150) * mm, "end": v(-13210, 1150) * mm});
            skLineSegment(sketch, "E642.95", {"start": v(-11210, 3950) * mm, "end": v(-13210, 3950) * mm});
            skLineSegment(sketch, "E642.96", {"start": v(-13210, 3950) * mm, "end": v(-13210, 1150) * mm});
            skLineSegment(sketch, "E642.97", {"start": v(-13060, 1200) * mm, "end": v(-11360, 1200) * mm});
            skLineSegment(sketch, "E642.98", {"start": v(-11310, 1150) * mm, "end": v(-11310, 3850) * mm});
            skLineSegment(sketch, "E642.99", {"start": v(-11210, 3950) * mm, "end": v(-11210, 1150) * mm});
            skLineSegment(sketch, "E642.100", {"start": v(-13210, 3950) * mm, "end": v(-13210, 1150) * mm});
            skLineSegment(sketch, "E642.101", {"start": v(-11210, 3950) * mm, "end": v(-13210, 3950) * mm});
            skLineSegment(sketch, "E642.102", {"start": v(-11310, 1150) * mm, "end": v(-11210, 1150) * mm});
            skLineSegment(sketch, "E642.103", {"start": v(-13210, 1150) * mm, "end": v(-13110, 1150) * mm});
            skLineSegment(sketch, "E642.104", {"start": v(-9180, 3950) * mm, "end": v(-7080, 3950) * mm});
            skLineSegment(sketch, "E642.105", {"start": v(-9180, -150) * mm, "end": v(-7080, -150) * mm});
            skLineSegment(sketch, "E642.106", {"start": v(-9180, 3950) * mm, "end": v(-9180, -150) * mm});
            skLineSegment(sketch, "E642.107", {"start": v(-7080, 3950) * mm, "end": v(-7080, -150) * mm});
            skLineSegment(sketch, "E642.108", {"start": v(-9080, -150) * mm, "end": v(-9080, 3850) * mm});
            skLineSegment(sketch, "E642.109", {"start": v(-9080, 3850) * mm, "end": v(-7180, 3850) * mm});
            skLineSegment(sketch, "E642.110", {"start": v(-7180, 3850) * mm, "end": v(-7180, -150) * mm});
            skLineSegment(sketch, "E642.111", {"start": v(-9030, 0) * mm, "end": v(-7230, 0) * mm});
            skLineSegment(sketch, "E642.112", {"start": v(-7230, 0) * mm, "end": v(-7230, 3800) * mm});
            skLineSegment(sketch, "E642.113", {"start": v(-7230, 3800) * mm, "end": v(-9030, 3800) * mm});
            skLineSegment(sketch, "E642.114", {"start": v(-9030, 3800) * mm, "end": v(-9030, 0) * mm});
            skSolve(sketch);
        }
        {
            var Q0;
            Q0=makeQuery(id+"F72.imprint","IMPRINT",FACE,{"disambiguationData":[TD([[makeQuery(id+"F72.imprint","IMPRINT",EDGE,{"derivedFrom":sQuery(id+"F72.wireOp",EDGE,"E642.46")}),1.0]])]});
            var Q1;
            Q1=makeQuery(id+"F72.imprint","IMPRINT",FACE,{"disambiguationData":[TD([[makeQuery(id+"F72.imprint","IMPRINT",EDGE,{"derivedFrom":sQuery(id+"F72.wireOp",EDGE,"E642.31")}),1.0]])]});
            var Q2;
            Q2=makeQuery(id+"F72.imprint","IMPRINT",FACE,{"disambiguationData":[TD([[makeQuery(id+"F72.imprint","IMPRINT",EDGE,{"derivedFrom":sQuery(id+"F72.wireOp",EDGE,"E642.20")}),1.0]])]});
            var Q3;
            {var subQ3=sQuery(id+"F72.wireOp",EDGE,"E642.59");Q3=makeQuery(id+"F72.imprint","IMPRINT",FACE,{"disambiguationData":[TD([[makeQuery(id+"F72.imprint","IMPRINT",EDGE,{"derivedFrom":subQ3}),-1.0]])]});}
            var Q4;
            {var subQ3=sQuery(id+"F72.wireOp",EDGE,"E642.75");Q4=makeQuery(id+"F72.imprint","IMPRINT",FACE,{"disambiguationData":[TD([[makeQuery(id+"F72.imprint","IMPRINT",EDGE,{"derivedFrom":subQ3}),-1.0]])]});}
            var Q5;
            {var subQ3=sQuery(id+"F72.wireOp",EDGE,"E642.91");Q5=makeQuery(id+"F72.imprint","IMPRINT",FACE,{"disambiguationData":[TD([[makeQuery(id+"F72.imprint","IMPRINT",EDGE,{"derivedFrom":subQ3}),-1.0]])]});}
            var Q6;
            Q6=makeQuery(id+"F72.imprint","IMPRINT",FACE,{"disambiguationData":[TD([[makeQuery(id+"F72.imprint","IMPRINT",EDGE,{"derivedFrom":sQuery(id+"F72.wireOp",EDGE,"E642.104")}),-1.0]])]});
            var Q7;
            {var subQ3=sQuery(id+"F72.wireOp",EDGE,"E642.7");Q7=makeQuery(id+"F72.imprint","IMPRINT",FACE,{"disambiguationData":[TD([[makeQuery(id+"F72.imprint","IMPRINT",EDGE,{"derivedFrom":subQ3}),-1.0]])]});}
            extrude(context, id + "F73", {"entities" : qUnion([Q0, Q1, Q2, Q3, Q4, Q5, Q6, Q7]), "operationType" : NewBodyOperationType.ADD, "depth" : 50 * mm, "offsetDistance" : 25 * mm});
        }
    });
